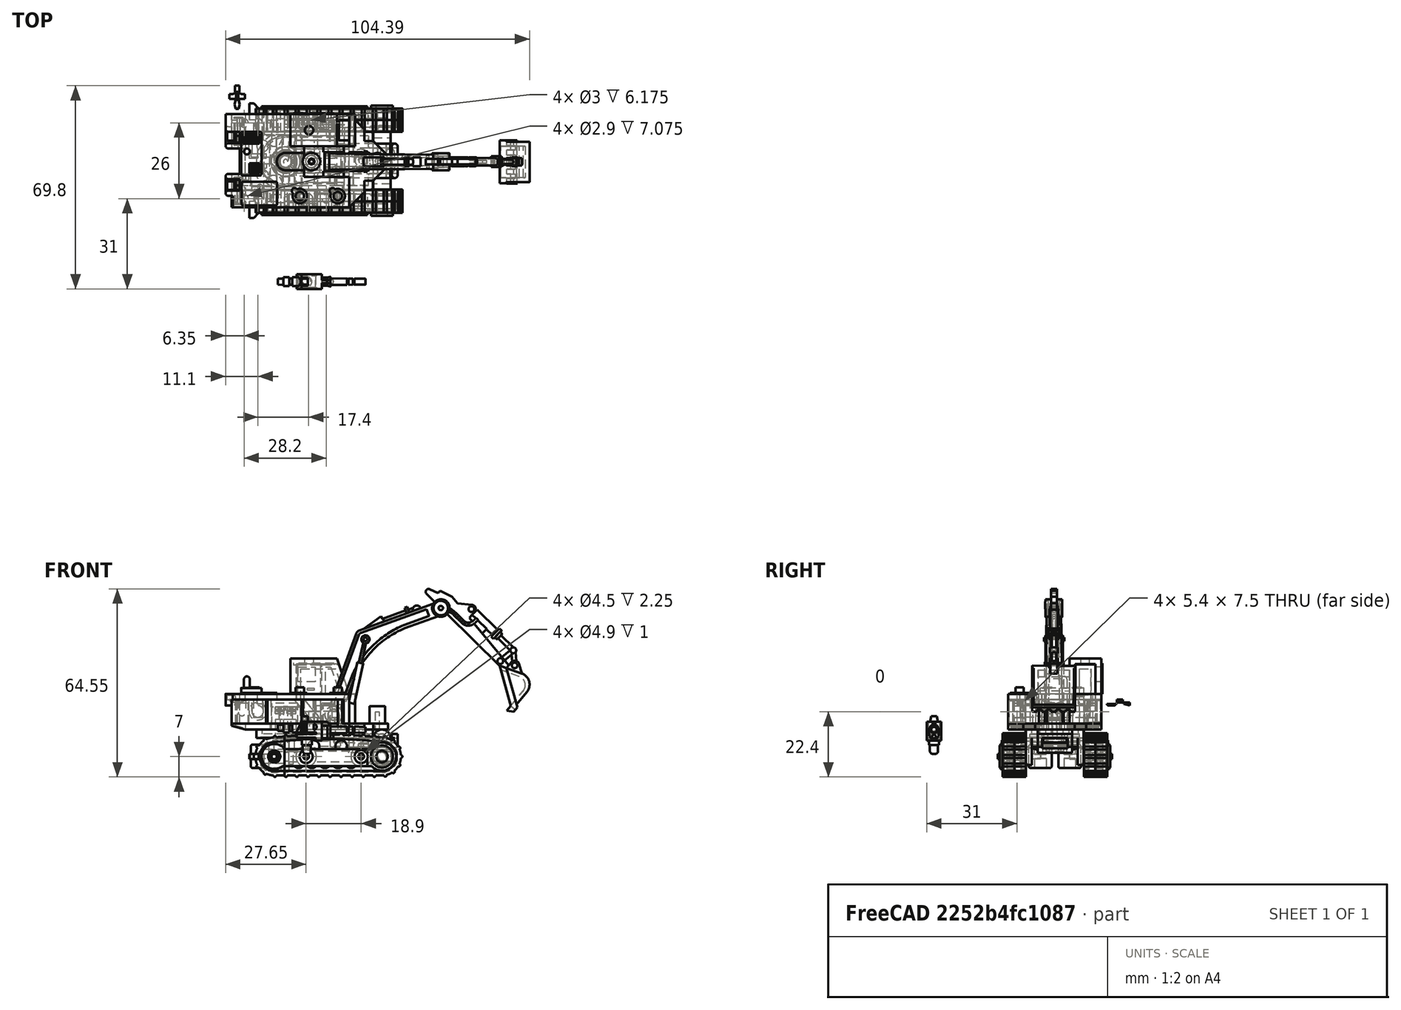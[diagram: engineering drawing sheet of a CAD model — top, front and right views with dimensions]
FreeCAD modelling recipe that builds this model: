
FCSTD DOCUMENT  (FreeCAD 1.0R39109 (Git))
Label: Scavanger
License: All rights reserved
LicenseURL: https://en.wikipedia.org/wiki/All_rights_reserved
objects: Sketcher::SketchObject×284, PartDesign::Pad×196, PartDesign::Pocket×128, PartDesign::Body×18, PartDesign::Fillet×15, PartDesign::SubShapeBinder×11, PartDesign::Chamfer×8, App::Link×5, Part::Mirroring×5, App::Part×1, Part::Feature×1
note: 1644 computed .brp shape members not serialized (recipe doc carries the construction recipe); baked Part::Feature solids carry a one-line shape summary decoded from their .brp

FEATURE [Sketcher::SketchObject] Sketch
  ArcFitTolerance = 1e-06
  AttachmentSupport = -> [XY_Plane]
  FullyConstrained = true
  MakeInternals = false
  MapMode = 5
  sketch-geometry (43):
    g0: LineSegment StartX=0 StartY=0 StartZ=0 EndX=44.5 EndY=0 EndZ=0
    g1: LineSegment StartX=44.5 StartY=0 StartZ=0 EndX=44.5 EndY=-11 EndZ=0
    g2: LineSegment StartX=44.5 StartY=-11 StartZ=0 EndX=27 EndY=-11 EndZ=0
    g3: LineSegment StartX=27 StartY=-11 StartZ=0 EndX=27 EndY=-13.25 EndZ=0
    g4: LineSegment StartX=27 StartY=-13.25 StartZ=0 EndX=20.6 EndY=-13.25 EndZ=0
    g5: ArcOfCircle CenterX=20.6 CenterY=-16.25 CenterZ=0 NormalX=0 NormalY=0 NormalZ=1 AngleXU=0 Radius=3 StartAngle=1.5708 EndAngle=4.71239
    g6: LineSegment StartX=20.6 StartY=-19.25 StartZ=0 EndX=27 EndY=-19.25 EndZ=0
    g7: LineSegment StartX=27 StartY=-19.25 StartZ=0 EndX=27 EndY=-21.5 EndZ=0
    g8: LineSegment StartX=27 StartY=-21.5 StartZ=0 EndX=42.5 EndY=-21.5 EndZ=0
    g9: LineSegment StartX=42.5 StartY=-21.5 StartZ=0 EndX=42.5 EndY=-32 EndZ=0
    g10: LineSegment StartX=42.5 StartY=-32 StartZ=0 EndX=2.5 EndY=-32 EndZ=0
    g11: LineSegment StartX=2.5 StartY=-32 StartZ=0 EndX=2.5 EndY=-28 EndZ=0
    g12: LineSegment StartX=2.5 StartY=-28 StartZ=0 EndX=0.875 EndY=-28 EndZ=0
    g13: ArcOfCircle CenterX=0.875 CenterY=-27.125 CenterZ=0 NormalX=0 NormalY=0 NormalZ=1 AngleXU=0 Radius=0.875 StartAngle=1.5708 EndAngle=4.71239
    g14: LineSegment StartX=0.875 StartY=-26.25 StartZ=0 EndX=4.8 EndY=-26.25 EndZ=0
    g15: LineSegment StartX=4.8 StartY=-26.25 StartZ=0 EndX=4.8 EndY=-22.25 EndZ=0
    g16: LineSegment StartX=4.8 StartY=-22.25 StartZ=0 EndX=0.875 EndY=-22.25 EndZ=0
    g17: ArcOfCircle CenterX=0.875 CenterY=-21.375 CenterZ=0 NormalX=0 NormalY=0 NormalZ=1 AngleXU=0 Radius=0.875 StartAngle=1.5708 EndAngle=4.71239
    g18: LineSegment StartX=0.875 StartY=-20.5 StartZ=0 EndX=4.8 EndY=-20.5 EndZ=0
    g19: LineSegment StartX=4.8 StartY=-20.5 StartZ=0 EndX=4.8 EndY=-11.75 EndZ=0
    g20: LineSegment StartX=4.8 StartY=-11.75 StartZ=0 EndX=0.875 EndY=-11.75 EndZ=0
    g21: ArcOfCircle CenterX=0.875 CenterY=-10.875 CenterZ=0 NormalX=0 NormalY=0 NormalZ=1 AngleXU=0 Radius=0.875 StartAngle=1.5708 EndAngle=4.71239
    g22: LineSegment StartX=0.875 StartY=-10 StartZ=0 EndX=4.8 EndY=-10 EndZ=0
    g23: LineSegment StartX=4.8 StartY=-10 StartZ=0 EndX=4.8 EndY=-6 EndZ=0
    g24: LineSegment StartX=4.8 StartY=-6 StartZ=0 EndX=0.875 EndY=-6 EndZ=0
    g25: ArcOfCircle CenterX=0.875 CenterY=-5.125 CenterZ=0 NormalX=0 NormalY=0 NormalZ=1 AngleXU=0 Radius=0.875 StartAngle=3.14159 EndAngle=4.71239
    g26: LineSegment StartX=0 StartY=0 StartZ=0 EndX=0 EndY=-5.125 EndZ=0
    g27: LineSegment [constr] StartX=0.875 StartY=-10 StartZ=0 EndX=0.875 EndY=-10.875 EndZ=0
    g28: LineSegment [constr] StartX=0.875 StartY=-10.875 StartZ=0 EndX=0.875 EndY=-11.75 EndZ=0
    g29: LineSegment [constr] StartX=0.875 StartY=-20.5 StartZ=0 EndX=0.875 EndY=-21.375 EndZ=0
    g30: LineSegment [constr] StartX=0.875 StartY=-21.375 StartZ=0 EndX=0.875 EndY=-22.25 EndZ=0
    g31: LineSegment [constr] StartX=0.875 StartY=-26.25 StartZ=0 EndX=0.875 EndY=-27.125 EndZ=0
    g32: LineSegment [constr] StartX=0.875 StartY=-27.125 StartZ=0 EndX=0.875 EndY=-28 EndZ=0
    g33: LineSegment [constr] StartX=27 StartY=-13.25 StartZ=0 EndX=27 EndY=-19.25 EndZ=0
    g34: LineSegment [constr] StartX=20.6 StartY=-13.25 StartZ=0 EndX=17.6 EndY=-13.25 EndZ=0
    g35: LineSegment [constr] StartX=17.6 StartY=-13.25 StartZ=0 EndX=17.6 EndY=-16.25 EndZ=0
    g36: LineSegment [constr] StartX=20.6 StartY=-13.25 StartZ=0 EndX=20.6 EndY=-19.25 EndZ=0
    g37: LineSegment [constr] StartX=4.8 StartY=-10 StartZ=0 EndX=4.8 EndY=-11.75 EndZ=0
    g38: LineSegment [constr] StartX=4.8 StartY=-20.5 StartZ=0 EndX=4.8 EndY=-22.25 EndZ=0
    g39: LineSegment StartX=42.5 StartY=-2 StartZ=0 EndX=24.3 EndY=-2 EndZ=0
    g40: LineSegment StartX=24.3 StartY=-2 StartZ=0 EndX=24.3 EndY=-9 EndZ=0
    g41: LineSegment StartX=24.3 StartY=-9 StartZ=0 EndX=42.5 EndY=-9 EndZ=0
    g42: LineSegment StartX=42.5 StartY=-9 StartZ=0 EndX=42.5 EndY=-2 EndZ=0
  constraints (123):
    c: Coincident(g0,g-1)
    c: PointOnObject(g0,g-1)
    c: Coincident(g1,g0)
    c: Vertical(g1)
    c: DistanceX(g0,g0) = 44.5
    c: Coincident(g2,g1)
    c: Horizontal(g2)
    c: Coincident(g3,g2)
    c: Vertical(g3)
    c: Coincident(g4,g3)
    c: Horizontal(g4)
    c: Coincident(g5,g4)
    c: Coincident(g6,g5)
    c: Horizontal(g6)
    c: Coincident(g7,g6)
    c: Vertical(g7)
    c: Coincident(g8,g7)
    c: Horizontal(g8)
    c: Coincident(g9,g8)
    c: Vertical(g9)
    c: Coincident(g10,g9)
    c: Horizontal(g10)
    c: Coincident(g11,g10)
    c: Vertical(g11)
    c: Coincident(g12,g11)
    c: Horizontal(g12)
    c: Coincident(g13,g12)
    c: Coincident(g14,g13)
    c: Coincident(g15,g14)
    c: Vertical(g15)
    c: Coincident(g16,g15)
    c: Horizontal(g16)
    c: Coincident(g17,g16)
    c: Coincident(g18,g17)
    c: Horizontal(g18)
    c: Coincident(g19,g18)
    c: Vertical(g19)
    c: Coincident(g20,g19)
    c: Horizontal(g20)
    c: Coincident(g21,g20)
    c: Coincident(g22,g21)
    c: Horizontal(g22)
    c: Coincident(g23,g22)
    c: Vertical(g23)
    c: Coincident(g24,g23)
    c: Horizontal(g24)
    c: Coincident(g25,g24)
    c: PointOnObject(g25,g-2)
    c: Coincident(g26,g0)
    c: Coincident(g26,g25)
    c: DistanceY(g1,g1) = 11
    c: Horizontal(g14)
    c: DistanceX(g10,g10) = 40
    c: Diameter(g5) = 6
    c: Diameter(g17) = 1.75
    c: Diameter(g21) = 1.75
    c: Diameter(g13) = 1.75
    c: Tangent(g17,g-2)
    c: Tangent(g21,g-2)
    c: Diameter(g25) = 1.75
    c: DistanceX(g25,g24) = 0
    c: DistanceY(g25,g25) = 0
    c: Coincident(g27,g21)
    c: Coincident(g27,g21)
    c: Coincident(g28,g21)
    c: Coincident(g28,g20)
    c: Vertical(g27)
    c: Vertical(g28)
    c: Tangent(g13,g-2)
    c: Coincident(g29,g17)
    c: Coincident(g29,g17)
    c: Coincident(g30,g17)
    c: Coincident(g30,g16)
    c: Coincident(g31,g13)
    c: Coincident(g31,g13)
    c: Coincident(g32,g13)
    c: Coincident(g32,g12)
    c: Vertical(g29)
    c: Vertical(g30)
    c: Vertical(g31)
    c: Vertical(g32)
    c: DistanceX(g2,g2) = 17.5
    c: DistanceY(g7,g2) = 10.5
    c: Coincident(g33,g3)
    c: Coincident(g33,g6)
    c: Vertical(g33)
    c: DistanceY(g3,g2) = 2.25
    c: Coincident(g34,g4)
    c: Horizontal(g34)
    c: Tangent(g34,g5)
    c: Coincident(g35,g34)
    c: Tangent(g35,g5) = -1.5708
    c: Vertical(g35)
    c: Coincident(g36,g4)
    c: Coincident(g36,g5)
    c: Vertical(g36)
    c: DistanceX(g35,g1) = 26.9
    c: DistanceX(g8,g8) = 15.5
    c: DistanceY(g9,g9) = 10.5
    c: DistanceY(g11,g11) = 4
    c: Coincident(g37,g22)
    c: Coincident(g37,g19)
    c: Vertical(g37)
    c: Coincident(g38,g18)
    c: Coincident(g38,g15)
    c: Vertical(g38)
    c: DistanceY(g24,g0) = 6
    c: DistanceY(g23,g23) = 4
    c: DistanceY(g15,g15) = 4
    c: DistanceX(g25,g23) = 4.8
    c: DistanceX(g19,g35) = 12.8
    c: Coincident(g39,g40)
    c: Coincident(g40,g41)
    c: Coincident(g41,g42)
    c: Coincident(g42,g39)
    c: Horizontal(g39)
    c: Horizontal(g41)
    c: Vertical(g40)
    c: Vertical(g42)
    c: DistanceX(g39,g0) = 2
    c: DistanceY(g39,g0) = 2
    c: DistanceY(g1,g41) = 2
    c: DistanceX(g39,g39) = 18.2
FEATURE [PartDesign::Pad] Pad
  Direction = (0,0,1)
  Length = 2
  Length2 = 10
  Profile = -> Sketch
  ReferenceAxis = -> Sketch [N_Axis]
  Refine = true
  Suppressed = false
  Type = 0
FEATURE [Sketcher::SketchObject] Sketch001
  ArcFitTolerance = 1e-06
  AttachmentSupport = -> [Pad]
  ExternalGeometry = -> [Pad]
  FullyConstrained = true
  MakeInternals = false
  MapMode = 5
  Placement = pos=(0,0,0) rot=(0,0.707107,0.707107;3.14159rad)
  sketch-geometry (4):
    g0: LineSegment StartX=-42.5 StartY=2 StartZ=0 EndX=-38.2 EndY=14.2 EndZ=0
    g1: LineSegment StartX=-38.2 StartY=14.2 StartZ=0 EndX=-22.3 EndY=14.2 EndZ=0
    g2: LineSegment StartX=-22.3 StartY=14.2 StartZ=0 EndX=-22.3 EndY=2 EndZ=0
    g3: LineSegment StartX=-22.3 StartY=2 StartZ=0 EndX=-42.5 EndY=2 EndZ=0
  constraints (12):
    c: Coincident(g0,g-5)
    c: Coincident(g1,g0)
    c: Horizontal(g1)
    c: DistanceY(g-6,g1) = 12.2
    c: DistanceX(g1,g1) = 15.9
    c: Coincident(g2,g1)
    c: PointOnObject(g2,g-3)
    c: Vertical(g2)
    c: DistanceX(g0,g2) = 20.2
    c: DistanceX(g-6,g2) = 2
    c: Coincident(g3,g2)
    c: Coincident(g3,g0)
FEATURE [PartDesign::Pad] Pad001
  BaseFeature = -> Pad
  Direction = (0,1,-2e-16)
  Length = 2
  Length2 = 10
  Profile = -> Sketch001
  ReferenceAxis = -> Sketch001 [N_Axis]
  Refine = true
  Reversed = true
  Suppressed = false
  Type = 0
FEATURE [Sketcher::SketchObject] Sketch002
  ArcFitTolerance = 1e-06
  AttachmentSupport = -> [Pad001]
  ExternalGeometry = -> [Pad001]
  FullyConstrained = true
  MakeInternals = false
  MapMode = 5
  Placement = pos=(0,-11,0) rot=(1,0,0;1.5708rad)
  sketch-geometry (4):
    g0: LineSegment StartX=22.3 StartY=2 StartZ=0 EndX=42.5 EndY=2 EndZ=0
    g1: LineSegment StartX=42.5 StartY=2 StartZ=0 EndX=38.2 EndY=14.2 EndZ=0
    g2: LineSegment StartX=38.2 StartY=14.2 StartZ=0 EndX=22.3 EndY=14.2 EndZ=0
    g3: LineSegment StartX=22.3 StartY=14.2 StartZ=0 EndX=22.3 EndY=2 EndZ=0
  constraints (8):
    c: Coincident(g0,g-4)
    c: Coincident(g0,g-3)
    c: Coincident(g1,g0)
    c: Coincident(g1,g-5)
    c: Coincident(g2,g1)
    c: Coincident(g2,g-5)
    c: Coincident(g3,g2)
    c: Coincident(g3,g0)
FEATURE [PartDesign::Pad] Pad002
  BaseFeature = -> Pad001
  Direction = (0,-1,2e-16)
  Length = 2
  Length2 = 10
  Profile = -> Sketch002
  ReferenceAxis = -> Sketch002 [N_Axis]
  Refine = true
  Reversed = true
  Suppressed = false
  Type = 0
FEATURE [Sketcher::SketchObject] Sketch003
  ArcFitTolerance = 1e-06
  AttachmentSupport = -> [Pad002]
  ExternalGeometry = -> [Pad002]
  FullyConstrained = true
  MakeInternals = false
  MapMode = 5
  Placement = pos=(0,0,2) rot=(0,0,1;0rad)
  sketch-geometry (4):
    g0: LineSegment StartX=24.3 StartY=-2 StartZ=0 EndX=22.3 EndY=-2 EndZ=0
    g1: LineSegment StartX=22.3 StartY=-2 StartZ=0 EndX=22.3 EndY=-9 EndZ=0
    g2: LineSegment StartX=22.3 StartY=-9 StartZ=0 EndX=24.3 EndY=-9 EndZ=0
    g3: LineSegment StartX=24.3 StartY=-9 StartZ=0 EndX=24.3 EndY=-2 EndZ=0
  constraints (10):
    c: Coincident(g0,g1)
    c: Coincident(g1,g2)
    c: Coincident(g2,g3)
    c: Coincident(g3,g0)
    c: Horizontal(g0)
    c: Horizontal(g2)
    c: Vertical(g1)
    c: Vertical(g3)
    c: Coincident(g0,g-4)
    c: Coincident(g1,g-5)
FEATURE [PartDesign::Pad] Pad003
  BaseFeature = -> Pad002
  Direction = (0,0,1)
  Length = 12.2
  Length2 = 10
  Profile = -> Sketch003
  ReferenceAxis = -> Sketch003 [N_Axis]
  Refine = true
  Suppressed = false
  Type = 0
FEATURE [Sketcher::SketchObject] Sketch004
  ArcFitTolerance = 1e-06
  AttachmentSupport = -> [Pad003]
  ExternalGeometry = -> [Pad003]
  FullyConstrained = true
  MakeInternals = false
  MapMode = 5
  Placement = pos=(0,-2,0) rot=(1,0,0;1.5708rad)
  sketch-geometry (4):
    g0: LineSegment StartX=24.3 StartY=14.2 StartZ=0 EndX=38.2 EndY=14.2 EndZ=0
    g1: LineSegment StartX=38.2 StartY=14.2 StartZ=0 EndX=38.9049 EndY=12.2 EndZ=0
    g2: LineSegment StartX=38.9049 StartY=12.2 StartZ=0 EndX=24.3 EndY=12.2 EndZ=0
    g3: LineSegment StartX=24.3 StartY=12.2 StartZ=0 EndX=24.3 EndY=14.2 EndZ=0
  constraints (10):
    c: Coincident(g0,g-3)
    c: Coincident(g0,g-4)
    c: Coincident(g1,g0)
    c: PointOnObject(g1,g-4)
    c: Coincident(g2,g1)
    c: Horizontal(g2)
    c: Coincident(g3,g2)
    c: Vertical(g3)
    c: Coincident(g3,g0)
    c: DistanceY(g3,g3) = 2
FEATURE [PartDesign::Pad] Pad004
  BaseFeature = -> Pad003
  Direction = (0,-1,2e-16)
  Length = 7
  Length2 = 10
  Profile = -> Sketch004
  ReferenceAxis = -> Sketch004 [N_Axis]
  Refine = true
  Suppressed = false
  Type = 0
FEATURE [Sketcher::SketchObject] Sketch005
  ArcFitTolerance = 1e-06
  AttachmentSupport = -> [Pad004]
  ExternalGeometry = -> [Pad004]
  FullyConstrained = true
  MakeInternals = false
  MapMode = 5
  Placement = pos=(0,0,0) rot=(1,0,0;3.14159rad)
  sketch-geometry (17):
    g0: ArcOfCircle CenterX=0.875 CenterY=27.125 CenterZ=0 NormalX=0 NormalY=0 NormalZ=1 AngleXU=0 Radius=0.875 StartAngle=1.5708 EndAngle=3.14159
    g1: ArcOfCircle CenterX=0.875 CenterY=21.375 CenterZ=0 NormalX=0 NormalY=0 NormalZ=1 AngleXU=0 Radius=0.875 StartAngle=3.14159 EndAngle=4.71239
    g2: LineSegment [constr] StartX=0.875 StartY=21.375 StartZ=0 EndX=-1e-16 EndY=21.375 EndZ=0
    g3: LineSegment [constr] StartX=0.875 StartY=27.125 StartZ=0 EndX=0 EndY=27.125 EndZ=0
    g4: LineSegment StartX=0 StartY=27.125 StartZ=0 EndX=-1e-16 EndY=21.375 EndZ=0
    g5: LineSegment StartX=0.875 StartY=20.5 StartZ=0 EndX=2 EndY=20.5 EndZ=0
    g6: LineSegment StartX=2 StartY=20.5 StartZ=0 EndX=2 EndY=28 EndZ=0
    g7: LineSegment StartX=2 StartY=28 StartZ=0 EndX=0.875 EndY=28 EndZ=0
    g8: ArcOfCircle CenterX=0.875 CenterY=10.875 CenterZ=0 NormalX=0 NormalY=0 NormalZ=1 AngleXU=0 Radius=0.875 StartAngle=1.5708 EndAngle=3.14159
    g9: LineSegment StartX=2 StartY=4.25 StartZ=0 EndX=2 EndY=11.75 EndZ=0
    g10: LineSegment StartX=2 StartY=11.75 StartZ=0 EndX=0.875 EndY=11.75 EndZ=0
    g11: LineSegment [constr] StartX=0.875 StartY=10.875 StartZ=0 EndX=1.5096e-12 EndY=10.875 EndZ=0
    g12: LineSegment StartX=1.5096e-12 StartY=10.875 StartZ=0 EndX=1.5096e-12 EndY=5.125 EndZ=0
    g13: ArcOfCircle CenterX=0.875 CenterY=5.125 CenterZ=0 NormalX=0 NormalY=0 NormalZ=1 AngleXU=0 Radius=0.875 StartAngle=3.14159 EndAngle=4.71239
    g14: LineSegment [constr] StartX=0.875 StartY=5.125 StartZ=0 EndX=1.5096e-12 EndY=5.125 EndZ=0
    g15: LineSegment [constr] StartX=0.875 StartY=5.125 StartZ=0 EndX=0.875 EndY=4.25 EndZ=0
    g16: LineSegment StartX=0.875 StartY=4.25 StartZ=0 EndX=2 EndY=4.25 EndZ=0
  constraints (44):
    c: Tangent(g0,g-3) = -1.5708
    c: PointOnObject(g0,g-3)
    c: Tangent(g1,g-4) = -1.5708
    c: PointOnObject(g1,g-4)
    c: Coincident(g2,g1)
    c: Coincident(g2,g1)
    c: Horizontal(g2)
    c: Coincident(g3,g0)
    c: Coincident(g3,g0)
    c: Horizontal(g3)
    c: Coincident(g4,g0)
    c: Coincident(g4,g1)
    c: Coincident(g5,g1)
    c: Horizontal(g5)
    c: Coincident(g6,g5)
    c: Vertical(g6)
    c: Coincident(g7,g6)
    c: Coincident(g7,g0)
    c: Horizontal(g7)
    c: Tangent(g8,g-5) = -1.5708
    c: PointOnObject(g8,g-5)
    c: Vertical(g9)
    c: Coincident(g10,g9)
    c: Coincident(g10,g8)
    c: Horizontal(g10)
    c: Coincident(g11,g8)
    c: Coincident(g11,g8)
    c: Coincident(g12,g8)
    c: Coincident(g12,g-6)
    c: Vertical(g12)
    c: Coincident(g13,g12)
    c: Coincident(g14,g-6)
    c: Coincident(g14,g12)
    c: Coincident(g15,g14)
    c: Coincident(g15,g13)
    c: Vertical(g15)
    c: Radius(g-6) = 0.875
    c: Radius(g-5) = 0.875
    c: Coincident(g13,g14)
    c: Coincident(g16,g13)
    c: Coincident(g16,g9)
    c: Horizontal(g16)
    c: DistanceX(g0,g6) = 2
    c: DistanceX(g12,g9) = 2
FEATURE [PartDesign::Pad] Pad005
  BaseFeature = -> Pad004
  Direction = (0,0,-1)
  Length = 2
  Length2 = 10
  Profile = -> Sketch005
  ReferenceAxis = -> Sketch005 [N_Axis]
  Refine = true
  Suppressed = false
  Type = 0
FEATURE [Sketcher::SketchObject] Sketch006
  ArcFitTolerance = 1e-06
  AttachmentSupport = -> [Pad005]
  FullyConstrained = true
  MakeInternals = false
  MapMode = 5
  Placement = pos=(0,0,2) rot=(0,0,1;0rad)
  sketch-geometry (12):
    g0: LineSegment StartX=5.3 StartY=-6.5 StartZ=0 EndX=5.3 EndY=-20.5 EndZ=0
    g1: LineSegment StartX=5.8 StartY=-21 StartZ=0 EndX=11.8 EndY=-21 EndZ=0
    g2: LineSegment StartX=12.3 StartY=-20.5 StartZ=0 EndX=12.3 EndY=-6.5 EndZ=0
    g3: LineSegment StartX=11.8 StartY=-6 StartZ=0 EndX=5.8 EndY=-6 EndZ=0
    g4: ArcOfCircle CenterX=5.8 CenterY=-6.5 CenterZ=0 NormalX=0 NormalY=0 NormalZ=1 AngleXU=0 Radius=0.5 StartAngle=1.5708 EndAngle=3.14159
    g5: GeomPoint [constr] X=5.3 Y=-6 Z=0
    g6: ArcOfCircle CenterX=11.8 CenterY=-6.5 CenterZ=0 NormalX=0 NormalY=0 NormalZ=1 AngleXU=0 Radius=0.5 StartAngle=0 EndAngle=1.5708
    g7: GeomPoint [constr] X=12.3 Y=-6 Z=0
    g8: ArcOfCircle CenterX=11.8 CenterY=-20.5 CenterZ=0 NormalX=0 NormalY=0 NormalZ=1 AngleXU=0 Radius=0.5 StartAngle=4.71239 EndAngle=6.28319
    g9: GeomPoint [constr] X=12.3 Y=-21 Z=0
    g10: ArcOfCircle CenterX=5.8 CenterY=-20.5 CenterZ=0 NormalX=0 NormalY=0 NormalZ=1 AngleXU=0 Radius=0.5 StartAngle=3.14159 EndAngle=4.71239
    g11: GeomPoint [constr] X=5.3 Y=-21 Z=0
  constraints (28):
    c: Vertical(g0)
    c: Vertical(g2)
    c: Horizontal(g1)
    c: Horizontal(g3)
    c: PointOnObject(g5,g0)
    c: PointOnObject(g5,g3)
    c: Tangent(g0,g4) = -1.5708
    c: Tangent(g3,g4) = -1.5708
    c: PointOnObject(g7,g2)
    c: PointOnObject(g7,g3)
    c: Tangent(g2,g6) = -1.5708
    c: Tangent(g3,g6) = -1.5708
    c: PointOnObject(g9,g1)
    c: PointOnObject(g9,g2)
    c: Tangent(g1,g8) = -1.5708
    c: Tangent(g2,g8) = -1.5708
    c: PointOnObject(g11,g0)
    c: PointOnObject(g11,g1)
    c: Tangent(g0,g10) = -1.5708
    c: Tangent(g1,g10) = -1.5708
    c: Radius(g4) = 0.5
    c: Radius(g6) = 0.5
    c: Radius(g10) = 0.5
    c: Radius(g8) = 0.5
    c: DistanceY(g1,g3) = 15
    c: DistanceX(g0,g2) = 7
    c: DistanceY(g3,g-1) = 6
    c: DistanceX(g-1,g0) = 5.3
FEATURE [PartDesign::Pad] Pad006
  BaseFeature = -> Pad005
  Direction = (0,0,1)
  Length = 2
  Length2 = 10
  Profile = -> Sketch006
  ReferenceAxis = -> Sketch006 [N_Axis]
  Refine = true
  Suppressed = false
  Type = 0
FEATURE [Sketcher::SketchObject] Sketch007
  ArcFitTolerance = 1e-06
  AttachmentSupport = -> [Pad006]
  ExternalGeometry = -> [Pad006]
  FullyConstrained = true
  MakeInternals = false
  MapMode = 5
  Placement = pos=(0,0,4) rot=(0,0,1;0rad)
  sketch-geometry (4):
    g0: Circle CenterX=7.3 CenterY=-12.8 CenterZ=0 NormalX=0 NormalY=0 NormalZ=1 AngleXU=0 Radius=1
    g1: LineSegment [constr] StartX=7.3 StartY=-12.8 StartZ=0 EndX=7.3 EndY=-13.8 EndZ=0
    g2: LineSegment [constr] StartX=7.3 StartY=-12.8 StartZ=0 EndX=7.3 EndY=-11.8 EndZ=0
    g3: LineSegment [constr] StartX=7.3 StartY=-12.8 StartZ=0 EndX=6.3 EndY=-12.8 EndZ=0
  constraints (12):
    c: Diameter(g0) = 2
    c: Coincident(g1,g0)
    c: PointOnObject(g1,g0)
    c: Vertical(g1)
    c: Coincident(g2,g0)
    c: PointOnObject(g2,g0)
    c: Vertical(g2)
    c: DistanceY(g2,g-1) = 11.8
    c: Coincident(g3,g0)
    c: PointOnObject(g3,g0)
    c: Horizontal(g3)
    c: DistanceX(g-3,g3) = 1
FEATURE [PartDesign::Pad] Pad007
  BaseFeature = -> Pad006
  Direction = (0,0,1)
  Length = 4
  Length2 = 10
  Profile = -> Sketch007
  ReferenceAxis = -> Sketch007 [N_Axis]
  Refine = true
  Suppressed = false
  Type = 0
FEATURE [PartDesign::Fillet] Fillet
  Base = -> Pad007 [Edge171]
  BaseFeature = -> Pad007
  Radius = 1
  Refine = true
  SupportTransform = false
  Suppressed = false
  UseAllEdges = false
FEATURE [Sketcher::SketchObject] Sketch008
  ArcFitTolerance = 1e-06
  AttachmentSupport = -> [Fillet]
  ExternalGeometry = -> [Fillet]
  FullyConstrained = true
  MakeInternals = false
  MapMode = 5
  Placement = pos=(0,0,4) rot=(0,0,1;0rad)
  sketch-geometry (16):
    g0: LineSegment StartX=11.6 StartY=-6.7 StartZ=0 EndX=6 EndY=-6.7 EndZ=0
    g1: LineSegment StartX=6 StartY=-6.7 StartZ=0 EndX=6 EndY=-10.1 EndZ=0
    g2: LineSegment StartX=6 StartY=-10.1 StartZ=0 EndX=11.6 EndY=-10.1 EndZ=0
    g3: LineSegment StartX=11.6 StartY=-10.1 StartZ=0 EndX=11.6 EndY=-6.7 EndZ=0
    g4: LineSegment StartX=11.4 StartY=-6.9 StartZ=0 EndX=6.2 EndY=-6.9 EndZ=0
    g5: LineSegment StartX=6.2 StartY=-6.9 StartZ=0 EndX=6.2 EndY=-9.9 EndZ=0
    g6: LineSegment StartX=6.2 StartY=-9.9 StartZ=0 EndX=11.4 EndY=-9.9 EndZ=0
    g7: LineSegment StartX=11.4 StartY=-9.9 StartZ=0 EndX=11.4 EndY=-6.9 EndZ=0
    g8: LineSegment StartX=11.6 StartY=-16.9 StartZ=0 EndX=8.2 EndY=-16.9 EndZ=0
    g9: LineSegment StartX=8.2 StartY=-16.9 StartZ=0 EndX=8.2 EndY=-20.3 EndZ=0
    g10: LineSegment StartX=8.2 StartY=-20.3 StartZ=0 EndX=11.6 EndY=-20.3 EndZ=0
    g11: LineSegment StartX=11.6 StartY=-20.3 StartZ=0 EndX=11.6 EndY=-16.9 EndZ=0
    g12: LineSegment StartX=11.4 StartY=-17.1 StartZ=0 EndX=8.4 EndY=-17.1 EndZ=0
    g13: LineSegment StartX=8.4 StartY=-17.1 StartZ=0 EndX=8.4 EndY=-20.1 EndZ=0
    g14: LineSegment StartX=8.4 StartY=-20.1 StartZ=0 EndX=11.4 EndY=-20.1 EndZ=0
    g15: LineSegment StartX=11.4 StartY=-20.1 StartZ=0 EndX=11.4 EndY=-17.1 EndZ=0
  constraints (50):
    c: Coincident(g0,g1)
    c: Coincident(g1,g2)
    c: Coincident(g2,g3)
    c: Coincident(g3,g0)
    c: Horizontal(g0)
    c: Horizontal(g2)
    c: Vertical(g1)
    c: Vertical(g3)
    c: Coincident(g4,g5)
    c: Coincident(g5,g6)
    c: Coincident(g6,g7)
    c: Coincident(g7,g4)
    c: Horizontal(g4)
    c: Horizontal(g6)
    c: Vertical(g5)
    c: Vertical(g7)
    c: Coincident(g8,g9)
    c: Coincident(g9,g10)
    c: Coincident(g10,g11)
    c: Coincident(g11,g8)
    c: Horizontal(g8)
    c: Horizontal(g10)
    c: Vertical(g9)
    c: Vertical(g11)
    c: Coincident(g12,g13)
    c: Coincident(g13,g14)
    c: Coincident(g14,g15)
    c: Coincident(g15,g12)
    c: Horizontal(g12)
    c: Horizontal(g14)
    c: Vertical(g13)
    c: Vertical(g15)
    c: DistanceX(g8,g8) = 3.4
    c: DistanceY(g9,g9) = 3.4
    c: DistanceX(g8,g12) = 0.2
    c: DistanceX(g12,g8) = 0.2
    c: DistanceY(g12,g8) = 0.2
    c: DistanceY(g9,g13) = 0.2
    c: DistanceX(g6,g2) = 0.2
    c: DistanceX(g1,g5) = 0.2
    c: DistanceY(g1,g5) = 0.2
    c: DistanceY(g4,g0) = 0.2
    c: DistanceX(g0,g0) = 5.6
    c: DistanceY(g1,g1) = 3.4
    c: DistanceX(g-4,g-3) = 7
    c: DistanceX(g-4,g0) = 0.7
    c: DistanceY(g0,g-5) = 0.7
    c: DistanceY(g-6,g10) = 0.7
    c: DistanceX(g10,g-3) = 0.7
    c: DistanceX(g0,g-3) = 0.7
FEATURE [PartDesign::Pad] Pad008
  BaseFeature = -> Fillet
  Direction = (0,0,1)
  Length = 0.3
  Length2 = 10
  Profile = -> Sketch008
  ReferenceAxis = -> Sketch008 [N_Axis]
  Refine = true
  Suppressed = false
  Type = 0
FEATURE [Sketcher::SketchObject] Sketch009
  ArcFitTolerance = 1e-06
  AttachmentSupport = -> [Pad008]
  ExternalGeometry = -> [Pad008]
  FullyConstrained = true
  MakeInternals = false
  MapMode = 5
  Placement = pos=(0,0,4) rot=(0,0,1;0rad)
  sketch-geometry (197):
    g0: LineSegment [constr] StartX=11.4 StartY=-6.9 StartZ=0 EndX=8.4 EndY=-9.9 EndZ=0
    g1: LineSegment [constr] StartX=10.1 StartY=-6.9 StartZ=0 EndX=7.1 EndY=-9.9 EndZ=0
    g2: LineSegment [constr] StartX=8.8 StartY=-6.9 StartZ=0 EndX=6.2 EndY=-9.5 EndZ=0
    g3: LineSegment [constr] StartX=7.5 StartY=-6.9 StartZ=0 EndX=6.2 EndY=-8.2 EndZ=0
    g4: LineSegment [constr] StartX=11.4 StartY=-8.2 StartZ=0 EndX=9.7 EndY=-9.9 EndZ=0
    g5: LineSegment [constr] StartX=11.4 StartY=-9.5 StartZ=0 EndX=11 EndY=-9.9 EndZ=0
    g6: LineSegment [constr] StartX=6.2 StartY=-6.9 StartZ=0 EndX=9.2 EndY=-9.9 EndZ=0
    g7: LineSegment [constr] StartX=7.5 StartY=-6.9 StartZ=0 EndX=10.5 EndY=-9.9 EndZ=0
    g8: LineSegment [constr] StartX=8.8 StartY=-6.9 StartZ=0 EndX=11.4 EndY=-9.5 EndZ=0
    g9: LineSegment [constr] StartX=10.1 StartY=-6.9 StartZ=0 EndX=11.4 EndY=-8.2 EndZ=0
    g10: LineSegment [constr] StartX=6.2 StartY=-8.2 StartZ=0 EndX=7.9 EndY=-9.9 EndZ=0
    g11: LineSegment [constr] StartX=6.2 StartY=-9.5 StartZ=0 EndX=6.6 EndY=-9.9 EndZ=0
    g12: LineSegment StartX=11.4 StartY=-9.65 StartZ=0 EndX=8.65 EndY=-6.9 EndZ=0
    g13: LineSegment StartX=11.4 StartY=-9.35 StartZ=0 EndX=8.95 EndY=-6.9 EndZ=0
    g14: LineSegment StartX=11.4 StartY=-8.05 StartZ=0 EndX=10.25 EndY=-6.9 EndZ=0
    g15: LineSegment StartX=11.4 StartY=-8.35 StartZ=0 EndX=9.95 EndY=-6.9 EndZ=0
    g16: LineSegment StartX=7.65 StartY=-6.9 StartZ=0 EndX=10.65 EndY=-9.9 EndZ=0
    g17: LineSegment StartX=7.35 StartY=-6.9 StartZ=0 EndX=10.35 EndY=-9.9 EndZ=0
    g18: LineSegment StartX=6.35 StartY=-6.9 StartZ=0 EndX=9.35 EndY=-9.9 EndZ=0
    g19: LineSegment StartX=6.2 StartY=-7.05 StartZ=0 EndX=9.05 EndY=-9.9 EndZ=0
    g20: LineSegment StartX=6.2 StartY=-8.05 StartZ=0 EndX=8.05 EndY=-9.9 EndZ=0
    g21: LineSegment StartX=6.2 StartY=-8.35 StartZ=0 EndX=7.75 EndY=-9.9 EndZ=0
    g22: LineSegment StartX=6.75 StartY=-9.9 StartZ=0 EndX=6.2 EndY=-9.35 EndZ=0
    g23: LineSegment StartX=6.45 StartY=-9.9 StartZ=0 EndX=6.2 EndY=-9.65 EndZ=0
    g24: LineSegment StartX=10.25 StartY=-6.9 StartZ=0 EndX=9.95 EndY=-6.9 EndZ=0
    g25: LineSegment StartX=8.95 StartY=-6.9 StartZ=0 EndX=8.65 EndY=-6.9 EndZ=0
    g26: LineSegment StartX=7.65 StartY=-6.9 StartZ=0 EndX=7.35 EndY=-6.9 EndZ=0
    g27: LineSegment StartX=6.35 StartY=-6.9 StartZ=0 EndX=6.2 EndY=-6.9 EndZ=0
    g28: LineSegment StartX=6.2 StartY=-6.9 StartZ=0 EndX=6.2 EndY=-7.05 EndZ=0
    g29: LineSegment StartX=6.2 StartY=-8.05 StartZ=0 EndX=6.2 EndY=-8.35 EndZ=0
    g30: LineSegment StartX=6.2 StartY=-9.35 StartZ=0 EndX=6.2 EndY=-9.65 EndZ=0
    g31: LineSegment StartX=6.45 StartY=-9.9 StartZ=0 EndX=6.75 EndY=-9.9 EndZ=0
    g32: LineSegment StartX=7.75 StartY=-9.9 StartZ=0 EndX=8.05 EndY=-9.9 EndZ=0
    g33: LineSegment StartX=9.05 StartY=-9.9 StartZ=0 EndX=9.35 EndY=-9.9 EndZ=0
    g34: LineSegment StartX=10.35 StartY=-9.9 StartZ=0 EndX=10.65 EndY=-9.9 EndZ=0
    g35: LineSegment StartX=11.4 StartY=-9.65 StartZ=0 EndX=11.4 EndY=-9.35 EndZ=0
    g36: LineSegment StartX=11.4 StartY=-8.35 StartZ=0 EndX=11.4 EndY=-8.05 EndZ=0
    g37: LineSegment StartX=9.88358 StartY=-8.275 StartZ=0 EndX=9.525 EndY=-8.63358 EndZ=0
    g38: LineSegment StartX=10.025 StartY=-8.41642 StartZ=0 EndX=9.66642 EndY=-8.775 EndZ=0
    g39: LineSegment StartX=10.5336 StartY=-7.625 StartZ=0 EndX=10.175 EndY=-7.98358 EndZ=0
    g40: LineSegment StartX=10.675 StartY=-7.76642 StartZ=0 EndX=10.3164 EndY=-8.125 EndZ=0
    g41: LineSegment StartX=11.1856 StartY=-6.97295 StartZ=0 EndX=10.825 EndY=-7.33358 EndZ=0
    g42: LineSegment StartX=11.327 StartY=-7.11438 StartZ=0 EndX=10.9664 EndY=-7.475 EndZ=0
    g43: LineSegment StartX=9.88358 StartY=-6.975 StartZ=0 EndX=9.525 EndY=-7.33358 EndZ=0
    g44: LineSegment StartX=10.025 StartY=-7.11642 StartZ=0 EndX=9.66642 EndY=-7.475 EndZ=0
    g45: LineSegment StartX=9.23358 StartY=-7.625 StartZ=0 EndX=8.875 EndY=-7.98358 EndZ=0
    g46: LineSegment StartX=9.375 StartY=-7.76642 StartZ=0 EndX=9.01642 EndY=-8.125 EndZ=0
    g47: LineSegment StartX=8.58358 StartY=-8.275 StartZ=0 EndX=8.225 EndY=-8.63358 EndZ=0
    g48: LineSegment StartX=8.725 StartY=-8.41642 StartZ=0 EndX=8.36642 EndY=-8.775 EndZ=0
    g49: LineSegment StartX=9.23358 StartY=-8.925 StartZ=0 EndX=8.875 EndY=-9.28358 EndZ=0
    g50: LineSegment StartX=9.375 StartY=-9.06642 StartZ=0 EndX=9.01642 EndY=-9.425 EndZ=0
    g51: LineSegment StartX=9.88358 StartY=-9.575 StartZ=0 EndX=9.55858 EndY=-9.9 EndZ=0
    g52: LineSegment StartX=10.025 StartY=-9.71642 StartZ=0 EndX=9.84142 EndY=-9.9 EndZ=0
    g53: LineSegment StartX=8.58358 StartY=-9.575 StartZ=0 EndX=8.25858 EndY=-9.9 EndZ=0
    g54: LineSegment StartX=8.725 StartY=-9.71642 StartZ=0 EndX=8.54142 EndY=-9.9 EndZ=0
    g55: LineSegment StartX=7.28358 StartY=-9.575 StartZ=0 EndX=6.95858 EndY=-9.9 EndZ=0
    g56: LineSegment StartX=7.425 StartY=-9.71642 StartZ=0 EndX=7.24142 EndY=-9.9 EndZ=0
    g57: LineSegment StartX=6.63358 StartY=-8.925 StartZ=0 EndX=6.275 EndY=-9.28358 EndZ=0
    g58: LineSegment StartX=6.775 StartY=-9.06642 StartZ=0 EndX=6.41642 EndY=-9.425 EndZ=0
    g59: LineSegment StartX=7.28358 StartY=-8.275 StartZ=0 EndX=6.925 EndY=-8.63358 EndZ=0
    g60: LineSegment StartX=7.425 StartY=-8.41642 StartZ=0 EndX=7.06642 EndY=-8.775 EndZ=0
    g61: LineSegment StartX=7.93358 StartY=-7.625 StartZ=0 EndX=7.575 EndY=-7.98358 EndZ=0
    g62: LineSegment StartX=8.075 StartY=-7.76642 StartZ=0 EndX=7.71642 EndY=-8.125 EndZ=0
    g63: LineSegment StartX=8.58358 StartY=-6.975 StartZ=0 EndX=8.225 EndY=-7.33358 EndZ=0
    g64: LineSegment StartX=8.725 StartY=-7.11642 StartZ=0 EndX=8.36642 EndY=-7.475 EndZ=0
    g65: LineSegment StartX=7.28358 StartY=-6.975 StartZ=0 EndX=6.925 EndY=-7.33358 EndZ=0
    g66: LineSegment StartX=7.425 StartY=-7.11642 StartZ=0 EndX=7.06642 EndY=-7.475 EndZ=0
    g67: LineSegment StartX=6.63358 StartY=-7.625 StartZ=0 EndX=6.275 EndY=-7.98358 EndZ=0
    g68: LineSegment StartX=6.775 StartY=-7.76642 StartZ=0 EndX=6.41642 EndY=-8.125 EndZ=0
    g69: LineSegment StartX=7.93358 StartY=-8.925 StartZ=0 EndX=7.575 EndY=-9.28358 EndZ=0
    g70: LineSegment StartX=8.075 StartY=-9.06642 StartZ=0 EndX=7.71642 EndY=-9.425 EndZ=0
    g71: LineSegment StartX=10.5336 StartY=-8.925 StartZ=0 EndX=10.175 EndY=-9.28358 EndZ=0
    g72: LineSegment StartX=10.675 StartY=-9.06642 StartZ=0 EndX=10.3164 EndY=-9.425 EndZ=0
    g73: LineSegment StartX=11.1836 StartY=-8.275 StartZ=0 EndX=10.825 EndY=-8.63358 EndZ=0
    g74: LineSegment StartX=11.325 StartY=-8.41642 StartZ=0 EndX=10.9664 EndY=-8.775 EndZ=0
    g75: LineSegment StartX=10.9664 StartY=-8.775 StartZ=0 EndX=10.825 EndY=-8.63358 EndZ=0
    g76: LineSegment StartX=11.325 StartY=-8.41642 StartZ=0 EndX=11.1836 EndY=-8.275 EndZ=0
    g77: LineSegment StartX=11.327 StartY=-7.11438 StartZ=0 EndX=11.1856 EndY=-6.97295 EndZ=0
    g78: LineSegment StartX=10.9664 StartY=-7.475 StartZ=0 EndX=10.825 EndY=-7.33358 EndZ=0
    g79: LineSegment StartX=10.675 StartY=-7.76642 StartZ=0 EndX=10.5336 EndY=-7.625 EndZ=0
    g80: LineSegment StartX=10.3164 StartY=-8.125 StartZ=0 EndX=10.175 EndY=-7.98358 EndZ=0
    g81: LineSegment StartX=10.025 StartY=-7.11642 StartZ=0 EndX=9.88358 EndY=-6.975 EndZ=0
    g82: LineSegment StartX=9.66642 StartY=-7.475 StartZ=0 EndX=9.525 EndY=-7.33358 EndZ=0
    g83: LineSegment StartX=9.375 StartY=-7.76642 StartZ=0 EndX=9.23358 EndY=-7.625 EndZ=0
    g84: LineSegment StartX=9.01642 StartY=-8.125 StartZ=0 EndX=8.875 EndY=-7.98358 EndZ=0
    g85: LineSegment StartX=8.36642 StartY=-7.475 StartZ=0 EndX=8.225 EndY=-7.33358 EndZ=0
    g86: LineSegment StartX=8.725 StartY=-7.11642 StartZ=0 EndX=8.58358 EndY=-6.975 EndZ=0
    g87: LineSegment StartX=8.075 StartY=-7.76642 StartZ=0 EndX=7.93358 EndY=-7.625 EndZ=0
    g88: LineSegment StartX=7.425 StartY=-7.11642 StartZ=0 EndX=7.28358 EndY=-6.975 EndZ=0
    g89: LineSegment StartX=7.06642 StartY=-7.475 StartZ=0 EndX=6.925 EndY=-7.33358 EndZ=0
    g90: LineSegment StartX=6.775 StartY=-7.76642 StartZ=0 EndX=6.63358 EndY=-7.625 EndZ=0
    g91: LineSegment StartX=6.41642 StartY=-8.125 StartZ=0 EndX=6.275 EndY=-7.98358 EndZ=0
    g92: LineSegment StartX=7.71642 StartY=-8.125 StartZ=0 EndX=7.575 EndY=-7.98358 EndZ=0
    g93: LineSegment StartX=7.425 StartY=-8.41642 StartZ=0 EndX=7.28358 EndY=-8.275 EndZ=0
    g94: LineSegment StartX=7.06642 StartY=-8.775 StartZ=0 EndX=6.925 EndY=-8.63358 EndZ=0
    g95: LineSegment StartX=6.775 StartY=-9.06642 StartZ=0 EndX=6.63358 EndY=-8.925 EndZ=0
    g96: LineSegment StartX=6.41642 StartY=-9.425 StartZ=0 EndX=6.275 EndY=-9.28358 EndZ=0
    g97: LineSegment StartX=7.425 StartY=-9.71642 StartZ=0 EndX=7.28358 EndY=-9.575 EndZ=0
    g98: LineSegment StartX=8.725 StartY=-9.71642 StartZ=0 EndX=8.58358 EndY=-9.575 EndZ=0
    g99: LineSegment StartX=8.075 StartY=-9.06642 StartZ=0 EndX=7.93358 EndY=-8.925 EndZ=0
    g100: LineSegment StartX=7.71642 StartY=-9.425 StartZ=0 EndX=7.575 EndY=-9.28358 EndZ=0
    g101: LineSegment StartX=9.01642 StartY=-9.425 StartZ=0 EndX=8.875 EndY=-9.28358 EndZ=0
    g102: LineSegment StartX=9.375 StartY=-9.06642 StartZ=0 EndX=9.23358 EndY=-8.925 EndZ=0
    g103: LineSegment StartX=8.725 StartY=-8.41642 StartZ=0 EndX=8.58358 EndY=-8.275 EndZ=0
    g104: LineSegment StartX=8.36642 StartY=-8.775 StartZ=0 EndX=8.225 EndY=-8.63358 EndZ=0
    g105: LineSegment StartX=9.66642 StartY=-8.775 StartZ=0 EndX=9.525 EndY=-8.63358 EndZ=0
    g106: LineSegment StartX=10.025 StartY=-8.41642 StartZ=0 EndX=9.88358 EndY=-8.275 EndZ=0
    g107: LineSegment StartX=10.675 StartY=-9.06642 StartZ=0 EndX=10.5336 EndY=-8.925 EndZ=0
    g108: LineSegment StartX=10.3164 StartY=-9.425 StartZ=0 EndX=10.175 EndY=-9.28358 EndZ=0
    g109: LineSegment StartX=10.025 StartY=-9.71642 StartZ=0 EndX=9.88358 EndY=-9.575 EndZ=0
    g110: LineSegment StartX=9.84142 StartY=-9.9 StartZ=0 EndX=9.55858 EndY=-9.9 EndZ=0
    g111: LineSegment StartX=8.54142 StartY=-9.9 StartZ=0 EndX=8.25858 EndY=-9.9 EndZ=0
    g112: LineSegment StartX=7.24142 StartY=-9.9 StartZ=0 EndX=6.95858 EndY=-9.9 EndZ=0
    g113: LineSegment StartX=11.1414 StartY=-9.9 StartZ=0 EndX=11.325 EndY=-9.71642 EndZ=0
    g114: LineSegment StartX=11.325 StartY=-9.71642 StartZ=0 EndX=11.1836 EndY=-9.575 EndZ=0
    g115: LineSegment StartX=11.1836 StartY=-9.575 StartZ=0 EndX=10.8586 EndY=-9.9 EndZ=0
    g116: LineSegment StartX=10.8586 StartY=-9.9 StartZ=0 EndX=11.1414 EndY=-9.9 EndZ=0
    g117: LineSegment [constr] StartX=11.4 StartY=-17.1 StartZ=0 EndX=8.4 EndY=-20.1 EndZ=0
    g118: LineSegment [constr] StartX=10.1 StartY=-17.1 StartZ=0 EndX=8.4 EndY=-18.8 EndZ=0
    g119: LineSegment [constr] StartX=8.8 StartY=-17.1 StartZ=0 EndX=8.4 EndY=-17.5 EndZ=0
    g120: LineSegment [constr] StartX=11.4 StartY=-18.4 StartZ=0 EndX=9.7 EndY=-20.1 EndZ=0
    g121: LineSegment [constr] StartX=11.4 StartY=-19.7 StartZ=0 EndX=11 EndY=-20.1 EndZ=0
    g122: LineSegment [constr] StartX=10.1 StartY=-17.1 StartZ=0 EndX=11.4 EndY=-18.4 EndZ=0
    g123: LineSegment [constr] StartX=8.8 StartY=-17.1 StartZ=0 EndX=11.4 EndY=-19.7 EndZ=0
    g124: LineSegment [constr] StartX=8.4 StartY=-18 StartZ=0 EndX=10.5 EndY=-20.1 EndZ=0
    g125: LineSegment [constr] StartX=8.4 StartY=-19.3 StartZ=0 EndX=9.2 EndY=-20.1 EndZ=0
    g126: LineSegment [constr] StartX=10.1 StartY=-17.1 StartZ=0 EndX=10.1 EndY=-18.4 EndZ=0
    g127: LineSegment [constr] StartX=8.8 StartY=-17.1 StartZ=0 EndX=8.8 EndY=-18.4 EndZ=0
    g128: LineSegment StartX=8.95 StartY=-17.1 StartZ=0 EndX=11.4 EndY=-19.55 EndZ=0
    g129: LineSegment StartX=11.4 StartY=-19.85 StartZ=0 EndX=8.65 EndY=-17.1 EndZ=0
    g130: LineSegment StartX=8.95 StartY=-17.1 StartZ=0 EndX=8.65 EndY=-17.1 EndZ=0
    g131: LineSegment StartX=11.4 StartY=-19.55 StartZ=0 EndX=11.4 EndY=-19.85 EndZ=0
    g132: LineSegment StartX=9.95 StartY=-17.1 StartZ=0 EndX=11.4 EndY=-18.55 EndZ=0
    g133: LineSegment StartX=11.4 StartY=-18.25 StartZ=0 EndX=10.25 EndY=-17.1 EndZ=0
    g134: LineSegment StartX=10.25 StartY=-17.1 StartZ=0 EndX=9.95 EndY=-17.1 EndZ=0
    g135: LineSegment StartX=11.4 StartY=-18.25 StartZ=0 EndX=11.4 EndY=-18.55 EndZ=0
    g136: LineSegment StartX=8.4 StartY=-17.85 StartZ=0 EndX=10.65 EndY=-20.1 EndZ=0
    g137: LineSegment StartX=10.35 StartY=-20.1 StartZ=0 EndX=8.4 EndY=-18.15 EndZ=0
    g138: LineSegment StartX=8.4 StartY=-18.15 StartZ=0 EndX=8.4 EndY=-17.85 EndZ=0
    g139: LineSegment StartX=10.65 StartY=-20.1 StartZ=0 EndX=10.35 EndY=-20.1 EndZ=0
    g140: LineSegment StartX=8.4 StartY=-19.15 StartZ=0 EndX=9.35 EndY=-20.1 EndZ=0
    g141: LineSegment StartX=8.4 StartY=-19.45 StartZ=0 EndX=9.05 EndY=-20.1 EndZ=0
    g142: LineSegment StartX=9.35 StartY=-20.1 StartZ=0 EndX=9.05 EndY=-20.1 EndZ=0
    g143: LineSegment StartX=8.4 StartY=-19.15 StartZ=0 EndX=8.4 EndY=-19.45 EndZ=0
    g144: LineSegment StartX=9.23358 StartY=-17.825 StartZ=0 EndX=9.375 EndY=-17.9664 EndZ=0
    g145: LineSegment StartX=9.375 StartY=-17.9664 StartZ=0 EndX=9.01642 EndY=-18.325 EndZ=0
    g146: LineSegment StartX=9.01642 StartY=-18.325 StartZ=0 EndX=8.875 EndY=-18.1836 EndZ=0
    g147: LineSegment StartX=8.875 StartY=-18.1836 StartZ=0 EndX=9.23358 EndY=-17.825 EndZ=0
    g148: LineSegment StartX=9.88358 StartY=-17.175 StartZ=0 EndX=10.025 EndY=-17.3164 EndZ=0
    g149: LineSegment StartX=10.025 StartY=-17.3164 StartZ=0 EndX=9.66642 EndY=-17.675 EndZ=0
    g150: LineSegment StartX=9.66642 StartY=-17.675 StartZ=0 EndX=9.525 EndY=-17.5336 EndZ=0
    g151: LineSegment StartX=9.525 StartY=-17.5336 StartZ=0 EndX=9.88358 EndY=-17.175 EndZ=0
    g152: LineSegment StartX=8.58358 StartY=-18.475 StartZ=0 EndX=8.725 EndY=-18.6164 EndZ=0
    g153: LineSegment StartX=8.725 StartY=-18.6164 StartZ=0 EndX=8.4 EndY=-18.9414 EndZ=0
    g154: LineSegment StartX=8.4 StartY=-18.9414 StartZ=0 EndX=8.4 EndY=-18.6586 EndZ=0
    g155: LineSegment StartX=8.58358 StartY=-18.475 StartZ=0 EndX=8.4 EndY=-18.6586 EndZ=0
    g156: LineSegment StartX=11.1856 StartY=-17.173 StartZ=0 EndX=10.825 EndY=-17.5336 EndZ=0
    g157: LineSegment StartX=10.825 StartY=-17.5336 StartZ=0 EndX=10.9664 EndY=-17.675 EndZ=0
    g158: LineSegment StartX=10.9664 StartY=-17.675 StartZ=0 EndX=11.327 EndY=-17.3144 EndZ=0
    g159: LineSegment StartX=11.327 StartY=-17.3144 StartZ=0 EndX=11.1856 EndY=-17.173 EndZ=0
    g160: LineSegment StartX=10.5336 StartY=-17.825 StartZ=0 EndX=10.675 EndY=-17.9664 EndZ=0
    g161: LineSegment StartX=10.675 StartY=-17.9664 StartZ=0 EndX=10.3164 EndY=-18.325 EndZ=0
    g162: LineSegment StartX=10.3164 StartY=-18.325 StartZ=0 EndX=10.175 EndY=-18.1836 EndZ=0
    g163: LineSegment StartX=10.5336 StartY=-17.825 StartZ=0 EndX=10.175 EndY=-18.1836 EndZ=0
    g164: LineSegment StartX=11.1836 StartY=-18.475 StartZ=0 EndX=11.325 EndY=-18.6164 EndZ=0
    g165: LineSegment StartX=11.325 StartY=-18.6164 StartZ=0 EndX=10.9664 EndY=-18.975 EndZ=0
    g166: LineSegment StartX=10.9664 StartY=-18.975 StartZ=0 EndX=10.825 EndY=-18.8336 EndZ=0
    g167: LineSegment StartX=11.1836 StartY=-18.475 StartZ=0 EndX=10.825 EndY=-18.8336 EndZ=0
    g168: LineSegment StartX=9.88358 StartY=-18.475 StartZ=0 EndX=10.025 EndY=-18.6164 EndZ=0
    g169: LineSegment StartX=10.025 StartY=-18.6164 StartZ=0 EndX=9.66642 EndY=-18.975 EndZ=0
    g170: LineSegment StartX=9.66642 StartY=-18.975 StartZ=0 EndX=9.525 EndY=-18.8336 EndZ=0
    g171: LineSegment StartX=9.88358 StartY=-18.475 StartZ=0 EndX=9.525 EndY=-18.8336 EndZ=0
    g172: LineSegment StartX=10.5336 StartY=-19.125 StartZ=0 EndX=10.675 EndY=-19.2664 EndZ=0
    g173: LineSegment StartX=10.675 StartY=-19.2664 StartZ=0 EndX=10.3164 EndY=-19.625 EndZ=0
    g174: LineSegment StartX=10.3164 StartY=-19.625 StartZ=0 EndX=10.175 EndY=-19.4836 EndZ=0
    g175: LineSegment StartX=10.5336 StartY=-19.125 StartZ=0 EndX=10.175 EndY=-19.4836 EndZ=0
    g176: LineSegment StartX=11.325 StartY=-19.9164 StartZ=0 EndX=11.1836 EndY=-19.775 EndZ=0
    g177: LineSegment StartX=11.1836 StartY=-19.775 StartZ=0 EndX=10.8586 EndY=-20.1 EndZ=0
    g178: LineSegment StartX=10.8586 StartY=-20.1 StartZ=0 EndX=11.1414 EndY=-20.1 EndZ=0
    g179: LineSegment StartX=11.325 StartY=-19.9164 StartZ=0 EndX=11.1414 EndY=-20.1 EndZ=0
    g180: LineSegment StartX=9.84142 StartY=-20.1 StartZ=0 EndX=10.025 EndY=-19.9164 EndZ=0
    g181: LineSegment StartX=10.025 StartY=-19.9164 StartZ=0 EndX=9.88358 EndY=-19.775 EndZ=0
    g182: LineSegment StartX=9.88358 StartY=-19.775 StartZ=0 EndX=9.55858 EndY=-20.1 EndZ=0
    g183: LineSegment StartX=9.55858 StartY=-20.1 StartZ=0 EndX=9.84142 EndY=-20.1 EndZ=0
    g184: LineSegment StartX=8.725 StartY=-19.9164 StartZ=0 EndX=8.58358 EndY=-19.775 EndZ=0
    g185: LineSegment StartX=8.58358 StartY=-19.775 StartZ=0 EndX=8.4 EndY=-19.9586 EndZ=0
    g186: LineSegment StartX=8.4 StartY=-19.9586 StartZ=0 EndX=8.4 EndY=-20.1 EndZ=0
    g187: LineSegment StartX=8.4 StartY=-20.1 StartZ=0 EndX=8.54142 EndY=-20.1 EndZ=0
    g188: LineSegment StartX=8.54142 StartY=-20.1 StartZ=0 EndX=8.725 EndY=-19.9164 EndZ=0
    g189: LineSegment StartX=9.375 StartY=-19.2664 StartZ=0 EndX=9.23358 EndY=-19.125 EndZ=0
    g190: LineSegment StartX=9.23358 StartY=-19.125 StartZ=0 EndX=8.875 EndY=-19.4836 EndZ=0
    g191: LineSegment StartX=8.875 StartY=-19.4836 StartZ=0 EndX=9.01642 EndY=-19.625 EndZ=0
    g192: LineSegment StartX=9.01642 StartY=-19.625 StartZ=0 EndX=9.375 EndY=-19.2664 EndZ=0
    g193: LineSegment StartX=8.58358 StartY=-17.175 StartZ=0 EndX=8.4 EndY=-17.3586 EndZ=0
    g194: LineSegment StartX=8.58358 StartY=-17.175 StartZ=0 EndX=8.725 EndY=-17.3164 EndZ=0
    g195: LineSegment StartX=8.725 StartY=-17.3164 StartZ=0 EndX=8.4 EndY=-17.6414 EndZ=0
    g196: LineSegment StartX=8.4 StartY=-17.6414 StartZ=0 EndX=8.4 EndY=-17.3586 EndZ=0
  constraints (603):
    c: DistanceY(g-8,g-8) = 3
    c: DistanceY(g-4,g-4) = 3
    c: DistanceX(g-12,g-11) = 0.7
    c: Coincident(g0,g-4)
    c: PointOnObject(g0,g-5)
    c: Angle(g0,g-4) = 0.785398
    c: PointOnObject(g1,g-5)
    c: PointOnObject(g1,g-13)
    c: Parallel(g1,g0)
    c: PointOnObject(g2,g-6)
    c: PointOnObject(g3,g-6)
    c: PointOnObject(g3,g-13)
    c: PointOnObject(g2,g-13)
    c: Parallel(g1,g2)
    c: Parallel(g0,g3)
    c: PointOnObject(g4,g-4)
    c: PointOnObject(g4,g-5)
    c: PointOnObject(g5,g-4)
    c: PointOnObject(g5,g-5)
    c: Parallel(g0,g4)
    c: Parallel(g4,g5)
    c: DistanceX(g3,g2) = 1.3
    c: DistanceX(g2,g1) = 1.3
    c: DistanceX(g1,g0) = 1.3
    c: DistanceY(g4,g0) = 1.3
    c: DistanceX(g-6,g3) = 1.3
    c: DistanceY(g5,g4) = 1.3
    c: Coincident(g6,g-6)
    c: PointOnObject(g6,g-5)
    c: Angle(g6,g-13) = 0.785398
    c: Coincident(g7,g3)
    c: PointOnObject(g7,g-5)
    c: Coincident(g8,g2)
    c: PointOnObject(g8,g-4)
    c: Coincident(g9,g1)
    c: PointOnObject(g9,g-4)
    c: Coincident(g10,g3)
    c: PointOnObject(g10,g-5)
    c: Coincident(g11,g2)
    c: PointOnObject(g11,g-5)
    c: Parallel(g6,g7)
    c: Parallel(g7,g8)
    c: Parallel(g8,g9)
    c: Parallel(g6,g10)
    c: Parallel(g10,g11)
    c: PointOnObject(g13,g-4)
    c: PointOnObject(g14,g-4)
    c: PointOnObject(g15,g-4)
    c: PointOnObject(g14,g-13)
    c: PointOnObject(g15,g-13)
    c: PointOnObject(g13,g-13)
    c: PointOnObject(g12,g-13)
    c: Parallel(g12,g8)
    c: PointOnObject(g12,g-4)
    c: Parallel(g8,g13)
    c: Parallel(g9,g15)
    c: Parallel(g9,g14)
    c: DistanceY(g5,g13) = 0.15
    c: DistanceY(g12,g5) = 0.15
    c: DistanceY(g15,g4) = 0.15
    c: DistanceY(g4,g14) = 0.15
    c: PointOnObject(g19,g-5)
    c: PointOnObject(g18,g-5)
    c: PointOnObject(g17,g-5)
    c: PointOnObject(g16,g-5)
    c: PointOnObject(g21,g-5)
    c: PointOnObject(g20,g-5)
    c: Parallel(g10,g21)
    c: Parallel(g10,g20)
    c: Parallel(g16,g7)
    c: Parallel(g17,g7)
    c: Parallel(g18,g6)
    c: Parallel(g19,g6)
    c: PointOnObject(g16,g-13)
    c: PointOnObject(g17,g-13)
    c: PointOnObject(g18,g-13)
    c: PointOnObject(g19,g-6)
    c: PointOnObject(g20,g-6)
    c: PointOnObject(g21,g-6)
    c: Parallel(g11,g22)
    c: PointOnObject(g22,g-6)
    c: PointOnObject(g22,g-5)
    c: Parallel(g23,g11)
    c: PointOnObject(g23,g-5)
    c: PointOnObject(g23,g-6)
    c: Coincident(g24,g14)
    c: Coincident(g24,g15)
    c: Coincident(g25,g13)
    c: Coincident(g25,g12)
    c: Coincident(g26,g16)
    c: Coincident(g26,g17)
    c: DistanceX(g3,g16) = 0.15
    c: DistanceX(g17,g3) = 0.15
    c: DistanceX(g6,g18) = 0.15
    c: DistanceY(g19,g6) = 0.15
    c: DistanceY(g3,g20) = 0.15
    c: DistanceY(g21,g3) = 0.15
    c: DistanceY(g2,g22) = 0.15
    c: DistanceY(g23,g2) = 0.15
    c: Coincident(g27,g18)
    c: Coincident(g27,g6)
    c: Coincident(g28,g6)
    c: Coincident(g28,g19)
    c: Coincident(g29,g20)
    c: Coincident(g29,g21)
    c: Coincident(g30,g22)
    c: Coincident(g30,g23)
    c: Coincident(g31,g23)
    c: Coincident(g31,g22)
    c: Coincident(g32,g21)
    c: Coincident(g32,g20)
    c: Coincident(g33,g19)
    c: Coincident(g33,g18)
    c: Coincident(g34,g17)
    c: Coincident(g34,g16)
    c: Coincident(g35,g12)
    c: Coincident(g35,g13)
    c: Coincident(g36,g15)
    c: Coincident(g36,g14)
    c: Coincident(g75,g74)
    c: Coincident(g75,g73)
    c: Coincident(g76,g74)
    c: Coincident(g76,g73)
    c: Coincident(g77,g42)
    c: Coincident(g77,g41)
    c: Coincident(g78,g42)
    c: Coincident(g78,g41)
    c: Coincident(g79,g40)
    c: Coincident(g79,g39)
    c: Coincident(g80,g40)
    c: Coincident(g80,g39)
    c: Coincident(g81,g44)
    c: Coincident(g81,g43)
    c: Coincident(g82,g44)
    c: Coincident(g82,g43)
    c: Coincident(g83,g46)
    c: Coincident(g83,g45)
    c: Coincident(g84,g46)
    c: Coincident(g84,g45)
    c: Coincident(g85,g64)
    c: Coincident(g85,g63)
    c: Coincident(g86,g64)
    c: Coincident(g86,g63)
    c: Coincident(g87,g62)
    c: Coincident(g87,g61)
    c: Coincident(g88,g66)
    c: Coincident(g88,g65)
    c: Coincident(g89,g66)
    c: Coincident(g89,g65)
    c: Coincident(g90,g68)
    c: Coincident(g90,g67)
    c: Coincident(g91,g68)
    c: Coincident(g91,g67)
    c: Coincident(g92,g62)
    c: Coincident(g92,g61)
    c: Coincident(g93,g60)
    c: Coincident(g93,g59)
    c: Coincident(g94,g60)
    c: Coincident(g94,g59)
    c: Coincident(g95,g58)
    c: Coincident(g95,g57)
    c: Coincident(g96,g58)
    c: Coincident(g96,g57)
    c: Coincident(g97,g56)
    c: Coincident(g97,g55)
    c: Coincident(g98,g54)
    c: Coincident(g98,g53)
    c: Coincident(g99,g70)
    c: Coincident(g99,g69)
    c: Coincident(g100,g70)
    c: Coincident(g100,g69)
    c: Coincident(g101,g50)
    c: Coincident(g101,g49)
    c: Coincident(g102,g50)
    c: Coincident(g102,g49)
    c: Coincident(g103,g48)
    c: Coincident(g103,g47)
    c: Coincident(g104,g48)
    c: Coincident(g104,g47)
    c: Coincident(g105,g38)
    c: Coincident(g105,g37)
    c: Coincident(g106,g38)
    c: Coincident(g106,g37)
    c: Coincident(g107,g72)
    c: Coincident(g107,g71)
    c: Coincident(g108,g72)
    c: Coincident(g108,g71)
    c: Coincident(g109,g52)
    c: Coincident(g109,g51)
    c: PointOnObject(g52,g-5)
    c: PointOnObject(g51,g-5)
    c: PointOnObject(g54,g-5)
    c: PointOnObject(g53,g-5)
    c: PointOnObject(g56,g-5)
    c: PointOnObject(g55,g-5)
    c: Coincident(g110,g52)
    c: Coincident(g110,g51)
    c: Coincident(g111,g54)
    c: Coincident(g111,g53)
    c: Coincident(g112,g56)
    c: Coincident(g112,g55)
    c: PointOnObject(g113,g-5)
    c: Coincident(g114,g113)
    c: Coincident(g115,g114)
    c: PointOnObject(g115,g-5)
    c: Coincident(g116,g115)
    c: Coincident(g116,g113)
    c: Parallel(g38,g0)
    c: Parallel(g37,g0)
    c: Parallel(g46,g1)
    c: Parallel(g45,g1)
    c: Parallel(g64,g2)
    c: Parallel(g63,g2)
    c: Parallel(g44,g1)
    c: Parallel(g43,g1)
    c: Parallel(g39,g0)
    c: Parallel(g40,g0)
    c: Parallel(g73,g4)
    c: Parallel(g74,g4)
    c: Parallel(g42,g0)
    c: Parallel(g41,g0)
    c: Parallel(g113,g5)
    c: Parallel(g115,g5)
    c: Parallel(g52,g4)
    c: Parallel(g51,g4)
    c: Parallel(g54,g0)
    c: Parallel(g53,g0)
    c: Parallel(g56,g1)
    c: Parallel(g55,g1)
    c: Parallel(g58,g2)
    c: Parallel(g57,g2)
    c: Parallel(g70,g1)
    c: Parallel(g69,g1)
    c: Parallel(g60,g2)
    c: Parallel(g59,g2)
    c: Parallel(g68,g3)
    c: Parallel(g67,g3)
    c: Parallel(g66,g3)
    c: Parallel(g65,g3)
    c: Parallel(g61,g2)
    c: Parallel(g62,g2)
    c: Parallel(g48,g1)
    c: Parallel(g47,g1)
    c: Parallel(g49,g0)
    c: Parallel(g50,g0)
    c: Parallel(g72,g4)
    c: Parallel(g71,g4)
    c: Parallel(g81,g15)
    c: Parallel(g79,g15)
    c: Parallel(g76,g15)
    c: Parallel(g78,g14)
    c: Parallel(g77,g14)
    c: Parallel(g82,g13)
    c: Parallel(g80,g13)
    c: Parallel(g75,g13)
    c: Parallel(g114,g12)
    c: Parallel(g107,g12)
    c: Parallel(g12,g106)
    c: Parallel(g83,g12)
    c: Parallel(g86,g12)
    c: Parallel(g85,g16)
    c: Parallel(g84,g16)
    c: Parallel(g105,g16)
    c: Parallel(g108,g16)
    c: Parallel(g109,g17)
    c: Parallel(g102,g17)
    c: Parallel(g101,g18)
    c: Parallel(g103,g17)
    c: Parallel(g104,g18)
    c: Parallel(g87,g17)
    c: Parallel(g92,g18)
    c: Parallel(g88,g17)
    c: Parallel(g89,g18)
    c: Parallel(g90,g19)
    c: Parallel(g93,g19)
    c: Parallel(g99,g19)
    c: Parallel(g98,g19)
    c: Parallel(g97,g21)
    c: Parallel(g95,g21)
    c: Parallel(g96,g22)
    c: Distance(g57,g2) = 0.1
    c: Distance(g58,g2) = 0.1
    c: Distance(g57,g21) = 0.1
    c: Distance(g57,g22) = 0.1
    c: Distance(g59,g2) = 0.1
    c: Distance(g60,g2) = 0.1
    c: Parallel(g94,g20)
    c: Distance(g59,g20) = 0.1
    c: Distance(g59,g19) = 0.1
    c: Distance(g69,g1) = 0.1
    c: Distance(g70,g1) = 0.1
    c: Parallel(g100,g20)
    c: Distance(g56,g1) = 0.1
    c: Distance(g55,g1) = 0.1
    c: Distance(g54,g0) = 0.1
    c: Distance(g53,g0) = 0.1
    c: Distance(g50,g0) = 0.1
    c: Distance(g49,g0) = 0.1
    c: Distance(g48,g1) = 0.1
    c: Distance(g47,g1) = 0.1
    c: Distance(g56,g21) = 0.1
    c: Distance(g54,g19) = 0.1
    c: Distance(g70,g19) = 0.1
    c: Distance(g70,g20) = 0.1
    c: Parallel(g91,g20)
    c: Distance(g68,g3) = 0.1
    c: Distance(g67,g3) = 0.1
    c: Distance(g68,g19) = 0.1
    c: Distance(g68,g20) = 0.1
    c: Distance(g52,g4) = 0.1
    c: Distance(g51,g4) = 0.1
    c: Distance(g52,g17) = 0.1
    c: Distance(g50,g17) = 0.1
    c: Distance(g50,g18) = 0.1
    c: Distance(g47,g18) = 0.1
    c: Distance(g48,g17) = 0.1
    c: Distance(g62,g2) = 0.1
    c: Distance(g61,g2) = 0.1
    c: Distance(g62,g17) = 0.1
    c: Distance(g62,g18) = 0.1
    c: Distance(g66,g3) = 0.1
    c: Distance(g65,g3) = 0.1
    c: Distance(g66,g18) = 0.1
    c: Distance(g66,g17) = 0.1
    c: Distance(g64,g2) = 0.1
    c: Distance(g63,g2) = 0.1
    c: Distance(g64,g16) = 0.1
    c: Distance(g64,g12) = 0.1
    c: Distance(g46,g1) = 0.1
    c: Distance(g45,g1) = 0.1
    c: Distance(g46,g12) = 0.1
    c: Distance(g46,g16) = 0.1
    c: Distance(g37,g0) = 0.1
    c: Distance(g38,g0) = 0.1
    c: Distance(g38,g12) = 0.1
    c: Distance(g38,g16) = 0.1
    c: Distance(g72,g4) = 0.1
    c: Distance(g71,g4) = 0.1
    c: Distance(g72,g12) = 0.1
    c: Distance(g72,g16) = 0.1
    c: Distance(g113,g5) = 0.1
    c: Distance(g114,g5) = 0.1
    c: Distance(g113,g12) = 0.1
    c: Distance(g74,g4) = 0.1
    c: Distance(g73,g4) = 0.1
    c: Distance(g74,g13) = 0.1
    c: Distance(g74,g15) = 0.1
    c: Distance(g40,g0) = 0.1
    c: Distance(g39,g0) = 0.1
    c: Distance(g40,g13) = 0.1
    c: Distance(g40,g15) = 0.1
    c: Distance(g44,g1) = 0.1
    c: Distance(g43,g1) = 0.1
    c: Distance(g44,g13) = 0.1
    c: Distance(g44,g15) = 0.1
    c: Distance(g42,g0) = 0.1
    c: Distance(g41,g0) = 0.1
    c: Distance(g42,g14) = 0.1
    c: Distance(g41) = 0.51
    c: Coincident(g117,g-8)
    c: Coincident(g117,g-10)
    c: PointOnObject(g118,g-7)
    c: PointOnObject(g119,g-7)
    c: DistanceX(g118,g117) = 1.3
    c: DistanceX(g119,g118) = 1.3
    c: Angle(g-7,g118) = 0.785398
    c: Angle(g119,g-7) = 2.35619
    c: PointOnObject(g119,g-9)
    c: PointOnObject(g118,g-9)
    c: PointOnObject(g120,g-8)
    c: PointOnObject(g121,g-8)
    c: PointOnObject(g120,g-10)
    c: PointOnObject(g121,g-10)
    c: Angle(g120,g-8) = 0.785398
    c: Angle(g-8,g121) = 2.35619
    c: DistanceY(g120,g117) = 1.3
    c: DistanceY(g121,g120) = 1.3
    c: Coincident(g122,g118)
    c: Coincident(g123,g119)
    c: Angle(g123,g-7) = 0.785398
    c: Angle(g-7,g122) = 2.35619
    c: PointOnObject(g122,g-8)
    c: PointOnObject(g123,g-8)
    c: PointOnObject(g124,g-9)
    c: PointOnObject(g125,g-9)
    c: Angle(g-9,g124) = 0.785398
    c: Angle(g125,g-9) = 2.35619
    c: PointOnObject(g125,g-10)
    c: PointOnObject(g124,g-10)
    c: DistanceY(g125,g124) = 1.3
    c: Coincident(g126,g118)
    c: PointOnObject(g126,g117)
    c: Vertical(g126)
    c: Coincident(g127,g119)
    c: PointOnObject(g127,g118)
    c: Vertical(g127)
    c: PointOnObject(g127,g124)
    c: PointOnObject(g128,g-7)
    c: PointOnObject(g128,g-8)
    c: PointOnObject(g129,g-8)
    c: PointOnObject(g129,g-7)
    c: Coincident(g130,g128)
    c: Coincident(g130,g129)
    c: Coincident(g131,g128)
    c: Coincident(g131,g129)
    c: DistanceY(g121,g128) = 0.15
    c: DistanceY(g129,g121) = 0.15
    c: Parallel(g128,g123)
    c: Parallel(g129,g123)
    c: PointOnObject(g132,g-7)
    c: PointOnObject(g132,g-8)
    c: PointOnObject(g133,g-8)
    c: PointOnObject(g133,g-7)
    c: Coincident(g134,g133)
    c: Coincident(g134,g132)
    c: Coincident(g135,g133)
    c: Coincident(g135,g132)
    c: Parallel(g122,g132)
    c: Parallel(g122,g133)
    c: DistanceY(g120,g133) = 0.15
    c: DistanceY(g132,g120) = 0.15
    c: PointOnObject(g136,g-9)
    c: PointOnObject(g136,g-10)
    c: PointOnObject(g137,g-10)
    c: PointOnObject(g137,g-9)
    c: Coincident(g138,g137)
    c: Coincident(g138,g136)
    c: Coincident(g139,g136)
    c: Coincident(g139,g137)
    c: Parallel(g136,g124)
    c: Parallel(g137,g124)
    c: DistanceY(g124,g136) = 0.15
    c: DistanceY(g137,g124) = 0.15
    c: PointOnObject(g140,g-9)
    c: PointOnObject(g140,g-10)
    c: PointOnObject(g141,g-9)
    c: PointOnObject(g141,g-10)
    c: Coincident(g142,g140)
    c: Coincident(g142,g141)
    c: Coincident(g143,g140)
    c: Coincident(g143,g141)
    c: DistanceX(g125,g140) = 0.15
    c: DistanceX(g141,g125) = 0.15
    c: Parallel(g125,g141)
    c: Parallel(g125,g140)
    c: Coincident(g145,g144)
    c: Coincident(g146,g145)
    c: Coincident(g147,g146)
    c: Coincident(g147,g144)
    c: Coincident(g149,g148)
    c: Coincident(g150,g149)
    c: Coincident(g151,g150)
    c: Coincident(g151,g148)
    c: Coincident(g153,g152)
    c: PointOnObject(g153,g-9)
    c: Coincident(g154,g153)
    c: PointOnObject(g154,g-9)
    c: Coincident(g155,g152)
    c: Coincident(g155,g154)
    c: Coincident(g157,g156)
    c: Coincident(g158,g157)
    c: Coincident(g159,g158)
    c: Coincident(g159,g156)
    c: Coincident(g161,g160)
    c: Coincident(g162,g161)
    c: Coincident(g163,g160)
    c: Coincident(g163,g162)
    c: Coincident(g165,g164)
    c: Coincident(g166,g165)
    c: Coincident(g167,g164)
    c: Coincident(g167,g166)
    c: Coincident(g169,g168)
    c: Coincident(g170,g169)
    c: Coincident(g171,g168)
    c: Coincident(g171,g170)
    c: Coincident(g173,g172)
    c: Coincident(g174,g173)
    c: Coincident(g175,g172)
    c: Coincident(g175,g174)
    c: Coincident(g177,g176)
    c: PointOnObject(g177,g-10)
    c: Coincident(g178,g177)
    c: PointOnObject(g178,g-10)
    c: Coincident(g179,g176)
    c: Coincident(g179,g178)
    c: PointOnObject(g180,g-10)
    c: Coincident(g181,g180)
    c: Coincident(g182,g181)
    c: PointOnObject(g182,g-10)
    c: Coincident(g183,g182)
    c: Coincident(g183,g180)
    c: Coincident(g185,g184)
    c: PointOnObject(g185,g-9)
    c: Coincident(g186,g185)
    c: Coincident(g186,g117)
    c: Coincident(g187,g117)
    c: PointOnObject(g187,g-10)
    c: Coincident(g188,g187)
    c: Coincident(g188,g184)
    c: Coincident(g190,g189)
    c: Coincident(g191,g190)
    c: Coincident(g192,g191)
    c: Coincident(g192,g189)
    c: Parallel(g190,g117)
    c: Parallel(g192,g117)
    c: Parallel(g188,g117)
    c: Parallel(g185,g117)
    c: Parallel(g182,g120)
    c: Parallel(g180,g120)
    c: Parallel(g173,g120)
    c: Parallel(g175,g120)
    c: Parallel(g179,g121)
    c: Parallel(g177,g121)
    c: Parallel(g165,g120)
    c: Parallel(g167,g120)
    c: Parallel(g158,g117)
    c: Parallel(g156,g117)
    c: Parallel(g161,g117)
    c: Parallel(g163,g117)
    c: Parallel(g149,g118)
    c: Parallel(g151,g118)
    c: PointOnObject(g193,g-9)
    c: Coincident(g194,g193)
    c: Coincident(g195,g194)
    c: PointOnObject(g195,g-9)
    c: Coincident(g196,g195)
    c: Coincident(g196,g193)
    c: Parallel(g193,g119)
    c: Parallel(g195,g119)
    c: Perpendicular(g194,g195)
    c: Perpendicular(g147,g144)
    c: Perpendicular(g146,g145)
    c: Perpendicular(g150,g149)
    c: Perpendicular(g149,g148)
    c: Perpendicular(g160,g163)
    c: Perpendicular(g162,g161)
    c: Perpendicular(g157,g158)
    c: Perpendicular(g158,g159)
    c: Perpendicular(g167,g164)
    c: Perpendicular(g166,g165)
    c: Perpendicular(g174,g173)
    c: Perpendicular(g175,g172)
    c: Perpendicular(g176,g179)
    c: Perpendicular(g181,g180)
    c: Perpendicular(g184,g188)
    c: Perpendicular(g191,g192)
    c: Perpendicular(g189,g192)
    c: Perpendicular(g170,g169)
    c: Perpendicular(g171,g168)
    c: Parallel(g171,g117)
    c: Parallel(g169,g117)
    c: Parallel(g155,g118)
    c: Parallel(g153,g118)
    c: Distance(g150,g118) = 0.1
    c: Distance(g149,g118) = 0.1
    c: Distance(g149,g128) = 0.1
    c: Distance(g148,g132) = 0.1
    c: Distance(g160,g117) = 0.1
    c: Distance(g160,g117) = 0.1
    c: Distance(g160,g132) = 0.1
    c: Distance(g161,g128) = 0.1
    c: Distance(g164,g120) = 0.1
    c: Distance(g164,g120) = 0.1
    c: Distance(g164,g132) = 0.1
    c: Distance(g166,g128) = 0.1
    c: Distance(g156,g117) = 0.1
    c: Distance(g158,g117) = 0.1
    c: Distance(g156,g133) = 0.1
    c: Distance(g156) = 0.51
    c: Distance(g194,g119) = 0.1
    c: Distance(g193,g119) = 0.1
    c: Distance(g194,g129) = 0.1
    c: Distance(g144,g118) = 0.1
    c: Distance(g144,g118) = 0.1
    c: Distance(g144,g129) = 0.1
    c: Parallel(g145,g118)
    c: Parallel(g147,g118)
    c: Distance(g146,g136) = 0.1
    c: Distance(g168,g117) = 0.1
    c: Distance(g168,g117) = 0.1
    c: Distance(g168,g129) = 0.1
    c: Distance(g170,g136) = 0.1
    c: Distance(g172,g120) = 0.1
    c: Distance(g172,g120) = 0.1
    c: Distance(g172,g129) = 0.1
    c: Distance(g174,g136) = 0.1
    c: Distance(g176,g121) = 0.1
    c: Distance(g176,g121) = 0.1
    c: Distance(g176,g129) = 0.1
    c: Distance(g152,g118) = 0.1
    c: Distance(g152,g118) = 0.1
    c: Distance(g152,g137) = 0.1
    c: Parallel(g152,g124)
    c: Distance(g189,g117) = 0.1
    c: Distance(g189,g117) = 0.1
    c: Distance(g189,g137) = 0.1
    c: Distance(g191,g140) = 0.1
    c: Distance(g180,g120) = 0.1
    c: Distance(g181,g120) = 0.1
    c: Distance(g181,g137) = 0.1
    c: Distance(g184,g117) = 0.1
    c: Distance(g184,g117) = 0.1
    c: Distance(g184,g141) = 0.1
FEATURE [PartDesign::Pad] Pad009
  BaseFeature = -> Pad008
  Direction = (0,0,1)
  Length = 0.2
  Length2 = 10
  Profile = -> Sketch009
  ReferenceAxis = -> Sketch009 [N_Axis]
  Refine = true
  Suppressed = false
  Type = 0
FEATURE [Sketcher::SketchObject] Sketch010
  ArcFitTolerance = 1e-06
  AttachmentSupport = -> [Pad009]
  ExternalGeometry = -> [Pad009]
  FullyConstrained = true
  MakeInternals = false
  MapMode = 5
  Placement = pos=(0,0,4.2) rot=(0,0,1;0rad)
  sketch-geometry (40):
    g0: LineSegment StartX=6.7 StartY=-6.9 StartZ=0 EndX=6.2 EndY=-7.4 EndZ=0
    g1: LineSegment StartX=6.2 StartY=-7.4 StartZ=0 EndX=6.2 EndY=-7.7 EndZ=0
    g2: LineSegment StartX=6.2 StartY=-7.7 StartZ=0 EndX=7 EndY=-6.9 EndZ=0
    g3: LineSegment StartX=7 StartY=-6.9 StartZ=0 EndX=6.7 EndY=-6.9 EndZ=0
    g4: LineSegment StartX=8 StartY=-6.9 StartZ=0 EndX=8.3 EndY=-6.9 EndZ=0
    g5: LineSegment StartX=8.3 StartY=-6.9 StartZ=0 EndX=6.2 EndY=-9 EndZ=0
    g6: LineSegment StartX=6.2 StartY=-9 StartZ=0 EndX=6.2 EndY=-8.7 EndZ=0
    g7: LineSegment StartX=6.2 StartY=-8.7 StartZ=0 EndX=8 EndY=-6.9 EndZ=0
    g8: LineSegment StartX=9.3 StartY=-6.9 StartZ=0 EndX=9.6 EndY=-6.9 EndZ=0
    g9: LineSegment StartX=9.6 StartY=-6.9 StartZ=0 EndX=6.6 EndY=-9.9 EndZ=0
    g10: LineSegment StartX=6.6 StartY=-9.9 StartZ=0 EndX=6.3 EndY=-9.9 EndZ=0
    g11: LineSegment StartX=6.3 StartY=-9.9 StartZ=0 EndX=9.3 EndY=-6.9 EndZ=0
    g12: LineSegment StartX=10.6 StartY=-6.9 StartZ=0 EndX=10.9 EndY=-6.9 EndZ=0
    g13: LineSegment StartX=10.9 StartY=-6.9 StartZ=0 EndX=7.9 EndY=-9.9 EndZ=0
    g14: LineSegment StartX=7.9 StartY=-9.9 StartZ=0 EndX=7.6 EndY=-9.9 EndZ=0
    g15: LineSegment StartX=7.6 StartY=-9.9 StartZ=0 EndX=10.6 EndY=-6.9 EndZ=0
    g16: LineSegment StartX=11.4 StartY=-7.4 StartZ=0 EndX=11.4 EndY=-7.7 EndZ=0
    g17: LineSegment StartX=11.4 StartY=-7.7 StartZ=0 EndX=9.2 EndY=-9.9 EndZ=0
    g18: LineSegment StartX=9.2 StartY=-9.9 StartZ=0 EndX=8.9 EndY=-9.9 EndZ=0
    g19: LineSegment StartX=8.9 StartY=-9.9 StartZ=0 EndX=11.4 EndY=-7.4 EndZ=0
    g20: LineSegment StartX=11.4 StartY=-8.7 StartZ=0 EndX=11.4 EndY=-9 EndZ=0
    g21: LineSegment StartX=11.4 StartY=-9 StartZ=0 EndX=10.5 EndY=-9.9 EndZ=0
    g22: LineSegment StartX=10.5 StartY=-9.9 StartZ=0 EndX=10.2 EndY=-9.9 EndZ=0
    g23: LineSegment StartX=10.2 StartY=-9.9 StartZ=0 EndX=11.4 EndY=-8.7 EndZ=0
    g24: LineSegment StartX=9.3 StartY=-17.1 StartZ=0 EndX=9.6 EndY=-17.1 EndZ=0
    g25: LineSegment StartX=9.6 StartY=-17.1 StartZ=0 EndX=8.4 EndY=-18.3 EndZ=0
    g26: LineSegment StartX=8.4 StartY=-18.3 StartZ=0 EndX=8.4 EndY=-18 EndZ=0
    g27: LineSegment StartX=8.4 StartY=-18 StartZ=0 EndX=9.3 EndY=-17.1 EndZ=0
    g28: LineSegment StartX=10.6 StartY=-17.1 StartZ=0 EndX=10.9 EndY=-17.1 EndZ=0
    g29: LineSegment StartX=10.9 StartY=-17.1 StartZ=0 EndX=8.4 EndY=-19.6 EndZ=0
    g30: LineSegment StartX=8.4 StartY=-19.6 StartZ=0 EndX=8.4 EndY=-19.3 EndZ=0
    g31: LineSegment StartX=8.4 StartY=-19.3 StartZ=0 EndX=10.6 EndY=-17.1 EndZ=0
    g32: LineSegment StartX=11.4 StartY=-17.6 StartZ=0 EndX=11.4 EndY=-17.9 EndZ=0
    g33: LineSegment StartX=11.4 StartY=-17.6 StartZ=0 EndX=8.9 EndY=-20.1 EndZ=0
    g34: LineSegment StartX=8.9 StartY=-20.1 StartZ=0 EndX=9.2 EndY=-20.1 EndZ=0
    g35: LineSegment StartX=9.2 StartY=-20.1 StartZ=0 EndX=11.4 EndY=-17.9 EndZ=0
    g36: LineSegment StartX=11.4 StartY=-18.9 StartZ=0 EndX=11.4 EndY=-19.2 EndZ=0
    g37: LineSegment StartX=11.4 StartY=-19.2 StartZ=0 EndX=10.5 EndY=-20.1 EndZ=0
    g38: LineSegment StartX=10.5 StartY=-20.1 StartZ=0 EndX=10.2 EndY=-20.1 EndZ=0
    g39: LineSegment StartX=10.2 StartY=-20.1 StartZ=0 EndX=11.4 EndY=-18.9 EndZ=0
  constraints (120):
    c: PointOnObject(g0,g-18)
    c: PointOnObject(g0,g-16)
    c: Coincident(g1,g0)
    c: PointOnObject(g1,g-16)
    c: Coincident(g2,g1)
    c: PointOnObject(g2,g-18)
    c: Coincident(g3,g2)
    c: Coincident(g3,g0)
    c: PointOnObject(g4,g-18)
    c: PointOnObject(g4,g-18)
    c: Coincident(g5,g4)
    c: PointOnObject(g5,g-16)
    c: Coincident(g6,g5)
    c: PointOnObject(g6,g-16)
    c: Coincident(g7,g6)
    c: Coincident(g7,g4)
    c: PointOnObject(g8,g-18)
    c: PointOnObject(g8,g-18)
    c: Coincident(g9,g8)
    c: PointOnObject(g9,g-17)
    c: Coincident(g10,g9)
    c: PointOnObject(g10,g-17)
    c: Coincident(g11,g10)
    c: Coincident(g11,g8)
    c: PointOnObject(g12,g-18)
    c: PointOnObject(g12,g-18)
    c: Coincident(g13,g12)
    c: PointOnObject(g13,g-17)
    c: Coincident(g14,g13)
    c: PointOnObject(g14,g-17)
    c: Coincident(g15,g14)
    c: Coincident(g15,g12)
    c: PointOnObject(g16,g-19)
    c: PointOnObject(g16,g-19)
    c: Coincident(g17,g16)
    c: PointOnObject(g17,g-17)
    c: Coincident(g18,g17)
    c: PointOnObject(g18,g-17)
    c: Coincident(g19,g18)
    c: Coincident(g19,g16)
    c: PointOnObject(g20,g-19)
    c: PointOnObject(g20,g-19)
    c: Coincident(g21,g20)
    c: PointOnObject(g21,g-17)
    c: Coincident(g22,g21)
    c: PointOnObject(g22,g-17)
    c: Coincident(g23,g20)
    c: Coincident(g22,g23)
    c: DistanceX(g0,g2) = 0.3
    c: DistanceX(g4,g4) = 0.3
    c: DistanceX(g8,g8) = 0.3
    c: DistanceX(g12,g12) = 0.3
    c: Parallel(g0,g-22)
    c: Parallel(g2,g-22)
    c: Parallel(g7,g-23)
    c: Parallel(g5,g-23)
    c: Parallel(g11,g-24)
    c: Parallel(g9,g-24)
    c: Parallel(g15,g-20)
    c: Parallel(g13,g-20)
    c: Parallel(g17,g-21)
    c: Parallel(g19,g-21)
    c: Parallel(g23,g-21)
    c: Parallel(g21,g-21)
    c: DistanceY(g20,g20) = 0.3
    c: DistanceY(g16,g16) = 0.3
    c: DistanceX(g-18,g0) = 0.5
    c: DistanceX(g2,g4) = 1
    c: DistanceX(g4,g8) = 1
    c: DistanceX(g8,g12) = 1
    c: DistanceX(g13,g18) = 1
    c: DistanceX(g17,g22) = 1
    c: PointOnObject(g24,g-31)
    c: PointOnObject(g24,g-31)
    c: Coincident(g25,g24)
    c: PointOnObject(g25,g-30)
    c: Coincident(g26,g25)
    c: PointOnObject(g26,g-30)
    c: Coincident(g27,g26)
    c: Coincident(g27,g24)
    c: PointOnObject(g28,g-31)
    c: PointOnObject(g28,g-31)
    c: Coincident(g29,g28)
    c: PointOnObject(g29,g-30)
    c: Coincident(g30,g29)
    c: PointOnObject(g30,g-30)
    c: Coincident(g31,g30)
    c: Coincident(g31,g28)
    c: PointOnObject(g32,g-28)
    c: PointOnObject(g32,g-28)
    c: Coincident(g33,g32)
    c: PointOnObject(g33,g-29)
    c: Coincident(g34,g33)
    c: PointOnObject(g34,g-29)
    c: Coincident(g35,g34)
    c: Coincident(g35,g32)
    c: PointOnObject(g36,g-28)
    c: PointOnObject(g36,g-28)
    c: Coincident(g37,g36)
    c: PointOnObject(g37,g-29)
    c: Coincident(g38,g37)
    c: PointOnObject(g38,g-29)
    c: Coincident(g39,g38)
    c: Coincident(g39,g36)
    c: DistanceX(g24,g24) = 0.3
    c: Parallel(g27,g25)
    c: Parallel(g31,g29)
    c: Parallel(g33,g35)
    c: Parallel(g39,g37)
    c: DistanceY(g36,g36) = 0.3
    c: DistanceY(g32,g32) = 0.3
    c: DistanceX(g28,g28) = 0.3
    c: DistanceX(g24,g28) = 1
    c: DistanceY(g36,g32) = 1
    c: Parallel(g29,g33)
    c: Parallel(g35,g39)
    c: Parallel(g31,g25)
    c: Parallel(g29,g-32)
    c: DistanceX(g-31,g24) = 0.9
    c: DistanceX(g37,g-29) = 0.9
FEATURE [PartDesign::Pocket] Pocket
  BaseFeature = -> Pad009
  Direction = (0,0,-1)
  Length = 0.2
  Length2 = 5
  Profile = -> Sketch010
  ReferenceAxis = -> Sketch010 [N_Axis]
  Refine = true
  Suppressed = false
  Type = 0
FEATURE [Sketcher::SketchObject] Sketch011
  ArcFitTolerance = 1e-06
  AttachmentSupport = -> [Pocket]
  ExternalGeometry = -> [Pocket]
  FullyConstrained = true
  MakeInternals = false
  MapMode = 5
  Placement = pos=(0,0,2) rot=(0,0,1;0rad)
  sketch-geometry (12):
    g0: LineSegment StartX=5.5 StartY=-23.7 StartZ=0 EndX=5.5 EndY=-30.8 EndZ=0
    g1: LineSegment StartX=6 StartY=-31.3 StartZ=0 EndX=17.2 EndY=-31.3 EndZ=0
    g2: LineSegment StartX=17.7 StartY=-30.8 StartZ=0 EndX=17.7 EndY=-23.7 EndZ=0
    g3: LineSegment StartX=17.2 StartY=-23.2 StartZ=0 EndX=6 EndY=-23.2 EndZ=0
    g4: ArcOfCircle CenterX=17.2 CenterY=-30.8 CenterZ=0 NormalX=0 NormalY=0 NormalZ=1 AngleXU=0 Radius=0.5 StartAngle=4.71239 EndAngle=6.28319
    g5: GeomPoint [constr] X=17.7 Y=-31.3 Z=0
    g6: ArcOfCircle CenterX=17.2 CenterY=-23.7 CenterZ=0 NormalX=0 NormalY=0 NormalZ=1 AngleXU=0 Radius=0.5 StartAngle=-1.8e-15 EndAngle=1.5708
    g7: GeomPoint [constr] X=17.7 Y=-23.2 Z=0
    g8: ArcOfCircle CenterX=6 CenterY=-23.7 CenterZ=0 NormalX=0 NormalY=0 NormalZ=1 AngleXU=0 Radius=0.5 StartAngle=1.5708 EndAngle=3.14159
    g9: GeomPoint [constr] X=5.5 Y=-23.2 Z=0
    g10: ArcOfCircle CenterX=6 CenterY=-30.8 CenterZ=0 NormalX=0 NormalY=0 NormalZ=1 AngleXU=0 Radius=0.5 StartAngle=3.14159 EndAngle=4.71239
    g11: GeomPoint [constr] X=5.5 Y=-31.3 Z=0
  constraints (28):
    c: Vertical(g0)
    c: Vertical(g2)
    c: Horizontal(g1)
    c: Horizontal(g3)
    c: PointOnObject(g5,g1)
    c: PointOnObject(g5,g2)
    c: Tangent(g1,g4) = -1.5708
    c: Tangent(g2,g4) = -1.5708
    c: PointOnObject(g7,g2)
    c: PointOnObject(g7,g3)
    c: Tangent(g2,g6) = -1.5708
    c: Tangent(g3,g6) = -1.5708
    c: PointOnObject(g9,g0)
    c: PointOnObject(g9,g3)
    c: Tangent(g0,g8) = -1.5708
    c: Tangent(g3,g8) = -1.5708
    c: PointOnObject(g11,g0)
    c: PointOnObject(g11,g1)
    c: Tangent(g0,g10) = -1.5708
    c: Tangent(g1,g10) = -1.5708
    c: Radius(g8) = 0.5
    c: Radius(g10) = 0.5
    c: Radius(g6) = 0.5
    c: Radius(g4) = 0.5
    c: DistanceX(g0,g2) = 12.2
    c: DistanceY(g1,g3) = 8.1
    c: DistanceY(g-3,g1) = 0.7
    c: DistanceX(g-3,g0) = 3
FEATURE [PartDesign::Pad] Pad010
  BaseFeature = -> Pocket
  Direction = (0,0,1)
  Length = 0.3
  Length2 = 10
  Profile = -> Sketch011
  ReferenceAxis = -> Sketch011 [N_Axis]
  Refine = true
  Suppressed = false
  Type = 0
FEATURE [Sketcher::SketchObject] Sketch012
  ArcFitTolerance = 1e-06
  AttachmentSupport = -> [Pad010]
  ExternalGeometry = -> [Pad010]
  FullyConstrained = true
  MakeInternals = false
  MapMode = 5
  Placement = pos=(0,0,2) rot=(0,0,1;0rad)
  sketch-geometry (8):
    g0: Circle CenterX=25.5 CenterY=-28.1 CenterZ=0 NormalX=0 NormalY=0 NormalZ=1 AngleXU=0 Radius=2.5
    g1: Circle CenterX=38.5 CenterY=-28.1 CenterZ=0 NormalX=0 NormalY=0 NormalZ=1 AngleXU=0 Radius=2.5
    g2: LineSegment [constr] StartX=25.5 StartY=-28.1 StartZ=0 EndX=25.5 EndY=-30.6 EndZ=0
    g3: LineSegment [constr] StartX=38.5 StartY=-28.1 StartZ=0 EndX=38.5 EndY=-30.6 EndZ=0
    g4: LineSegment [constr] StartX=38.5 StartY=-28.1 StartZ=0 EndX=41 EndY=-28.1 EndZ=0
    g5: LineSegment [constr] StartX=25.5 StartY=-28.1 StartZ=0 EndX=28 EndY=-28.1 EndZ=0
    g6: LineSegment [constr] StartX=38.5 StartY=-28.1 StartZ=0 EndX=36 EndY=-28.1 EndZ=0
    g7: LineSegment [constr] StartX=36 StartY=-28.1 StartZ=0 EndX=28 EndY=-28.1 EndZ=0
  constraints (23):
    c: Diameter(g0) = 5
    c: Diameter(g1) = 5
    c: Coincident(g2,g0)
    c: PointOnObject(g2,g0)
    c: Vertical(g2)
    c: Coincident(g3,g1)
    c: PointOnObject(g3,g1)
    c: Vertical(g3)
    c: Coincident(g4,g1)
    c: PointOnObject(g4,g1)
    c: Horizontal(g4)
    c: Coincident(g5,g0)
    c: PointOnObject(g5,g0)
    c: Horizontal(g5)
    c: DistanceX(g4,g-5) = 1.5
    c: Coincident(g6,g1)
    c: PointOnObject(g6,g1)
    c: Horizontal(g6)
    c: Coincident(g7,g6)
    c: Coincident(g7,g5)
    c: Horizontal(g7)
    c: DistanceX(g5,g6) = 8
    c: DistanceY(g-5,g3) = 1.4
FEATURE [PartDesign::Pad] Pad011
  BaseFeature = -> Pad010
  Direction = (0,0,1)
  Length = 0.3
  Length2 = 10
  Profile = -> Sketch012
  ReferenceAxis = -> Sketch012 [N_Axis]
  Refine = true
  Suppressed = false
  Type = 0
FEATURE [Sketcher::SketchObject] Sketch013
  ArcFitTolerance = 1e-06
  AttachmentSupport = -> [Pad011]
  ExternalGeometry = -> [Pad011]
  FullyConstrained = true
  MakeInternals = false
  MapMode = 5
  Placement = pos=(0,0,2) rot=(0,0,1;0rad)
  sketch-geometry (8):
    g0: ArcOfCircle CenterX=23.7322 CenterY=-26.3322 CenterZ=0 NormalX=0 NormalY=0 NormalZ=1 AngleXU=0 Radius=1 StartAngle=0.58404 EndAngle=4.12835
    g1: ArcOfCircle CenterX=36.7322 CenterY=-26.3322 CenterZ=0 NormalX=0 NormalY=0 NormalZ=1 AngleXU=0 Radius=1 StartAngle=0.58404 EndAngle=4.12835
    g2: LineSegment [constr] StartX=25.5 StartY=-28.1 StartZ=0 EndX=23.7322 EndY=-26.3322 EndZ=0
    g3: LineSegment [constr] StartX=38.5 StartY=-28.1 StartZ=0 EndX=36.7322 EndY=-26.3322 EndZ=0
    g4: LineSegment [constr] StartX=25.5 StartY=-28.1 StartZ=0 EndX=28 EndY=-28.1 EndZ=0
    g5: LineSegment [constr] StartX=38.5 StartY=-28.1 StartZ=0 EndX=41 EndY=-28.1 EndZ=0
    g6: ArcOfCircle CenterX=25.5 CenterY=-28.1 CenterZ=0 NormalX=0 NormalY=0 NormalZ=1 AngleXU=0 Radius=2.5 StartAngle=1.95348 EndAngle=2.75891
    g7: ArcOfCircle CenterX=38.5 CenterY=-28.1 CenterZ=0 NormalX=0 NormalY=0 NormalZ=1 AngleXU=0 Radius=2.5 StartAngle=1.95348 EndAngle=2.75891
  constraints (24):
    c: PointOnObject(g0,g-4)
    c: PointOnObject(g1,g-3)
    c: Diameter(g0) = 2
    c: Diameter(g1) = 2
    c: Coincident(g2,g-4)
    c: Coincident(g2,g0)
    c: Coincident(g3,g-3)
    c: Coincident(g3,g1)
    c: Coincident(g4,g2)
    c: PointOnObject(g4,g-4)
    c: Horizontal(g4)
    c: Coincident(g5,g3)
    c: PointOnObject(g5,g-3)
    c: Horizontal(g5)
    c: Coincident(g6,g0)
    c: Coincident(g6,g0)
    c: Coincident(g7,g1)
    c: Coincident(g7,g1)
    c: Coincident(g6,g2)
    c: Coincident(g7,g3)
    c: Angle(g4,g2) = 2.35619
    c: Angle(g5,g3) = 2.35619
    c: PointOnObject(g1,g7)
    c: PointOnObject(g0,g6)
FEATURE [PartDesign::Pad] Pad012
  BaseFeature = -> Pad011
  Direction = (0,0,1)
  Length = 0.3
  Length2 = 10
  Profile = -> Sketch013
  ReferenceAxis = -> Sketch013 [N_Axis]
  Refine = true
  Suppressed = false
  Type = 0
FEATURE [Sketcher::SketchObject] Sketch014
  ArcFitTolerance = 1e-06
  AttachmentSupport = -> [Pad012]
  ExternalGeometry = -> [Pad012]
  FullyConstrained = true
  MakeInternals = false
  MapMode = 5
  Placement = pos=(0,0,2.3) rot=(0,0,1;0rad)
  sketch-geometry (2):
    g0: Circle CenterX=25.5 CenterY=-28.1 CenterZ=0 NormalX=0 NormalY=0 NormalZ=1 AngleXU=0 Radius=1.45
    g1: Circle CenterX=38.5 CenterY=-28.1 CenterZ=0 NormalX=0 NormalY=0 NormalZ=1 AngleXU=0 Radius=1.45
  constraints (4):
    c: Coincident(g0,g-3)
    c: Coincident(g1,g-4)
    c: Diameter(g0) = 2.9
    c: Diameter(g1) = 2.9
FEATURE [PartDesign::Pad] Pad013
  BaseFeature = -> Pad012
  Direction = (0,0,1)
  Length = 2
  Length2 = 10
  Profile = -> Sketch014
  ReferenceAxis = -> Sketch014 [N_Axis]
  Refine = true
  Suppressed = false
  Type = 0
FEATURE [Sketcher::SketchObject] Sketch015
  ArcFitTolerance = 1e-06
  AttachmentSupport = -> [Pad013]
  ExternalGeometry = -> [Pad013]
  FullyConstrained = true
  MakeInternals = false
  MapMode = 5
  Placement = pos=(0,-1e-16,0) rot=(0,0.707107,0.707107;3.14159rad)
  sketch-geometry (9):
    g0: LineSegment StartX=-30.8 StartY=11.2 StartZ=0 EndX=-30.8 EndY=6.2 EndZ=0
    g1: LineSegment StartX=-30.8 StartY=6.2 StartZ=0 EndX=-24.8 EndY=6.2 EndZ=0
    g2: LineSegment StartX=-24.8 StartY=6.2 StartZ=0 EndX=-24.8 EndY=11.2 EndZ=0
    g3: LineSegment StartX=-24.8 StartY=11.2 StartZ=0 EndX=-30.8 EndY=11.2 EndZ=0
    g4: LineSegment StartX=-36.0765 StartY=11.2 StartZ=0 EndX=-39.3191 EndY=2 EndZ=0
    g5: LineSegment StartX=-39.3191 StartY=2 StartZ=0 EndX=-34.3191 EndY=2 EndZ=0
    g6: LineSegment StartX=-34.3191 StartY=2 StartZ=0 EndX=-34.3191 EndY=11.2 EndZ=0
    g7: LineSegment StartX=-34.3191 StartY=11.2 StartZ=0 EndX=-36.0765 EndY=11.2 EndZ=0
    g8: LineSegment [constr] StartX=-37.0327 StartY=8.48709 StartZ=0 EndX=-39.8621 EndY=9.48434 EndZ=0
  constraints (28):
    c: Coincident(g0,g1)
    c: Coincident(g1,g2)
    c: Coincident(g2,g3)
    c: Coincident(g3,g0)
    c: Vertical(g0)
    c: Vertical(g2)
    c: Horizontal(g1)
    c: Horizontal(g3)
    c: Coincident(g5,g4)
    c: Horizontal(g5)
    c: Coincident(g6,g5)
    c: Vertical(g6)
    c: Coincident(g7,g6)
    c: Coincident(g7,g4)
    c: Horizontal(g7)
    c: DistanceY(g-6,g4) = 2
    c: DistanceY(g0,g0) = 5
    c: DistanceX(g3,g3) = 6
    c: DistanceX(g2,g-5) = 2.5
    c: DistanceY(g2,g-5) = 3
    c: DistanceY(g4,g-4) = 3
    c: Parallel(g4,g-4)
    c: DistanceX(g5,g5) = 5
    c: PointOnObject(g8,g4)
    c: PointOnObject(g8,g-4)
    c: Angle(g8,g4) = 1.5708
    c: Distance(g8,g-4) = 5
    c: Distance(g8) = 3
FEATURE [PartDesign::Pocket] Pocket001
  BaseFeature = -> Pad013
  Direction = (0,-1,2e-16)
  Length = 5
  Length2 = 5
  Profile = -> Sketch015
  ReferenceAxis = -> Sketch015 [N_Axis]
  Refine = true
  Suppressed = false
  Type = 0
FEATURE [Sketcher::SketchObject] Sketch016
  ArcFitTolerance = 1e-06
  AttachmentSupport = -> [Pocket001]
  ExternalGeometry = -> [Pocket001]
  FullyConstrained = true
  MakeInternals = false
  MapMode = 5
  Placement = pos=(0,-1e-16,0) rot=(0,0.707107,0.707107;3.14159rad)
  sketch-geometry (16):
    g0: LineSegment StartX=-37.2 StartY=12.5 StartZ=0 EndX=-23.3 EndY=12.5 EndZ=0
    g1: LineSegment StartX=-23.3 StartY=12.5 StartZ=0 EndX=-23.3 EndY=12 EndZ=0
    g2: LineSegment StartX=-23.3 StartY=12 StartZ=0 EndX=-24.3 EndY=12 EndZ=0
    g3: LineSegment StartX=-24.3 StartY=12 StartZ=0 EndX=-24.3 EndY=2 EndZ=0
    g4: LineSegment StartX=-24.3 StartY=2 StartZ=0 EndX=-24.8 EndY=2 EndZ=0
    g5: LineSegment StartX=-24.8 StartY=2 StartZ=0 EndX=-24.8 EndY=12 EndZ=0
    g6: LineSegment StartX=-24.8 StartY=12 StartZ=0 EndX=-32.6 EndY=12 EndZ=0
    g7: LineSegment StartX=-32.6 StartY=12 StartZ=0 EndX=-32.6 EndY=2 EndZ=0
    g8: LineSegment StartX=-32.6 StartY=2 StartZ=0 EndX=-33.1 EndY=2 EndZ=0
    g9: LineSegment StartX=-33.1 StartY=2 StartZ=0 EndX=-33.1 EndY=12 EndZ=0
    g10: LineSegment StartX=-33.1 StartY=12 StartZ=0 EndX=-37.2 EndY=12 EndZ=0
    g11: LineSegment StartX=-37.2 StartY=12.5 StartZ=0 EndX=-37.2 EndY=12 EndZ=0
    g12: LineSegment StartX=-30.35 StartY=3.95 StartZ=0 EndX=-30.35 EndY=3.2 EndZ=0
    g13: LineSegment StartX=-30.35 StartY=3.2 StartZ=0 EndX=-28.15 EndY=3.2 EndZ=0
    g14: LineSegment StartX=-28.15 StartY=3.2 StartZ=0 EndX=-28.15 EndY=3.95 EndZ=0
    g15: LineSegment StartX=-28.15 StartY=3.95 StartZ=0 EndX=-30.35 EndY=3.95 EndZ=0
  constraints (48):
    c: Horizontal(g0)
    c: Coincident(g1,g0)
    c: Vertical(g1)
    c: Coincident(g2,g1)
    c: Horizontal(g2)
    c: Coincident(g3,g2)
    c: Vertical(g3)
    c: Coincident(g4,g3)
    c: Coincident(g5,g4)
    c: Vertical(g5)
    c: Coincident(g6,g5)
    c: Horizontal(g6)
    c: Coincident(g7,g6)
    c: Vertical(g7)
    c: Coincident(g8,g7)
    c: Coincident(g9,g8)
    c: Vertical(g9)
    c: Coincident(g10,g9)
    c: Horizontal(g10)
    c: Coincident(g11,g0)
    c: Coincident(g11,g10)
    c: Vertical(g11)
    c: Coincident(g12,g13)
    c: Coincident(g13,g14)
    c: Coincident(g14,g15)
    c: Coincident(g15,g12)
    c: Vertical(g12)
    c: Vertical(g14)
    c: Horizontal(g13)
    c: Horizontal(g15)
    c: Horizontal(g8)
    c: Horizontal(g4)
    c: DistanceY(g8,g-3) = 0
    c: DistanceX(g8,g8) = 0.5
    c: DistanceX(g4,g4) = 0.5
    c: DistanceY(g11,g11) = 0.5
    c: DistanceY(g1,g1) = 0.5
    c: DistanceY(g5,g0) = 0.5
    c: DistanceX(g0,g-4) = 1
    c: DistanceY(g7,g4) = 0
    c: DistanceX(g-5,g0) = 1
    c: DistanceY(g0,g-5) = 1.7
    c: PointOnObject(g-6,g5)
    c: DistanceX(g7,g4) = 7.8
    c: DistanceX(g15,g15) = 2.2
    c: DistanceY(g14,g14) = 0.75
    c: DistanceX(g7,g12) = 2.25
    c: DistanceY(g12,g-7) = 2.25
FEATURE [PartDesign::Pad] Pad014
  BaseFeature = -> Pocket001
  Direction = (0,1,-2e-16)
  Length = 0.3
  Length2 = 10
  Profile = -> Sketch016
  ReferenceAxis = -> Sketch016 [N_Axis]
  Refine = true
  Suppressed = false
  Type = 0
FEATURE [Sketcher::SketchObject] Sketch017
  ArcFitTolerance = 1e-06
  AttachmentSupport = -> [Pad014]
  ExternalGeometry = -> [Pad014]
  FullyConstrained = true
  MakeInternals = false
  MapMode = 5
  Placement = pos=(0,0,0) rot=(1,0,0;3.14159rad)
  sketch-geometry (14):
    g0: LineSegment StartX=40.75 StartY=0 StartZ=0 EndX=44.5 EndY=0 EndZ=0
    g1: LineSegment StartX=44.5 StartY=0 StartZ=0 EndX=44.5 EndY=11 EndZ=0
    g2: LineSegment StartX=44.5 StartY=11 StartZ=0 EndX=30.5 EndY=11 EndZ=0
    g3: LineSegment StartX=30.5 StartY=11 StartZ=0 EndX=30.5 EndY=9 EndZ=0
    g4: LineSegment StartX=30.5 StartY=9 StartZ=0 EndX=42.5 EndY=9 EndZ=0
    g5: LineSegment StartX=42.5 StartY=9 StartZ=0 EndX=42.5 EndY=2 EndZ=0
    g6: LineSegment StartX=42.5 StartY=2 StartZ=0 EndX=40.75 EndY=2 EndZ=0
    g7: LineSegment StartX=40.75 StartY=2 StartZ=0 EndX=40.75 EndY=0 EndZ=0
    g8: LineSegment StartX=42.5 StartY=32 StartZ=0 EndX=42.5 EndY=21.5 EndZ=0
    g9: LineSegment StartX=42.5 StartY=21.5 StartZ=0 EndX=30.5 EndY=21.5 EndZ=0
    g10: LineSegment StartX=30.5 StartY=21.5 StartZ=0 EndX=30.5 EndY=23.5 EndZ=0
    g11: LineSegment StartX=30.5 StartY=23.5 StartZ=0 EndX=40.5 EndY=23.5 EndZ=0
    g12: LineSegment StartX=40.5 StartY=23.5 StartZ=0 EndX=40.5 EndY=32 EndZ=0
    g13: LineSegment StartX=40.5 StartY=32 StartZ=0 EndX=42.5 EndY=32 EndZ=0
  constraints (36):
    c: PointOnObject(g0,g-9)
    c: Coincident(g0,g-9)
    c: Coincident(g1,g0)
    c: Coincident(g1,g-7)
    c: Coincident(g2,g1)
    c: PointOnObject(g2,g-6)
    c: Coincident(g3,g2)
    c: PointOnObject(g3,g-10)
    c: Vertical(g3)
    c: Coincident(g4,g3)
    c: Coincident(g4,g-10)
    c: Coincident(g5,g4)
    c: Coincident(g5,g-11)
    c: Coincident(g6,g5)
    c: PointOnObject(g6,g-11)
    c: Coincident(g7,g6)
    c: Coincident(g7,g0)
    c: Vertical(g7)
    c: Coincident(g8,g-4)
    c: Coincident(g8,g-5)
    c: Coincident(g9,g8)
    c: PointOnObject(g9,g-5)
    c: Coincident(g10,g9)
    c: Vertical(g10)
    c: Coincident(g11,g10)
    c: Horizontal(g11)
    c: Coincident(g12,g11)
    c: PointOnObject(g12,g-4)
    c: Vertical(g12)
    c: Coincident(g13,g12)
    c: Coincident(g13,g8)
    c: DistanceX(g13,g13) = 2
    c: DistanceY(g10,g10) = 2
    c: DistanceX(g10,g11) = 10
    c: DistanceX(g9,g2) = 0
    c: DistanceX(g6,g6) = 1.75
FEATURE [PartDesign::Pad] Pad015
  BaseFeature = -> Pad014
  Direction = (0,0,-1)
  Length = 8.2
  Length2 = 10
  Profile = -> Sketch017
  ReferenceAxis = -> Sketch017 [N_Axis]
  Refine = true
  Suppressed = false
  Type = 0
FEATURE [Sketcher::SketchObject] Sketch018
  ArcFitTolerance = 1e-06
  AttachmentSupport = -> [Pad015]
  ExternalGeometry = -> [Pad015]
  FullyConstrained = true
  MakeInternals = false
  MapMode = 5
  Placement = pos=(0,0,0) rot=(1,0,0;3.14159rad)
  sketch-geometry (1):
    g0: Circle CenterX=20.6 CenterY=16.25 CenterZ=0 NormalX=0 NormalY=0 NormalZ=1 AngleXU=0 Radius=4.95
  constraints (2):
    c: Coincident(g0,g-3)
    c: Diameter(g0) = 9.9
FEATURE [PartDesign::Pad] Pad016
  BaseFeature = -> Pad015
  Direction = (0,0,-1)
  Length = 2.5
  Length2 = 10
  Profile = -> Sketch018
  ReferenceAxis = -> Sketch018 [N_Axis]
  Refine = true
  Suppressed = false
  Type = 0
FEATURE [Sketcher::SketchObject] Sketch019
  ArcFitTolerance = 1e-06
  AttachmentSupport = -> [Pad016]
  ExternalGeometry = -> [Pad016]
  FullyConstrained = true
  MakeInternals = false
  MapMode = 5
  Placement = pos=(0,-23.5,0) rot=(1,0,0;1.5708rad)
  sketch-geometry (4):
    g0: LineSegment StartX=30.5 StartY=-8.2 StartZ=0 EndX=23.6194 EndY=1.8e-15 EndZ=0
    g1: LineSegment StartX=30.5 StartY=-8.2 StartZ=0 EndX=33.8806 EndY=-8.2 EndZ=0
    g2: LineSegment StartX=33.8806 StartY=-8.2 StartZ=0 EndX=27 EndY=0 EndZ=0
    g3: LineSegment StartX=27 StartY=7e-16 StartZ=0 EndX=23.6194 EndY=2.1e-15 EndZ=0
  constraints (10):
    c: Coincident(g0,g-3)
    c: Angle(g-3,g0) = 0.698132
    c: PointOnObject(g0,g-4)
    c: Coincident(g1,g0)
    c: Horizontal(g1)
    c: Coincident(g2,g1)
    c: Parallel(g0,g2)
    c: Coincident(g3,g2)
    c: Coincident(g3,g0)
    c: Coincident(g2,g-5)
FEATURE [PartDesign::Pad] Pad017
  BaseFeature = -> Pad016
  Direction = (0,-1,2e-16)
  Length = 14.5
  Length2 = 10
  Profile = -> Sketch019
  ReferenceAxis = -> Sketch019 [N_Axis]
  Refine = true
  Reversed = true
  Suppressed = false
  Type = 0
FEATURE [Sketcher::SketchObject] Sketch020
  ArcFitTolerance = 1e-06
  AttachmentSupport = -> [Pad017]
  ExternalGeometry = -> [Pad017]
  FullyConstrained = true
  MakeInternals = false
  MapMode = 5
  Placement = pos=(0,-9,0) rot=(0,0.707107,0.707107;3.14159rad)
  sketch-geometry (3):
    g0: LineSegment StartX=-30.5 StartY=0 StartZ=0 EndX=-30.5 EndY=-4.17114 EndZ=0
    g1: LineSegment StartX=-30.5 StartY=-4.17114 StartZ=0 EndX=-27 EndY=0 EndZ=0
    g2: LineSegment StartX=-27 StartY=0 StartZ=0 EndX=-30.5 EndY=0 EndZ=0
  constraints (6):
    c: Coincident(g0,g-4)
    c: Coincident(g0,g-3)
    c: Coincident(g1,g0)
    c: Coincident(g1,g-4)
    c: Coincident(g2,g1)
    c: Coincident(g2,g0)
FEATURE [PartDesign::Pad] Pad018
  BaseFeature = -> Pad017
  Direction = (0,1,-2e-16)
  Length = 2
  Length2 = 10
  Profile = -> Sketch020
  ReferenceAxis = -> Sketch020 [N_Axis]
  Refine = true
  Reversed = true
  Suppressed = false
  Type = 0
FEATURE [Sketcher::SketchObject] Sketch021
  ArcFitTolerance = 1e-06
  AttachmentSupport = -> [Pad018]
  ExternalGeometry = -> [Pad018]
  FullyConstrained = true
  MakeInternals = false
  MapMode = 5
  Placement = pos=(0,-23.5,0) rot=(1,0,0;1.5708rad)
  sketch-geometry (3):
    g0: LineSegment StartX=30.5 StartY=0 StartZ=0 EndX=27 EndY=0 EndZ=0
    g1: LineSegment StartX=27 StartY=0 StartZ=0 EndX=30.5 EndY=-4.17114 EndZ=0
    g2: LineSegment StartX=30.5 StartY=-4.17114 StartZ=0 EndX=30.5 EndY=0 EndZ=0
  constraints (6):
    c: Coincident(g0,g-3)
    c: Coincident(g0,g-4)
    c: Coincident(g1,g0)
    c: Coincident(g1,g-4)
    c: Coincident(g2,g1)
    c: Coincident(g2,g0)
FEATURE [PartDesign::Pad] Pad019
  BaseFeature = -> Pad018
  Direction = (0,-1,2e-16)
  Length = 2
  Length2 = 10
  Profile = -> Sketch021
  ReferenceAxis = -> Sketch021 [N_Axis]
  Refine = true
  Reversed = true
  Suppressed = false
  Type = 0
FEATURE [Sketcher::SketchObject] Sketch022
  ArcFitTolerance = 1e-06
  AttachmentSupport = -> [Pad019]
  ExternalGeometry = -> [Pad019]
  FullyConstrained = true
  MakeInternals = false
  MapMode = 5
  Placement = pos=(0,0,0) rot=(1,0,0;3.14159rad)
  sketch-geometry (4):
    g0: LineSegment StartX=6.7 StartY=19.45 StartZ=0 EndX=6.7 EndY=7.55 EndZ=0
    g1: LineSegment StartX=6.7 StartY=7.55 StartZ=0 EndX=10.9 EndY=7.55 EndZ=0
    g2: LineSegment StartX=10.9 StartY=7.55 StartZ=0 EndX=10.9 EndY=19.45 EndZ=0
    g3: LineSegment StartX=10.9 StartY=19.45 StartZ=0 EndX=6.7 EndY=19.45 EndZ=0
  constraints (14):
    c: Coincident(g0,g1)
    c: Coincident(g1,g2)
    c: Coincident(g2,g3)
    c: Coincident(g3,g0)
    c: Vertical(g0)
    c: Vertical(g2)
    c: Horizontal(g1)
    c: Horizontal(g3)
    c: DistanceY(g0,g0) = 11.9
    c: DistanceX(g3,g3) = 4.2
    c: DistanceY(g-5,g-3) = 15
    c: DistanceX(g-6,g-4) = 7
    c: DistanceX(g-6,g0) = 1.4
    c: DistanceY(g2,g-3) = 1.55
FEATURE [PartDesign::Pocket] Pocket002
  BaseFeature = -> Pad019
  Direction = (0,0,1)
  Length = 2
  Length2 = 5
  Profile = -> Sketch022
  ReferenceAxis = -> Sketch022 [N_Axis]
  Refine = true
  Suppressed = false
  Type = 0
FEATURE [Sketcher::SketchObject] Sketch023
  ArcFitTolerance = 1e-06
  AttachmentSupport = -> [Pocket002]
  ExternalGeometry = -> [Pocket002]
  FullyConstrained = true
  MakeInternals = false
  MapMode = 5
  Placement = pos=(0,0,0) rot=(1,0,0;3.14159rad)
  sketch-geometry (3):
    g0: Circle CenterX=11.75 CenterY=25.05 CenterZ=0 NormalX=0 NormalY=0 NormalZ=1 AngleXU=0 Radius=0.95
    g1: Circle CenterX=11.75 CenterY=6.95 CenterZ=0 NormalX=0 NormalY=0 NormalZ=1 AngleXU=0 Radius=0.95
    g2: LineSegment [constr] StartX=11.75 StartY=25.05 StartZ=0 EndX=10.8 EndY=25.05 EndZ=0
  constraints (9):
    c: Diameter(g0) = 1.9
    c: Diameter(g1) = 1.9
    c: DistanceY(g0,g-4) = 6.95
    c: DistanceY(g-1,g1) = 6.95
    c: DistanceX(g0,g1) = 0
    c: Coincident(g2,g0)
    c: PointOnObject(g2,g0)
    c: Horizontal(g2)
    c: DistanceX(g-6,g2) = 8.8
FEATURE [PartDesign::Pad] Pad020
  BaseFeature = -> Pocket002
  Direction = (0,0,-1)
  Length = 1.5
  Length2 = 10
  Profile = -> Sketch023
  ReferenceAxis = -> Sketch023 [N_Axis]
  Refine = true
  Suppressed = false
  Type = 0
FEATURE [Sketcher::SketchObject] Sketch024
  ArcFitTolerance = 1e-06
  AttachmentSupport = -> [Pad020]
  ExternalGeometry = -> [Pad020]
  FullyConstrained = true
  MakeInternals = false
  MapMode = 5
  Placement = pos=(0,-21.5,0) rot=(0,0.707107,0.707107;3.14159rad)
  sketch-geometry (4):
    g0: LineSegment StartX=-33.6 StartY=-8.2 StartZ=0 EndX=-33.6 EndY=-1.6 EndZ=0
    g1: LineSegment StartX=-33.6 StartY=-1.6 StartZ=0 EndX=-40.6 EndY=-1.6 EndZ=0
    g2: LineSegment StartX=-40.6 StartY=-1.6 StartZ=0 EndX=-40.6 EndY=-8.2 EndZ=0
    g3: LineSegment StartX=-40.6 StartY=-8.2 StartZ=0 EndX=-33.6 EndY=-8.2 EndZ=0
  constraints (12):
    c: Coincident(g0,g1)
    c: Coincident(g1,g2)
    c: Coincident(g2,g3)
    c: Coincident(g3,g0)
    c: Vertical(g0)
    c: Vertical(g2)
    c: Horizontal(g1)
    c: Horizontal(g3)
    c: PointOnObject(g0,g-3)
    c: DistanceX(g1,g1) = 7
    c: DistanceY(g2,g2) = 6.6
    c: DistanceX(g-4,g2) = 1.9
FEATURE [PartDesign::Pad] Pad021
  BaseFeature = -> Pad020
  Direction = (0,1,-2e-16)
  Length = 2
  Length2 = 10
  Profile = -> Sketch024
  ReferenceAxis = -> Sketch024 [N_Axis]
  Refine = true
  Suppressed = false
  Type = 0
FEATURE [Sketcher::SketchObject] Sketch025
  ArcFitTolerance = 1e-06
  AttachmentSupport = -> [Pad021]
  ExternalGeometry = -> [Pad021]
  FullyConstrained = true
  MakeInternals = false
  MapMode = 5
  Placement = pos=(0,-11,0) rot=(1,0,0;1.5708rad)
  sketch-geometry (4):
    g0: LineSegment StartX=33.6 StartY=-1.6 StartZ=0 EndX=33.6 EndY=-8.2 EndZ=0
    g1: LineSegment StartX=33.6 StartY=-8.2 StartZ=0 EndX=40.6 EndY=-8.2 EndZ=0
    g2: LineSegment StartX=40.6 StartY=-8.2 StartZ=0 EndX=40.6 EndY=-1.6 EndZ=0
    g3: LineSegment StartX=40.6 StartY=-1.6 StartZ=0 EndX=33.6 EndY=-1.6 EndZ=0
  constraints (10):
    c: Coincident(g0,g1)
    c: Coincident(g1,g2)
    c: Coincident(g2,g3)
    c: Coincident(g3,g0)
    c: Vertical(g0)
    c: Vertical(g2)
    c: Horizontal(g1)
    c: Horizontal(g3)
    c: Coincident(g0,g-6)
    c: Coincident(g1,g-3)
FEATURE [PartDesign::Pad] Pad022
  BaseFeature = -> Pad021
  Direction = (0,-1,2e-16)
  Length = 2
  Length2 = 10
  Profile = -> Sketch025
  ReferenceAxis = -> Sketch025 [N_Axis]
  Refine = true
  Suppressed = false
  Type = 0
FEATURE [Sketcher::SketchObject] Sketch026
  ArcFitTolerance = 1e-06
  AttachmentSupport = -> [Pad022]
  ExternalGeometry = -> [Pad022]
  FullyConstrained = true
  MakeInternals = false
  MapMode = 5
  Placement = pos=(0,-13,3.5e-15) rot=(1,0,0;1.5708rad)
  sketch-geometry (5):
    g0: LineSegment StartX=39 StartY=-5.1 StartZ=0 EndX=39 EndY=-8.2 EndZ=0
    g1: LineSegment StartX=39 StartY=-8.2 StartZ=0 EndX=35.2 EndY=-8.2 EndZ=0
    g2: LineSegment StartX=35.2 StartY=-8.2 StartZ=0 EndX=35.2 EndY=-5.1 EndZ=0
    g3: ArcOfCircle CenterX=37.1 CenterY=-5.1 CenterZ=0 NormalX=0 NormalY=0 NormalZ=1 AngleXU=0 Radius=1.9 StartAngle=0 EndAngle=3.14159
    g4: LineSegment [constr] StartX=37.1 StartY=-5.1 StartZ=0 EndX=37.1 EndY=-3.2 EndZ=0
  constraints (17):
    c: Vertical(g0)
    c: Coincident(g1,g0)
    c: Horizontal(g1)
    c: Coincident(g2,g1)
    c: Vertical(g2)
    c: PointOnObject(g0,g-3)
    c: Coincident(g3,g2)
    c: Coincident(g3,g0)
    c: DistanceY(g3,g2) = 0
    c: DistanceY(g0,g3) = 0
    c: Diameter(g3) = 3.8
    c: DistanceX(g-5,g-5) = 7
    c: DistanceX(g-6,g3) = 3.5
    c: Coincident(g4,g3)
    c: PointOnObject(g4,g3)
    c: Vertical(g4)
    c: DistanceY(g0,g4) = 5
FEATURE [PartDesign::Pocket] Pocket003
  BaseFeature = -> Pad022
  Direction = (0,1,-2e-16)
  Length = 2
  Length2 = 5
  Profile = -> Sketch026
  ReferenceAxis = -> Sketch026 [N_Axis]
  Refine = true
  Suppressed = false
  Type = 0
FEATURE [Sketcher::SketchObject] Sketch027
  ArcFitTolerance = 1e-06
  AttachmentSupport = -> [Pocket003]
  ExternalGeometry = -> [Pocket003]
  FullyConstrained = true
  MakeInternals = false
  MapMode = 5
  Placement = pos=(0,-19.5,1.05e-14) rot=(0,0.707107,0.707107;3.14159rad)
  sketch-geometry (4):
    g0: LineSegment StartX=-39 StartY=-5.1 StartZ=0 EndX=-39 EndY=-8.2 EndZ=0
    g1: LineSegment StartX=-39 StartY=-8.2 StartZ=0 EndX=-35.2 EndY=-8.2 EndZ=0
    g2: LineSegment StartX=-35.2 StartY=-8.2 StartZ=0 EndX=-35.2 EndY=-5.1 EndZ=0
    g3: ArcOfCircle CenterX=-37.1 CenterY=-5.09999 CenterZ=0 NormalX=0 NormalY=0 NormalZ=1 AngleXU=0 Radius=1.9 StartAngle=6.28318 EndAngle=9.42478
  constraints (9):
    c: Coincident(g0,g-5)
    c: Coincident(g0,g-5)
    c: Coincident(g1,g0)
    c: Coincident(g1,g-4)
    c: Coincident(g2,g1)
    c: Coincident(g2,g-4)
    c: Coincident(g3,g0)
    c: Coincident(g3,g2)
    c: Tangent(g3,g-3)
FEATURE [PartDesign::Pocket] Pocket004
  BaseFeature = -> Pocket003
  Direction = (0,-1,2e-16)
  Length = 2
  Length2 = 5
  Profile = -> Sketch027
  ReferenceAxis = -> Sketch027 [N_Axis]
  Refine = true
  Suppressed = false
  Type = 0
FEATURE [Sketcher::SketchObject] Sketch028
  ArcFitTolerance = 1e-06
  AttachmentSupport = -> [Pocket004]
  ExternalGeometry = -> [Pocket004]
  FullyConstrained = true
  MakeInternals = false
  MapMode = 5
  Placement = pos=(0,0,-8.2) rot=(1,0,0;3.14159rad)
  sketch-geometry (2):
    g0: Circle CenterX=29.5 CenterY=16.25 CenterZ=0 NormalX=0 NormalY=0 NormalZ=1 AngleXU=0 Radius=1
    g1: LineSegment [constr] StartX=29.5 StartY=16.25 StartZ=0 EndX=30.5 EndY=16.25 EndZ=0
  constraints (6):
    c: Radius(g0) = 1
    c: DistanceY(g-5,g0) = 0
    c: Coincident(g1,g0)
    c: PointOnObject(g1,g0)
    c: Horizontal(g1)
    c: Tangent(g0,g-7)
FEATURE [PartDesign::Pocket] Pocket005
  BaseFeature = -> Pocket004
  Direction = (0,0,1)
  Length = 7
  Length2 = 5
  Profile = -> Sketch028
  ReferenceAxis = -> Sketch028 [N_Axis]
  Refine = true
  Suppressed = false
  Type = 0
FEATURE [Sketcher::SketchObject] Sketch029
  ArcFitTolerance = 1e-06
  AttachmentSupport = -> [Pocket005]
  ExternalGeometry = -> [Pocket005]
  FullyConstrained = true
  MakeInternals = false
  MapMode = 5
  Placement = pos=(0,0,-8.2) rot=(1,0,0;3.14159rad)
  sketch-geometry (1):
    g0: Circle CenterX=29.5 CenterY=16.25 CenterZ=0 NormalX=0 NormalY=0 NormalZ=1 AngleXU=0 Radius=2.1
  constraints (2):
    c: Coincident(g0,g-3)
    c: Diameter(g0) = 4.2
FEATURE [PartDesign::Pocket] Pocket006
  BaseFeature = -> Pocket005
  Direction = (0,0,1)
  Length = 2.1
  Length2 = 5
  Profile = -> Sketch029
  ReferenceAxis = -> Sketch029 [N_Axis]
  Refine = true
  Suppressed = false
  Type = 0
FEATURE [Sketcher::SketchObject] Sketch030
  ArcFitTolerance = 1e-06
  AttachmentSupport = -> [Pocket006]
  ExternalGeometry = -> [Pocket006]
  FullyConstrained = true
  MakeInternals = false
  MapMode = 5
  Placement = pos=(0,0,-6.1) rot=(1,0,0;3.14159rad)
  sketch-geometry (2):
    g0: Circle CenterX=29.5 CenterY=16.25 CenterZ=0 NormalX=0 NormalY=0 NormalZ=1 AngleXU=0 Radius=2.1
    g1: Circle CenterX=29.5 CenterY=16.25 CenterZ=0 NormalX=0 NormalY=0 NormalZ=1 AngleXU=0 Radius=1
  constraints (4):
    c: Coincident(g0,g-3)
    c: Coincident(g1,g0)
    c: Tangent(g1,g-3)
    c: Radius(g0) = 2.1
FEATURE [PartDesign::Pad] Pad023
  BaseFeature = -> Pocket006
  Direction = (0,0,-1)
  Length = 5
  Length2 = 10
  Profile = -> Sketch030
  ReferenceAxis = -> Sketch030 [N_Axis]
  Refine = true
  Reversed = true
  Suppressed = false
  Type = 0
FEATURE [Sketcher::SketchObject] Sketch031
  ArcFitTolerance = 1e-06
  AttachmentSupport = -> [Pad023]
  ExternalGeometry = -> [Pad023]
  FullyConstrained = true
  MakeInternals = false
  MapMode = 5
  Placement = pos=(0,0,-3e-16) rot=(0,0,1;0rad)
  sketch-geometry (1):
    g0: Circle CenterX=29.5 CenterY=-16.25 CenterZ=0 NormalX=0 NormalY=0 NormalZ=1 AngleXU=0 Radius=3
  constraints (2):
    c: Coincident(g0,g-3)
    c: Diameter(g0) = 6
FEATURE [PartDesign::Pocket] Pocket007
  BaseFeature = -> Pad023
  Direction = (0,0,-1)
  Length = 4
  Length2 = 5
  Profile = -> Sketch031
  ReferenceAxis = -> Sketch031 [N_Axis]
  Refine = true
  Suppressed = false
  Type = 0
FEATURE [Sketcher::SketchObject] Sketch032
  ArcFitTolerance = 1e-06
  AttachmentOffset = pos=(0,0,1) rot=(0,0,1;0rad)
  AttachmentSupport = -> [Pocket007]
  ExternalGeometry = -> [Pocket007]
  FullyConstrained = true
  MakeInternals = false
  MapMode = 5
  Placement = pos=(0,0,-7.1) rot=(1,0,0;3.14159rad)
  sketch-geometry (2):
    g0: Circle CenterX=29.5 CenterY=16.25 CenterZ=0 NormalX=0 NormalY=0 NormalZ=1 AngleXU=0 Radius=2.1
    g1: Circle CenterX=29.5 CenterY=16.25 CenterZ=0 NormalX=0 NormalY=0 NormalZ=1 AngleXU=0 Radius=3
  constraints (4):
    c: Coincident(g0,g-3)
    c: Equal(g0,g-3)
    c: Coincident(g1,g0)
    c: Radius(g1) = 3
FEATURE [PartDesign::Pad] Pad024
  BaseFeature = -> Pocket007
  Direction = (0,0,-1)
  Length = 3.1
  Length2 = 10
  Profile = -> Sketch032
  ReferenceAxis = -> Sketch032 [N_Axis]
  Refine = true
  Reversed = true
  Suppressed = false
  Type = 0
FEATURE [Sketcher::SketchObject] Sketch033
  ArcFitTolerance = 1e-06
  AttachmentSupport = -> [Pad024]
  ExternalGeometry = -> [Pad024]
  FullyConstrained = true
  MakeInternals = false
  MapMode = 5
  Placement = pos=(0,0,-7.1) rot=(1,0,0;3.14159rad)
  sketch-geometry (4):
    g0: ArcOfCircle CenterX=29.5 CenterY=16.25 CenterZ=0 NormalX=0 NormalY=0 NormalZ=1 AngleXU=0 Radius=3.5 StartAngle=1.5488 EndAngle=4.73439
    g1: LineSegment StartX=29.577 StartY=19.249 StartZ=0 EndX=29.577 EndY=19.7492 EndZ=0
    g2: LineSegment StartX=29.577 StartY=13.251 StartZ=0 EndX=29.577 EndY=12.7508 EndZ=0
    g3: ArcOfCircle CenterX=29.5 CenterY=16.25 CenterZ=0 NormalX=0 NormalY=0 NormalZ=1 AngleXU=0 Radius=3 StartAngle=1.54513 EndAngle=4.73806
  constraints (11):
    c: Coincident(g0,g-4)
    c: Coincident(g1,g-4)
    c: Coincident(g1,g0)
    c: Coincident(g2,g-5)
    c: Coincident(g2,g0)
    c: Vertical(g1)
    c: Vertical(g2)
    c: Radius(g0) = 3.5
    c: Coincident(g3,g2)
    c: Coincident(g3,g1)
    c: Tangent(g3,g-4)
FEATURE [PartDesign::Pad] Pad025
  BaseFeature = -> Pad024
  Direction = (0,0,-1)
  Length = 4
  Length2 = 10
  Profile = -> Sketch033
  ReferenceAxis = -> Sketch033 [N_Axis]
  Refine = true
  Reversed = true
  Suppressed = false
  Type = 0
FEATURE [PartDesign::Pad] Pad026
  BaseFeature = -> Pad025
  Direction = (0,0,1)
  Length = 1
  Length2 = 10
  Profile = -> Pad025 [Face118]
  Refine = true
  Suppressed = false
  Type = 0
FEATURE [Sketcher::SketchObject] Sketch034
  ArcFitTolerance = 1e-06
  AttachmentSupport = -> [Pad026]
  ExternalGeometry = -> [Pad026]
  FullyConstrained = true
  MakeInternals = false
  MapMode = 5
  Placement = pos=(0,0,-2.5) rot=(1,0,0;3.14159rad)
  sketch-geometry (1):
    g0: Circle CenterX=20.6 CenterY=16.25 CenterZ=0 NormalX=0 NormalY=0 NormalZ=1 AngleXU=0 Radius=2
  constraints (2):
    c: Coincident(g0,g-3)
    c: Diameter(g0) = 4
FEATURE [PartDesign::Pad] Pad027
  BaseFeature = -> Pad026
  Direction = (0,0,-1)
  Length = 7.8
  Length2 = 10
  Profile = -> Sketch034
  ReferenceAxis = -> Sketch034 [N_Axis]
  Refine = true
  Suppressed = false
  Type = 0
FEATURE [Sketcher::SketchObject] Sketch035
  ArcFitTolerance = 1e-06
  AttachmentSupport = -> [Pad027]
  ExternalGeometry = -> [Pad027]
  FullyConstrained = true
  MakeInternals = false
  MapMode = 5
  Placement = pos=(0,0,-10.3) rot=(1,0,0;3.14159rad)
  sketch-geometry (1):
    g0: Circle CenterX=20.6 CenterY=16.25 CenterZ=0 NormalX=0 NormalY=0 NormalZ=1 AngleXU=0 Radius=0.75
  constraints (2):
    c: Coincident(g0,g-3)
    c: Radius(g0) = 0.75
FEATURE [PartDesign::Pocket] Pocket008
  BaseFeature = -> Pad027
  Direction = (0,0,1)
  Length = 8
  Length2 = 5
  Profile = -> Sketch035
  ReferenceAxis = -> Sketch035 [N_Axis]
  Refine = true
  Suppressed = false
  Type = 0
FEATURE [Sketcher::SketchObject] Sketch036
  ArcFitTolerance = 1e-06
  AttachmentSupport = -> [Pocket008]
  ExternalGeometry = -> [Pocket008]
  FullyConstrained = true
  MakeInternals = false
  MapMode = 5
  Placement = pos=(0,0,-2.5) rot=(1,0,0;3.14159rad)
  sketch-geometry (2):
    g0: Circle CenterX=20.6 CenterY=16.25 CenterZ=0 NormalX=0 NormalY=0 NormalZ=1 AngleXU=0 Radius=2
    g1: Circle CenterX=20.6 CenterY=16.25 CenterZ=0 NormalX=0 NormalY=0 NormalZ=1 AngleXU=0 Radius=3.5
  constraints (4):
    c: Coincident(g0,g-4)
    c: Equal(g0,g-4)
    c: Coincident(g1,g0)
    c: Diameter(g1) = 7
FEATURE [PartDesign::Pad] Pad028
  BaseFeature = -> Pocket008
  Direction = (0,0,-1)
  Length = 1.5
  Length2 = 10
  Profile = -> Sketch036
  ReferenceAxis = -> Sketch036 [N_Axis]
  Refine = true
  Suppressed = false
  Type = 0
FEATURE [Sketcher::SketchObject] Sketch037
  ArcFitTolerance = 1e-06
  AttachmentSupport = -> [Pad028]
  ExternalGeometry = -> [Pad028]
  FullyConstrained = true
  MakeInternals = false
  MapMode = 5
  Placement = pos=(0,0,-4) rot=(1,0,0;3.14159rad)
  sketch-geometry (12):
    g0: LineSegment [constr] StartX=20.6 StartY=16.25 StartZ=0 EndX=20.6 EndY=19.75 EndZ=0
    g1: LineSegment [constr] StartX=20.6 StartY=16.25 StartZ=0 EndX=24.1 EndY=16.25 EndZ=0
    g2: LineSegment [constr] StartX=20.6 StartY=16.25 StartZ=0 EndX=20.6 EndY=12.75 EndZ=0
    g3: LineSegment [constr] StartX=20.6 StartY=16.25 StartZ=0 EndX=17.1 EndY=16.25 EndZ=0
    g4: LineSegment [constr] StartX=20.6 StartY=16.25 StartZ=0 EndX=18.1251 EndY=13.7751 EndZ=0
    g5: LineSegment [constr] StartX=20.6 StartY=16.25 StartZ=0 EndX=23.0749 EndY=13.7751 EndZ=0
    g6: LineSegment [constr] StartX=20.6 StartY=16.25 StartZ=0 EndX=23.0749 EndY=18.7249 EndZ=0
    g7: LineSegment [constr] StartX=20.6 StartY=16.25 StartZ=0 EndX=18.1251 EndY=18.7249 EndZ=0
    g8: LineSegment StartX=18.6025 StartY=16.35 StartZ=0 EndX=17.1014 EndY=16.35 EndZ=0
    g9: LineSegment StartX=18.6025 StartY=16.15 StartZ=0 EndX=17.1014 EndY=16.15 EndZ=0
    g10: ArcOfCircle CenterX=20.6 CenterY=16.25 CenterZ=0 NormalX=0 NormalY=0 NormalZ=1 AngleXU=0 Radius=2 StartAngle=3.09157 EndAngle=3.19161
    g11: ArcOfCircle CenterX=20.6 CenterY=16.25 CenterZ=0 NormalX=0 NormalY=0 NormalZ=1 AngleXU=0 Radius=3.5 StartAngle=3.11302 EndAngle=3.17017
  constraints (38):
    c: Coincident(g0,g-4)
    c: Vertical(g0)
    c: Coincident(g1,g0)
    c: PointOnObject(g1,g-3)
    c: Horizontal(g1)
    c: Coincident(g2,g0)
    c: PointOnObject(g2,g-3)
    c: Vertical(g2)
    c: Coincident(g3,g0)
    c: PointOnObject(g3,g-3)
    c: Horizontal(g3)
    c: Coincident(g4,g0)
    c: PointOnObject(g4,g-3)
    c: Coincident(g5,g0)
    c: PointOnObject(g5,g-3)
    c: Coincident(g6,g0)
    c: PointOnObject(g6,g-3)
    c: Coincident(g7,g0)
    c: PointOnObject(g7,g-3)
    c: Angle(g0,g7) = 0.785398
    c: Angle(g6,g0) = 0.785398
    c: Angle(g5,g1) = 0.785398
    c: Angle(g4,g2) = 0.785398
    c: PointOnObject(g0,g-3)
    c: PointOnObject(g8,g-4)
    c: PointOnObject(g8,g-3)
    c: Horizontal(g8)
    c: PointOnObject(g9,g-4)
    c: PointOnObject(g9,g-3)
    c: Horizontal(g9)
    c: DistanceY(g3,g8) = 0.1
    c: DistanceY(g9,g3) = 0.1
    c: Coincident(g10,g8)
    c: Coincident(g10,g9)
    c: Tangent(g-4,g10)
    c: Coincident(g11,g9)
    c: Coincident(g11,g8)
    c: Tangent(g11,g-3)
FEATURE [PartDesign::Pocket] Pocket009
  BaseFeature = -> Pad028
  Direction = (0,0,1)
  Length = 1.5
  Length2 = 5
  Profile = -> Sketch037
  ReferenceAxis = -> Sketch037 [N_Axis]
  Refine = true
  Suppressed = false
  Type = 0
FEATURE [Sketcher::SketchObject] Sketch038
  ArcFitTolerance = 1e-06
  AttachmentSupport = -> [Pocket009]
  ExternalGeometry = -> [Pocket009]
  FullyConstrained = true
  MakeInternals = false
  MapMode = 5
  Placement = pos=(0,0,-4) rot=(1,0,0;3.14159rad)
  sketch-geometry (5):
    g0: LineSegment [constr] StartX=20.6 StartY=16.25 StartZ=0 EndX=24.1 EndY=16.25 EndZ=0
    g1: LineSegment StartX=24.0986 StartY=16.35 StartZ=0 EndX=22.5975 EndY=16.35 EndZ=0
    g2: LineSegment StartX=24.0986 StartY=16.15 StartZ=0 EndX=22.5975 EndY=16.15 EndZ=0
    g3: ArcOfCircle CenterX=20.6 CenterY=16.25 CenterZ=0 NormalX=0 NormalY=0 NormalZ=1 AngleXU=0 Radius=3.5 StartAngle=6.25461 EndAngle=6.31176
    g4: ArcOfCircle CenterX=20.6 CenterY=16.25 CenterZ=0 NormalX=0 NormalY=0 NormalZ=1 AngleXU=0 Radius=2 StartAngle=6.23316 EndAngle=6.33321
  constraints (16):
    c: Coincident(g0,g-4)
    c: Coincident(g0,g-4)
    c: PointOnObject(g1,g-3)
    c: Horizontal(g1)
    c: PointOnObject(g2,g-4)
    c: Horizontal(g2)
    c: DistanceY(g0,g1) = 0.1
    c: DistanceY(g2,g0) = 0.1
    c: Coincident(g3,g1)
    c: Coincident(g3,g2)
    c: PointOnObject(g2,g-6)
    c: PointOnObject(g1,g-5)
    c: PointOnObject(g0,g3)
    c: Coincident(g4,g1)
    c: Coincident(g4,g2)
    c: Tangent(g4,g-5)
FEATURE [PartDesign::Pocket] Pocket010
  BaseFeature = -> Pocket009
  Direction = (0,0,1)
  Length = 1.5
  Length2 = 5
  Profile = -> Sketch038
  ReferenceAxis = -> Sketch038 [N_Axis]
  Refine = true
  Suppressed = false
  Type = 0
FEATURE [Sketcher::SketchObject] Sketch039
  ArcFitTolerance = 1e-06
  AttachmentSupport = -> [Pocket010]
  ExternalGeometry = -> [Pocket010]
  FullyConstrained = true
  MakeInternals = false
  MapMode = 5
  Placement = pos=(0,0,-4) rot=(1,0,0;3.14159rad)
  sketch-geometry (6):
    g0: LineSegment [constr] StartX=20.6 StartY=16.25 StartZ=0 EndX=23.0749 EndY=18.7249 EndZ=0
    g1: LineSegment [constr] StartX=20.6 StartY=16.25 StartZ=0 EndX=24.6 EndY=16.25 EndZ=0
    g2: LineSegment StartX=23.0032 StartY=18.7946 StartZ=0 EndX=21.9417 EndY=17.7331 EndZ=0
    g3: LineSegment StartX=23.1446 StartY=18.6532 StartZ=0 EndX=22.0831 EndY=17.5917 EndZ=0
    g4: ArcOfCircle CenterX=20.6 CenterY=16.25 CenterZ=0 NormalX=0 NormalY=0 NormalZ=1 AngleXU=0 Radius=3.5 StartAngle=0.756826 EndAngle=0.813971
    g5: ArcOfCircle CenterX=20.6 CenterY=16.25 CenterZ=0 NormalX=0 NormalY=0 NormalZ=1 AngleXU=0 Radius=2 StartAngle=0.735382 EndAngle=0.835414
  constraints (20):
    c: Coincident(g0,g-4)
    c: PointOnObject(g0,g-3)
    c: Coincident(g1,g0)
    c: Horizontal(g1)
    c: DistanceX(g1,g1) = 4
    c: Angle(g1,g0) = 0.785398
    c: PointOnObject(g2,g-3)
    c: PointOnObject(g2,g-4)
    c: PointOnObject(g3,g-3)
    c: PointOnObject(g3,g-4)
    c: Parallel(g0,g2)
    c: Parallel(g0,g3)
    c: Distance(g0,g2) = 0.1
    c: Distance(g0,g3) = 0.1
    c: Coincident(g4,g2)
    c: Coincident(g4,g3)
    c: Coincident(g5,g2)
    c: Coincident(g5,g3)
    c: Tangent(g5,g-4)
    c: Tangent(g4,g-3)
FEATURE [PartDesign::Pocket] Pocket011
  BaseFeature = -> Pocket010
  Direction = (0,0,1)
  Length = 1.5
  Length2 = 5
  Profile = -> Sketch039
  ReferenceAxis = -> Sketch039 [N_Axis]
  Refine = true
  Suppressed = false
  Type = 0
FEATURE [Sketcher::SketchObject] Sketch040
  ArcFitTolerance = 1e-06
  AttachmentSupport = -> [Pocket011]
  ExternalGeometry = -> [Pocket011]
  FullyConstrained = true
  MakeInternals = false
  MapMode = 5
  Placement = pos=(0,0,-4) rot=(1,0,0;3.14159rad)
  sketch-geometry (6):
    g0: LineSegment [constr] StartX=20.6 StartY=16.25 StartZ=0 EndX=18.1251 EndY=18.7249 EndZ=0
    g1: LineSegment [constr] StartX=20.6 StartY=16.25 StartZ=0 EndX=16.6 EndY=16.25 EndZ=0
    g2: LineSegment StartX=18.1968 StartY=18.7946 StartZ=0 EndX=19.2583 EndY=17.7331 EndZ=0
    g3: LineSegment StartX=18.0554 StartY=18.6532 StartZ=0 EndX=19.1169 EndY=17.5917 EndZ=0
    g4: ArcOfCircle CenterX=20.6 CenterY=16.25 CenterZ=0 NormalX=0 NormalY=0 NormalZ=1 AngleXU=0 Radius=3.5 StartAngle=2.32762 EndAngle=2.38477
    g5: ArcOfCircle CenterX=20.6 CenterY=16.25 CenterZ=0 NormalX=0 NormalY=0 NormalZ=1 AngleXU=0 Radius=1.99994 StartAngle=2.30618 EndAngle=2.40621
  constraints (20):
    c: Coincident(g0,g-4)
    c: PointOnObject(g0,g-3)
    c: Coincident(g1,g0)
    c: Horizontal(g1)
    c: DistanceX(g1,g1) = 4
    c: Angle(g0,g1) = 0.785398
    c: PointOnObject(g2,g-3)
    c: PointOnObject(g2,g-4)
    c: PointOnObject(g3,g-3)
    c: PointOnObject(g3,g-4)
    c: Distance(g0,g3) = 0.1
    c: Distance(g0,g2) = 0.1
    c: Parallel(g0,g3)
    c: Parallel(g0,g2)
    c: Coincident(g4,g3)
    c: Coincident(g4,g2)
    c: Coincident(g5,g3)
    c: Coincident(g5,g2)
    c: Tangent(g4,g-3)
    c: Tangent(g5,g-4)
FEATURE [PartDesign::Pocket] Pocket012
  BaseFeature = -> Pocket011
  Direction = (0,0,1)
  Length = 1.5
  Length2 = 5
  Profile = -> Sketch040
  ReferenceAxis = -> Sketch040 [N_Axis]
  Refine = true
  Suppressed = false
  Type = 0
FEATURE [Sketcher::SketchObject] Sketch041
  ArcFitTolerance = 1e-06
  AttachmentSupport = -> [Pocket012]
  ExternalGeometry = -> [Pocket012]
  FullyConstrained = true
  MakeInternals = false
  MapMode = 5
  Placement = pos=(0,0,-4) rot=(1,0,0;3.14159rad)
  sketch-geometry (5):
    g0: LineSegment [constr] StartX=20.6 StartY=16.25 StartZ=0 EndX=20.6 EndY=19.75 EndZ=0
    g1: LineSegment StartX=20.5 StartY=19.7486 StartZ=0 EndX=20.5 EndY=18.2475 EndZ=0
    g2: LineSegment StartX=20.7 StartY=19.7486 StartZ=0 EndX=20.7 EndY=18.2475 EndZ=0
    g3: ArcOfCircle CenterX=20.6 CenterY=16.25 CenterZ=0 NormalX=0 NormalY=0 NormalZ=1 AngleXU=0 Radius=1.99997 StartAngle=1.52077 EndAngle=1.62082
    g4: ArcOfCircle CenterX=20.6 CenterY=16.25 CenterZ=0 NormalX=0 NormalY=0 NormalZ=1 AngleXU=0 Radius=3.5 StartAngle=1.54222 EndAngle=1.59937
  constraints (17):
    c: Coincident(g0,g-4)
    c: PointOnObject(g0,g-3)
    c: Vertical(g0)
    c: PointOnObject(g1,g-3)
    c: PointOnObject(g1,g-4)
    c: PointOnObject(g2,g-3)
    c: PointOnObject(g2,g-4)
    c: DistanceX(g1,g0) = 0.1
    c: DistanceX(g0,g2) = 0.1
    c: Vertical(g1)
    c: Vertical(g2)
    c: Coincident(g3,g1)
    c: Coincident(g3,g2)
    c: Coincident(g4,g1)
    c: Coincident(g4,g2)
    c: Tangent(g4,g-3)
    c: Tangent(g3,g-4)
FEATURE [PartDesign::Pocket] Pocket013
  BaseFeature = -> Pocket012
  Direction = (0,0,1)
  Length = 1.5
  Length2 = 5
  Profile = -> Sketch041
  ReferenceAxis = -> Sketch041 [N_Axis]
  Refine = true
  Suppressed = false
  Type = 0
FEATURE [Sketcher::SketchObject] Sketch042
  ArcFitTolerance = 1e-06
  AttachmentSupport = -> [Pocket013]
  ExternalGeometry = -> [Pocket013]
  FullyConstrained = true
  MakeInternals = false
  MapMode = 5
  Placement = pos=(0,0,-10.3) rot=(1,0,0;3.14159rad)
  sketch-geometry (2):
    g0: Circle CenterX=20.6 CenterY=16.25 CenterZ=0 NormalX=0 NormalY=0 NormalZ=1 AngleXU=0 Radius=2
    g1: Circle CenterX=20.6 CenterY=16.25 CenterZ=0 NormalX=0 NormalY=0 NormalZ=1 AngleXU=0 Radius=1.95
  constraints (5):
    c: Coincident(g0,g-3)
    c: Equal(g0,g-3)
    c: Coincident(g1,g0)
    c: Radius(g0) = 2
    c: Radius(g1) = 1.95
FEATURE [PartDesign::Pocket] Pocket014
  BaseFeature = -> Pocket013
  Direction = (0,0,1)
  Length = 7.8
  Length2 = 5
  Profile = -> Sketch042
  ReferenceAxis = -> Sketch042 [N_Axis]
  Refine = true
  Suppressed = false
  Type = 0
FEATURE [PartDesign::Chamfer] Chamfer
  Angle = 45
  Base = -> Pocket014 [Edge1389,Edge1393,Edge1381,Edge1385,Edge1397,Edge1401,Edge1372,Edge1409,Edge1407,Edge1368]
  BaseFeature = -> Pocket014
  ChamferType = 0
  FlipDirection = false
  Refine = true
  Size = 0.6
  Size2 = 1
  SupportTransform = false
  Suppressed = false
  UseAllEdges = false
FEATURE [Sketcher::SketchObject] Sketch043
  ArcFitTolerance = 1e-06
  AttachmentSupport = -> [Chamfer]
  ExternalGeometry = -> [Chamfer]
  FullyConstrained = true
  MakeInternals = false
  MapMode = 5
  Placement = pos=(0,0,-4) rot=(1,0,0;3.14159rad)
  sketch-geometry (15):
    g0: LineSegment [constr] StartX=20.6 StartY=16.25 StartZ=0 EndX=20.6 EndY=12.75 EndZ=0
    g1: LineSegment [constr] StartX=20.6 StartY=16.25 StartZ=0 EndX=18.1251 EndY=13.7751 EndZ=0
    g2: LineSegment [constr] StartX=20.6 StartY=16.25 StartZ=0 EndX=23.0749 EndY=13.7751 EndZ=0
    g3: LineSegment StartX=20.7 StartY=14.2525 StartZ=0 EndX=20.7 EndY=12.7514 EndZ=0
    g4: LineSegment StartX=20.5 StartY=14.2525 StartZ=0 EndX=20.5 EndY=12.7514 EndZ=0
    g5: LineSegment StartX=19.2583 StartY=14.7669 StartZ=0 EndX=18.1968 EndY=13.7054 EndZ=0
    g6: LineSegment StartX=19.1169 StartY=14.9083 StartZ=0 EndX=18.0554 EndY=13.8468 EndZ=0
    g7: LineSegment StartX=21.9417 StartY=14.7669 StartZ=0 EndX=23.0032 EndY=13.7054 EndZ=0
    g8: LineSegment StartX=22.0831 StartY=14.9083 StartZ=0 EndX=23.1446 EndY=13.8468 EndZ=0
    g9: ArcOfCircle CenterX=20.6 CenterY=16.25 CenterZ=0 NormalX=0 NormalY=0 NormalZ=1 AngleXU=0 Radius=2 StartAngle=3.87698 EndAngle=3.97701
    g10: ArcOfCircle CenterX=20.6 CenterY=16.25 CenterZ=0 NormalX=0 NormalY=0 NormalZ=1 AngleXU=0 Radius=3.5 StartAngle=3.89842 EndAngle=3.95556
    g11: ArcOfCircle CenterX=20.6 CenterY=16.25 CenterZ=0 NormalX=0 NormalY=0 NormalZ=1 AngleXU=0 Radius=2 StartAngle=4.66237 EndAngle=4.76241
    g12: ArcOfCircle CenterX=20.6 CenterY=16.25 CenterZ=0 NormalX=0 NormalY=0 NormalZ=1 AngleXU=0 Radius=3.5 StartAngle=4.68381 EndAngle=4.74096
    g13: ArcOfCircle CenterX=20.6 CenterY=16.25 CenterZ=0 NormalX=0 NormalY=0 NormalZ=1 AngleXU=0 Radius=1.99996 StartAngle=5.44777 EndAngle=5.5478
    g14: ArcOfCircle CenterX=20.6 CenterY=16.25 CenterZ=0 NormalX=0 NormalY=0 NormalZ=1 AngleXU=0 Radius=3.5 StartAngle=5.46921 EndAngle=5.52636
  constraints (51):
    c: Coincident(g0,g-4)
    c: PointOnObject(g0,g-4)
    c: Vertical(g0)
    c: Coincident(g1,g0)
    c: PointOnObject(g1,g-4)
    c: Coincident(g2,g0)
    c: PointOnObject(g2,g-4)
    c: Angle(g1,g0) = 0.785398
    c: Angle(g0,g2) = 0.785398
    c: PointOnObject(g3,g-3)
    c: PointOnObject(g3,g-4)
    c: PointOnObject(g4,g-3)
    c: PointOnObject(g4,g-4)
    c: PointOnObject(g5,g-3)
    c: PointOnObject(g5,g-4)
    c: PointOnObject(g6,g-3)
    c: PointOnObject(g6,g-4)
    c: PointOnObject(g7,g-3)
    c: PointOnObject(g7,g-4)
    c: PointOnObject(g8,g-3)
    c: PointOnObject(g8,g-4)
    c: Vertical(g4)
    c: Vertical(g3)
    c: Parallel(g2,g7)
    c: Parallel(g2,g8)
    c: Parallel(g5,g1)
    c: Parallel(g1,g6)
    c: DistanceX(g4,g0) = 0.1
    c: DistanceX(g0,g3) = 0.1
    c: Distance(g2,g7) = 0.1
    c: Distance(g2,g8) = 0.1
    c: Distance(g5,g1) = 0.1
    c: Distance(g6,g1) = 0.1
    c: Coincident(g9,g5)
    c: Coincident(g9,g6)
    c: Coincident(g10,g5)
    c: Coincident(g10,g6)
    c: Tangent(g10,g-4)
    c: Tangent(g9,g-3)
    c: Coincident(g11,g4)
    c: Coincident(g11,g3)
    c: Coincident(g12,g4)
    c: Coincident(g12,g3)
    c: Tangent(g12,g-4)
    c: Tangent(g11,g-3)
    c: Coincident(g13,g7)
    c: Coincident(g13,g8)
    c: Coincident(g14,g7)
    c: Coincident(g14,g8)
    c: Tangent(g14,g-4)
    c: Tangent(g13,g-3)
FEATURE [PartDesign::Pocket] Pocket015
  BaseFeature = -> Chamfer
  Direction = (0,0,1)
  Length = 1.5
  Length2 = 5
  Profile = -> Sketch043
  ReferenceAxis = -> Sketch043 [N_Axis]
  Refine = true
  Suppressed = false
  Type = 0
FEATURE [PartDesign::Chamfer] Chamfer001
  Angle = 45
  Base = -> Pocket015 [Edge1407,Edge1415,Edge1412,Edge1451,Edge1448,Edge1461]
  BaseFeature = -> Pocket015
  ChamferType = 0
  FlipDirection = false
  Refine = true
  Size = 0.6
  Size2 = 1
  SupportTransform = false
  Suppressed = false
  UseAllEdges = false
FEATURE [Sketcher::SketchObject] Sketch044
  ArcFitTolerance = 1e-06
  AttachmentSupport = -> [Chamfer001]
  ExternalGeometry = -> [Chamfer001]
  FullyConstrained = true
  MakeInternals = false
  MapMode = 5
  Placement = pos=(0,0,14.2) rot=(0,0,1;0rad)
  sketch-geometry (2):
    g0: Circle CenterX=28.65 CenterY=-5.5 CenterZ=0 NormalX=0 NormalY=0 NormalZ=1 AngleXU=0 Radius=1.45
    g1: LineSegment [constr] StartX=28.65 StartY=-5.5 StartZ=0 EndX=27.2 EndY=-5.5 EndZ=0
  constraints (7):
    c: Radius(g0) = 1.45
    c: DistanceY(g-3,g-3) = 11
    c: DistanceY(g-3,g0) = 5.5
    c: Coincident(g1,g0)
    c: PointOnObject(g1,g0)
    c: Horizontal(g1)
    c: DistanceX(g-3,g1) = 4.9
FEATURE [PartDesign::Pocket] Pocket016
  BaseFeature = -> Chamfer001
  Direction = (0,0,-1)
  Length = 5
  Length2 = 5
  Profile = -> Sketch044
  ReferenceAxis = -> Sketch044 [N_Axis]
  Refine = true
  Suppressed = false
  Type = 0
FEATURE [PartDesign::SubShapeBinder] Binder
  BindCopyOnChange = 0
  BindMode = 2
  ClaimChildren = false
  Context = -> Body001 [Binder.]
  Fuse = false
  MakeFace = true
  OffsetFill = false
  OffsetIntersection = false
  OffsetJoinType = 0
  OffsetOpenResult = false
  PartialLoad = false
  Refine = true
  Relative = true
  _Version = 2
FEATURE [Sketcher::SketchObject] Sketch045
  ArcFitTolerance = 1e-06
  AttachmentSupport = -> [Binder]
  ExternalGeometry = -> [Binder]
  FullyConstrained = true
  MakeInternals = false
  MapMode = 5
  Placement = pos=(0,0,0) rot=(1,0,0;3.14159rad)
  sketch-geometry (8):
    g0: LineSegment StartX=3.5 StartY=24.5 StartZ=0 EndX=40 EndY=24.5 EndZ=0
    g1: LineSegment StartX=40 StartY=24.5 StartZ=0 EndX=40 EndY=32 EndZ=0
    g2: LineSegment StartX=40 StartY=32 StartZ=0 EndX=38.5 EndY=32 EndZ=0
    g3: LineSegment StartX=38.5 StartY=32 StartZ=0 EndX=38.5 EndY=26 EndZ=0
    g4: LineSegment StartX=2 StartY=26 StartZ=0 EndX=38.5 EndY=26 EndZ=0
    g5: LineSegment StartX=2 StartY=26 StartZ=0 EndX=2 EndY=20.5 EndZ=0
    g6: LineSegment StartX=2 StartY=20.5 StartZ=0 EndX=3.5 EndY=20.5 EndZ=0
    g7: LineSegment StartX=3.5 StartY=20.5 StartZ=0 EndX=3.5 EndY=24.5 EndZ=0
  constraints (23):
    c: Horizontal(g0)
    c: Coincident(g1,g0)
    c: Vertical(g1)
    c: Coincident(g2,g1)
    c: Horizontal(g2)
    c: Coincident(g3,g2)
    c: Vertical(g3)
    c: Horizontal(g4)
    c: Coincident(g4,g3)
    c: Coincident(g5,g4)
    c: Vertical(g5)
    c: Coincident(g6,g5)
    c: Horizontal(g6)
    c: Coincident(g7,g6)
    c: Coincident(g0,g7)
    c: Vertical(g7)
    c: DistanceY(g4,g-20) = 6
    c: DistanceY(g0,g3) = 1.5
    c: DistanceX(g2,g1) = 1.5
    c: PointOnObject(g2,g-3)
    c: DistanceX(g6,g6) = 1.5
    c: Coincident(g5,g-22)
    c: DistanceX(g4,g4) = 36.5
FEATURE [PartDesign::Pad] Pad029
  Direction = (0,0,-1)
  Length = 8.2
  Length2 = 10
  Profile = -> Sketch045
  ReferenceAxis = -> Sketch045 [N_Axis]
  Refine = true
  Suppressed = false
  Type = 0
FEATURE [Sketcher::SketchObject] Sketch046
  ArcFitTolerance = 1e-06
  AttachmentSupport = -> [Pad029]
  ExternalGeometry = -> [Pad029]
  FullyConstrained = true
  MakeInternals = false
  MapMode = 5
  Placement = pos=(0,-26,0) rot=(1,0,0;1.5708rad)
  sketch-geometry (6):
    g0: LineSegment StartX=9 StartY=0 StartZ=0 EndX=9 EndY=-4 EndZ=0
    g1: LineSegment StartX=13 StartY=0 StartZ=0 EndX=13 EndY=-4 EndZ=0
    g2: ArcOfCircle CenterX=11 CenterY=-4 CenterZ=0 NormalX=0 NormalY=0 NormalZ=1 AngleXU=0 Radius=2 StartAngle=3.14159 EndAngle=6.28319
    g3: LineSegment StartX=9 StartY=0 StartZ=0 EndX=13 EndY=0 EndZ=0
    g4: LineSegment [constr] StartX=9 StartY=-4 StartZ=0 EndX=13 EndY=-4 EndZ=0
    g5: LineSegment [constr] StartX=11 StartY=-4 StartZ=0 EndX=11 EndY=-6 EndZ=0
  constraints (18):
    c: PointOnObject(g0,g-3)
    c: Vertical(g0)
    c: PointOnObject(g1,g-3)
    c: Vertical(g1)
    c: Coincident(g2,g0)
    c: Coincident(g2,g1)
    c: Coincident(g3,g0)
    c: Coincident(g3,g1)
    c: Coincident(g4,g0)
    c: Coincident(g4,g1)
    c: Horizontal(g4)
    c: PointOnObject(g2,g4)
    c: Diameter(g2) = 4
    c: DistanceX(g-5,g0) = 7
    c: Coincident(g5,g2)
    c: PointOnObject(g5,g2)
    c: Vertical(g5)
    c: DistanceY(g5,g0) = 6
FEATURE [PartDesign::Pocket] Pocket017
  BaseFeature = -> Pad029
  Direction = (0,1,-2e-16)
  Length = 5
  Length2 = 5
  Profile = -> Sketch046
  ReferenceAxis = -> Sketch046 [N_Axis]
  Refine = true
  Suppressed = false
  Type = 0
FEATURE [Sketcher::SketchObject] Sketch047
  ArcFitTolerance = 1e-06
  AttachmentSupport = -> [Pocket017]
  ExternalGeometry = -> [Pocket017]
  FullyConstrained = true
  MakeInternals = false
  MapMode = 5
  Placement = pos=(0,0,-8.2) rot=(1,0,0;3.14159rad)
  sketch-geometry (24):
    g0: LineSegment StartX=38.5 StartY=32 StartZ=0 EndX=38.5 EndY=26 EndZ=0
    g1: LineSegment StartX=38.5 StartY=26 StartZ=0 EndX=26.5 EndY=26 EndZ=0
    g2: LineSegment StartX=26.5 StartY=26 StartZ=0 EndX=20.5 EndY=32 EndZ=0
    g3: LineSegment StartX=20.5 StartY=32 StartZ=0 EndX=2 EndY=32 EndZ=0
    g4: LineSegment StartX=2 StartY=32 StartZ=0 EndX=2 EndY=20.5 EndZ=0
    g5: LineSegment StartX=2 StartY=20.5 StartZ=0 EndX=6.8 EndY=20.5 EndZ=0
    g6: LineSegment StartX=6.8 StartY=20.5 StartZ=0 EndX=6.8 EndY=11.75 EndZ=0
    g7: LineSegment StartX=6.8 StartY=11.75 StartZ=0 EndX=2 EndY=11.75 EndZ=0
    g8: LineSegment StartX=2 StartY=11.75 StartZ=0 EndX=2 EndY=0 EndZ=0
    g9: LineSegment StartX=2 StartY=0 StartZ=0 EndX=20.5 EndY=0 EndZ=0
    g10: LineSegment StartX=20.5 StartY=0 StartZ=0 EndX=26.5 EndY=6 EndZ=0
    g11: LineSegment StartX=26.5 StartY=6 StartZ=0 EndX=38.5 EndY=6 EndZ=0
    g12: LineSegment StartX=38.5 StartY=6 StartZ=0 EndX=38.5 EndY=0 EndZ=0
    g13: LineSegment StartX=38.5 StartY=0 StartZ=0 EndX=42.5 EndY=0 EndZ=0
    g14: LineSegment StartX=42.5 StartY=0 StartZ=0 EndX=47.7 EndY=5.2 EndZ=0
    g15: LineSegment StartX=47.7 StartY=5.2 StartZ=0 EndX=47.7 EndY=9.2 EndZ=0
    g16: LineSegment StartX=47.7 StartY=9.2 StartZ=0 EndX=50.7 EndY=9.2 EndZ=0
    g17: LineSegment StartX=50.7 StartY=9.2 StartZ=0 EndX=55.8 EndY=14.3 EndZ=0
    g18: LineSegment StartX=55.8 StartY=14.3 StartZ=0 EndX=55.8 EndY=17.7 EndZ=0
    g19: LineSegment StartX=55.8 StartY=17.7 StartZ=0 EndX=50.7 EndY=22.8 EndZ=0
    g20: LineSegment StartX=50.7 StartY=22.8 StartZ=0 EndX=47.7 EndY=22.8 EndZ=0
    g21: LineSegment StartX=47.7 StartY=22.8 StartZ=0 EndX=47.7 EndY=26.8 EndZ=0
    g22: LineSegment StartX=42.5 StartY=32 StartZ=0 EndX=47.7 EndY=26.8 EndZ=0
    g23: LineSegment StartX=38.5 StartY=32 StartZ=0 EndX=42.5 EndY=32 EndZ=0
  constraints (71):
    c: Coincident(g0,g-3)
    c: Coincident(g0,g-4)
    c: Coincident(g1,g0)
    c: PointOnObject(g1,g-4)
    c: Coincident(g2,g1)
    c: Coincident(g3,g2)
    c: Horizontal(g3)
    c: Coincident(g4,g3)
    c: Coincident(g4,g-6)
    c: Vertical(g4)
    c: Coincident(g5,g4)
    c: Horizontal(g5)
    c: Coincident(g6,g5)
    c: Vertical(g6)
    c: Coincident(g7,g6)
    c: Horizontal(g7)
    c: Coincident(g8,g7)
    c: PointOnObject(g8,g-1)
    c: Vertical(g8)
    c: Coincident(g9,g8)
    c: PointOnObject(g9,g-1)
    c: Coincident(g10,g9)
    c: Coincident(g11,g10)
    c: Horizontal(g11)
    c: Coincident(g12,g11)
    c: PointOnObject(g12,g-1)
    c: Vertical(g12)
    c: Coincident(g13,g12)
    c: PointOnObject(g13,g-1)
    c: Coincident(g14,g13)
    c: Coincident(g15,g14)
    c: Vertical(g15)
    c: Coincident(g16,g15)
    c: Horizontal(g16)
    c: Coincident(g17,g16)
    c: Coincident(g18,g17)
    c: Vertical(g18)
    c: Coincident(g19,g18)
    c: Coincident(g20,g19)
    c: Horizontal(g20)
    c: Coincident(g21,g20)
    c: Vertical(g21)
    c: Coincident(g22,g21)
    c: DistanceY(g8,g8) = 11.75
    c: DistanceY(g4,g4) = 11.5
    c: DistanceX(g4,g5) = 4.8
    c: Angle(g10,g9) = 2.35619
    c: Angle(g3,g2) = 2.35619
    c: DistanceX(g1,g1) = 12
    c: DistanceX(g11,g11) = 12
    c: DistanceY(g0,g0) = 6
    c: DistanceY(g12,g12) = 6
    c: Coincident(g23,g0)
    c: Coincident(g23,g22)
    c: Horizontal(g23)
    c: DistanceX(g23,g23) = 4
    c: DistanceX(g13,g13) = 4
    c: DistanceX(g3,g3) = 18.5
    c: DistanceX(g9,g9) = 18.5
    c: DistanceX(g7,g7) = 4.8
    c: DistanceX(g3,g18) = 53.8
    c: DistanceY(g15,g15) = 4
    c: DistanceY(g21,g21) = 4
    c: DistanceX(g20,g20) = 3
    c: DistanceX(g16,g16) = 3
    c: DistanceX(g22,g21) = 5.2
    c: DistanceX(g13,g14) = 5.2
    c: Angle(g14,g13) = 2.35619
    c: Angle(g23,g22) = 2.35619
    c: Angle(g20,g19) = 2.35619
    c: Angle(g17,g16) = 2.35619
FEATURE [PartDesign::Pad] Pad030
  BaseFeature = -> Pocket017
  Direction = (0,0,-1)
  Length = 2
  Length2 = 10
  Profile = -> Sketch047
  ReferenceAxis = -> Sketch047 [N_Axis]
  Refine = true
  Suppressed = false
  Type = 0
FEATURE [PartDesign::Fillet] Fillet001
  Base = -> Pad030 [Edge77,Edge79]
  BaseFeature = -> Pad030
  Radius = 4
  Refine = true
  SupportTransform = false
  Suppressed = false
  UseAllEdges = false
FEATURE [Sketcher::SketchObject] Sketch048
  ArcFitTolerance = 1e-06
  AttachmentSupport = -> [Fillet001]
  ExternalGeometry = -> [Fillet001]
  FullyConstrained = true
  MakeInternals = false
  MapMode = 5
  Placement = pos=(0,0,-8.2) rot=(0,0,1;0rad)
  sketch-geometry (8):
    g0: LineSegment StartX=2 StartY=-11.75 StartZ=0 EndX=2 EndY=-6 EndZ=0
    g1: LineSegment StartX=2 StartY=-6 StartZ=0 EndX=38.5 EndY=-6 EndZ=0
    g2: LineSegment StartX=38.5 StartY=-6 StartZ=0 EndX=38.5 EndY=0 EndZ=0
    g3: LineSegment StartX=38.5 StartY=0 StartZ=0 EndX=40 EndY=0 EndZ=0
    g4: LineSegment StartX=40 StartY=0 StartZ=0 EndX=40 EndY=-7.5 EndZ=0
    g5: LineSegment StartX=40 StartY=-7.5 StartZ=0 EndX=3.5 EndY=-7.5 EndZ=0
    g6: LineSegment StartX=3.5 StartY=-7.5 StartZ=0 EndX=3.5 EndY=-11.75 EndZ=0
    g7: LineSegment StartX=3.5 StartY=-11.75 StartZ=0 EndX=2 EndY=-11.75 EndZ=0
  constraints (28):
    c: DistanceX(g-7,g-7) = 1.5
    c: DistanceX(g-3,g-3) = 1.5
    c: DistanceX(g-4,g-4) = 27
    c: DistanceX(g-9,g-9) = 4
    c: DistanceX(g-8,g-8) = 5.5
    c: DistanceY(g-10,g-10) = 6
    c: DistanceY(g-11,g-11) = 6
    c: Coincident(g0,g-13)
    c: PointOnObject(g0,g-12)
    c: Coincident(g1,g0)
    c: Coincident(g1,g-16)
    c: Horizontal(g1)
    c: Coincident(g2,g1)
    c: Coincident(g2,g-10)
    c: Coincident(g3,g2)
    c: PointOnObject(g3,g-1)
    c: Coincident(g4,g3)
    c: Vertical(g4)
    c: Coincident(g5,g4)
    c: Horizontal(g5)
    c: Coincident(g6,g5)
    c: PointOnObject(g6,g-13)
    c: Vertical(g6)
    c: Coincident(g7,g6)
    c: Coincident(g7,g0)
    c: DistanceX(g7,g7) = 1.5
    c: DistanceX(g3,g3) = 1.5
    c: DistanceY(g4,g1) = 1.5
FEATURE [PartDesign::Pad] Pad031
  BaseFeature = -> Fillet001
  Direction = (0,0,1)
  Length = 8.2
  Length2 = 10
  Profile = -> Sketch048
  ReferenceAxis = -> Sketch048 [N_Axis]
  Refine = true
  Suppressed = false
  Type = 0
FEATURE [Sketcher::SketchObject] Sketch049
  ArcFitTolerance = 1e-06
  AttachmentSupport = -> [Pad031]
  ExternalGeometry = -> [Pad031]
  FullyConstrained = true
  MakeInternals = false
  MapMode = 5
  Placement = pos=(0,-6,0) rot=(0,0.707107,0.707107;3.14159rad)
  sketch-geometry (4):
    g0: LineSegment StartX=-13 StartY=0 StartZ=0 EndX=-9 EndY=0 EndZ=0
    g1: LineSegment StartX=-9 StartY=0 StartZ=0 EndX=-9 EndY=-4 EndZ=0
    g2: LineSegment StartX=-13 StartY=0 StartZ=0 EndX=-13 EndY=-4 EndZ=0
    g3: ArcOfCircle CenterX=-11 CenterY=-4.00001 CenterZ=0 NormalX=0 NormalY=0 NormalZ=1 AngleXU=0 Radius=2 StartAngle=3.14159 EndAngle=6.28319
  constraints (9):
    c: Coincident(g0,g-3)
    c: Coincident(g0,g-4)
    c: Coincident(g1,g0)
    c: Coincident(g1,g-5)
    c: Coincident(g2,g0)
    c: Coincident(g2,g-5)
    c: Coincident(g3,g2)
    c: Coincident(g3,g1)
    c: Tangent(g3,g-5)
FEATURE [PartDesign::Pocket] Pocket018
  BaseFeature = -> Pad031
  Direction = (0,-1,2e-16)
  Length = 5
  Length2 = 5
  Profile = -> Sketch049
  ReferenceAxis = -> Sketch049 [N_Axis]
  Refine = true
  Suppressed = false
  Type = 0
FEATURE [Sketcher::SketchObject] Sketch050
  ArcFitTolerance = 1e-06
  AttachmentSupport = -> [Pocket018]
  ExternalGeometry = -> [Pocket018]
  FullyConstrained = true
  MakeInternals = false
  MapMode = 5
  sketch-geometry (8):
    g0: LineSegment StartX=2 StartY=-6.05 StartZ=0 EndX=2 EndY=-9.05 EndZ=0
    g1: LineSegment StartX=2 StartY=-9.05 StartZ=0 EndX=3.5 EndY=-9.05 EndZ=0
    g2: LineSegment StartX=3.5 StartY=-9.05 StartZ=0 EndX=3.5 EndY=-6.05 EndZ=0
    g3: LineSegment StartX=3.5 StartY=-6.05 StartZ=0 EndX=2 EndY=-6.05 EndZ=0
    g4: LineSegment StartX=3.5 StartY=-26 StartZ=0 EndX=3.5 EndY=-23 EndZ=0
    g5: LineSegment StartX=3.5 StartY=-23 StartZ=0 EndX=2 EndY=-23 EndZ=0
    g6: LineSegment StartX=2 StartY=-23 StartZ=0 EndX=2 EndY=-26 EndZ=0
    g7: LineSegment StartX=2 StartY=-26 StartZ=0 EndX=3.5 EndY=-26 EndZ=0
  constraints (23):
    c: Coincident(g0,g1)
    c: Coincident(g1,g2)
    c: Coincident(g2,g3)
    c: Coincident(g3,g0)
    c: Vertical(g0)
    c: Vertical(g2)
    c: Horizontal(g1)
    c: Horizontal(g3)
    c: PointOnObject(g0,g-6)
    c: PointOnObject(g1,g-7)
    c: Coincident(g4,g5)
    c: Coincident(g5,g6)
    c: Coincident(g6,g7)
    c: Vertical(g4)
    c: Vertical(g6)
    c: Horizontal(g5)
    c: Horizontal(g7)
    c: Distance(g4) = 3
    c: Distance(g0) = 3
    c: DistanceY(g0,g-6) = 0.05
    c: Coincident(g4,g7)
    c: DistanceX(g6,g4) = 1.5
    c: Coincident(g6,g-4)
FEATURE [PartDesign::Pad] Pad032
  BaseFeature = -> Pocket018
  Direction = (0,0,1)
  Length = 0.1
  Length2 = 10
  Profile = -> Sketch050
  ReferenceAxis = -> Sketch050 [N_Axis]
  Refine = true
  Suppressed = false
  Type = 0
FEATURE [Sketcher::SketchObject] Sketch051
  ArcFitTolerance = 1e-06
  AttachmentSupport = -> [Pad032]
  ExternalGeometry = -> [Pad032]
  FullyConstrained = true
  MakeInternals = false
  MapMode = 5
  Placement = pos=(0,0,0.1) rot=(0,0,1;0rad)
  sketch-geometry (8):
    g0: LineSegment StartX=3.5 StartY=-23 StartZ=0 EndX=0.5 EndY=-23 EndZ=0
    g1: LineSegment StartX=0.5 StartY=-23 StartZ=0 EndX=0.5 EndY=-26 EndZ=0
    g2: LineSegment StartX=0.5 StartY=-26 StartZ=0 EndX=3.5 EndY=-26 EndZ=0
    g3: LineSegment StartX=3.5 StartY=-26 StartZ=0 EndX=3.5 EndY=-23 EndZ=0
    g4: LineSegment StartX=3.5 StartY=-6.05 StartZ=0 EndX=0.5 EndY=-6.05 EndZ=0
    g5: LineSegment StartX=0.5 StartY=-6.05 StartZ=0 EndX=0.5 EndY=-9.05 EndZ=0
    g6: LineSegment StartX=0.5 StartY=-9.05 StartZ=0 EndX=3.5 EndY=-9.05 EndZ=0
    g7: LineSegment StartX=3.5 StartY=-9.05 StartZ=0 EndX=3.5 EndY=-6.05 EndZ=0
  constraints (20):
    c: Coincident(g0,g1)
    c: Coincident(g1,g2)
    c: Coincident(g2,g3)
    c: Coincident(g3,g0)
    c: Horizontal(g0)
    c: Horizontal(g2)
    c: Vertical(g1)
    c: Coincident(g0,g-10)
    c: Coincident(g4,g5)
    c: Coincident(g5,g6)
    c: Coincident(g6,g7)
    c: Coincident(g7,g4)
    c: Horizontal(g4)
    c: Horizontal(g6)
    c: Vertical(g5)
    c: Coincident(g4,g-4)
    c: Coincident(g6,g-6)
    c: Coincident(g2,g-8)
    c: DistanceX(g2,g2) = 3
    c: DistanceX(g6,g6) = 3
FEATURE [PartDesign::Pad] Pad033
  BaseFeature = -> Pad032
  Direction = (0,0,1)
  Length = 1.5
  Length2 = 10
  Profile = -> Sketch051
  ReferenceAxis = -> Sketch051 [N_Axis]
  Refine = true
  Suppressed = false
  Type = 0
FEATURE [Sketcher::SketchObject] Sketch052
  ArcFitTolerance = 1e-06
  AttachmentSupport = -> [Pad033]
  ExternalGeometry = -> [Pad033]
  FullyConstrained = true
  MakeInternals = false
  MapMode = 5
  Placement = pos=(0,0,-8.2) rot=(0,0,1;0rad)
  sketch-geometry (8):
    g0: LineSegment StartX=3.5 StartY=-20.5 StartZ=0 EndX=3.5 EndY=-22.5 EndZ=0
    g1: LineSegment StartX=3.5 StartY=-22.5 StartZ=0 EndX=8 EndY=-22.5 EndZ=0
    g2: LineSegment StartX=8 StartY=-22.5 StartZ=0 EndX=8 EndY=-20.5 EndZ=0
    g3: LineSegment StartX=8 StartY=-20.5 StartZ=0 EndX=3.5 EndY=-20.5 EndZ=0
    g4: LineSegment StartX=3.5 StartY=-11.75 StartZ=0 EndX=8 EndY=-11.75 EndZ=0
    g5: LineSegment StartX=8 StartY=-11.75 StartZ=0 EndX=8 EndY=-9.75 EndZ=0
    g6: LineSegment StartX=8 StartY=-9.75 StartZ=0 EndX=3.5 EndY=-9.75 EndZ=0
    g7: LineSegment StartX=3.5 StartY=-9.75 StartZ=0 EndX=3.5 EndY=-11.75 EndZ=0
  constraints (22):
    c: Coincident(g0,g1)
    c: Coincident(g1,g2)
    c: Coincident(g2,g3)
    c: Coincident(g3,g0)
    c: Vertical(g0)
    c: Vertical(g2)
    c: Horizontal(g1)
    c: Horizontal(g3)
    c: Coincident(g0,g-8)
    c: Coincident(g4,g5)
    c: Coincident(g5,g6)
    c: Coincident(g6,g7)
    c: Coincident(g7,g4)
    c: Horizontal(g4)
    c: Horizontal(g6)
    c: Vertical(g5)
    c: Vertical(g7)
    c: Coincident(g4,g-4)
    c: DistanceX(g-7,g4) = 6
    c: DistanceX(g-8,g2) = 6
    c: DistanceY(g5,g5) = 2
    c: DistanceY(g2,g2) = 2
FEATURE [PartDesign::Pad] Pad034
  BaseFeature = -> Pad033
  Direction = (0,0,1)
  Length = 8.2
  Length2 = 10
  Profile = -> Sketch052
  ReferenceAxis = -> Sketch052 [N_Axis]
  Refine = true
  Suppressed = false
  Type = 0
FEATURE [Sketcher::SketchObject] Sketch053
  ArcFitTolerance = 1e-06
  AttachmentSupport = -> [Pad034]
  ExternalGeometry = -> [Pad034]
  FullyConstrained = true
  MakeInternals = false
  MapMode = 5
  Placement = pos=(0,-11.75,0) rot=(1,0,0;1.5708rad)
  sketch-geometry (6):
    g0: LineSegment StartX=4.3 StartY=0 StartZ=0 EndX=4.3 EndY=-4.2 EndZ=0
    g1: LineSegment StartX=6.9 StartY=0 StartZ=0 EndX=6.9 EndY=-4.2 EndZ=0
    g2: ArcOfCircle CenterX=5.6 CenterY=-4.2 CenterZ=0 NormalX=0 NormalY=0 NormalZ=1 AngleXU=0 Radius=1.3 StartAngle=3.14159 EndAngle=6.28319
    g3: LineSegment [constr] StartX=4.3 StartY=-4.2 StartZ=0 EndX=6.9 EndY=-4.2 EndZ=0
    g4: LineSegment [constr] StartX=5.6 StartY=-4.2 StartZ=0 EndX=5.6 EndY=-5.5 EndZ=0
    g5: LineSegment StartX=6.9 StartY=0 StartZ=0 EndX=4.3 EndY=0 EndZ=0
  constraints (18):
    c: PointOnObject(g0,g-3)
    c: Vertical(g0)
    c: PointOnObject(g1,g-3)
    c: Vertical(g1)
    c: Coincident(g2,g0)
    c: Coincident(g2,g1)
    c: Coincident(g3,g0)
    c: Coincident(g3,g1)
    c: Horizontal(g3)
    c: PointOnObject(g2,g3)
    c: DistanceX(g0,g1) = 2.6
    c: DistanceX(g1,g-4) = 1.1
    c: Coincident(g4,g2)
    c: PointOnObject(g4,g2)
    c: Vertical(g4)
    c: DistanceY(g4,g0) = 5.5
    c: Coincident(g5,g1)
    c: Coincident(g5,g0)
FEATURE [PartDesign::Pocket] Pocket019
  BaseFeature = -> Pad034
  Direction = (0,1,-2e-16)
  Length = 2
  Length2 = 5
  Profile = -> Sketch053
  ReferenceAxis = -> Sketch053 [N_Axis]
  Refine = true
  Suppressed = false
  Type = 0
FEATURE [Sketcher::SketchObject] Sketch054
  ArcFitTolerance = 1e-06
  AttachmentSupport = -> [Pocket019]
  ExternalGeometry = -> [Pocket019]
  FullyConstrained = true
  MakeInternals = false
  MapMode = 5
  Placement = pos=(0,-20.5,0) rot=(0,0.707107,0.707107;3.14159rad)
  sketch-geometry (4):
    g0: LineSegment StartX=-6.9 StartY=0 StartZ=0 EndX=-4.3 EndY=0 EndZ=0
    g1: LineSegment StartX=-4.3 StartY=0 StartZ=0 EndX=-4.3 EndY=-4.2 EndZ=0
    g2: LineSegment StartX=-6.9 StartY=0 StartZ=0 EndX=-6.9 EndY=-4.2 EndZ=0
    g3: ArcOfCircle CenterX=-5.6 CenterY=-4.20001 CenterZ=0 NormalX=0 NormalY=0 NormalZ=1 AngleXU=0 Radius=1.3 StartAngle=3.14159 EndAngle=6.28319
  constraints (9):
    c: Coincident(g0,g-3)
    c: Coincident(g0,g-5)
    c: Coincident(g1,g0)
    c: Coincident(g1,g-5)
    c: Coincident(g2,g0)
    c: Coincident(g2,g-4)
    c: Coincident(g3,g2)
    c: Coincident(g3,g1)
    c: Tangent(g3,g-4)
FEATURE [PartDesign::Pocket] Pocket020
  BaseFeature = -> Pocket019
  Direction = (0,-1,2e-16)
  Length = 2
  Length2 = 5
  Profile = -> Sketch054
  ReferenceAxis = -> Sketch054 [N_Axis]
  Refine = true
  Suppressed = false
  Type = 0
FEATURE [Sketcher::SketchObject] Sketch055
  ArcFitTolerance = 1e-06
  AttachmentSupport = -> [Pocket020]
  ExternalGeometry = -> [Pocket020]
  FullyConstrained = true
  MakeInternals = false
  MapMode = 5
  Placement = pos=(0,0,0) rot=(0,0.707107,0.707107;3.14159rad)
  sketch-geometry (3):
    g0: LineSegment StartX=-2 StartY=-10.2 StartZ=0 EndX=-2 EndY=-8.9 EndZ=0
    g1: LineSegment StartX=-2 StartY=-10.2 StartZ=0 EndX=-6.8 EndY=-10.2 EndZ=0
    g2: LineSegment StartX=-2 StartY=-8.9 StartZ=0 EndX=-6.8 EndY=-10.2 EndZ=0
  constraints (7):
    c: Coincident(g0,g-4)
    c: PointOnObject(g0,g-3)
    c: DistanceY(g0,g0) = 1.3
    c: Coincident(g1,g0)
    c: Coincident(g2,g0)
    c: Coincident(g2,g1)
    c: Coincident(g-5,g1)
FEATURE [PartDesign::Pocket] Pocket021
  BaseFeature = -> Pocket020
  Direction = (0,-1,2e-16)
  Length = 32
  Length2 = 5
  Profile = -> Sketch055
  ReferenceAxis = -> Sketch055 [N_Axis]
  Refine = true
  Suppressed = false
  Type = 0
FEATURE [Sketcher::SketchObject] Sketch056
  ArcFitTolerance = 1e-06
  AttachmentSupport = -> [Pocket021]
  ExternalGeometry = -> [Pocket021]
  FullyConstrained = true
  MakeInternals = false
  MapMode = 5
  Placement = pos=(-2.10902,-1.7e-15,-7.78714) rot=(0.991268,0,-0.131859;3.14159rad)
  sketch-geometry (8):
    g0: LineSegment StartX=5.25705 StartY=31 StartZ=0 EndX=5.25705 EndY=21.5 EndZ=0
    g1: LineSegment StartX=5.25705 StartY=21.5 StartZ=0 EndX=8.22998 EndY=21.5 EndZ=0
    g2: LineSegment StartX=8.22998 StartY=21.5 StartZ=0 EndX=8.22998 EndY=31 EndZ=0
    g3: LineSegment StartX=8.22998 StartY=31 StartZ=0 EndX=5.25705 EndY=31 EndZ=0
    g4: LineSegment StartX=5.25705 StartY=10.75 StartZ=0 EndX=5.25705 EndY=1 EndZ=0
    g5: LineSegment StartX=5.25705 StartY=1 StartZ=0 EndX=8.22998 EndY=1 EndZ=0
    g6: LineSegment StartX=8.22998 StartY=1 StartZ=0 EndX=8.22998 EndY=10.75 EndZ=0
    g7: LineSegment StartX=8.22998 StartY=10.75 StartZ=0 EndX=5.25705 EndY=10.75 EndZ=0
  constraints (24):
    c: Coincident(g0,g1)
    c: Coincident(g1,g2)
    c: Coincident(g2,g3)
    c: Coincident(g3,g0)
    c: Vertical(g0)
    c: Vertical(g2)
    c: Horizontal(g1)
    c: Horizontal(g3)
    c: Coincident(g4,g5)
    c: Coincident(g5,g6)
    c: Coincident(g6,g7)
    c: Coincident(g7,g4)
    c: Vertical(g4)
    c: Vertical(g6)
    c: Horizontal(g5)
    c: Horizontal(g7)
    c: DistanceY(g0,g-6) = 1
    c: DistanceY(g-5,g0) = 1
    c: DistanceY(g4,g-3) = 1
    c: DistanceY(g-4,g4) = 1
    c: DistanceX(g-4,g4) = 1
    c: DistanceX(g5,g-4) = 1
    c: DistanceX(g-5,g0) = 1
    c: DistanceX(g1,g-5) = 1
FEATURE [PartDesign::Pocket] Pocket022
  BaseFeature = -> Pocket021
  Direction = (0.261415,0,0.965226)
  Length = 0.3
  Length2 = 5
  Profile = -> Sketch056
  ReferenceAxis = -> Sketch056 [N_Axis]
  Refine = true
  Suppressed = false
  Type = 0
FEATURE [Sketcher::SketchObject] Sketch057
  ArcFitTolerance = 1e-06
  AttachmentSupport = -> [Pocket022]
  ExternalGeometry = -> [Pocket022]
  FullyConstrained = true
  MakeInternals = false
  MapMode = 5
  Placement = pos=(-2.03059,0,-7.49757) rot=(0.991268,0,-0.131859;3.14159rad)
  sketch-geometry (32):
    g0: LineSegment StartX=5.55705 StartY=10.45 StartZ=0 EndX=5.55705 EndY=1.3 EndZ=0
    g1: LineSegment StartX=5.55705 StartY=1.3 StartZ=0 EndX=6.15705 EndY=1.3 EndZ=0
    g2: LineSegment StartX=6.15705 StartY=1.3 StartZ=0 EndX=6.15705 EndY=10.45 EndZ=0
    g3: LineSegment StartX=6.15705 StartY=10.45 StartZ=0 EndX=5.55705 EndY=10.45 EndZ=0
    g4: LineSegment StartX=6.45705 StartY=10.45 StartZ=0 EndX=6.45705 EndY=1.3 EndZ=0
    g5: LineSegment StartX=6.45705 StartY=1.3 StartZ=0 EndX=7.05705 EndY=1.3 EndZ=0
    g6: LineSegment StartX=7.05705 StartY=1.3 StartZ=0 EndX=7.05705 EndY=10.45 EndZ=0
    g7: LineSegment StartX=7.05705 StartY=10.45 StartZ=0 EndX=6.45705 EndY=10.45 EndZ=0
    g8: LineSegment StartX=7.35705 StartY=10.45 StartZ=0 EndX=7.35705 EndY=1.3 EndZ=0
    g9: LineSegment StartX=7.35705 StartY=1.3 StartZ=0 EndX=7.92998 EndY=1.3 EndZ=0
    g10: LineSegment StartX=7.92998 StartY=1.3 StartZ=0 EndX=7.92998 EndY=10.45 EndZ=0
    g11: LineSegment StartX=7.92998 StartY=10.45 StartZ=0 EndX=7.35705 EndY=10.45 EndZ=0
    g12: LineSegment [constr] StartX=6.15705 StartY=10.45 StartZ=0 EndX=6.45705 EndY=10.45 EndZ=0
    g13: LineSegment [constr] StartX=7.05705 StartY=10.45 StartZ=0 EndX=7.35705 EndY=10.45 EndZ=0
    g14: LineSegment [constr] StartX=6.15705 StartY=1.3 StartZ=0 EndX=6.45705 EndY=1.3 EndZ=0
    g15: LineSegment [constr] StartX=7.05705 StartY=1.3 StartZ=0 EndX=7.35705 EndY=1.3 EndZ=0
    g16: LineSegment StartX=5.55705 StartY=30.7 StartZ=0 EndX=5.55705 EndY=21.8 EndZ=0
    g17: LineSegment StartX=5.55705 StartY=21.8 StartZ=0 EndX=6.15705 EndY=21.8 EndZ=0
    g18: LineSegment StartX=6.15705 StartY=21.8 StartZ=0 EndX=6.15705 EndY=30.7 EndZ=0
    g19: LineSegment StartX=6.15705 StartY=30.7 StartZ=0 EndX=5.55705 EndY=30.7 EndZ=0
    g20: LineSegment StartX=6.45705 StartY=30.7 StartZ=0 EndX=6.45705 EndY=21.8 EndZ=0
    g21: LineSegment StartX=6.45705 StartY=21.8 StartZ=0 EndX=7.05705 EndY=21.8 EndZ=0
    g22: LineSegment StartX=7.05705 StartY=21.8 StartZ=0 EndX=7.05705 EndY=30.7 EndZ=0
    g23: LineSegment StartX=7.05705 StartY=30.7 StartZ=0 EndX=6.45705 EndY=30.7 EndZ=0
    g24: LineSegment StartX=7.35705 StartY=30.7 StartZ=0 EndX=7.35705 EndY=21.8 EndZ=0
    g25: LineSegment StartX=7.35705 StartY=21.8 StartZ=0 EndX=7.92998 EndY=21.8 EndZ=0
    g26: LineSegment StartX=7.92998 StartY=21.8 StartZ=0 EndX=7.92998 EndY=30.7 EndZ=0
    g27: LineSegment StartX=7.92998 StartY=30.7 StartZ=0 EndX=7.35705 EndY=30.7 EndZ=0
    g28: LineSegment [constr] StartX=6.45705 StartY=30.7 StartZ=0 EndX=6.15705 EndY=30.7 EndZ=0
    g29: LineSegment [constr] StartX=7.35705 StartY=30.7 StartZ=0 EndX=7.05705 EndY=30.7 EndZ=0
    g30: LineSegment [constr] StartX=6.45705 StartY=21.8 StartZ=0 EndX=6.15705 EndY=21.8 EndZ=0
    g31: LineSegment [constr] StartX=7.35705 StartY=21.8 StartZ=0 EndX=7.05705 EndY=21.8 EndZ=0
  constraints (90):
    c: Coincident(g0,g1)
    c: Coincident(g1,g2)
    c: Coincident(g2,g3)
    c: Coincident(g3,g0)
    c: Vertical(g0)
    c: Vertical(g2)
    c: Horizontal(g1)
    c: Horizontal(g3)
    c: Coincident(g4,g5)
    c: Coincident(g5,g6)
    c: Coincident(g6,g7)
    c: Coincident(g7,g4)
    c: Vertical(g4)
    c: Vertical(g6)
    c: Horizontal(g5)
    c: Horizontal(g7)
    c: Coincident(g8,g9)
    c: Coincident(g9,g10)
    c: Coincident(g10,g11)
    c: Coincident(g11,g8)
    c: Vertical(g8)
    c: Vertical(g10)
    c: Horizontal(g9)
    c: Horizontal(g11)
    c: DistanceX(g-3,g-3) = 2.97293
    c: DistanceX(g-3,g0) = 0.3
    c: DistanceX(g10,g-3) = 0.3
    c: DistanceX(g6,g8) = 0.3
    c: DistanceX(g2,g4) = 0.3
    c: DistanceX(g3,g3) = 0.6
    c: DistanceX(g7,g7) = 0.6
    c: DistanceX(g11,g11) = 0.572927
    c: DistanceY(g0,g-3) = 0.3
    c: Coincident(g12,g2)
    c: Coincident(g12,g4)
    c: Coincident(g13,g6)
    c: Coincident(g13,g8)
    c: Horizontal(g12)
    c: Horizontal(g13)
    c: Coincident(g14,g1)
    c: Coincident(g14,g4)
    c: Coincident(g15,g5)
    c: Coincident(g15,g8)
    c: Horizontal(g14)
    c: Horizontal(g15)
    c: DistanceY(g-4,g0) = 0.3
    c: Coincident(g16,g17)
    c: Coincident(g17,g18)
    c: Coincident(g18,g19)
    c: Coincident(g19,g16)
    c: Vertical(g16)
    c: Vertical(g18)
    c: Horizontal(g17)
    c: Horizontal(g19)
    c: Coincident(g20,g21)
    c: Coincident(g21,g22)
    c: Coincident(g22,g23)
    c: Coincident(g23,g20)
    c: Vertical(g20)
    c: Vertical(g22)
    c: Horizontal(g21)
    c: Horizontal(g23)
    c: Coincident(g24,g25)
    c: Coincident(g25,g26)
    c: Coincident(g26,g27)
    c: Coincident(g27,g24)
    c: Vertical(g24)
    c: Vertical(g26)
    c: Horizontal(g25)
    c: Horizontal(g27)
    c: Coincident(g28,g20)
    c: Coincident(g28,g18)
    c: Coincident(g29,g24)
    c: Coincident(g29,g22)
    c: Horizontal(g28)
    c: Horizontal(g29)
    c: Coincident(g30,g20)
    c: Coincident(g30,g17)
    c: Horizontal(g30)
    c: Coincident(g31,g24)
    c: Coincident(g31,g21)
    c: Horizontal(g31)
    c: DistanceX(g-5,g16) = 0.3
    c: DistanceX(g30,g30) = 0.3
    c: DistanceX(g31,g31) = 0.3
    c: DistanceX(g17,g17) = 0.6
    c: DistanceX(g21,g21) = 0.6
    c: DistanceY(g-5,g16) = 0.3
    c: DistanceY(g16,g-6) = 0.3
    c: DistanceX(g26,g-6) = 0.3
FEATURE [PartDesign::Pad] Pad035
  BaseFeature = -> Pocket022
  Direction = (-0.261415,0,-0.965226)
  Length = 0.3
  Length2 = 10
  Profile = -> Sketch057
  ReferenceAxis = -> Sketch057 [N_Axis]
  Refine = true
  Suppressed = false
  Type = 0
FEATURE [Sketcher::SketchObject] Sketch058
  ArcFitTolerance = 1e-06
  AttachmentSupport = -> [Pad035]
  ExternalGeometry = -> [Pad035]
  FullyConstrained = true
  MakeInternals = false
  MapMode = 5
  Placement = pos=(0,0,-8.2) rot=(0,0,1;0rad)
  sketch-geometry (1):
    g0: Circle CenterX=20.6 CenterY=-16.25 CenterZ=0 NormalX=0 NormalY=0 NormalZ=1 AngleXU=0 Radius=5.25
  constraints (4):
    c: Diameter(g0) = 10.5
    c: DistanceY(g-3,g-3) = 8.75
    c: DistanceY(g0,g-3) = 4.5
    c: DistanceX(g-3,g0) = 13.8
FEATURE [PartDesign::Pocket] Pocket023
  BaseFeature = -> Pad035
  Direction = (0,0,-1)
  Length = 5
  Length2 = 5
  Profile = -> Sketch058
  ReferenceAxis = -> Sketch058 [N_Axis]
  Refine = true
  Suppressed = false
  Type = 0
FEATURE [Sketcher::SketchObject] Sketch059
  ArcFitTolerance = 1e-06
  AttachmentSupport = -> [Pocket023]
  ExternalGeometry = -> [Pocket023]
  FullyConstrained = true
  MakeInternals = false
  MapMode = 5
  Placement = pos=(0,0,-10.2) rot=(1,0,0;3.14159rad)
  sketch-geometry (2):
    g0: Circle CenterX=29.5 CenterY=16.25 CenterZ=0 NormalX=0 NormalY=0 NormalZ=1 AngleXU=0 Radius=0.75
    g1: LineSegment [constr] StartX=20.6 StartY=16.25 StartZ=0 EndX=29.5 EndY=16.25 EndZ=0
  constraints (5):
    c: Radius(g0) = 0.75
    c: Coincident(g1,g-3)
    c: Coincident(g1,g0)
    c: Horizontal(g1)
    c: DistanceX(g1,g1) = 8.9
FEATURE [PartDesign::Pocket] Pocket024
  BaseFeature = -> Pocket023
  Direction = (0,0,1)
  Length = 5
  Length2 = 5
  Profile = -> Sketch059
  ReferenceAxis = -> Sketch059 [N_Axis]
  Refine = true
  Suppressed = false
  Type = 0
FEATURE [Sketcher::SketchObject] Sketch060
  ArcFitTolerance = 1e-06
  AttachmentSupport = -> [Pocket024]
  ExternalGeometry = -> [Pocket024]
  FullyConstrained = true
  MakeInternals = false
  MapMode = 5
  Placement = pos=(0,0,-8.2) rot=(0,0,1;0rad)
  sketch-geometry (2):
    g0: Circle CenterX=29.5 CenterY=-16.25 CenterZ=0 NormalX=0 NormalY=0 NormalZ=1 AngleXU=0 Radius=0.75
    g1: Circle CenterX=29.5 CenterY=-16.25 CenterZ=0 NormalX=0 NormalY=0 NormalZ=1 AngleXU=0 Radius=2
  constraints (4):
    c: Coincident(g0,g-3)
    c: Equal(g0,g-3)
    c: Coincident(g1,g0)
    c: Diameter(g1) = 4
FEATURE [PartDesign::Pad] Pad036
  BaseFeature = -> Pocket024
  Direction = (0,0,1)
  Length = 2
  Length2 = 10
  Profile = -> Sketch060
  ReferenceAxis = -> Sketch060 [N_Axis]
  Refine = true
  Suppressed = false
  Type = 0
FEATURE [Sketcher::SketchObject] Sketch061
  ArcFitTolerance = 1e-06
  AttachmentSupport = -> [Pad036]
  ExternalGeometry = -> [Pad036]
  FullyConstrained = true
  MakeInternals = false
  MapMode = 5
  Placement = pos=(0,0,-10.2) rot=(1,0,0;3.14159rad)
  sketch-geometry (9):
    g0: LineSegment StartX=34 StartY=18.85 StartZ=0 EndX=41 EndY=18.85 EndZ=0
    g1: LineSegment StartX=41 StartY=18.85 StartZ=0 EndX=41 EndY=13.65 EndZ=0
    g2: LineSegment StartX=41 StartY=13.65 StartZ=0 EndX=34 EndY=13.65 EndZ=0
    g3: LineSegment StartX=34 StartY=13.65 StartZ=0 EndX=34 EndY=14.35 EndZ=0
    g4: LineSegment StartX=34 StartY=14.35 StartZ=0 EndX=39.7 EndY=14.35 EndZ=0
    g5: LineSegment StartX=39.7 StartY=14.35 StartZ=0 EndX=39.7 EndY=18.15 EndZ=0
    g6: LineSegment StartX=39.7 StartY=18.15 StartZ=0 EndX=34 EndY=18.15 EndZ=0
    g7: LineSegment StartX=34 StartY=18.85 StartZ=0 EndX=34 EndY=18.15 EndZ=0
    g8: LineSegment [constr] StartX=34 StartY=18.15 StartZ=0 EndX=34 EndY=14.35 EndZ=0
  constraints (27):
    c: Horizontal(g0)
    c: Coincident(g1,g0)
    c: Vertical(g1)
    c: Coincident(g2,g1)
    c: Horizontal(g2)
    c: Coincident(g3,g2)
    c: Coincident(g4,g3)
    c: Horizontal(g4)
    c: Coincident(g5,g4)
    c: Vertical(g5)
    c: Coincident(g6,g5)
    c: Horizontal(g6)
    c: Coincident(g7,g0)
    c: Coincident(g7,g6)
    c: Vertical(g7)
    c: Vertical(g3)
    c: Coincident(g8,g6)
    c: Coincident(g8,g3)
    c: Vertical(g8)
    c: DistanceY(g8,g8) = 3.8
    c: DistanceY(g7,g7) = 0.7
    c: DistanceY(g3,g3) = 0.7
    c: DistanceX(g5,g0) = 1.3
    c: DistanceX(g0,g0) = 7
    c: DistanceY(g5,g5) = 3.8
    c: DistanceY(g-3,g5) = 1.9
    c: DistanceX(g-3,g6) = 4.5
FEATURE [PartDesign::Pocket] Pocket025
  BaseFeature = -> Pad036
  Direction = (0,0,1)
  Length = 5
  Length2 = 5
  Profile = -> Sketch061
  ReferenceAxis = -> Sketch061 [N_Axis]
  Refine = true
  Suppressed = false
  Type = 0
FEATURE [Sketcher::SketchObject] Sketch062
  ArcFitTolerance = 1e-06
  AttachmentSupport = -> [Pocket025]
  ExternalGeometry = -> [Pocket025]
  FullyConstrained = true
  MakeInternals = false
  MapMode = 5
  Placement = pos=(0,0,-8.2) rot=(0,0,1;0rad)
  sketch-geometry (2):
    g0: Circle CenterX=52.1 CenterY=-16 CenterZ=0 NormalX=0 NormalY=0 NormalZ=1 AngleXU=0 Radius=2.7
    g1: LineSegment [constr] StartX=52.1 StartY=-16 StartZ=0 EndX=54.8 EndY=-16 EndZ=0
  constraints (9):
    c: DistanceY(g-4,g-3) = 0.0862915
    c: DistanceY(g-4,g-3) = 5.74315
    c: DistanceY(g-7,g-6) = 13.6
    c: DistanceY(g0,g-6) = 6.8
    c: Radius(g0) = 2.7
    c: Coincident(g1,g0)
    c: PointOnObject(g1,g0)
    c: Horizontal(g1)
    c: DistanceX(g1,g-3) = 1
FEATURE [PartDesign::Pad] Pad037
  BaseFeature = -> Pocket025
  Direction = (0,0,1)
  Length = 6
  Length2 = 10
  Profile = -> Sketch062
  ReferenceAxis = -> Sketch062 [N_Axis]
  Refine = true
  Suppressed = false
  Type = 0
FEATURE [PartDesign::Fillet] Fillet002
  Base = -> Pad037 [Edge151]
  BaseFeature = -> Pad037
  Radius = 0.3
  Refine = true
  SupportTransform = false
  Suppressed = false
  UseAllEdges = false
FEATURE [Sketcher::SketchObject] Sketch063
  ArcFitTolerance = 1e-06
  AttachmentSupport = -> [Fillet002]
  ExternalGeometry = -> [Fillet002]
  FullyConstrained = true
  MakeInternals = false
  MapMode = 5
  Placement = pos=(0,0,-10.2) rot=(1,0,0;3.14159rad)
  sketch-geometry (1):
    g0: Circle CenterX=52.1 CenterY=16 CenterZ=0 NormalX=0 NormalY=0 NormalZ=1 AngleXU=0 Radius=0.75
  constraints (2):
    c: Coincident(g0,g-3)
    c: Radius(g0) = 0.75
FEATURE [PartDesign::Pocket] Pocket026
  BaseFeature = -> Fillet002
  Direction = (0,0,1)
  Length = 6
  Length2 = 5
  Profile = -> Sketch063
  ReferenceAxis = -> Sketch063 [N_Axis]
  Refine = true
  Suppressed = false
  Type = 0
FEATURE [Sketcher::SketchObject] Sketch064
  ArcFitTolerance = 1e-06
  AttachmentSupport = -> [Pocket026]
  ExternalGeometry = -> [Pocket026]
  FullyConstrained = true
  MakeInternals = false
  MapMode = 5
  Placement = pos=(0,-26,0) rot=(1,0,0;1.5708rad)
  sketch-geometry (3):
    g0: LineSegment StartX=3.5 StartY=1.6 StartZ=0 EndX=3 EndY=1.6 EndZ=0
    g1: LineSegment StartX=3.5 StartY=1.6 StartZ=0 EndX=3.5 EndY=1.1 EndZ=0
    g2: LineSegment StartX=3.5 StartY=1.1 StartZ=0 EndX=3 EndY=1.6 EndZ=0
  constraints (8):
    c: Coincident(g0,g-4)
    c: PointOnObject(g0,g-3)
    c: Coincident(g1,g0)
    c: PointOnObject(g1,g-4)
    c: Coincident(g2,g1)
    c: Coincident(g2,g0)
    c: DistanceX(g0,g0) = 0.5
    c: DistanceY(g1,g1) = 0.5
FEATURE [PartDesign::Pocket] Pocket027
  BaseFeature = -> Pocket026
  Direction = (0,1,-2e-16)
  Length = 20
  Length2 = 5
  Profile = -> Sketch064
  ReferenceAxis = -> Sketch064 [N_Axis]
  Refine = true
  Suppressed = false
  Type = 0
FEATURE [PartDesign::Body] Body001  label="Front_Torso"
  AllowCompound = false
  Group = -> [Binder,Sketch045,Pad029,Sketch046,Pocket017,Sketch047,Pad030,Fillet001,Sketch048,Pad031,Sketch049,Pocket018,Sketch050,Pad032,Sketch051,Pad033,Sketch052,Pad034,Sketch053,Pocket019,Sketch054,Pocket020,Sketch055,Pocket021,Sketch056,Pocket022,Sketch057,Pad035,Sketch058,Pocket023,Sketch059,Pocket024,Sketch060,Pad036,Sketch061,Pocket025,Sketch062,Pad037,Fillet002,Sketch063,Pocket026,Sketch064,Pocket027]
  Origin = -> Origin001
  Tip = -> Pocket027
FEATURE [Sketcher::SketchObject] Sketch065
  ArcFitTolerance = 1e-06
  AttachmentSupport = -> [XY_Plane002]
  FullyConstrained = true
  MakeInternals = false
  MapMode = 5
  sketch-geometry (12):
    g0: LineSegment [constr] StartX=-4e-16 StartY=0 StartZ=0 EndX=50.4 EndY=-4e-16 EndZ=0
    g1: LineSegment StartX=-4e-16 StartY=0 StartZ=0 EndX=25.1943 EndY=11.751 EndZ=0
    g2: LineSegment StartX=50.4 StartY=-4e-16 StartZ=0 EndX=25.1943 EndY=11.751 EndZ=0
    g3: LineSegment StartX=1.9444 StartY=-4.16885 StartZ=0 EndX=12.9214 EndY=0.950952 EndZ=0
    g4: ArcOfCircle CenterX=25.1943 CenterY=-29.2294 CenterZ=0 NormalX=0 NormalY=0 NormalZ=1 AngleXU=0 Radius=32.5803 StartAngle=1.18457 EndAngle=1.95703
    g5: LineSegment StartX=37.4673 StartY=0.950952 StartZ=0 EndX=48.4563 EndY=-4.16918 EndZ=0
    g6: LineSegment [constr] StartX=50.4 StartY=-4e-16 StartZ=0 EndX=48.4563 EndY=-4.16918 EndZ=0
    g7: LineSegment [constr] StartX=-4e-16 StartY=0 StartZ=0 EndX=1.9444 EndY=-4.16885 EndZ=0
    g8: LineSegment [constr] StartX=25.1943 StartY=-29.2294 StartZ=0 EndX=25.1943 EndY=3.35095 EndZ=0
    g9: LineSegment [constr] StartX=25.1943 StartY=3.35095 StartZ=0 EndX=25.1943 EndY=11.751 EndZ=0
    g10: ArcOfCircle CenterX=51.1739 CenterY=-2.89846 CenterZ=0 NormalX=0 NormalY=0 NormalZ=1 AngleXU=0 Radius=3 StartAngle=3.57898 EndAngle=8.1149
    g11: ArcOfCircle CenterX=-0.773401 CenterY=-2.89859 CenterZ=0 NormalX=0 NormalY=0 NormalZ=1 AngleXU=0 Radius=3 StartAngle=1.31005 EndAngle=5.84597
  constraints (35):
    c: Coincident(g0,g-1)
    c: PointOnObject(g0,g-1)
    c: Coincident(g1,g0)
    c: Coincident(g2,g0)
    c: Coincident(g2,g1)
    c: Angle(g1,g2) = 2.26893
    c: DistanceX(g0,g0) = 50.4
    c: Distance(g1) = 27.8
    c: Distance(g2) = 27.8102
    c: Coincident(g4,g3)
    c: Coincident(g5,g4)
    c: Coincident(g6,g0)
    c: Coincident(g6,g5)
    c: Distance(g6) = 4.6
    c: Coincident(g7,g0)
    c: Coincident(g7,g3)
    c: Distance(g7) = 4.6
    c: Coincident(g8,g4)
    c: PointOnObject(g8,g4)
    c: Vertical(g8)
    c: Coincident(g9,g8)
    c: Coincident(g9,g1)
    c: Vertical(g9)
    c: DistanceY(g9,g9) = 8.4
    c: Angle(g7,g1) = 1.5708
    c: Angle(g3,g7) = 1.5708
    c: DistanceY(g4,g3) = 0
    c: Angle(g2,g6) = 1.5708
    c: DistanceY(g3,g8) = 2.4
    c: Coincident(g10,g0)
    c: Coincident(g10,g5)
    c: Diameter(g10) = 6
    c: Coincident(g11,g0)
    c: Coincident(g11,g3)
    c: Diameter(g11) = 6
FEATURE [PartDesign::Pad] Pad038
  Direction = (0,0,1)
  Length = 5.6
  Length2 = 10
  Profile = -> Sketch065
  ReferenceAxis = -> Sketch065 [N_Axis]
  Refine = true
  Suppressed = false
  Type = 0
FEATURE [PartDesign::Fillet] Fillet003
  Base = -> Pad038 [Edge2]
  BaseFeature = -> Pad038
  Radius = 2
  Refine = true
  SupportTransform = false
  Suppressed = false
  UseAllEdges = false
FEATURE [Sketcher::SketchObject] Sketch066
  ArcFitTolerance = 1e-06
  AttachmentSupport = -> [Fillet003]
  ExternalGeometry = -> [Fillet003]
  FullyConstrained = true
  MakeInternals = false
  MapMode = 5
  Placement = pos=(0,0,0) rot=(1,0,0;3.14159rad)
  sketch-geometry (1):
    g0: Circle CenterX=51.1739 CenterY=2.89846 CenterZ=0 NormalX=0 NormalY=0 NormalZ=1 AngleXU=0 Radius=3
  constraints (2):
    c: Coincident(g0,g-3)
    c: Equal(g0,g-3)
FEATURE [PartDesign::Pad] Pad039
  BaseFeature = -> Fillet003
  Direction = (0,0,-1)
  Length = 0.25
  Length2 = 10
  Profile = -> Sketch066
  ReferenceAxis = -> Sketch066 [N_Axis]
  Refine = true
  Suppressed = false
  Type = 0
FEATURE [Sketcher::SketchObject] Sketch067
  ArcFitTolerance = 1e-06
  AttachmentSupport = -> [Pad039]
  ExternalGeometry = -> [Pad039]
  FullyConstrained = true
  MakeInternals = false
  MapMode = 5
  Placement = pos=(0,0,5.6) rot=(0,0,1;0rad)
  sketch-geometry (1):
    g0: Circle CenterX=51.1739 CenterY=-2.89846 CenterZ=0 NormalX=0 NormalY=0 NormalZ=1 AngleXU=0 Radius=3
  constraints (2):
    c: Coincident(g0,g-4)
    c: Equal(g0,g-4)
FEATURE [PartDesign::Pad] Pad040
  BaseFeature = -> Pad039
  Direction = (0,0,1)
  Length = 0.25
  Length2 = 10
  Profile = -> Sketch067
  ReferenceAxis = -> Sketch067 [N_Axis]
  Refine = true
  Suppressed = false
  Type = 0
FEATURE [Sketcher::SketchObject] Sketch068
  ArcFitTolerance = 1e-06
  AttachmentSupport = -> [Pad040]
  ExternalGeometry = -> [Pad040]
  FullyConstrained = true
  MakeInternals = false
  MapMode = 5
  Placement = pos=(0,0,5.6) rot=(0,0,1;0rad)
  sketch-geometry (1):
    g0: Circle CenterX=-0.773401 CenterY=-2.89859 CenterZ=0 NormalX=0 NormalY=0 NormalZ=1 AngleXU=0 Radius=3
  constraints (2):
    c: Coincident(g0,g-3)
    c: Equal(g0,g-3)
FEATURE [PartDesign::Pad] Pad041
  BaseFeature = -> Pad040
  Direction = (0,0,1)
  Length = 0.1
  Length2 = 10
  Profile = -> Sketch068
  ReferenceAxis = -> Sketch068 [N_Axis]
  Refine = true
  Suppressed = false
  Type = 0
FEATURE [Sketcher::SketchObject] Sketch069
  ArcFitTolerance = 1e-06
  AttachmentSupport = -> [Pad041]
  ExternalGeometry = -> [Pad041]
  FullyConstrained = true
  MakeInternals = false
  MapMode = 5
  Placement = pos=(0,0,0) rot=(1,0,0;3.14159rad)
  sketch-geometry (1):
    g0: Circle CenterX=-0.773401 CenterY=2.89859 CenterZ=0 NormalX=0 NormalY=0 NormalZ=1 AngleXU=0 Radius=3
  constraints (2):
    c: Coincident(g0,g-3)
    c: Equal(g0,g-3)
FEATURE [PartDesign::Pad] Pad042
  BaseFeature = -> Pad041
  Direction = (0,0,-1)
  Length = 0.1
  Length2 = 10
  Profile = -> Sketch069
  ReferenceAxis = -> Sketch069 [N_Axis]
  Refine = true
  Suppressed = false
  Type = 0
FEATURE [Sketcher::SketchObject] Sketch070
  ArcFitTolerance = 1e-06
  AttachmentSupport = -> [Pad042]
  ExternalGeometry = -> [Pad042]
  FullyConstrained = false
  MakeInternals = false
  MapMode = 5
  Placement = pos=(0,0,0) rot=(1,0,0;3.14159rad)
  sketch-geometry (4):
    g0: LineSegment StartX=24.0163 StartY=-5.17817 StartZ=0 EndX=24.0163 EndY=-6.67308 EndZ=0
    g1: LineSegment StartX=24.0163 StartY=-6.67308 StartZ=0 EndX=26.3302 EndY=-6.67308 EndZ=0
    g2: LineSegment StartX=26.3302 StartY=-6.67308 StartZ=0 EndX=26.3302 EndY=-5.17817 EndZ=0
    g3: LineSegment StartX=26.3302 StartY=-5.17817 StartZ=0 EndX=24.0163 EndY=-5.17817 EndZ=0
  constraints (8):
    c: Coincident(g0,g1)
    c: Coincident(g1,g2)
    c: Coincident(g2,g3)
    c: Coincident(g3,g0)
    c: Vertical(g0)
    c: Vertical(g2)
    c: Horizontal(g1)
    c: Horizontal(g3)
FEATURE [PartDesign::Pad] Pad043
  BaseFeature = -> Pad042
  Direction = (0,0,-1)
  Length = 1
  Length2 = 10
  Profile = -> Sketch070
  ReferenceAxis = -> Sketch070 [N_Axis]
  Refine = true
  Suppressed = false
  Type = 0
FEATURE [Sketcher::SketchObject] Sketch071
  ArcFitTolerance = 1e-06
  AttachmentOffset = pos=(0,0,-8) rot=(0,0,1;0rad)
  AttachmentSupport = -> [Pad043]
  ExternalGeometry = -> [Pad043]
  FullyConstrained = true
  MakeInternals = false
  MapMode = 5
  Placement = pos=(0,13.1782,-1.8e-15) rot=(1,0,0;1.5708rad)
  sketch-geometry (10):
    g0: LineSegment StartX=50.4 StartY=1e-16 StartZ=0 EndX=50.4 EndY=-2 EndZ=0
    g1: LineSegment StartX=50.4 StartY=-2 StartZ=0 EndX=0 EndY=-2 EndZ=0
    g2: LineSegment StartX=0 StartY=-2 StartZ=0 EndX=0 EndY=0 EndZ=0
    g3: LineSegment StartX=0 StartY=0 StartZ=0 EndX=-4e-16 EndY=0.4 EndZ=0
    g4: LineSegment StartX=-4e-16 StartY=0.4 StartZ=0 EndX=50.4 EndY=1e-16 EndZ=0
    g5: LineSegment StartX=0 StartY=5.6 StartZ=0 EndX=-4e-16 EndY=5.2 EndZ=0
    g6: LineSegment StartX=-4e-16 StartY=5.2 StartZ=0 EndX=50.4 EndY=5.6 EndZ=0
    g7: LineSegment StartX=50.4 StartY=5.6 StartZ=0 EndX=50.4 EndY=7.6 EndZ=0
    g8: LineSegment StartX=50.4 StartY=7.6 StartZ=0 EndX=0 EndY=7.6 EndZ=0
    g9: LineSegment StartX=0 StartY=5.6 StartZ=0 EndX=0 EndY=7.6 EndZ=0
  constraints (26):
    c: Coincident(g0,g-5)
    c: Vertical(g0)
    c: Coincident(g1,g0)
    c: Horizontal(g1)
    c: Coincident(g2,g1)
    c: Coincident(g2,g-1)
    c: Vertical(g2)
    c: Coincident(g3,g2)
    c: PointOnObject(g3,g-3)
    c: Coincident(g4,g3)
    c: Coincident(g4,g0)
    c: DistanceY(g3,g3) = 0.4
    c: DistanceY(g2,g2) = 2
    c: PointOnObject(g5,g-3)
    c: Coincident(g6,g5)
    c: DistanceY(g5,g5) = 0.4
    c: Coincident(g7,g6)
    c: Vertical(g7)
    c: Coincident(g8,g7)
    c: PointOnObject(g8,g-2)
    c: Horizontal(g8)
    c: Coincident(g9,g5)
    c: Coincident(g9,g8)
    c: DistanceY(g9,g9) = 2
    c: Coincident(g5,g-8)
    c: Coincident(g6,g-6)
FEATURE [PartDesign::Pocket] Pocket028
  BaseFeature = -> Pad043
  Direction = (0,1,-2e-16)
  Length = 22
  Length2 = 5
  Profile = -> Sketch071
  ReferenceAxis = -> Sketch071 [N_Axis]
  Refine = true
  Reversed = true
  Suppressed = false
  Type = 0
FEATURE [Sketcher::SketchObject] Sketch072
  ArcFitTolerance = 1e-06
  AttachmentSupport = -> [Pocket028]
  ExternalGeometry = -> [Pocket028]
  FullyConstrained = true
  MakeInternals = false
  MapMode = 5
  Placement = pos=(0,0,5.85) rot=(0,0,1;0rad)
  sketch-geometry (1):
    g0: Circle CenterX=51.1739 CenterY=-2.89846 CenterZ=0 NormalX=0 NormalY=0 NormalZ=1 AngleXU=0 Radius=3
  constraints (2):
    c: Coincident(g0,g-3)
    c: Equal(g0,g-3)
FEATURE [PartDesign::Pad] Pad044
  BaseFeature = -> Pocket028
  Direction = (0,0,1)
  Length = 6.1
  Length2 = 10
  Profile = -> Sketch072
  ReferenceAxis = -> Sketch072 [N_Axis]
  Refine = true
  Reversed = true
  Suppressed = false
  Type = 0
FEATURE [Sketcher::SketchObject] Sketch073
  ArcFitTolerance = 1e-06
  AttachmentSupport = -> [Pad044]
  ExternalGeometry = -> [Pad044]
  FullyConstrained = true
  MakeInternals = false
  MapMode = 5
  Placement = pos=(0,0,5.7) rot=(0,0,1;0rad)
  sketch-geometry (1):
    g0: Circle CenterX=-0.773401 CenterY=-2.89859 CenterZ=0 NormalX=0 NormalY=0 NormalZ=1 AngleXU=0 Radius=3
  constraints (2):
    c: Coincident(g0,g-3)
    c: Equal(g0,g-3)
FEATURE [PartDesign::Pad] Pad045
  BaseFeature = -> Pad044
  Direction = (0,0,1)
  Length = 5.8
  Length2 = 10
  Profile = -> Sketch073
  ReferenceAxis = -> Sketch073 [N_Axis]
  Refine = true
  Reversed = true
  Suppressed = false
  Type = 0
FEATURE [PartDesign::Pad] Pad046
  BaseFeature = -> Pad045
  Direction = (0,0,-1)
  Length = 0.25
  Length2 = 10
  Profile = -> Pad045 [Face1]
  Refine = true
  Suppressed = false
  Type = 0
FEATURE [PartDesign::Pad] Pad047
  BaseFeature = -> Pad046
  Direction = (0,0,1)
  Length = 0.25
  Length2 = 10
  Profile = -> Pad046 [Face1]
  Refine = true
  Suppressed = false
  Type = 0
FEATURE [Sketcher::SketchObject] Sketch074
  ArcFitTolerance = 1e-06
  AttachmentSupport = -> [Pad047]
  ExternalGeometry = -> [Pad047]
  FullyConstrained = true
  MakeInternals = false
  MapMode = 5
  Placement = pos=(0,0,6.1) rot=(0,0,1;0rad)
  sketch-geometry (1):
    g0: Circle CenterX=51.1739 CenterY=-2.89846 CenterZ=0 NormalX=0 NormalY=0 NormalZ=1 AngleXU=0 Radius=1.9
  constraints (2):
    c: Coincident(g0,g-3)
    c: Radius(g0) = 1.9
FEATURE [PartDesign::Pad] Pad048
  BaseFeature = -> Pad047
  Direction = (0,0,1)
  Length = 2
  Length2 = 10
  Profile = -> Sketch074
  ReferenceAxis = -> Sketch074 [N_Axis]
  Refine = true
  Suppressed = false
  Type = 0
FEATURE [Sketcher::SketchObject] Sketch075
  ArcFitTolerance = 1e-06
  AttachmentSupport = -> [Pad048]
  ExternalGeometry = -> [Pad048]
  FullyConstrained = true
  MakeInternals = false
  MapMode = 5
  Placement = pos=(0,0,-0.5) rot=(1,0,0;3.14159rad)
  sketch-geometry (1):
    g0: Circle CenterX=51.1739 CenterY=2.89846 CenterZ=0 NormalX=0 NormalY=0 NormalZ=1 AngleXU=0 Radius=1.9
  constraints (2):
    c: Coincident(g0,g-3)
    c: Radius(g0) = 1.9
FEATURE [PartDesign::Pad] Pad049
  BaseFeature = -> Pad048
  Direction = (0,0,-1)
  Length = 2
  Length2 = 10
  Profile = -> Sketch075
  ReferenceAxis = -> Sketch075 [N_Axis]
  Refine = true
  Suppressed = false
  Type = 0
FEATURE [Sketcher::SketchObject] Sketch076
  ArcFitTolerance = 1e-06
  AttachmentSupport = -> [Pad049]
  ExternalGeometry = -> [Pad049]
  FullyConstrained = true
  MakeInternals = false
  MapMode = 5
  Placement = pos=(0,0,5.7) rot=(0,0,1;0rad)
  sketch-geometry (1):
    g0: Circle CenterX=-0.773401 CenterY=-2.89859 CenterZ=0 NormalX=0 NormalY=0 NormalZ=1 AngleXU=0 Radius=0.75
  constraints (2):
    c: Radius(g0) = 0.75
    c: Coincident(g0,g-3)
FEATURE [PartDesign::Pocket] Pocket029
  BaseFeature = -> Pad049
  Direction = (0,0,-1)
  Length = 6
  Length2 = 5
  Profile = -> Sketch076
  ReferenceAxis = -> Sketch076 [N_Axis]
  Refine = true
  Suppressed = false
  Type = 0
FEATURE [Sketcher::SketchObject] Sketch077
  ArcFitTolerance = 1e-06
  AttachmentSupport = -> [Pocket029]
  ExternalGeometry = -> [Pocket029]
  FullyConstrained = true
  MakeInternals = false
  MapMode = 5
  Placement = pos=(0.0031744,1e-16,0.399975) rot=(0.999992,0,-0.003968;3.14159rad)
  sketch-geometry (14):
    g0: LineSegment StartX=2.22247 StartY=2.82018 StartZ=0 EndX=12.4102 EndY=-1.93134 EndZ=0
    g1: ArcOfCircle CenterX=25.192 CenterY=29.2294 CenterZ=0 NormalX=0 NormalY=0 NormalZ=1 AngleXU=0 Radius=33.6803 StartAngle=4.32313 EndAngle=5.05713
    g2: LineSegment StartX=36.5742 StartY=-2.46935 StartZ=0 EndX=48.1725 EndY=2.93448 EndZ=0
    g3: ArcOfCircle CenterX=51.1722 CenterY=2.89849 CenterZ=0 NormalX=0 NormalY=0 NormalZ=1 AngleXU=0 Radius=3 StartAngle=3.12959 EndAngle=4.02604
    g4: LineSegment StartX=49.2711 StartY=0.577787 StartZ=0 EndX=25.6148 EndY=-10.4505 EndZ=0
    g5: ArcOfCircle CenterX=25.1922 CenterY=-9.5442 CenterZ=0 NormalX=0 NormalY=0 NormalZ=1 AngleXU=0 Radius=1.00001 StartAngle=4.27602 EndAngle=5.14876
    g6: LineSegment StartX=24.7695 StartY=-10.4505 StartZ=0 EndX=1.12424 EndY=0.577594 EndZ=0
    g7: LineSegment [constr] StartX=3.75384 StartY=3.32348 StartZ=0 EndX=3.28744 EndY=2.32348 EndZ=0
    g8: ArcOfCircle CenterX=-0.776505 CenterY=2.89862 CenterZ=0 NormalX=0 NormalY=0 NormalZ=1 AngleXU=0 Radius=3 StartAngle=5.39856 EndAngle=6.25703
    g9: LineSegment [constr] StartX=2.23467 StartY=0.0596903 StartZ=0 EndX=1.81199 EndY=-0.846586 EndZ=0
    g10: LineSegment [constr] StartX=47.0641 StartY=2.41808 StartZ=0 EndX=46.6418 EndY=3.32453 EndZ=0
    g11: LineSegment [constr] StartX=48.1632 StartY=0.0612903 StartZ=0 EndX=48.5857 EndY=-0.845059 EndZ=0
    g12: LineSegment [constr] StartX=25.192 StartY=29.2294 StartZ=0 EndX=25.192 EndY=-3.35095 EndZ=0
    g13: LineSegment [constr] StartX=25.192 StartY=-3.35095 StartZ=0 EndX=25.192 EndY=-4.45095 EndZ=0
  constraints (47):
    c: PointOnObject(g0,g-10)
    c: Coincident(g1,g0)
    c: Coincident(g2,g1)
    c: PointOnObject(g2,g-3)
    c: Coincident(g3,g2)
    c: Coincident(g4,g3)
    c: Coincident(g5,g4)
    c: Coincident(g6,g5)
    c: PointOnObject(g6,g-10)
    c: Tangent(g3,g-3) = -1.5708
    c: Coincident(g1,g-6)
    c: PointOnObject(g7,g-9)
    c: PointOnObject(g7,g0)
    c: Perpendicular(g7,g-9)
    c: DistanceY(g7,g7) = 1
    c: Coincident(g8,g6)
    c: Coincident(g8,g0)
    c: PointOnObject(g9,g6)
    c: PointOnObject(g9,g-8)
    c: Perpendicular(g-8,g9)
    c: Parallel(g0,g-9)
    c: Parallel(g6,g-8)
    c: Parallel(g2,g-4)
    c: Parallel(g4,g-5)
    c: Distance(g-1,g9) = 2
    c: Distance(g7,g-9) = 2
    c: Distance(g9) = 1
    c: Coincident(g5,g-7)
    c: Radius(g8) = 3
    c: PointOnObject(g10,g2)
    c: PointOnObject(g10,g-4)
    c: Perpendicular(g-4,g10)
    c: Distance(g-4,g10) = 2
    c: Distance(g10) = 1
    c: PointOnObject(g11,g4)
    c: PointOnObject(g11,g-5)
    c: Perpendicular(g4,g11)
    c: Distance(g11,g-5) = 2
    c: Distance(g11) = 1
    c: DistanceY(g4,g5) = 0
    c: Coincident(g12,g1)
    c: PointOnObject(g12,g-6)
    c: Vertical(g12)
    c: Coincident(g13,g12)
    c: PointOnObject(g13,g1)
    c: Vertical(g13)
    c: DistanceY(g13,g13) = 1.1
FEATURE [PartDesign::Pocket] Pocket030
  BaseFeature = -> Pocket029
  Direction = (0.00793626,0,0.999969)
  Length = 1
  Length2 = 5
  Profile = -> Sketch077
  ReferenceAxis = -> Sketch077 [N_Axis]
  Refine = true
  Suppressed = false
  Type = 0
FEATURE [Sketcher::SketchObject] Sketch078
  ArcFitTolerance = 1e-06
  AttachmentSupport = -> [Pocket030]
  ExternalGeometry = -> [Pocket030]
  FullyConstrained = true
  MakeInternals = false
  MapMode = 5
  Placement = pos=(-0.0412672,1.1e-15,5.19967) rot=(0,-1,0;0.007936rad)
  sketch-geometry (16):
    g0: LineSegment StartX=24.7884 StartY=10.4386 StartZ=0 EndX=1.16868 EndY=-0.577594 EndZ=0
    g1: ArcOfCircle CenterX=-0.732063 CenterY=-2.89862 CenterZ=0 NormalX=0 NormalY=0 NormalZ=1 AngleXU=0 Radius=3 StartAngle=6.27142 EndAngle=7.16781
    g2: LineSegment StartX=2.26773 StartY=-2.93391 StartZ=0 EndX=13.015 EndY=2.0786 EndZ=0
    g3: ArcOfCircle CenterX=25.2362 CenterY=-29.649 CenterZ=0 NormalX=0 NormalY=0 NormalZ=1 AngleXU=0 Radius=34 StartAngle=1.20312 EndAngle=1.93847
    g4: ArcOfCircle CenterX=25.2366 CenterY=9.54034 CenterZ=0 NormalX=0 NormalY=0 NormalZ=1 AngleXU=0 Radius=1.00385 StartAngle=1.16095 EndAngle=2.0336
    g5: LineSegment StartX=25.6366 StartY=10.4611 StartZ=0 EndX=49.3155 EndY=-0.577787 EndZ=0
    g6: LineSegment StartX=37.4573 StartY=2.0786 StartZ=0 EndX=48.2169 EndY=-2.93448 EndZ=0
    g7: ArcOfCircle CenterX=51.2167 CenterY=-2.89849 CenterZ=0 NormalX=0 NormalY=0 NormalZ=1 AngleXU=0 Radius=3 StartAngle=2.25714 EndAngle=3.15359
    g8: LineSegment [constr] StartX=2.27651 StartY=-0.0609062 StartZ=0 EndX=1.85382 EndY=0.84537 EndZ=0
    g9: LineSegment [constr] StartX=3.3756 StartY=-2.4172 StartZ=0 EndX=3.79829 EndY=-3.32348 EndZ=0
    g10: LineSegment [constr] StartX=48.2076 StartY=-0.0612903 StartZ=0 EndX=48.6302 EndY=0.845059 EndZ=0
    g11: LineSegment [constr] StartX=47.1086 StartY=-2.41808 StartZ=0 EndX=46.6862 EndY=-3.32453 EndZ=0
    g12: LineSegment [constr] StartX=25.2366 StartY=9.54034 StartZ=0 EndX=25.2366 EndY=10.5442 EndZ=0
    g13: LineSegment [constr] StartX=25.2366 StartY=10.5442 StartZ=0 EndX=25.2366 EndY=11.5442 EndZ=0
    g14: LineSegment [constr] StartX=25.2364 StartY=-29.2294 StartZ=0 EndX=25.2364 EndY=3.35095 EndZ=0
    g15: LineSegment [constr] StartX=25.2364 StartY=3.35095 StartZ=0 EndX=25.2364 EndY=4.35095 EndZ=0
  constraints (56):
    c: Coincident(g1,g0)
    c: Coincident(g2,g1)
    c: Coincident(g3,g2)
    c: Coincident(g4,g0)
    c: Coincident(g5,g4)
    c: PointOnObject(g5,g-8)
    c: Coincident(g6,g3)
    c: PointOnObject(g6,g-8)
    c: Coincident(g7,g6)
    c: Coincident(g7,g5)
    c: PointOnObject(g0,g-10)
    c: PointOnObject(g1,g-10)
    c: PointOnObject(g8,g0)
    c: PointOnObject(g8,g-4)
    c: PointOnObject(g9,g2)
    c: PointOnObject(g9,g-11)
    c: Perpendicular(g0,g8)
    c: Perpendicular(g-11,g9)
    c: Parallel(g2,g-11)
    c: Parallel(g0,g-4)
    c: Distance(g9,g-11) = 2
    c: Distance(g8,g-4) = 2
    c: Distance(g8) = 1
    c: Distance(g9) = 1
    c: Radius(g1) = 3
    c: PointOnObject(g10,g5)
    c: PointOnObject(g10,g-3)
    c: PointOnObject(g11,g6)
    c: PointOnObject(g11,g-7)
    c: Parallel(g5,g-3)
    c: Parallel(g6,g-7)
    c: Perpendicular(g-7,g11)
    c: Perpendicular(g-3,g10)
    c: Distance(g-3,g10) = 2
    c: Distance(g11,g-7) = 2
    c: Distance(g11) = 1
    c: Distance(g10) = 1
    c: Radius(g7) = 3
    c: Coincident(g12,g4)
    c: PointOnObject(g12,g4)
    c: Vertical(g12)
    c: Coincident(g13,g12)
    c: PointOnObject(g13,g-6)
    c: Vertical(g13)
    c: DistanceY(g13,g13) = 1
    c: DistanceX(g-6,g4) = 0
    c: DistanceX(g12,g4) = 0.4
    c: Coincident(g14,g-5)
    c: PointOnObject(g14,g-5)
    c: Vertical(g14)
    c: Coincident(g15,g14)
    c: PointOnObject(g15,g3)
    c: Vertical(g15)
    c: DistanceY(g15,g15) = 1
    c: Radius(g3) = 34
    c: DistanceY(g2,g3) = 0
FEATURE [PartDesign::Pocket] Pocket031
  BaseFeature = -> Pocket030
  Direction = (0.00793626,0,-0.999969)
  Length = 1
  Length2 = 5
  Profile = -> Sketch078
  ReferenceAxis = -> Sketch078 [N_Axis]
  Refine = true
  Suppressed = false
  Type = 0
FEATURE [Sketcher::SketchObject] Sketch079
  ArcFitTolerance = 1e-06
  AttachmentSupport = -> [Pocket031]
  ExternalGeometry = -> [Pocket031]
  FullyConstrained = true
  MakeInternals = false
  MapMode = 5
  Placement = pos=(0,0,-0.1) rot=(1,0,0;3.14159rad)
  sketch-geometry (2):
    g0: Circle CenterX=-0.773401 CenterY=2.89859 CenterZ=0 NormalX=0 NormalY=0 NormalZ=1 AngleXU=0 Radius=0.75
    g1: Circle CenterX=-0.773401 CenterY=2.89859 CenterZ=0 NormalX=0 NormalY=0 NormalZ=1 AngleXU=0 Radius=2.5
  constraints (4):
    c: Coincident(g0,g-3)
    c: Equal(g0,g-3)
    c: Coincident(g1,g0)
    c: Radius(g1) = 2.5
FEATURE [PartDesign::Pocket] Pocket032
  BaseFeature = -> Pocket031
  Direction = (0,0,1)
  Length = 1
  Length2 = 5
  Profile = -> Sketch079
  ReferenceAxis = -> Sketch079 [N_Axis]
  Refine = true
  Suppressed = false
  Type = 0
FEATURE [Sketcher::SketchObject] Sketch080
  ArcFitTolerance = 1e-06
  AttachmentSupport = -> [Pocket032]
  ExternalGeometry = -> [Pocket032]
  FullyConstrained = true
  MakeInternals = false
  MapMode = 5
  Placement = pos=(0,0,5.7) rot=(0,0,1;0rad)
  sketch-geometry (2):
    g0: Circle CenterX=-0.773401 CenterY=-2.89859 CenterZ=0 NormalX=0 NormalY=0 NormalZ=1 AngleXU=0 Radius=0.75
    g1: Circle CenterX=-0.773401 CenterY=-2.89859 CenterZ=0 NormalX=0 NormalY=0 NormalZ=1 AngleXU=0 Radius=2.5
  constraints (4):
    c: Coincident(g0,g-3)
    c: Equal(g0,g-3)
    c: Coincident(g1,g0)
    c: Radius(g1) = 2.5
FEATURE [PartDesign::Pocket] Pocket033
  BaseFeature = -> Pocket032
  Direction = (0,0,-1)
  Length = 1
  Length2 = 5
  Profile = -> Sketch080
  ReferenceAxis = -> Sketch080 [N_Axis]
  Refine = true
  Suppressed = false
  Type = 0
FEATURE [Sketcher::SketchObject] Sketch081
  ArcFitTolerance = 1e-06
  AttachmentOffset = pos=(0,0,-1.9) rot=(0,0,1;0rad)
  AttachmentSupport = -> [Pocket033]
  ExternalGeometry = -> [Pocket033]
  FullyConstrained = true
  MakeInternals = false
  MapMode = 5
  Placement = pos=(0,0,3.8) rot=(0,0,1;0rad)
  sketch-geometry (1):
    g0: Circle CenterX=-0.773401 CenterY=-2.89859 CenterZ=0 NormalX=0 NormalY=0 NormalZ=1 AngleXU=0 Radius=3
  constraints (2):
    c: Coincident(g0,g-3)
    c: Equal(g0,g-3)
FEATURE [PartDesign::Pocket] Pocket034
  BaseFeature = -> Pocket033
  Direction = (0,0,-1)
  Length = 2
  Length2 = 5
  Profile = -> Sketch081
  ReferenceAxis = -> Sketch081 [N_Axis]
  Refine = true
  Suppressed = false
  Type = 0
FEATURE [Sketcher::SketchObject] Sketch082
  ArcFitTolerance = 1e-06
  AttachmentSupport = -> [Pocket034]
  ExternalGeometry = -> [Pocket034]
  FullyConstrained = true
  MakeInternals = false
  MapMode = 5
  Placement = pos=(-0.033331,0,4.1997) rot=(0,-1,0;0.007936rad)
  sketch-geometry (4):
    g0: LineSegment StartX=1.16868 StartY=-0.577594 StartZ=0 EndX=2.98123 EndY=0.267777 EndZ=0
    g1: LineSegment StartX=2.26773 StartY=-2.93391 StartZ=0 EndX=4.08023 EndY=-2.08857 EndZ=0
    g2: LineSegment StartX=2.98123 StartY=0.267777 StartZ=0 EndX=4.08023 EndY=-2.08857 EndZ=0
    g3: ArcOfCircle CenterX=-0.732063 CenterY=-2.89862 CenterZ=0 NormalX=0 NormalY=0 NormalZ=1 AngleXU=0 Radius=3 StartAngle=6.27142 EndAngle=7.16781
  constraints (11):
    c: Coincident(g0,g-3)
    c: PointOnObject(g0,g-3)
    c: Coincident(g1,g-5)
    c: PointOnObject(g1,g-5)
    c: Coincident(g2,g0)
    c: Coincident(g2,g1)
    c: Coincident(g3,g-3)
    c: Coincident(g3,g1)
    c: Radius(g3) = 3
    c: Perpendicular(g2,g0)
    c: Distance(g0) = 2
FEATURE [PartDesign::Pad] Pad050
  BaseFeature = -> Pocket034
  Direction = (-0.00793626,0,0.999969)
  Length = 1
  Length2 = 10
  Profile = -> Sketch082
  ReferenceAxis = -> Sketch082 [N_Axis]
  Refine = true
  Suppressed = false
  Type = 0
FEATURE [Sketcher::SketchObject] Sketch083
  ArcFitTolerance = 1e-06
  AttachmentSupport = -> [Pad050]
  ExternalGeometry = -> [Pad050]
  FullyConstrained = true
  MakeInternals = false
  MapMode = 5
  Placement = pos=(0.0111107,0,1.39994) rot=(0.999992,0,-0.003968;3.14159rad)
  sketch-geometry (4):
    g0: LineSegment StartX=2.22247 StartY=2.82018 StartZ=0 EndX=4.03502 EndY=1.97481 EndZ=0
    g1: LineSegment StartX=1.12424 StartY=0.577594 StartZ=0 EndX=2.97974 EndY=-0.287809 EndZ=0
    g2: LineSegment StartX=2.97974 StartY=-0.287809 StartZ=0 EndX=4.03502 EndY=1.97481 EndZ=0
    g3: ArcOfCircle CenterX=-0.776505 CenterY=2.89862 CenterZ=0 NormalX=0 NormalY=0 NormalZ=1 AngleXU=0 Radius=3 StartAngle=5.39856 EndAngle=6.25703
  constraints (11):
    c: Coincident(g0,g-4)
    c: PointOnObject(g0,g-3)
    c: Coincident(g1,g-5)
    c: PointOnObject(g1,g-5)
    c: Coincident(g2,g1)
    c: Coincident(g2,g0)
    c: Coincident(g3,g0)
    c: Coincident(g3,g-5)
    c: Radius(g3) = 3
    c: Perpendicular(g2,g0)
    c: Distance(g0) = 2
FEATURE [PartDesign::Pad] Pad051
  BaseFeature = -> Pad050
  Direction = (-0.00793626,0,-0.999969)
  Length = 1
  Length2 = 10
  Profile = -> Sketch083
  ReferenceAxis = -> Sketch083 [N_Axis]
  Refine = true
  Suppressed = false
  Type = 0
FEATURE [Sketcher::SketchObject] Sketch084
  ArcFitTolerance = 1e-06
  AttachmentOffset = pos=(0,0,-1) rot=(0,0,1;0rad)
  AttachmentSupport = -> [Pad051]
  ExternalGeometry = -> [Pad051]
  FullyConstrained = true
  MakeInternals = false
  MapMode = 5
  Placement = pos=(0,0,5.1) rot=(0,0,1;0rad)
  sketch-geometry (1):
    g0: Circle CenterX=25.1945 CenterY=7.74034 CenterZ=0 NormalX=0 NormalY=0 NormalZ=1 AngleXU=0 Radius=1.4
  constraints (3):
    c: Diameter(g0) = 2.8
    c: DistanceX(g0,g-3) = 0
    c: DistanceY(g0,g-3) = 1.8
FEATURE [PartDesign::Pad] Pad052
  BaseFeature = -> Pad051
  Direction = (0,0,1)
  Length = 4.5
  Length2 = 10
  Profile = -> Sketch084
  ReferenceAxis = -> Sketch084 [N_Axis]
  Refine = true
  Reversed = true
  Suppressed = false
  Type = 0
FEATURE [Sketcher::SketchObject] Sketch085
  ArcFitTolerance = 1e-06
  AttachmentSupport = -> [Pad052]
  ExternalGeometry = -> [Pad052]
  FullyConstrained = true
  MakeInternals = false
  MapMode = 5
  Placement = pos=(0,0,5.1) rot=(0,0,1;0rad)
  sketch-geometry (7):
    g0: LineSegment [constr] StartX=25.1945 StartY=7.74034 StartZ=0 EndX=26.3687 EndY=6.97795 EndZ=0
    g1: LineSegment [constr] StartX=26.3687 StartY=6.97795 StartZ=0 EndX=43.9818 EndY=-4.45796 EndZ=0
    g2: LineSegment StartX=25.1945 StartY=7.74034 StartZ=0 EndX=24.9223 EndY=7.32098 EndZ=0
    g3: LineSegment StartX=24.9223 StartY=7.32098 StartZ=0 EndX=32.2159 EndY=2.58533 EndZ=0
    g4: LineSegment StartX=32.2159 StartY=2.58533 StartZ=0 EndX=32.7605 EndY=3.42405 EndZ=0
    g5: LineSegment StartX=32.7605 StartY=3.42405 StartZ=0 EndX=25.4668 EndY=8.1597 EndZ=0
    g6: LineSegment StartX=25.4668 StartY=8.1597 StartZ=0 EndX=25.1945 EndY=7.74034 EndZ=0
  constraints (20):
    c: Coincident(g0,g-3)
    c: PointOnObject(g0,g-3)
    c: Angle(g0,g-4) = 0.139626
    c: Coincident(g1,g0)
    c: Angle(g0,g1) = 3.14159
    c: Distance(g1) = 21
    c: Coincident(g2,g0)
    c: Coincident(g3,g2)
    c: Coincident(g4,g3)
    c: Coincident(g5,g4)
    c: Coincident(g6,g5)
    c: Coincident(g6,g0)
    c: Parallel(g1,g5)
    c: Parallel(g1,g3)
    c: Distance(g6) = 0.5
    c: Distance(g2) = 0.5
    c: Perpendicular(g2,g0)
    c: Perpendicular(g6,g0)
    c: Perpendicular(g4,g3)
    c: PointOnObject(g3,g-5)
FEATURE [PartDesign::Pad] Pad053
  BaseFeature = -> Pad052
  Direction = (0,0,1)
  Length = 4.5
  Length2 = 10
  Profile = -> Sketch085
  ReferenceAxis = -> Sketch085 [N_Axis]
  Refine = true
  Reversed = true
  Suppressed = false
  Type = 0
FEATURE [PartDesign::Pad] Pad054
  BaseFeature = -> Pad053
  Direction = (0,0,1)
  Length = 0.5
  Length2 = 10
  Profile = -> Pad053 [Face52]
  Refine = true
  Suppressed = false
  Type = 0
FEATURE [PartDesign::Pad] Pad055
  BaseFeature = -> Pad054
  Direction = (0,0,-1)
  Length = 0.5
  Length2 = 10
  Profile = -> Pad054 [Face38]
  Refine = true
  Suppressed = false
  Type = 0
FEATURE [Sketcher::SketchObject] Sketch086
  ArcFitTolerance = 1e-06
  AttachmentSupport = -> [Pad055]
  ExternalGeometry = -> [Pad055]
  FullyConstrained = true
  MakeInternals = false
  MapMode = 5
  Placement = pos=(0,0,0.1) rot=(1,0,0;3.14159rad)
  sketch-geometry (9):
    g0: Circle [constr] CenterX=25.1945 CenterY=-7.74034 CenterZ=0 NormalX=0 NormalY=0 NormalZ=1 AngleXU=0 Radius=1.4
    g1: LineSegment [constr] StartX=25.1945 StartY=-7.74034 StartZ=0 EndX=26.3687 EndY=-6.97795 EndZ=0
    g2: LineSegment [constr] StartX=26.3687 StartY=-6.97795 StartZ=0 EndX=43.9818 EndY=4.45796 EndZ=0
    g3: LineSegment StartX=32.6403 StartY=-4.09821 StartZ=0 EndX=44.5264 EndY=3.61924 EndZ=0
    g4: LineSegment StartX=44.5264 StartY=3.61924 StartZ=0 EndX=43.9818 EndY=4.45796 EndZ=0
    g5: LineSegment StartX=43.9818 StartY=4.45796 StartZ=0 EndX=43.4372 EndY=5.29667 EndZ=0
    g6: LineSegment StartX=43.4372 StartY=5.29667 StartZ=0 EndX=31.5512 EndY=-2.42078 EndZ=0
    g7: LineSegment StartX=32.6403 StartY=-4.09821 StartZ=0 EndX=32.0957 EndY=-3.2595 EndZ=0
    g8: LineSegment StartX=32.0957 StartY=-3.2595 StartZ=0 EndX=31.5512 EndY=-2.42078 EndZ=0
  constraints (25):
    c: Coincident(g0,g-3)
    c: PointOnObject(g-3,g0)
    c: Coincident(g1,g0)
    c: PointOnObject(g1,g0)
    c: Parallel(g-4,g1)
    c: Coincident(g2,g1)
    c: Distance(g2) = 21
    c: Parallel(g2,g-4)
    c: Coincident(g4,g3)
    c: Coincident(g4,g2)
    c: Coincident(g5,g2)
    c: Coincident(g6,g5)
    c: Parallel(g2,g3)
    c: Parallel(g2,g6)
    c: Coincident(g7,g3)
    c: PointOnObject(g7,g2)
    c: Coincident(g8,g7)
    c: Coincident(g8,g6)
    c: PointOnObject(g-5,g7)
    c: Distance(g7) = 1
    c: Distance(g8) = 1
    c: Perpendicular(g7,g2)
    c: Perpendicular(g8,g2)
    c: Perpendicular(g4,g2)
    c: Perpendicular(g5,g2)
FEATURE [PartDesign::Pad] Pad056
  BaseFeature = -> Pad055
  Direction = (0,0,-1)
  Length = 6
  Length2 = 10
  Profile = -> Sketch086
  ReferenceAxis = -> Sketch086 [N_Axis]
  Refine = true
  Reversed = true
  Suppressed = false
  Type = 0
FEATURE [PartDesign::Pad] Pad057
  BaseFeature = -> Pad056
  Direction = (0,0,-1)
  Length = 0.5
  Length2 = 10
  Profile = -> Pad056 [Face44]
  Refine = true
  Suppressed = false
  Type = 0
FEATURE [Sketcher::SketchObject] Sketch087
  ArcFitTolerance = 1e-06
  AttachmentSupport = -> [Pad057]
  ExternalGeometry = -> [Pad057]
  FullyConstrained = true
  MakeInternals = false
  MapMode = 5
  Placement = pos=(0,0,0.1) rot=(1,0,0;3.14159rad)
  sketch-geometry (4):
    g0: LineSegment StartX=29.837 StartY=-4.12989 StartZ=0 EndX=31.8234 EndY=-2.84014 EndZ=0
    g1: LineSegment StartX=31.8234 StartY=-2.84014 StartZ=0 EndX=32.3676 EndY=-3.67816 EndZ=0
    g2: ArcOfCircle CenterX=25.2338 CenterY=28.9708 CenterZ=0 NormalX=0 NormalY=0 NormalZ=1 AngleXU=0 Radius=33.4193 StartAngle=4.85057 EndAngle=4.92751
    g3: GeomPoint [constr] X=29.8371 Y=-4.12989 Z=0
  constraints (10):
    c: Coincident(g0,g-3)
    c: PointOnObject(g0,g-5)
    c: Angle(g0,g-3) = 3.14159
    c: Coincident(g1,g0)
    c: Coincident(g1,g-5)
    c: Coincident(g2,g1)
    c: PointOnObject(g3,g-6)
    c: PointOnObject(g3,g2)
    c: Tangent(g-6,g2,g3) = -1.5708
    c: Coincident(g2,g0)
FEATURE [PartDesign::Pad] Pad058
  BaseFeature = -> Pad057
  Direction = (0,0,-1)
  Length = 5.5
  Length2 = 10
  Profile = -> Sketch087
  ReferenceAxis = -> Sketch087 [N_Axis]
  Refine = true
  Reversed = true
  Suppressed = false
  Type = 0
FEATURE [PartDesign::Fillet] Fillet004
  Base = -> Pad058 [Edge3,Edge1,Edge6,Edge19]
  BaseFeature = -> Pad058
  Radius = 0.49
  Refine = true
  SupportTransform = false
  Suppressed = false
  UseAllEdges = false
FEATURE [PartDesign::Pad] Pad059
  BaseFeature = -> Fillet004
  Direction = (0,0,1)
  Length = 0.25
  Length2 = 10
  Profile = -> Fillet004 [Face13]
  Refine = true
  Suppressed = false
  Type = 0
FEATURE [Sketcher::SketchObject] Sketch088
  ArcFitTolerance = 1e-06
  AttachmentSupport = -> [Pad059]
  ExternalGeometry = -> [Pad059]
  FullyConstrained = true
  MakeInternals = false
  MapMode = 5
  Placement = pos=(0,0,0.1) rot=(1,0,0;3.14159rad)
  sketch-geometry (4):
    g0: ArcOfCircle CenterX=25.1945 CenterY=-7.74034 CenterZ=0 NormalX=0 NormalY=0 NormalZ=1 AngleXU=0 Radius=1.4 StartAngle=0.94108 EndAngle=6.49385
    g1: LineSegment StartX=26.019 StartY=-6.60887 StartZ=0 EndX=31.8234 EndY=-2.84014 EndZ=0
    g2: LineSegment StartX=31.8234 StartY=-2.84014 StartZ=0 EndX=32.368 EndY=-3.67886 EndZ=0
    g3: LineSegment StartX=32.368 StartY=-3.67886 StartZ=0 EndX=26.5636 EndY=-7.44759 EndZ=0
  constraints (8):
    c: Coincident(g0,g-5)
    c: Tangent(g0,g-7) = -1.5708
    c: Coincident(g1,g0)
    c: Coincident(g1,g-6)
    c: Coincident(g2,g1)
    c: Coincident(g2,g-5)
    c: Coincident(g3,g-5)
    c: Coincident(g3,g0)
FEATURE [PartDesign::Pad] Pad060
  BaseFeature = -> Pad059
  Direction = (0,0,-1)
  Length = 0.25
  Length2 = 10
  Profile = -> Sketch088
  ReferenceAxis = -> Sketch088 [N_Axis]
  Refine = true
  Suppressed = false
  Type = 0
FEATURE [PartDesign::Fillet] Fillet005
  Base = -> Pad060 [Edge105,Edge109,Edge68,Edge67]
  BaseFeature = -> Pad060
  Radius = 0.25
  Refine = true
  SupportTransform = false
  Suppressed = false
  UseAllEdges = false
FEATURE [Sketcher::SketchObject] Sketch089
  ArcFitTolerance = 1e-06
  AttachmentSupport = -> [Fillet005]
  ExternalGeometry = -> [Fillet005]
  FullyConstrained = true
  MakeInternals = false
  MapMode = 5
  Placement = pos=(0,0,5.85) rot=(0,0,1;0rad)
  sketch-geometry (1):
    g0: Circle CenterX=25.1945 CenterY=7.74034 CenterZ=0 NormalX=0 NormalY=0 NormalZ=1 AngleXU=0 Radius=0.65
  constraints (2):
    c: Coincident(g0,g-3)
    c: Diameter(g0) = 1.3
FEATURE [PartDesign::Pad] Pad061
  BaseFeature = -> Fillet005
  Direction = (0,0,1)
  Length = 0.5
  Length2 = 10
  Profile = -> Sketch089
  ReferenceAxis = -> Sketch089 [N_Axis]
  Refine = true
  Suppressed = false
  Type = 0
FEATURE [Sketcher::SketchObject] Sketch090
  ArcFitTolerance = 1e-06
  AttachmentSupport = -> [Pad061]
  ExternalGeometry = -> [Pad061]
  FullyConstrained = true
  MakeInternals = false
  MapMode = 5
  Placement = pos=(0,0,-0.15) rot=(1,0,0;3.14159rad)
  sketch-geometry (1):
    g0: Circle CenterX=25.1945 CenterY=-7.74034 CenterZ=0 NormalX=0 NormalY=0 NormalZ=1 AngleXU=0 Radius=0.65
  constraints (2):
    c: Coincident(g0,g-3)
    c: Diameter(g0) = 1.3
FEATURE [PartDesign::Pad] Pad062
  BaseFeature = -> Pad061
  Direction = (0,0,-1)
  Length = 0.5
  Length2 = 10
  Profile = -> Sketch090
  ReferenceAxis = -> Sketch090 [N_Axis]
  Refine = true
  Suppressed = false
  Type = 0
FEATURE [Sketcher::SketchObject] Sketch091
  ArcFitTolerance = 1e-06
  AttachmentOffset = pos=(0,0,-2.05) rot=(0,0,1;0rad)
  AttachmentSupport = -> [Pad062]
  ExternalGeometry = -> [Pad062]
  FullyConstrained = true
  MakeInternals = false
  MapMode = 5
  Placement = pos=(0,0,4.3) rot=(0,0,1;0rad)
  sketch-geometry (2):
    g0: LineSegment StartX=4.16885 StartY=1.9444 StartZ=0 EndX=6.70641 EndY=3.12795 EndZ=0
    g1: ArcOfCircle CenterX=5.43763 CenterY=2.53618 CenterZ=0 NormalX=0 NormalY=0 NormalZ=1 AngleXU=0 Radius=1.4 StartAngle=0.436418 EndAngle=3.57801
  constraints (7):
    c: PointOnObject(g0,g-3)
    c: PointOnObject(g0,g-3)
    c: Coincident(g1,g0)
    c: Coincident(g1,g0)
    c: PointOnObject(g1,g0)
    c: Diameter(g1) = 2.8
    c: Distance(g-1,g0) = 4.6
FEATURE [PartDesign::Pad] Pad063
  BaseFeature = -> Pad062
  Direction = (0,0,1)
  Length = 3
  Length2 = 10
  Profile = -> Sketch091
  ReferenceAxis = -> Sketch091 [N_Axis]
  Refine = true
  Reversed = true
  Suppressed = false
  Type = 0
FEATURE [Sketcher::SketchObject] Sketch092
  ArcFitTolerance = 1e-06
  AttachmentOffset = pos=(0,0,-0.5) rot=(0,0,1;0rad)
  AttachmentSupport = -> [Pad063]
  ExternalGeometry = -> [Pad063]
  FullyConstrained = true
  MakeInternals = false
  MapMode = 5
  Placement = pos=(0,0,3.8) rot=(0,0,1;0rad)
  sketch-geometry (4):
    g0: LineSegment StartX=6.70641 StartY=3.12795 StartZ=0 EndX=23.0193 EndY=10.7365 EndZ=0
    g1: LineSegment StartX=23.0193 StartY=10.7365 StartZ=0 EndX=22.5966 EndY=11.6428 EndZ=0
    g2: LineSegment StartX=22.5966 StartY=11.6428 StartZ=0 EndX=5.67242 EndY=3.74911 EndZ=0
    g3: LineSegment StartX=6.70641 StartY=3.12795 StartZ=0 EndX=5.67242 EndY=3.74911 EndZ=0
  constraints (11):
    c: Coincident(g0,g-3)
    c: PointOnObject(g0,g-4)
    c: Distance(g0) = 18
    c: Coincident(g1,g0)
    c: Coincident(g2,g1)
    c: Coincident(g3,g0)
    c: Coincident(g3,g2)
    c: Parallel(g0,g2)
    c: Distance(g1) = 1
    c: Perpendicular(g0,g1)
    c: Angle(g3,g2) = 0.977384
FEATURE [PartDesign::Pad] Pad064
  BaseFeature = -> Pad063
  Direction = (0,0,1)
  Length = 2
  Length2 = 10
  Profile = -> Sketch092
  ReferenceAxis = -> Sketch092 [N_Axis]
  Refine = true
  Reversed = true
  Suppressed = false
  Type = 0
FEATURE [Sketcher::SketchObject] Sketch093
  ArcFitTolerance = 1e-06
  AttachmentSupport = -> [Pad064]
  ExternalGeometry = -> [Pad064]
  FullyConstrained = true
  MakeInternals = false
  MapMode = 5
  Placement = pos=(-0.422696,0.906271,0) rot=(-0.154901,0.698572,0.698572;3.44895rad)
  sketch-geometry (8):
    g0: LineSegment StartX=-9.7798 StartY=4.3 StartZ=0 EndX=-9.7798 EndY=1.3 EndZ=0
    g1: LineSegment StartX=-9.7798 StartY=1.3 StartZ=0 EndX=-8.7798 EndY=1.3 EndZ=0
    g2: LineSegment StartX=-8.7798 StartY=1.3 StartZ=0 EndX=-8.7798 EndY=4.3 EndZ=0
    g3: LineSegment StartX=-8.7798 StartY=4.3 StartZ=0 EndX=-9.7798 EndY=4.3 EndZ=0
    g4: LineSegment StartX=-25.4 StartY=4.3 StartZ=0 EndX=-25.4 EndY=1.3 EndZ=0
    g5: LineSegment StartX=-25.4 StartY=1.3 StartZ=0 EndX=-18.4 EndY=1.3 EndZ=0
    g6: LineSegment StartX=-18.4 StartY=1.3 StartZ=0 EndX=-18.4 EndY=4.3 EndZ=0
    g7: LineSegment StartX=-18.4 StartY=4.3 StartZ=0 EndX=-25.4 EndY=4.3 EndZ=0
  constraints (25):
    c: Coincident(g0,g1)
    c: Coincident(g1,g2)
    c: Coincident(g2,g3)
    c: Coincident(g3,g0)
    c: Vertical(g0)
    c: Vertical(g2)
    c: Horizontal(g1)
    c: Horizontal(g3)
    c: DistanceY(g0,g0) = 3
    c: DistanceY(g-3,g2) = 0.5
    c: DistanceX(g3,g3) = 1
    c: DistanceX(g2,g-3) = 1.8
    c: Coincident(g4,g5)
    c: Coincident(g5,g6)
    c: Coincident(g6,g7)
    c: Coincident(g7,g4)
    c: Vertical(g4)
    c: Vertical(g6)
    c: Horizontal(g5)
    c: Horizontal(g7)
    c: DistanceY(g4,g4) = 3
    c: DistanceY(g-3,g4) = 0.5
    c: PointOnObject(g-3,g4)
    c: DistanceX(g7,g7) = 7
    c: DistanceX(g5,g0) = 8.6202
FEATURE [PartDesign::Pad] Pad065
  BaseFeature = -> Pad064
  Direction = (-0.422696,0.906271,0)
  Length = 2
  Length2 = 10
  Profile = -> Sketch093
  ReferenceAxis = -> Sketch093 [N_Axis]
  Refine = true
  Reversed = true
  Suppressed = false
  Type = 0
FEATURE [PartDesign::Pad] Pad066
  BaseFeature = -> Pad065
  Direction = (-0.422696,0.906271,0)
  Length = 1
  Length2 = 10
  Profile = -> Sketch093
  ReferenceAxis = -> Sketch093 [N_Axis]
  Refine = true
  Suppressed = false
  Type = 0
FEATURE [PartDesign::Fillet] Fillet006
  Base = -> Pad066 [Edge249,Edge257,Edge255,Edge252]
  BaseFeature = -> Pad066
  Radius = 0.99
  Refine = true
  SupportTransform = false
  Suppressed = false
  UseAllEdges = false
FEATURE [Sketcher::SketchObject] Sketch094
  ArcFitTolerance = 1e-06
  AttachmentSupport = -> [Fillet006]
  ExternalGeometry = -> [Fillet006]
  FullyConstrained = true
  MakeInternals = false
  MapMode = 5
  Placement = pos=(0,0,4.3) rot=(0,0,1;0rad)
  sketch-geometry (3):
    g0: LineSegment StartX=15.83 StartY=9.59015 StartZ=0 EndX=23.0193 EndY=10.7365 EndZ=0
    g1: LineSegment StartX=23.0193 StartY=10.7365 StartZ=0 EndX=22.1739 EndY=12.549 EndZ=0
    g2: LineSegment StartX=22.1739 StartY=12.549 StartZ=0 EndX=15.83 EndY=9.59015 EndZ=0
  constraints (6):
    c: Coincident(g0,g-4)
    c: Coincident(g0,g-5)
    c: Coincident(g1,g0)
    c: Coincident(g1,g-4)
    c: Coincident(g2,g1)
    c: Coincident(g2,g0)
FEATURE [PartDesign::Pocket] Pocket035
  BaseFeature = -> Fillet006
  Direction = (0,0,-1)
  Length = 5
  Length2 = 5
  Profile = -> Sketch094
  ReferenceAxis = -> Sketch094 [N_Axis]
  Refine = true
  Suppressed = false
  Type = 0
FEATURE [Sketcher::SketchObject] Sketch095
  ArcFitTolerance = 1e-06
  AttachmentSupport = -> [Pocket035]
  ExternalGeometry = -> [Pocket035]
  FullyConstrained = true
  MakeInternals = false
  MapMode = 5
  Placement = pos=(0,0,4.3) rot=(0,0,1;0rad)
  sketch-geometry (3):
    g0: LineSegment StartX=15.83 StartY=9.59015 StartZ=0 EndX=16.218 EndY=7.57532 EndZ=0
    g1: LineSegment StartX=16.218 StartY=7.57532 StartZ=0 EndX=16.6712 EndY=7.78667 EndZ=0
    g2: LineSegment StartX=16.6712 StartY=7.78667 StartZ=0 EndX=15.83 EndY=9.59015 EndZ=0
  constraints (7):
    c: Coincident(g0,g-3)
    c: PointOnObject(g0,g-4)
    c: Coincident(g1,g0)
    c: Coincident(g1,g-4)
    c: Coincident(g2,g1)
    c: Coincident(g2,g0)
    c: Distance(g1) = 0.5
FEATURE [PartDesign::Pad] Pad067
  BaseFeature = -> Pocket035
  Direction = (0,0,1)
  Length = 3
  Length2 = 10
  Profile = -> Sketch095
  ReferenceAxis = -> Sketch095 [N_Axis]
  Refine = true
  Reversed = true
  Suppressed = false
  Type = 0
FEATURE [PartDesign::SubShapeBinder] Binder001
  BindCopyOnChange = 0
  BindMode = 0
  ClaimChildren = false
  Context = -> Body003 [Binder001.]
  Fuse = false
  MakeFace = true
  OffsetFill = false
  OffsetIntersection = false
  OffsetJoinType = 0
  OffsetOpenResult = false
  PartialLoad = false
  Refine = true
  Relative = true
  Support = -> [Body[Pocket016.Face64]]
  _Version = 2
FEATURE [Sketcher::SketchObject] Sketch096
  ArcFitTolerance = 1e-06
  AttachmentSupport = -> [Binder001]
  ExternalGeometry = -> [Binder001]
  FullyConstrained = true
  MakeInternals = false
  MapMode = 5
  Placement = pos=(0,-9,0) rot=(0,0.707107,0.707107;3.14159rad)
  sketch-geometry (6):
    g0: LineSegment StartX=-38.8695 StartY=12.15 StartZ=0 EndX=-42.45 EndY=1.99145 EndZ=0
    g1: LineSegment StartX=-42.45 StartY=1.99145 StartZ=0 EndX=-42.45 EndY=0.05 EndZ=0
    g2: LineSegment StartX=-42.45 StartY=0.05 StartZ=0 EndX=-24.35 EndY=0.05 EndZ=0
    g3: LineSegment StartX=-24.35 StartY=0.05 StartZ=0 EndX=-24.35 EndY=12.15 EndZ=0
    g4: LineSegment StartX=-24.35 StartY=12.15 StartZ=0 EndX=-38.8695 EndY=12.15 EndZ=0
    g5: LineSegment [constr] StartX=-42.1204 StartY=2.92651 StartZ=0 EndX=-42.1676 EndY=2.94313 EndZ=0
  constraints (19):
    c: Coincident(g1,g0)
    c: Vertical(g1)
    c: Coincident(g2,g1)
    c: Horizontal(g2)
    c: Coincident(g3,g2)
    c: Vertical(g3)
    c: Coincident(g4,g3)
    c: Coincident(g4,g0)
    c: Horizontal(g4)
    c: Parallel(g-3,g0)
    c: DistanceY(g-5,g2) = 0.05
    c: DistanceX(g2,g-5) = 0.05
    c: DistanceY(g3,g-5) = 0.05
    c: DistanceX(g-6,g1) = 0.05
    c: PointOnObject(g5,g0)
    c: PointOnObject(g5,g-3)
    c: Perpendicular(g5,g-3)
    c: Distance(g5,g-6) = 1
    c: Distance(g5) = 0.05
FEATURE [PartDesign::Pad] Pad068
  Direction = (0,1,-2e-16)
  Length = 1.5
  Length2 = 10
  Profile = -> Sketch096
  ReferenceAxis = -> Sketch096 [N_Axis]
  Refine = true
  Suppressed = false
  Type = 0
FEATURE [Sketcher::SketchObject] Sketch097
  ArcFitTolerance = 1e-06
  AttachmentSupport = -> [Pad068]
  ExternalGeometry = -> [Pad068]
  FullyConstrained = true
  MakeInternals = false
  MapMode = 5
  Placement = pos=(0,-7.5,2.3e-15) rot=(0,0.707107,0.707107;3.14159rad)
  sketch-geometry (11):
    g0: LineSegment StartX=-38.8695 StartY=12.15 StartZ=0 EndX=-42.45 EndY=1.99145 EndZ=0
    g1: LineSegment StartX=-42.45 StartY=1.99145 StartZ=0 EndX=-42.45 EndY=0.05 EndZ=0
    g2: LineSegment StartX=-42.45 StartY=0.05 StartZ=0 EndX=-40.95 EndY=0.05 EndZ=0
    g3: LineSegment StartX=-40.95 StartY=0.05 StartZ=0 EndX=-40.95 EndY=1.73484 EndZ=0
    g4: LineSegment StartX=-40.95 StartY=1.73484 StartZ=0 EndX=-37.8078 EndY=10.65 EndZ=0
    g5: LineSegment StartX=-38.8695 StartY=12.15 StartZ=0 EndX=-24.35 EndY=12.15 EndZ=0
    g6: LineSegment StartX=-24.35 StartY=12.15 StartZ=0 EndX=-24.35 EndY=0.05 EndZ=0
    g7: LineSegment StartX=-24.35 StartY=0.05 StartZ=0 EndX=-25.85 EndY=0.05 EndZ=0
    g8: LineSegment StartX=-25.85 StartY=0.05 StartZ=0 EndX=-25.85 EndY=10.65 EndZ=0
    g9: LineSegment StartX=-25.85 StartY=10.65 StartZ=0 EndX=-37.8078 EndY=10.65 EndZ=0
    g10: LineSegment [constr] StartX=-40.1992 StartY=8.37747 StartZ=0 EndX=-38.7845 EndY=7.87884 EndZ=0
  constraints (29):
    c: Coincident(g0,g-5)
    c: Coincident(g0,g-4)
    c: Coincident(g1,g0)
    c: Coincident(g1,g-7)
    c: Coincident(g2,g1)
    c: PointOnObject(g2,g-7)
    c: DistanceX(g2,g2) = 1.5
    c: Coincident(g3,g2)
    c: Vertical(g3)
    c: Coincident(g4,g3)
    c: Coincident(g5,g0)
    c: Coincident(g5,g-6)
    c: Coincident(g6,g5)
    c: Coincident(g6,g-7)
    c: Coincident(g7,g6)
    c: PointOnObject(g7,g-7)
    c: Coincident(g8,g7)
    c: Vertical(g8)
    c: Coincident(g9,g8)
    c: Coincident(g9,g4)
    c: Horizontal(g9)
    c: Parallel(g0,g4)
    c: DistanceY(g4,g0) = 1.5
    c: DistanceX(g8,g5) = 1.5
    c: PointOnObject(g10,g0)
    c: PointOnObject(g10,g4)
    c: Perpendicular(g10,g0)
    c: Distance(g0,g10) = 4
    c: Distance(g10) = 1.5
FEATURE [PartDesign::Pad] Pad069
  BaseFeature = -> Pad068
  Direction = (0,1,-2e-16)
  Length = 5.4
  Length2 = 10
  Profile = -> Sketch097
  ReferenceAxis = -> Sketch097 [N_Axis]
  Refine = true
  Suppressed = false
  Type = 0
FEATURE [Sketcher::SketchObject] Sketch098
  ArcFitTolerance = 1e-06
  AttachmentSupport = -> [Pad069]
  ExternalGeometry = -> [Pad069]
  FullyConstrained = true
  MakeInternals = false
  MapMode = 5
  Placement = pos=(0,-2.1,5e-16) rot=(0,0.707107,0.707107;3.14159rad)
  sketch-geometry (5):
    g0: LineSegment StartX=-40.95 StartY=0.05 StartZ=0 EndX=-25.85 EndY=0.05 EndZ=0
    g1: LineSegment StartX=-25.85 StartY=0.05 StartZ=0 EndX=-25.85 EndY=10.65 EndZ=0
    g2: LineSegment StartX=-25.85 StartY=10.65 StartZ=0 EndX=-37.8078 EndY=10.65 EndZ=0
    g3: LineSegment StartX=-37.8078 StartY=10.65 StartZ=0 EndX=-40.95 EndY=1.73484 EndZ=0
    g4: LineSegment StartX=-40.95 StartY=1.73484 StartZ=0 EndX=-40.95 EndY=0.05 EndZ=0
  constraints (10):
    c: Coincident(g0,g-3)
    c: Coincident(g0,g-6)
    c: Coincident(g1,g0)
    c: Coincident(g1,g-6)
    c: Coincident(g2,g1)
    c: Coincident(g2,g-5)
    c: Coincident(g3,g2)
    c: Coincident(g3,g-4)
    c: Coincident(g4,g3)
    c: Coincident(g4,g0)
FEATURE [PartDesign::Pad] Pad070
  BaseFeature = -> Pad069
  Direction = (0,1,-2e-16)
  Length = 1.5
  Length2 = 10
  Profile = -> Sketch098
  ReferenceAxis = -> Sketch098 [N_Axis]
  Refine = true
  Reversed = true
  Suppressed = false
  Type = 0
FEATURE [PartDesign::Body] Body003  label="Cab"
  AllowCompound = false
  Group = -> [Binder001,Sketch096,Pad068,Sketch097,Pad069,Sketch098,Pad070]
  Origin = -> Origin003
  Tip = -> Pad070
FEATURE [Sketcher::SketchObject] Sketch099
  ArcFitTolerance = 1e-06
  AttachmentSupport = -> [XY_Plane004]
  FullyConstrained = true
  MakeInternals = false
  MapMode = 5
  sketch-geometry (5):
    g0: LineSegment StartX=4.60348 StartY=-9.77661 StartZ=0 EndX=0 EndY=-13 EndZ=0
    g1: LineSegment StartX=0 StartY=0 StartZ=0 EndX=0 EndY=-13 EndZ=0
    g2: LineSegment StartX=0 StartY=0 StartZ=0 EndX=4.60348 EndY=-3.22339 EndZ=0
    g3: ArcOfCircle CenterX=2.30917 CenterY=-6.5 CenterZ=0 NormalX=0 NormalY=0 NormalZ=1 AngleXU=0 Radius=4 StartAngle=5.32325 EndAngle=7.24312
    g4: GeomPoint [constr] X=9.28296 Y=-6.5 Z=0
  constraints (12):
    c: PointOnObject(g0,g-2)
    c: Coincident(g1,g0)
    c: DistanceY(g1,g1) = 13
    c: Coincident(g2,g1)
    c: PointOnObject(g4,g0)
    c: PointOnObject(g4,g2)
    c: Tangent(g0,g3) = 1.5708
    c: Tangent(g2,g3) = 1.5708
    c: Angle(g2,g0) = 1.22173
    c: Coincident(g1,g-1)
    c: Diameter(g3) = 8
    c: DistanceY(g3,g1) = 6.5
FEATURE [PartDesign::Pad] Pad071
  Direction = (0,0,1)
  Length = 13.8
  Length2 = 10
  Profile = -> Sketch099
  ReferenceAxis = -> Sketch099 [N_Axis]
  Refine = true
  Suppressed = false
  Type = 0
FEATURE [Sketcher::SketchObject] Sketch100
  ArcFitTolerance = 1e-06
  AttachmentSupport = -> [Pad071]
  ExternalGeometry = -> [Pad071]
  FullyConstrained = true
  MakeInternals = false
  MapMode = 5
  Placement = pos=(0,0,13.8) rot=(0,0,1;0rad)
  sketch-geometry (6):
    g0: LineSegment StartX=0 StartY=-11.5 StartZ=0 EndX=3.50917 EndY=-9.04285 EndZ=0
    g1: LineSegment StartX=0 StartY=-1.5 StartZ=0 EndX=3.50917 EndY=-3.95715 EndZ=0
    g2: ArcOfCircle CenterX=1.67222 CenterY=-6.5 CenterZ=0 NormalX=0 NormalY=0 NormalZ=1 AngleXU=0 Radius=3.13695 StartAngle=5.33799 EndAngle=7.22838
    g3: LineSegment StartX=0 StartY=-1.5 StartZ=0 EndX=0 EndY=-11.5 EndZ=0
    g4: LineSegment [constr] StartX=1.67222 StartY=-6.5 StartZ=0 EndX=4.80917 EndY=-6.5 EndZ=0
    g5: LineSegment [constr] StartX=4.80917 StartY=-6.5 StartZ=0 EndX=6.30917 EndY=-6.5 EndZ=0
  constraints (19):
    c: PointOnObject(g0,g-2)
    c: PointOnObject(g1,g-2)
    c: Coincident(g2,g1)
    c: Coincident(g2,g0)
    c: Coincident(g3,g1)
    c: Coincident(g3,g0)
    c: DistanceY(g-5,g0) = 1.5
    c: DistanceY(g1,g-1) = 1.5
    c: Parallel(g1,g-3)
    c: Parallel(g0,g-5)
    c: DistanceX(g1,g0) = 0
    c: Coincident(g4,g2)
    c: PointOnObject(g4,g2)
    c: Horizontal(g4)
    c: Coincident(g5,g4)
    c: PointOnObject(g5,g-4)
    c: Horizontal(g5)
    c: DistanceX(g5,g5) = 1.5
    c: DistanceX(g0,g4) = 1.3
FEATURE [PartDesign::Pocket] Pocket036
  BaseFeature = -> Pad071
  Direction = (0,0,-1)
  Length = 12.3
  Length2 = 5
  Profile = -> Sketch100
  ReferenceAxis = -> Sketch100 [N_Axis]
  Refine = true
  Suppressed = false
  Type = 0
FEATURE [Sketcher::SketchObject] Sketch101
  ArcFitTolerance = 1e-06
  AttachmentSupport = -> [Pocket036]
  ExternalGeometry = -> [Pocket036]
  FullyConstrained = true
  MakeInternals = false
  MapMode = 5
  Placement = pos=(0,0,13.8) rot=(0,0,1;0rad)
  sketch-geometry (4):
    g0: LineSegment StartX=0 StartY=-1.5 StartZ=0 EndX=0 EndY=-11.5 EndZ=0
    g1: LineSegment StartX=0 StartY=-11.5 StartZ=0 EndX=3.50917 EndY=-9.04285 EndZ=0
    g2: LineSegment StartX=0 StartY=-1.5 StartZ=0 EndX=3.50917 EndY=-3.95715 EndZ=0
    g3: ArcOfCircle CenterX=1.67222 CenterY=-6.5 CenterZ=0 NormalX=0 NormalY=0 NormalZ=1 AngleXU=0 Radius=3.13695 StartAngle=5.33799 EndAngle=7.22838
  constraints (9):
    c: Coincident(g0,g-3)
    c: Coincident(g0,g-5)
    c: Coincident(g1,g0)
    c: Coincident(g1,g-5)
    c: Coincident(g2,g0)
    c: Coincident(g2,g-4)
    c: Coincident(g3,g2)
    c: Coincident(g3,g1)
    c: Tangent(g3,g-4)
FEATURE [PartDesign::Pad] Pad072
  BaseFeature = -> Pocket036
  Direction = (0,0,1)
  Length = 1.5
  Length2 = 10
  Profile = -> Sketch101
  ReferenceAxis = -> Sketch101 [N_Axis]
  Refine = true
  Reversed = true
  Suppressed = false
  Type = 0
FEATURE [Sketcher::SketchObject] Sketch102
  ArcFitTolerance = 1e-06
  AttachmentSupport = -> [Pad072]
  ExternalGeometry = -> [Pad072]
  FullyConstrained = true
  MakeInternals = false
  MapMode = 5
  Placement = pos=(0,0,13.8) rot=(0,0,1;0rad)
  sketch-geometry (9):
    g0: LineSegment StartX=0 StartY=0 StartZ=0 EndX=-2 EndY=1.40042 EndZ=0
    g1: LineSegment StartX=-2 StartY=1.40042 StartZ=0 EndX=-2 EndY=-12.9004 EndZ=0
    g2: LineSegment StartX=-2 StartY=-12.9004 StartZ=0 EndX=-3.72022 EndY=-14.1049 EndZ=0
    g3: LineSegment StartX=-3.72022 StartY=-14.1049 StartZ=0 EndX=-1.57708 EndY=-15.1043 EndZ=0
    g4: LineSegment StartX=-1.57708 StartY=-15.1043 StartZ=0 EndX=0 EndY=-14 EndZ=0
    g5: LineSegment StartX=0 StartY=-14 StartZ=0 EndX=0 EndY=0 EndZ=0
    g6: LineSegment [constr] StartX=0 StartY=-6.59958 StartZ=0 EndX=-2 EndY=-6.59958 EndZ=0
    g7: LineSegment [constr] StartX=-2.49149 StartY=-13.2446 StartZ=0 EndX=-1.31688 EndY=-14.9221 EndZ=0
    g8: LineSegment [constr] StartX=-2 StartY=-12.9004 StartZ=0 EndX=0 EndY=-11.5 EndZ=0
  constraints (27):
    c: Coincident(g0,g-1)
    c: Coincident(g1,g0)
    c: Vertical(g1)
    c: Coincident(g2,g1)
    c: Coincident(g3,g2)
    c: Coincident(g4,g3)
    c: PointOnObject(g4,g-2)
    c: Coincident(g5,g4)
    c: Coincident(g5,g0)
    c: PointOnObject(g6,g1)
    c: Horizontal(g6)
    c: DistanceX(g6,g6) = 2
    c: DistanceY(g6,g0) = 8
    c: Angle(g0,g-3) = 3.14159
    c: Parallel(g-5,g4)
    c: Parallel(g2,g4)
    c: Angle(g3,g2) = 1.0472
    c: PointOnObject(g7,g2)
    c: PointOnObject(g7,g4)
    c: Perpendicular(g7,g2)
    c: Distance(g7,g2) = 1.5
    c: PointOnObject(g6,g5)
    c: DistanceY(g4,g-5) = 1
    c: Distance(g2) = 2.1
    c: Coincident(g8,g1)
    c: Coincident(g8,g-6)
    c: Angle(g2,g8) = 3.14159
FEATURE [PartDesign::Pad] Pad073
  BaseFeature = -> Pad072
  Direction = (0,0,1)
  Length = 1.5
  Length2 = 10
  Profile = -> Sketch102
  ReferenceAxis = -> Sketch102 [N_Axis]
  Refine = true
  Reversed = true
  Suppressed = false
  Type = 0
FEATURE [PartDesign::Pad] Pad074
  BaseFeature = -> Pad073
  Direction = (0,0,1)
  Length = 0.5
  Length2 = 10
  Profile = -> Sketch102
  ReferenceAxis = -> Sketch102 [N_Axis]
  Refine = true
  Suppressed = false
  Type = 0
FEATURE [Sketcher::SketchObject] Sketch103
  ArcFitTolerance = 1e-06
  AttachmentSupport = -> [Pad074]
  ExternalGeometry = -> [Pad074]
  FullyConstrained = true
  MakeInternals = false
  MapMode = 5
  Placement = pos=(3.4e-15,0,12.3) rot=(1,0,0;3.14159rad)
  sketch-geometry (10):
    g0: LineSegment StartX=-3.4e-15 StartY=1.5 StartZ=0 EndX=0 EndY=0 EndZ=0
    g1: LineSegment StartX=0 StartY=0 StartZ=0 EndX=-2 EndY=-1.40042 EndZ=0
    g2: LineSegment StartX=-3.4e-15 StartY=1.5 StartZ=0 EndX=-2 EndY=0.0995849 EndZ=0
    g3: LineSegment StartX=-2 StartY=0.0995849 StartZ=0 EndX=-2 EndY=-1.40042 EndZ=0
    g4: LineSegment StartX=-1.57708 StartY=15.1043 StartZ=0 EndX=-3.72022 EndY=14.1049 EndZ=0
    g5: LineSegment StartX=-3.72022 StartY=14.1049 StartZ=0 EndX=-2 EndY=12.9004 EndZ=0
    g6: LineSegment StartX=-1.57708 StartY=15.1043 StartZ=0 EndX=0 EndY=14 EndZ=0
    g7: LineSegment StartX=0 StartY=14 StartZ=0 EndX=0 EndY=13 EndZ=0
    g8: LineSegment StartX=0 StartY=11.5 StartZ=0 EndX=-2 EndY=12.9004 EndZ=0
    g9: LineSegment StartX=0 StartY=13 StartZ=0 EndX=0 EndY=11.5 EndZ=0
  constraints (21):
    c: Coincident(g0,g-4)
    c: Coincident(g0,g-1)
    c: Coincident(g1,g0)
    c: Coincident(g1,g-10)
    c: Coincident(g2,g0)
    c: PointOnObject(g2,g-10)
    c: Coincident(g3,g2)
    c: Coincident(g3,g1)
    c: Parallel(g1,g2)
    c: Coincident(g4,g-8)
    c: Coincident(g4,g-9)
    c: Coincident(g5,g4)
    c: Coincident(g5,g-10)
    c: Coincident(g6,g4)
    c: Coincident(g6,g-7)
    c: Coincident(g7,g6)
    c: Coincident(g7,g-6)
    c: Coincident(g8,g-3)
    c: Coincident(g8,g5)
    c: Coincident(g9,g7)
    c: Coincident(g9,g-3)
FEATURE [PartDesign::Pad] Pad075
  BaseFeature = -> Pad074
  Direction = (0,0,-1)
  Length = 10.8
  Length2 = 10
  Profile = -> Sketch103
  ReferenceAxis = -> Sketch103 [N_Axis]
  Refine = true
  Suppressed = false
  Type = 0
FEATURE [Sketcher::SketchObject] Sketch104
  ArcFitTolerance = 1e-06
  AttachmentSupport = -> [Pad075]
  ExternalGeometry = -> [Pad075]
  FullyConstrained = true
  MakeInternals = false
  MapMode = 5
  Placement = pos=(0,0,1.5) rot=(1,0,0;3.14159rad)
  sketch-geometry (6):
    g0: LineSegment StartX=0 StartY=14 StartZ=0 EndX=0 EndY=0 EndZ=0
    g1: LineSegment StartX=0 StartY=0 StartZ=0 EndX=-2 EndY=-1.40042 EndZ=0
    g2: LineSegment StartX=-2 StartY=-1.40042 StartZ=0 EndX=-2 EndY=12.9004 EndZ=0
    g3: LineSegment StartX=-2 StartY=12.9004 StartZ=0 EndX=-3.72022 EndY=14.1049 EndZ=0
    g4: LineSegment StartX=-3.72022 StartY=14.1049 StartZ=0 EndX=-1.57708 EndY=15.1043 EndZ=0
    g5: LineSegment StartX=-1.57708 StartY=15.1043 StartZ=0 EndX=0 EndY=14 EndZ=0
  constraints (12):
    c: Coincident(g0,g-7)
    c: Coincident(g0,g-1)
    c: Coincident(g1,g0)
    c: Coincident(g1,g-4)
    c: Coincident(g2,g1)
    c: Coincident(g2,g-3)
    c: Coincident(g3,g2)
    c: Coincident(g3,g-9)
    c: Coincident(g4,g3)
    c: Coincident(g4,g-8)
    c: Coincident(g5,g4)
    c: Coincident(g5,g0)
FEATURE [PartDesign::Pad] Pad076
  BaseFeature = -> Pad075
  Direction = (0,0,-1)
  Length = 2
  Length2 = 10
  Profile = -> Sketch104
  ReferenceAxis = -> Sketch104 [N_Axis]
  Refine = true
  Suppressed = false
  Type = 0
FEATURE [Sketcher::SketchObject] Sketch105
  ArcFitTolerance = 1e-06
  AttachmentSupport = -> [Pad076]
  ExternalGeometry = -> [Pad076]
  FullyConstrained = true
  MakeInternals = false
  MapMode = 5
  Placement = pos=(5.40323,-7.71662,-2.01e-14) rot=(-0.217607,0.690162,0.690162;3.57013rad)
  sketch-geometry (17):
    g0: LineSegment [constr] StartX=9.03768 StartY=12.3 StartZ=0 EndX=9.03768 EndY=1.5 EndZ=0
    g1: LineSegment StartX=11.1377 StartY=12.6 StartZ=0 EndX=9.03768 EndY=12.6 EndZ=0
    g2: LineSegment StartX=9.03768 StartY=12.6 StartZ=0 EndX=9.03768 EndY=11.025 EndZ=0
    g3: LineSegment StartX=9.03768 StartY=11.025 StartZ=0 EndX=11.1377 EndY=11.025 EndZ=0
    g4: LineSegment StartX=11.1377 StartY=11.025 StartZ=0 EndX=11.1377 EndY=12.6 EndZ=0
    g5: LineSegment StartX=11.1377 StartY=9.325 StartZ=0 EndX=9.03768 EndY=9.325 EndZ=0
    g6: LineSegment StartX=9.03768 StartY=9.325 StartZ=0 EndX=9.03768 EndY=7.75 EndZ=0
    g7: LineSegment StartX=9.03768 StartY=7.75 StartZ=0 EndX=11.1377 EndY=7.75 EndZ=0
    g8: LineSegment StartX=11.1377 StartY=7.75 StartZ=0 EndX=11.1377 EndY=9.325 EndZ=0
    g9: LineSegment StartX=11.1377 StartY=6.05 StartZ=0 EndX=9.03768 EndY=6.05 EndZ=0
    g10: LineSegment StartX=9.03768 StartY=6.05 StartZ=0 EndX=9.03768 EndY=4.475 EndZ=0
    g11: LineSegment StartX=9.03768 StartY=4.475 StartZ=0 EndX=11.1377 EndY=4.475 EndZ=0
    g12: LineSegment StartX=11.1377 StartY=4.475 StartZ=0 EndX=11.1377 EndY=6.05 EndZ=0
    g13: LineSegment StartX=11.1377 StartY=2.775 StartZ=0 EndX=9.03768 EndY=2.775 EndZ=0
    g14: LineSegment StartX=9.03768 StartY=2.775 StartZ=0 EndX=9.03768 EndY=1.2 EndZ=0
    g15: LineSegment StartX=9.03768 StartY=1.2 StartZ=0 EndX=11.1377 EndY=1.2 EndZ=0
    g16: LineSegment StartX=11.1377 StartY=1.2 StartZ=0 EndX=11.1377 EndY=2.775 EndZ=0
  constraints (51):
    c: Coincident(g0,g-4)
    c: Coincident(g0,g-5)
    c: Coincident(g1,g2)
    c: Coincident(g2,g3)
    c: Coincident(g3,g4)
    c: Coincident(g4,g1)
    c: Horizontal(g1)
    c: Horizontal(g3)
    c: Vertical(g2)
    c: Vertical(g4)
    c: PointOnObject(g1,g-3)
    c: PointOnObject(g2,g0)
    c: Coincident(g5,g6)
    c: Coincident(g6,g7)
    c: Coincident(g7,g8)
    c: Coincident(g8,g5)
    c: Horizontal(g5)
    c: Horizontal(g7)
    c: Vertical(g6)
    c: Vertical(g8)
    c: PointOnObject(g5,g-3)
    c: Coincident(g9,g10)
    c: Coincident(g10,g11)
    c: Coincident(g11,g12)
    c: Coincident(g12,g9)
    c: Horizontal(g9)
    c: Horizontal(g11)
    c: Vertical(g10)
    c: Vertical(g12)
    c: PointOnObject(g9,g-3)
    c: PointOnObject(g10,g0)
    c: Coincident(g13,g14)
    c: Coincident(g14,g15)
    c: Coincident(g15,g16)
    c: Coincident(g16,g13)
    c: Horizontal(g13)
    c: Horizontal(g15)
    c: Vertical(g14)
    c: Vertical(g16)
    c: PointOnObject(g13,g-3)
    c: PointOnObject(g14,g0)
    c: DistanceY(g1,g-3) = 1.7
    c: DistanceY(g5,g3) = 1.7
    c: DistanceY(g9,g7) = 1.7
    c: DistanceY(g13,g11) = 1.7
    c: DistanceY(g-3,g15) = 1.7
    c: DistanceY(g-3,g-3) = 14.8
    c: DistanceY(g4,g4) = 1.575
    c: DistanceY(g8,g8) = 1.575
    c: DistanceY(g12,g12) = 1.575
    c: PointOnObject(g6,g0)
FEATURE [PartDesign::Pocket] Pocket037
  BaseFeature = -> Pad076
  Direction = (0.573576,-0.819152,-2.2e-15)
  Length = 5
  Length2 = 5
  Profile = -> Sketch105
  ReferenceAxis = -> Sketch105 [N_Axis]
  Refine = true
  Suppressed = false
  Type = 0
FEATURE [Sketcher::SketchObject] Sketch106
  ArcFitTolerance = 1e-06
  AttachmentOffset = pos=(0,0,-5.65) rot=(0,0,1;0rad)
  AttachmentSupport = -> [Pocket037]
  ExternalGeometry = -> [Pocket037]
  FullyConstrained = true
  MakeInternals = false
  MapMode = 5
  Placement = pos=(3.2e-15,0,8.15) rot=(0,0,1;0rad)
  sketch-geometry (4):
    g0: LineSegment StartX=0 StartY=0 StartZ=0 EndX=4.58725 EndY=-3.21203 EndZ=0
    g1: LineSegment StartX=4.58725 StartY=-3.21203 StartZ=0 EndX=4.58725 EndY=0.287972 EndZ=0
    g2: LineSegment StartX=0 StartY=0 StartZ=0 EndX=2.04788 EndY=1.43394 EndZ=0
    g3: ArcOfCircle CenterX=2.99379 CenterY=0.143492 CenterZ=0 NormalX=0 NormalY=0 NormalZ=1 AngleXU=0 Radius=1.6 StartAngle=0.090423 EndAngle=2.20333
  constraints (12):
    c: Coincident(g0,g-1)
    c: PointOnObject(g0,g-3)
    c: Coincident(g1,g0)
    c: Vertical(g1)
    c: Coincident(g2,g0)
    c: Coincident(g3,g2)
    c: Coincident(g3,g1)
    c: Distance(g0) = 5.6
    c: Parallel(g2,g-4)
    c: DistanceY(g1,g1) = 3.5
    c: Distance(g2) = 2.5
    c: Radius(g3) = 1.6
FEATURE [PartDesign::Pad] Pad077
  BaseFeature = -> Pocket037
  Direction = (0,0,1)
  Length = 2.5
  Length2 = 10
  Profile = -> Sketch106
  ReferenceAxis = -> Sketch106 [N_Axis]
  Refine = true
  Reversed = true
  Suppressed = false
  Type = 0
FEATURE [Sketcher::SketchObject] Sketch107
  ArcFitTolerance = 1e-06
  AttachmentOffset = pos=(0,0,-0.25) rot=(0,0,1;0rad)
  AttachmentSupport = -> [Pad077]
  ExternalGeometry = -> [Pad077]
  FullyConstrained = true
  MakeInternals = false
  MapMode = 5
  Placement = pos=(0,0,7.9) rot=(0,0,1;0rad)
  sketch-geometry (7):
    g0: LineSegment StartX=-2 StartY=1.40042 StartZ=0 EndX=-14.65 EndY=23.3109 EndZ=0
    g1: LineSegment StartX=1.02951 StartY=0.720867 StartZ=0 EndX=-10.2333 EndY=25.8609 EndZ=0
    g2: LineSegment StartX=1.02951 StartY=0.720867 StartZ=0 EndX=0 EndY=3e-16 EndZ=0
    g3: LineSegment StartX=0 StartY=3e-16 StartZ=0 EndX=-2 EndY=1.40042 EndZ=0
    g4: LineSegment [constr] StartX=-2 StartY=1.40042 StartZ=0 EndX=0.165064 EndY=2.65042 EndZ=0
    g5: LineSegment [constr] StartX=-14.65 StartY=23.3109 StartZ=0 EndX=-10.2333 EndY=25.8609 EndZ=0
    g6: LineSegment StartX=-14.65 StartY=23.3109 StartZ=0 EndX=-10.2333 EndY=25.8609 EndZ=0
  constraints (18):
    c: Coincident(g0,g-3)
    c: PointOnObject(g1,g-4)
    c: Coincident(g2,g1)
    c: Coincident(g2,g-1)
    c: Coincident(g3,g2)
    c: Coincident(g3,g0)
    c: Distance(g0) = 25.3
    c: Coincident(g4,g0)
    c: PointOnObject(g4,g1)
    c: Perpendicular(g0,g4)
    c: Distance(g4) = 2.5
    c: Coincident(g5,g0)
    c: Perpendicular(g0,g5)
    c: Distance(g5) = 5.1
    c: Coincident(g1,g5)
    c: Coincident(g6,g0)
    c: Coincident(g6,g1)
    c: Angle(g0,g-5) = 2.61799
FEATURE [PartDesign::Pad] Pad078
  BaseFeature = -> Pad077
  Direction = (0,0,1)
  Length = 2
  Length2 = 10
  Profile = -> Sketch107
  ReferenceAxis = -> Sketch107 [N_Axis]
  Refine = true
  Reversed = true
  Suppressed = false
  Type = 0
FEATURE [Sketcher::SketchObject] Sketch108
  ArcFitTolerance = 1e-06
  AttachmentSupport = -> [Pad078]
  ExternalGeometry = -> [Pad078]
  FullyConstrained = false
  MakeInternals = false
  MapMode = 5
  Placement = pos=(0,0,7.9) rot=(0,0,1;0rad)
  sketch-geometry (14):
    g0: ArcOfCircle CenterX=-16.15 CenterY=25.9089 CenterZ=0 NormalX=0 NormalY=0 NormalZ=1 AngleXU=0 Radius=3 StartAngle=2.0944 EndAngle=5.23599
    g1: LineSegment [constr] StartX=-17.65 StartY=28.507 StartZ=0 EndX=-16.15 EndY=25.9089 EndZ=0
    g2: LineSegment [constr] StartX=-16.15 StartY=25.9089 StartZ=0 EndX=-14.65 EndY=23.3109 EndZ=0
    g3: LineSegment StartX=-17.65 StartY=28.507 StartZ=0 EndX=-19.6 EndY=31.8845 EndZ=0
    g4: ArcOfCircle CenterX=-18.734 CenterY=32.3845 CenterZ=0 NormalX=0 NormalY=0 NormalZ=1 AngleXU=0 Radius=1 StartAngle=0.872665 EndAngle=3.66519
    g5: LineSegment StartX=-18.0912 StartY=33.1506 StartZ=0 EndX=-15.7164 EndY=31.1579 EndZ=0
    g6: LineSegment StartX=-15.7164 StartY=31.1579 StartZ=0 EndX=-14.8504 EndY=31.6579 EndZ=0
    g7: LineSegment StartX=-14.8504 StartY=31.6579 StartZ=0 EndX=-11.4663 EndY=28.6131 EndZ=0
    g8: LineSegment StartX=-11.4663 StartY=28.6131 StartZ=0 EndX=-10.2333 EndY=25.8609 EndZ=0
    g9: LineSegment [constr] StartX=-19.6 StartY=31.8845 StartZ=0 EndX=-18.734 EndY=32.3845 EndZ=0
    g10: LineSegment [constr] StartX=-11.4663 StartY=28.6131 StartZ=0 EndX=-16.15 EndY=25.9089 EndZ=0
    g11: LineSegment [constr] StartX=-18.734 StartY=32.3845 StartZ=0 EndX=-18.0912 EndY=33.1506 EndZ=0
    g12: LineSegment [constr] StartX=-15.7164 StartY=31.1579 StartZ=0 EndX=-18.3145 EndY=29.6579 EndZ=0
    g13: LineSegment StartX=-10.2333 StartY=25.8609 StartZ=0 EndX=-14.65 EndY=23.3109 EndZ=0
  constraints (36):
    c: Coincident(g0,g-3)
    c: Radius(g0) = 3
    c: Coincident(g1,g0)
    c: Coincident(g1,g0)
    c: Coincident(g2,g0)
    c: Coincident(g2,g0)
    c: Angle(g1,g2) = 3.14159
    c: Angle(g-4,g2) = 3.14159
    c: Coincident(g3,g0)
    c: Angle(g3,g1) = 3.14159
    c: Coincident(g4,g3)
    c: Coincident(g5,g4)
    c: Coincident(g6,g5)
    c: Coincident(g7,g6)
    c: Coincident(g8,g7)
    c: Coincident(g8,g-5)
    c: Angle(g-5,g8) = 3.14159
    c: Radius(g4) = 1
    c: Distance(g0,g3) = 3.9
    c: Coincident(g9,g3)
    c: Coincident(g9,g4)
    c: Perpendicular(g3,g9)
    c: Coincident(g10,g7)
    c: Coincident(g10,g0)
    c: Perpendicular(g10,g2)
    c: Distance(g5) = 3.1
    c: Coincident(g11,g4)
    c: Coincident(g11,g4)
    c: Angle(g11,g9) = 2.79253
    c: Coincident(g12,g5)
    c: PointOnObject(g12,g3)
    c: Perpendicular(g3,g12)
    c: Distance(g12) = 3
    c: Angle(g12,g6) = 3.14159
    c: Coincident(g13,g0)
    c: Coincident(g13,g8)
FEATURE [PartDesign::Pad] Pad079
  BaseFeature = -> Pad078
  Direction = (0,0,1)
  Length = 2
  Length2 = 10
  Profile = -> Sketch108
  ReferenceAxis = -> Sketch108 [N_Axis]
  Refine = true
  Reversed = true
  Suppressed = false
  Type = 0
FEATURE [Sketcher::SketchObject] Sketch109
  ArcFitTolerance = 1e-06
  AttachmentSupport = -> [Pad079]
  ExternalGeometry = -> [Pad079]
  FullyConstrained = true
  MakeInternals = false
  MapMode = 5
  Placement = pos=(0,0,7.9) rot=(0,0,1;0rad)
  sketch-geometry (1):
    g0: Circle CenterX=-16.15 CenterY=25.9089 CenterZ=0 NormalX=0 NormalY=0 NormalZ=1 AngleXU=0 Radius=0.75
  constraints (2):
    c: Coincident(g0,g-3)
    c: Radius(g0) = 0.75
FEATURE [PartDesign::Pocket] Pocket038
  BaseFeature = -> Pad079
  Direction = (0,0,-1)
  Length = 5
  Length2 = 5
  Profile = -> Sketch109
  ReferenceAxis = -> Sketch109 [N_Axis]
  Refine = true
  Suppressed = false
  Type = 0
FEATURE [Sketcher::SketchObject] Sketch110
  ArcFitTolerance = 1e-06
  AttachmentSupport = -> [Pocket038]
  ExternalGeometry = -> [Pocket038]
  FullyConstrained = true
  MakeInternals = false
  MapMode = 5
  Placement = pos=(0,0,8.15) rot=(0,0,1;0rad)
  sketch-geometry (1):
    g0: Circle CenterX=2.99379 CenterY=0.143492 CenterZ=0 NormalX=0 NormalY=0 NormalZ=1 AngleXU=0 Radius=0.95
  constraints (2):
    c: Coincident(g0,g-3)
    c: Diameter(g0) = 1.9
FEATURE [PartDesign::Pad] Pad080
  BaseFeature = -> Pocket038
  Direction = (0,0,1)
  Length = 0.3
  Length2 = 10
  Profile = -> Sketch110
  ReferenceAxis = -> Sketch110 [N_Axis]
  Refine = true
  Suppressed = false
  Type = 0
FEATURE [Sketcher::SketchObject] Sketch111
  ArcFitTolerance = 1e-06
  AttachmentSupport = -> [Pad080]
  ExternalGeometry = -> [Pad080]
  FullyConstrained = true
  MakeInternals = false
  MapMode = 5
  Placement = pos=(0,0,5.65) rot=(1,0,0;3.14159rad)
  sketch-geometry (1):
    g0: Circle CenterX=2.99379 CenterY=-0.143492 CenterZ=0 NormalX=0 NormalY=0 NormalZ=1 AngleXU=0 Radius=0.95
  constraints (2):
    c: Coincident(g0,g-3)
    c: Diameter(g0) = 1.9
FEATURE [PartDesign::Pad] Pad081
  BaseFeature = -> Pad080
  Direction = (0,0,-1)
  Length = 0.3
  Length2 = 10
  Profile = -> Sketch111
  ReferenceAxis = -> Sketch111 [N_Axis]
  Refine = true
  Suppressed = false
  Type = 0
FEATURE [Sketcher::SketchObject] Sketch112
  ArcFitTolerance = 1e-06
  AttachmentSupport = -> [Pad081]
  ExternalGeometry = -> [Pad081]
  FullyConstrained = true
  MakeInternals = false
  MapMode = 5
  Placement = pos=(0,0,7.9) rot=(0,0,1;0rad)
  sketch-geometry (7):
    g0: LineSegment [constr] StartX=-14.65 StartY=23.3109 StartZ=0 EndX=-10.2333 EndY=25.8609 EndZ=0
    g1: LineSegment StartX=-10.2333 StartY=25.8609 StartZ=0 EndX=-7.65753 EndY=20.1115 EndZ=0
    g2: LineSegment StartX=-7.65753 StartY=20.1115 StartZ=0 EndX=-5.39731 EndY=21.4164 EndZ=0
    g3: LineSegment StartX=-10.2333 StartY=25.8609 StartZ=0 EndX=-5.61764 EndY=24.1188 EndZ=0
    g4: ArcOfCircle CenterX=-6.14731 CenterY=22.7154 CenterZ=0 NormalX=0 NormalY=0 NormalZ=1 AngleXU=0 Radius=1.5 StartAngle=5.23599 EndAngle=7.49309
    g5: GeomPoint [constr] X=-2.65399 Y=23.0003 Z=0
    g6: LineSegment [constr] StartX=-5.61764 StartY=24.1188 StartZ=0 EndX=-8.81175 EndY=22.6878 EndZ=0
  constraints (18):
    c: Coincident(g0,g-4)
    c: PointOnObject(g0,g-5)
    c: Perpendicular(g-3,g0)
    c: Coincident(g1,g0)
    c: PointOnObject(g1,g-5)
    c: Coincident(g2,g1)
    c: Coincident(g3,g0)
    c: PointOnObject(g5,g2)
    c: PointOnObject(g5,g3)
    c: Tangent(g2,g4) = -1.5708
    c: Tangent(g3,g4) = 1.5708
    c: Distance(g1) = 6.3
    c: Coincident(g6,g3)
    c: PointOnObject(g6,g1)
    c: Perpendicular(g1,g6)
    c: Distance(g6) = 3.5
    c: Radius(g4) = 1.5
    c: Perpendicular(g-3,g2)
FEATURE [PartDesign::Pad] Pad082
  BaseFeature = -> Pad081
  Direction = (0,0,1)
  Length = 2
  Length2 = 10
  Profile = -> Sketch112
  ReferenceAxis = -> Sketch112 [N_Axis]
  Refine = true
  Reversed = true
  Suppressed = false
  Type = 0
FEATURE [Sketcher::SketchObject] Sketch113
  ArcFitTolerance = 1e-06
  AttachmentSupport = -> [Pad082]
  ExternalGeometry = -> [Pad082]
  FullyConstrained = true
  MakeInternals = false
  MapMode = 5
  Placement = pos=(0,0,7.9) rot=(0,0,1;0rad)
  sketch-geometry (1):
    g0: Circle CenterX=-6.14731 CenterY=22.7154 CenterZ=0 NormalX=0 NormalY=0 NormalZ=1 AngleXU=0 Radius=1
  constraints (2):
    c: Coincident(g0,g-3)
    c: Radius(g0) = 1
FEATURE [PartDesign::Pad] Pad083
  BaseFeature = -> Pad082
  Direction = (0,0,1)
  Length = 0.3
  Length2 = 10
  Profile = -> Sketch113
  ReferenceAxis = -> Sketch113 [N_Axis]
  Refine = true
  Suppressed = false
  Type = 0
FEATURE [Sketcher::SketchObject] Sketch114
  ArcFitTolerance = 1e-06
  AttachmentSupport = -> [Pad083]
  ExternalGeometry = -> [Pad083]
  FullyConstrained = true
  MakeInternals = false
  MapMode = 5
  Placement = pos=(0,0,5.9) rot=(1,0,0;3.14159rad)
  sketch-geometry (1):
    g0: Circle CenterX=-6.14731 CenterY=-22.7154 CenterZ=0 NormalX=0 NormalY=0 NormalZ=1 AngleXU=0 Radius=1
  constraints (2):
    c: Coincident(g0,g-3)
    c: Radius(g0) = 1
FEATURE [PartDesign::Pad] Pad084
  BaseFeature = -> Pad083
  Direction = (0,0,-1)
  Length = 0.3
  Length2 = 10
  Profile = -> Sketch114
  ReferenceAxis = -> Sketch114 [N_Axis]
  Refine = true
  Suppressed = false
  Type = 0
FEATURE [Sketcher::SketchObject] Sketch115
  ArcFitTolerance = 1e-06
  AttachmentSupport = -> [Pad084]
  ExternalGeometry = -> [Pad084]
  FullyConstrained = true
  MakeInternals = false
  MapMode = 5
  Placement = pos=(0,0,7.9) rot=(0,0,1;0rad)
  sketch-geometry (6):
    g0: LineSegment [constr] StartX=-5.39731 StartY=21.4164 StartZ=0 EndX=3.62894 EndY=5.78247 EndZ=0
    g1: LineSegment [constr] StartX=3.62894 StartY=5.78247 StartZ=0 EndX=2.99379 EndY=0.143492 EndZ=0
    g2: Circle CenterX=-1.36442 CenterY=2.89955 CenterZ=0 NormalX=0 NormalY=0 NormalZ=1 AngleXU=0 Radius=1
    g3: LineSegment [constr] StartX=-1.36442 StartY=2.89955 StartZ=0 EndX=-2.49025 EndY=2.24955 EndZ=0
    g4: LineSegment [constr] StartX=-1.36442 StartY=2.89955 StartZ=0 EndX=-0.237924 EndY=3.54994 EndZ=0
    g5: LineSegment [constr] StartX=-0.237924 StartY=3.54994 StartZ=0 EndX=3.62894 EndY=5.78247 EndZ=0
  constraints (17):
    c: Coincident(g0,g-3)
    c: Perpendicular(g-4,g0)
    c: Coincident(g1,g0)
    c: Coincident(g1,g-6)
    c: Radius(g2) = 1
    c: Coincident(g3,g2)
    c: PointOnObject(g3,g-8)
    c: Coincident(g4,g2)
    c: PointOnObject(g4,g-7)
    c: Angle(g4,g3) = 3.14159
    c: Perpendicular(g-8,g3)
    c: Distance(g4,g-7) = 3.1
    c: Distance(g3,g4) = 2.60076
    c: Distance(g3,g2) = 1.3
    c: Coincident(g5,g4)
    c: Coincident(g5,g0)
    c: Perpendicular(g5,g0)
FEATURE [PartDesign::Pad] Pad085
  BaseFeature = -> Pad084
  Direction = (0,0,1)
  Length = 0.3
  Length2 = 10
  Profile = -> Sketch115
  ReferenceAxis = -> Sketch115 [N_Axis]
  Refine = true
  Suppressed = false
  Type = 0
FEATURE [Sketcher::SketchObject] Sketch116
  ArcFitTolerance = 1e-06
  AttachmentSupport = -> [Pad085]
  ExternalGeometry = -> [Pad085]
  FullyConstrained = true
  MakeInternals = false
  MapMode = 5
  Placement = pos=(0,0,5.9) rot=(1,0,0;3.14159rad)
  sketch-geometry (1):
    g0: Circle CenterX=-1.36442 CenterY=-2.89955 CenterZ=0 NormalX=0 NormalY=0 NormalZ=1 AngleXU=0 Radius=1
  constraints (2):
    c: Coincident(g0,g-3)
    c: Equal(g0,g-3)
FEATURE [PartDesign::Pad] Pad086
  BaseFeature = -> Pad085
  Direction = (0,0,-1)
  Length = 0.3
  Length2 = 10
  Profile = -> Sketch116
  ReferenceAxis = -> Sketch116 [N_Axis]
  Refine = true
  Suppressed = false
  Type = 0
FEATURE [Sketcher::SketchObject] Sketch117
  ArcFitTolerance = 1e-06
  AttachmentSupport = -> [Pad086]
  ExternalGeometry = -> [Pad086]
  FullyConstrained = true
  MakeInternals = false
  MapMode = 5
  Placement = pos=(-10.6229,18.3994,0) rot=(0.935113,0.250563,0.250563;1.63783rad)
  sketch-geometry (1):
    g0: Circle CenterX=6.03399 CenterY=6.9 CenterZ=0 NormalX=0 NormalY=0 NormalZ=1 AngleXU=0 Radius=1.3
  constraints (2):
    c: Symmetric(g-3,g-3,g0)
    c: Diameter(g0) = 2.6
FEATURE [PartDesign::Pad] Pad087
  BaseFeature = -> Pad086
  Direction = (0.5,-0.866025,2e-16)
  Length = 10
  Length2 = 10
  Profile = -> Sketch117
  ReferenceAxis = -> Sketch117 [N_Axis]
  Refine = true
  Suppressed = false
  Type = 0
FEATURE [Sketcher::SketchObject] Sketch118
  ArcFitTolerance = 1e-06
  AttachmentSupport = -> [Pad087]
  ExternalGeometry = -> [Pad087]
  FullyConstrained = true
  MakeInternals = false
  MapMode = 5
  Placement = pos=(-5.6229,9.73915,2.2e-15) rot=(0.935113,0.250563,0.250563;1.63783rad)
  sketch-geometry (4):
    g0: LineSegment StartX=4.03399 StartY=8.75 StartZ=0 EndX=4.03399 EndY=5.05 EndZ=0
    g1: LineSegment StartX=4.03399 StartY=5.05 StartZ=0 EndX=8.03399 EndY=5.05 EndZ=0
    g2: LineSegment StartX=8.03399 StartY=5.05 StartZ=0 EndX=8.03399 EndY=8.75 EndZ=0
    g3: LineSegment StartX=8.03399 StartY=8.75 StartZ=0 EndX=4.03399 EndY=8.75 EndZ=0
  constraints (12):
    c: Coincident(g0,g1)
    c: Coincident(g1,g2)
    c: Coincident(g2,g3)
    c: Coincident(g3,g0)
    c: Vertical(g0)
    c: Vertical(g2)
    c: Horizontal(g1)
    c: Horizontal(g3)
    c: DistanceX(g3,g3) = 4
    c: DistanceY(g2,g2) = 3.7
    c: DistanceY(g-3,g2) = 1.85
    c: DistanceX(g0,g-3) = 2
FEATURE [PartDesign::Pad] Pad088
  BaseFeature = -> Pad087
  Direction = (0.5,-0.866025,0)
  Length = 1
  Length2 = 10
  Profile = -> Sketch118
  ReferenceAxis = -> Sketch118 [N_Axis]
  Refine = true
  Suppressed = false
  Type = 0
FEATURE [Sketcher::SketchObject] Sketch119
  ArcFitTolerance = 1e-06
  AttachmentSupport = -> [Pad088]
  ExternalGeometry = -> [Pad088]
  FullyConstrained = true
  MakeInternals = false
  MapMode = 5
  Placement = pos=(-5.1229,8.87312,2.5e-15) rot=(0.935113,0.250563,0.250563;1.63783rad)
  sketch-geometry (1):
    g0: Circle CenterX=6.03399 CenterY=6.9 CenterZ=0 NormalX=0 NormalY=0 NormalZ=1 AngleXU=0 Radius=1.3
  constraints (2):
    c: Coincident(g0,g-3)
    c: Equal(g0,g-3)
FEATURE [PartDesign::Pad] Pad089
  BaseFeature = -> Pad088
  Direction = (0.5,-0.866025,2e-16)
  Length = 1
  Length2 = 10
  Profile = -> Sketch119
  ReferenceAxis = -> Sketch119 [N_Axis]
  Refine = true
  Suppressed = false
  Type = 0
FEATURE [Sketcher::SketchObject] Sketch120
  ArcFitTolerance = 1e-06
  AttachmentSupport = -> [Pad089]
  ExternalGeometry = -> [Pad089]
  FullyConstrained = true
  MakeInternals = false
  MapMode = 5
  Placement = pos=(1.12638,0.504623,0) rot=(0.416434,0.642878,0.642878;2.35241rad)
  sketch-geometry (1):
    g0: Circle CenterX=3.20398 CenterY=6.9 CenterZ=0 NormalX=0 NormalY=0 NormalZ=1 AngleXU=0 Radius=0.75
  constraints (5):
    c: Diameter(g0) = 1.5
    c: DistanceX(g-3,g-3) = 2
    c: DistanceY(g-4,g-3) = 2.6
    c: DistanceY(g0,g-3) = 1.3
    c: DistanceX(g-3,g0) = 1
FEATURE [PartDesign::Pad] Pad090
  BaseFeature = -> Pad089
  Direction = (0.912602,0.408848,2e-16)
  Length = 4
  Length2 = 10
  Profile = -> Sketch120
  ReferenceAxis = -> Sketch120 [N_Axis]
  Refine = true
  Suppressed = false
  Type = 0
FEATURE [Sketcher::SketchObject] Sketch121
  ArcFitTolerance = 1e-06
  AttachmentSupport = -> [Pad090]
  ExternalGeometry = -> [Pad090]
  FullyConstrained = true
  MakeInternals = false
  MapMode = 5
  Placement = pos=(0,0,8.2) rot=(0,0,1;0rad)
  sketch-geometry (3):
    g0: LineSegment [constr] StartX=0.602691 StartY=11.0241 StartZ=0 EndX=3.92521 EndY=5.26932 EndZ=0
    g1: LineSegment [constr] StartX=3.46685 StartY=5.06397 StartZ=0 EndX=3.92521 EndY=5.26932 EndZ=0
    g2: Circle CenterX=3.92521 CenterY=5.26932 CenterZ=0 NormalX=0 NormalY=0 NormalZ=1 AngleXU=0 Radius=1
  constraints (7):
    c: Symmetric(g-3,g-3,g0)
    c: Perpendicular(g0,g-3)
    c: Symmetric(g-4,g-4,g1)
    c: Coincident(g1,g0)
    c: Perpendicular(g-4,g1)
    c: Coincident(g2,g0)
    c: Radius(g2) = 1
FEATURE [PartDesign::Pad] Pad091
  BaseFeature = -> Pad090
  Direction = (0,0,1)
  Length = 2.6
  Length2 = 10
  Profile = -> Sketch121
  ReferenceAxis = -> Sketch121 [N_Axis]
  Refine = true
  Reversed = true
  Suppressed = false
  Type = 0
FEATURE [Sketcher::SketchObject] Sketch122
  ArcFitTolerance = 1e-06
  AttachmentSupport = -> [Pad091]
  ExternalGeometry = -> [Pad091]
  FullyConstrained = true
  MakeInternals = false
  MapMode = 5
  Placement = pos=(-4.6229,8.0071,-4.5e-15) rot=(0.935113,0.250563,0.250563;1.63783rad)
  sketch-geometry (1):
    g0: Circle CenterX=6.03399 CenterY=6.9 CenterZ=0 NormalX=0 NormalY=0 NormalZ=1 AngleXU=0 Radius=0.75
  constraints (2):
    c: Coincident(g0,g-3)
    c: Diameter(g0) = 1.5
FEATURE [PartDesign::Pad] Pad092
  BaseFeature = -> Pad091
  Direction = (0.5,-0.866025,0)
  Length = 7
  Length2 = 10
  Profile = -> Sketch122
  ReferenceAxis = -> Sketch122 [N_Axis]
  Refine = true
  Suppressed = false
  Type = 0
FEATURE [Sketcher::SketchObject] Sketch123
  ArcFitTolerance = 1e-06
  AttachmentOffset = pos=(0,0,-1.25) rot=(0,0,1;0rad)
  AttachmentSupport = -> [Pad092]
  ExternalGeometry = -> [Pad092]
  FullyConstrained = true
  MakeInternals = false
  MapMode = 5
  Placement = pos=(0,0,6.6) rot=(1,0,0;3.14159rad)
  sketch-geometry (5):
    g0: LineSegment [constr] StartX=2.99379 StartY=-0.143492 StartZ=0 EndX=3.92521 EndY=-5.26932 EndZ=0
    g1: LineSegment StartX=3.75746 StartY=-1.54948 StartZ=0 EndX=3.84685 EndY=-2.04143 EndZ=0
    g2: LineSegment StartX=3.84685 StartY=-2.04143 StartZ=0 EndX=2.86296 EndY=-2.22021 EndZ=0
    g3: LineSegment StartX=2.86296 StartY=-2.22021 StartZ=0 EndX=2.77357 EndY=-1.72827 EndZ=0
    g4: ArcOfCircle CenterX=2.99379 CenterY=-0.143507 CenterZ=0 NormalX=0 NormalY=0 NormalZ=1 AngleXU=0 Radius=1.59999 StartAngle=4.57431 EndAngle=5.20997
  constraints (15):
    c: Coincident(g0,g-3)
    c: Coincident(g0,g-4)
    c: PointOnObject(g1,g-5)
    c: Coincident(g2,g1)
    c: Coincident(g3,g2)
    c: PointOnObject(g3,g-5)
    c: Parallel(g1,g0)
    c: Parallel(g3,g0)
    c: Perpendicular(g2,g1)
    c: Coincident(g4,g3)
    c: Coincident(g4,g1)
    c: Distance(g2,g0) = 0.5
    c: Distance(g1,g0) = 0.5
    c: Distance(g3) = 0.5
    c: Tangent(g4,g-5)
FEATURE [PartDesign::Pad] Pad093
  BaseFeature = -> Pad092
  Direction = (0,0,-1)
  Length = 0.5
  Length2 = 10
  Profile = -> Sketch123
  ReferenceAxis = -> Sketch123 [N_Axis]
  Refine = true
  Reversed = true
  Suppressed = false
  Type = 0
FEATURE [Sketcher::SketchObject] Sketch124
  ArcFitTolerance = 1e-06
  AttachmentSupport = -> [Pad093]
  ExternalGeometry = -> [Pad093]
  FullyConstrained = true
  MakeInternals = false
  MapMode = 5
  Placement = pos=(0.482054,2.65285,0) rot=(0.063594,0.705675,0.705675;3.01457rad)
  sketch-geometry (1):
    g0: Circle CenterX=-2.9199 CenterY=6.85 CenterZ=0 NormalX=0 NormalY=0 NormalZ=1 AngleXU=0 Radius=0.75
  constraints (5):
    c: Diameter(g0) = 1.5
    c: Distance(g-3) = 1
    c: Distance(g-4) = 0.5
    c: DistanceX(g-4,g0) = 0.5
    c: DistanceY(g0,g-4) = 0.25
FEATURE [PartDesign::Pad] Pad094
  BaseFeature = -> Pad093
  Direction = (0.178784,0.983888,0)
  Length = 3
  Length2 = 10
  Profile = -> Sketch124
  ReferenceAxis = -> Sketch124 [N_Axis]
  Refine = true
  Suppressed = false
  Type = 0
FEATURE [PartDesign::Pad] Pad095
  BaseFeature = -> Pad094
  Direction = (0.178784,0.983888,0)
  Length = 2
  Length2 = 10
  Profile = -> Sketch124
  ReferenceAxis = -> Sketch124 [N_Axis]
  Refine = true
  Reversed = true
  Suppressed = false
  Type = 0
FEATURE [Sketcher::SketchObject] Sketch125
  ArcFitTolerance = 1e-06
  AttachmentOffset = pos=(0,0,-0.5) rot=(0,0,1;0rad)
  AttachmentSupport = -> [Pad095]
  ExternalGeometry = -> [Pad095]
  FullyConstrained = true
  MakeInternals = false
  MapMode = 5
  Placement = pos=(0,0,6.4) rot=(1,0,0;3.14159rad)
  sketch-geometry (4):
    g0: LineSegment StartX=-7.65753 StartY=-20.1115 StartZ=0 EndX=-4.79559 EndY=-13.7232 EndZ=0
    g1: LineSegment StartX=-4.79559 StartY=-13.7232 StartZ=0 EndX=-2.63502 EndY=-14.9707 EndZ=0
    g2: LineSegment StartX=-2.63502 StartY=-14.9707 StartZ=0 EndX=-6.11668 EndY=-21.0011 EndZ=0
    g3: LineSegment StartX=-6.11668 StartY=-21.0011 StartZ=0 EndX=-7.65753 EndY=-20.1115 EndZ=0
  constraints (10):
    c: Coincident(g0,g-4)
    c: PointOnObject(g0,g-4)
    c: Coincident(g1,g0)
    c: Coincident(g2,g1)
    c: Coincident(g2,g-3)
    c: Coincident(g3,g2)
    c: Coincident(g3,g0)
    c: Perpendicular(g3,g2)
    c: Distance(g0) = 7
    c: Parallel(g3,g1)
FEATURE [PartDesign::Pad] Pad096
  BaseFeature = -> Pad095
  Direction = (0,0,-1)
  Length = 1
  Length2 = 10
  Profile = -> Sketch125
  ReferenceAxis = -> Sketch125 [N_Axis]
  Refine = true
  Reversed = true
  Suppressed = false
  Type = 0
FEATURE [Sketcher::SketchObject] Sketch126
  ArcFitTolerance = 1e-06
  AttachmentSupport = -> [Pad096]
  ExternalGeometry = -> [Pad096]
  FullyConstrained = true
  MakeInternals = false
  MapMode = 5
  Placement = pos=(0,0,7.9) rot=(0,0,1;0rad)
  sketch-geometry (28):
    g0: LineSegment StartX=-5.56154 StartY=19.3009 StartZ=0 EndX=-6.42757 EndY=18.8009 EndZ=0
    g1: LineSegment StartX=-6.92294 StartY=18.6105 StartZ=0 EndX=-7.49696 EndY=18.4881 EndZ=0
    g2: LineSegment StartX=-9.64622 StartY=19.4441 StartZ=0 EndX=-11.6962 EndY=22.9948 EndZ=0
    g3: Circle [constr] CenterX=-16.15 CenterY=25.9089 CenterZ=0 NormalX=0 NormalY=0 NormalZ=1 AngleXU=0 Radius=3
    g4: LineSegment StartX=-12.617 StartY=24.1998 StartZ=0 EndX=-13.3213 EndY=24.9098 EndZ=0
    g5: ArcOfCircle CenterX=-7.91417 CenterY=20.4441 CenterZ=0 NormalX=0 NormalY=0 NormalZ=1 AngleXU=0 Radius=2 StartAngle=3.66519 EndAngle=4.92254
    g6: GeomPoint [constr] X=-8.91914 Y=18.1847 Z=0
    g7: ArcOfCircle CenterX=-7.27757 CenterY=20.2731 CenterZ=0 NormalX=0 NormalY=0 NormalZ=1 AngleXU=0 Radius=1.7 StartAngle=4.92254 EndAngle=5.23599
    g8: GeomPoint [constr] X=-6.66021 Y=18.6665 Z=0
    g9: ArcOfCircle CenterX=-16.8058 CenterY=20.0448 CenterZ=0 NormalX=0 NormalY=0 NormalZ=1 AngleXU=0 Radius=5.9 StartAngle=0.523599 EndAngle=0.78136
    g10: GeomPoint [constr] X=-12.0785 Y=23.657 Z=0
    g11: LineSegment [constr] StartX=-11.6962 StartY=22.9948 StartZ=0 EndX=-13.7747 EndY=21.7948 EndZ=0
    g12: LineSegment StartX=-5.56154 StartY=19.3009 StartZ=0 EndX=-5.06154 EndY=18.4348 EndZ=0
    g13: LineSegment StartX=-5.06154 StartY=18.4348 StartZ=0 EndX=-5.92757 EndY=17.9348 EndZ=0
    g14: LineSegment StartX=-6.71433 StartY=17.6325 StartZ=0 EndX=-7.28835 EndY=17.5101 EndZ=0
    g15: LineSegment StartX=-10.5122 StartY=18.9441 StartZ=0 EndX=-12.5622 EndY=22.4948 EndZ=0
    g16: LineSegment StartX=-13.327 StartY=23.4956 StartZ=0 EndX=-13.8319 EndY=24.0046 EndZ=0
    g17: ArcOfCircle CenterX=-16.15 CenterY=25.9089 CenterZ=0 NormalX=0 NormalY=0 NormalZ=1 AngleXU=0 Radius=2.99998 StartAngle=5.59546 EndAngle=5.94365
    g18: ArcOfCircle CenterX=-16.8058 CenterY=20.0448 CenterZ=0 NormalX=0 NormalY=0 NormalZ=1 AngleXU=0 Radius=4.9 StartAngle=0.523599 EndAngle=0.78136
    g19: GeomPoint [constr] X=-12.8798 Y=23.0447 Z=0
    g20: LineSegment [constr] StartX=-12.8695 StartY=24.4543 StartZ=0 EndX=-13.5795 EndY=23.7501 EndZ=0
    g21: LineSegment [constr] StartX=-11.1962 StartY=22.1287 StartZ=0 EndX=-12.0622 EndY=21.6287 EndZ=0
    g22: ArcOfCircle CenterX=-7.91417 CenterY=20.4441 CenterZ=0 NormalX=0 NormalY=0 NormalZ=1 AngleXU=0 Radius=3 StartAngle=3.66519 EndAngle=4.92254
    g23: GeomPoint [constr] X=-9.42162 Y=17.055 Z=0
    g24: ArcOfCircle CenterX=-7.27757 CenterY=20.2731 CenterZ=0 NormalX=0 NormalY=0 NormalZ=1 AngleXU=0 Radius=2.7 StartAngle=4.92254 EndAngle=5.23599
    g25: GeomPoint [constr] X=-6.29706 Y=17.7215 Z=0
    g26: LineSegment [constr] StartX=-7.28835 StartY=17.5101 StartZ=0 EndX=-7.49696 EndY=18.4881 EndZ=0
    g27: LineSegment [constr] StartX=-5.92757 StartY=17.9348 StartZ=0 EndX=-6.42757 EndY=18.8009 EndZ=0
  constraints (69):
    c: PointOnObject(g0,g-3)
    c: Coincident(g3,g-6)
    c: PointOnObject(g4,g3)
    c: PointOnObject(g6,g1)
    c: PointOnObject(g6,g2)
    c: Tangent(g1,g5) = 1.5708
    c: Tangent(g2,g5) = 1.5708
    c: PointOnObject(g8,g0)
    c: PointOnObject(g8,g1)
    c: Tangent(g0,g7) = 1.5708
    c: Tangent(g1,g7) = 1.5708
    c: PointOnObject(g10,g2)
    c: PointOnObject(g10,g4)
    c: Tangent(g2,g9) = -1.5708
    c: Tangent(g4,g9) = -1.5708
    c: Distance(g-3,g0) = 1.75
    c: Parallel(g2,g-5)
    c: PointOnObject(g11,g-5)
    c: Perpendicular(g11,g2)
    c: Distance(g11) = 2.4
    c: Distance(g11,g9) = 3.5
    c: Coincident(g12,g0)
    c: PointOnObject(g12,g-3)
    c: Coincident(g13,g12)
    c: PointOnObject(g16,g3)
    c: Coincident(g17,g16)
    c: Coincident(g17,g4)
    c: PointOnObject(g19,g15)
    c: PointOnObject(g19,g16)
    c: Tangent(g15,g18) = -1.5708
    c: Tangent(g16,g18) = -1.5708
    c: Parallel(g2,g15)
    c: Parallel(g4,g16)
    c: PointOnObject(g-6,g3)
    c: PointOnObject(g20,g4)
    c: Symmetric(g16,g16,g20)
    c: Perpendicular(g16,g20)
    c: Distance(g20) = 1
    c: PointOnObject(g21,g2)
    c: PointOnObject(g21,g15)
    c: Perpendicular(g21,g2)
    c: Distance(g21,g15) = 1
    c: PointOnObject(g23,g14)
    c: PointOnObject(g23,g15)
    c: Tangent(g14,g22) = 1.5708
    c: Tangent(g15,g22) = 1.5708
    c: PointOnObject(g25,g13)
    c: PointOnObject(g25,g14)
    c: Tangent(g13,g24) = 1.5708
    c: Tangent(g14,g24) = 1.5708
    c: Coincident(g22,g5)
    c: Parallel(g13,g0)
    c: Parallel(g14,g1)
    c: Coincident(g24,g7)
    c: Coincident(g18,g9)
    c: Coincident(g26,g14)
    c: Coincident(g26,g1)
    c: Coincident(g27,g13)
    c: Perpendicular(g27,g13)
    c: Distance(g27) = 1
    c: Perpendicular(g13,g-3)
    c: Radius(g7) = 1.7
    c: Radius(g5) = 2
    c: Coincident(g11,g2)
    c: Distance(g4,g21) = 3.5
    c: Distance(g4,g4) = 1
    c: Distance(g21,g2) = 3.1
    c: Distance(g0,g27) = 1
    c: Tangent(g17,g3)
FEATURE [PartDesign::Pad] Pad097
  BaseFeature = -> Pad096
  Direction = (0,0,1)
  Length = 0.5
  Length2 = 10
  Profile = -> Sketch126
  ReferenceAxis = -> Sketch126 [N_Axis]
  Refine = true
  Suppressed = false
  Type = 0
FEATURE [PartDesign::Pad] Pad098
  BaseFeature = -> Pad097
  Direction = (0,0,1)
  Length = 2.5
  Length2 = 10
  Profile = -> Sketch126
  ReferenceAxis = -> Sketch126 [N_Axis]
  Refine = true
  Reversed = true
  Suppressed = false
  Type = 0
FEATURE [Sketcher::SketchObject] Sketch127
  ArcFitTolerance = 1e-06
  AttachmentSupport = -> [Pad098]
  ExternalGeometry = -> [Pad098]
  FullyConstrained = true
  MakeInternals = false
  MapMode = 5
  Placement = pos=(-9.7479,16.8839,0) rot=(-0.186157,0.694747,0.694747;3.50969rad)
  sketch-geometry (3):
    g0: LineSegment StartX=-4.83399 StartY=8.4 StartZ=0 EndX=-4.33399 EndY=8.4 EndZ=0
    g1: LineSegment StartX=-4.33399 StartY=8.4 StartZ=0 EndX=-4.83399 EndY=7.9 EndZ=0
    g2: LineSegment StartX=-4.83399 StartY=7.9 StartZ=0 EndX=-4.83399 EndY=8.4 EndZ=0
  constraints (8):
    c: Coincident(g0,g-4)
    c: PointOnObject(g0,g-3)
    c: Coincident(g1,g0)
    c: PointOnObject(g1,g-4)
    c: Coincident(g2,g1)
    c: Coincident(g2,g0)
    c: DistanceX(g0,g0) = 0.5
    c: DistanceY(g2,g2) = 0.5
FEATURE [PartDesign::Pocket] Pocket039
  BaseFeature = -> Pad098
  Direction = (0.5,-0.866025,0)
  Length = 1
  Length2 = 5
  Profile = -> Sketch127
  ReferenceAxis = -> Sketch127 [N_Axis]
  Refine = true
  Suppressed = false
  Type = 0
FEATURE [Sketcher::SketchObject] Sketch128
  ArcFitTolerance = 1e-06
  AttachmentSupport = -> [Pocket039]
  ExternalGeometry = -> [Pocket039]
  FullyConstrained = true
  MakeInternals = false
  MapMode = 5
  Placement = pos=(-9.7479,16.8839,0) rot=(-0.186157,0.694747,0.694747;3.50969rad)
  sketch-geometry (3):
    g0: LineSegment StartX=-4.83399 StartY=7.9 StartZ=0 EndX=-5.33399 EndY=7.4 EndZ=0
    g1: LineSegment StartX=-4.83399 StartY=7.4 StartZ=0 EndX=-5.33399 EndY=7.4 EndZ=0
    g2: LineSegment StartX=-4.83399 StartY=7.9 StartZ=0 EndX=-4.83399 EndY=7.4 EndZ=0
  constraints (7):
    c: Coincident(g0,g-4)
    c: Coincident(g1,g-4)
    c: Horizontal(g1)
    c: Coincident(g0,g1)
    c: Angle(g0,g-3) = 3.14159
    c: Coincident(g2,g0)
    c: Coincident(g2,g1)
FEATURE [PartDesign::Pad] Pad099
  BaseFeature = -> Pocket039
  Direction = (-0.5,0.866025,0)
  Length = 1
  Length2 = 10
  Profile = -> Sketch128
  ReferenceAxis = -> Sketch128 [N_Axis]
  Refine = true
  Reversed = true
  Suppressed = false
  Type = 0
FEATURE [Sketcher::SketchObject] Sketch129
  ArcFitTolerance = 1e-06
  AttachmentSupport = -> [Pad099]
  ExternalGeometry = -> [Pad099]
  FullyConstrained = true
  MakeInternals = false
  MapMode = 5
  Placement = pos=(-9.2479,16.0178,0) rot=(0.935113,0.250563,0.250563;1.63783rad)
  sketch-geometry (3):
    g0: LineSegment StartX=4.83399 StartY=5.4 StartZ=0 EndX=4.83399 EndY=5.9 EndZ=0
    g1: LineSegment StartX=4.83399 StartY=5.9 StartZ=0 EndX=4.33399 EndY=5.4 EndZ=0
    g2: LineSegment StartX=4.33399 StartY=5.4 StartZ=0 EndX=4.83399 EndY=5.4 EndZ=0
  constraints (8):
    c: Coincident(g0,g-4)
    c: PointOnObject(g0,g-3)
    c: Coincident(g1,g0)
    c: PointOnObject(g1,g-4)
    c: Coincident(g2,g1)
    c: Coincident(g2,g0)
    c: DistanceY(g0,g0) = 0.5
    c: DistanceX(g2,g2) = 0.5
FEATURE [PartDesign::Pocket] Pocket040
  BaseFeature = -> Pad099
  Direction = (-0.5,0.866025,0)
  Length = 1
  Length2 = 5
  Profile = -> Sketch129
  ReferenceAxis = -> Sketch129 [N_Axis]
  Refine = true
  Suppressed = false
  Type = 0
FEATURE [Sketcher::SketchObject] Sketch130
  ArcFitTolerance = 1e-06
  AttachmentSupport = -> [Pocket040]
  ExternalGeometry = -> [Pocket040]
  FullyConstrained = true
  MakeInternals = false
  MapMode = 5
  Placement = pos=(-9.2479,16.0178,0) rot=(0.935113,0.250563,0.250563;1.63783rad)
  sketch-geometry (3):
    g0: LineSegment StartX=4.83399 StartY=6.4 StartZ=0 EndX=5.33399 EndY=6.4 EndZ=0
    g1: LineSegment StartX=5.33399 StartY=6.4 StartZ=0 EndX=4.83399 EndY=5.9 EndZ=0
    g2: LineSegment StartX=4.83399 StartY=6.4 StartZ=0 EndX=4.83399 EndY=5.9 EndZ=0
  constraints (7):
    c: Coincident(g0,g-4)
    c: Horizontal(g0)
    c: Coincident(g1,g0)
    c: Coincident(g1,g-4)
    c: Coincident(g2,g0)
    c: Coincident(g2,g1)
    c: Angle(g-5,g1) = 3.14159
FEATURE [PartDesign::Pad] Pad100
  BaseFeature = -> Pocket040
  Direction = (0.5,-0.866025,0)
  Length = 1
  Length2 = 10
  Profile = -> Sketch130
  ReferenceAxis = -> Sketch130 [N_Axis]
  Refine = true
  Reversed = true
  Suppressed = false
  Type = 0
FEATURE [PartDesign::Fillet] Fillet007
  Base = -> Pad100 [Edge285,Edge268]
  BaseFeature = -> Pad100
  Radius = 1
  Refine = true
  SupportTransform = false
  Suppressed = false
  UseAllEdges = false
FEATURE [Sketcher::SketchObject] Sketch131
  ArcFitTolerance = 1e-06
  AttachmentSupport = -> [Fillet007]
  ExternalGeometry = -> [Fillet007]
  FullyConstrained = true
  MakeInternals = false
  MapMode = 5
  Placement = pos=(0,0,8.4) rot=(0,0,1;0rad)
  sketch-geometry (32):
    g0: LineSegment StartX=-8.26707 StartY=18.4754 StartZ=0 EndX=-8.44352 EndY=17.4911 EndZ=0
    g1: LineSegment StartX=-8.46192 StartY=18.5205 StartZ=0 EndX=-8.7358 EndY=17.5588 EndZ=0
    g2: LineSegment StartX=-9.21128 StartY=18.9217 StartZ=0 EndX=-9.85984 EndY=18.1606 EndZ=0
    g3: LineSegment StartX=-9.35684 StartY=19.0589 StartZ=0 EndX=-10.0782 EndY=18.3663 EndZ=0
    g4: LineSegment StartX=-9.8311 StartY=19.7643 StartZ=0 EndX=-10.6971 EndY=19.2643 EndZ=0
    g5: LineSegment StartX=-9.9311 StartY=19.9375 StartZ=0 EndX=-10.7971 EndY=19.4375 EndZ=0
    g6: LineSegment StartX=-10.3561 StartY=20.6736 StartZ=0 EndX=-11.2221 EndY=20.1736 EndZ=0
    g7: LineSegment StartX=-10.4561 StartY=20.8468 StartZ=0 EndX=-11.3221 EndY=20.3468 EndZ=0
    g8: LineSegment StartX=-10.8811 StartY=21.5829 StartZ=0 EndX=-11.7471 EndY=21.0829 EndZ=0
    g9: LineSegment StartX=-10.9811 StartY=21.7561 StartZ=0 EndX=-11.8471 EndY=21.2561 EndZ=0
    g10: LineSegment StartX=-11.4061 StartY=22.4923 StartZ=0 EndX=-12.2721 EndY=21.9923 EndZ=0
    g11: LineSegment StartX=-11.5061 StartY=22.6655 StartZ=0 EndX=-12.3721 EndY=22.1655 EndZ=0
    g12: LineSegment StartX=-11.9472 StartY=23.392 StartZ=0 EndX=-12.7707 EndY=22.8247 EndZ=0
    g13: LineSegment StartX=-12.0634 StartY=23.5548 StartZ=0 EndX=-12.8672 EndY=22.9599 EndZ=0
    g14: LineSegment StartX=-12.617 StartY=24.1998 StartZ=0 EndX=-13.327 EndY=23.4956 EndZ=0
    g15: LineSegment StartX=-12.7579 StartY=24.3418 StartZ=0 EndX=-13.4678 EndY=23.6376 EndZ=0
    g16: LineSegment StartX=-12.617 StartY=24.1998 StartZ=0 EndX=-12.7579 EndY=24.3418 EndZ=0
    g17: LineSegment StartX=-13.327 StartY=23.4956 StartZ=0 EndX=-13.4678 EndY=23.6376 EndZ=0
    g18: ArcOfCircle CenterX=-16.8058 CenterY=20.0448 CenterZ=0 NormalX=0 NormalY=0 NormalZ=1 AngleXU=0 Radius=5.9 StartAngle=0.603268 EndAngle=0.637168
    g19: ArcOfCircle CenterX=-16.8058 CenterY=20.0448 CenterZ=0 NormalX=0 NormalY=0 NormalZ=1 AngleXU=0 Radius=4.9 StartAngle=0.603268 EndAngle=0.637168
    g20: LineSegment StartX=-11.4061 StartY=22.4923 StartZ=0 EndX=-11.5061 EndY=22.6655 EndZ=0
    g21: LineSegment StartX=-12.2721 StartY=21.9923 StartZ=0 EndX=-12.3721 EndY=22.1655 EndZ=0
    g22: LineSegment StartX=-10.8811 StartY=21.5829 StartZ=0 EndX=-10.9811 EndY=21.7561 EndZ=0
    g23: LineSegment StartX=-11.7471 StartY=21.0829 StartZ=0 EndX=-11.8471 EndY=21.2561 EndZ=0
    g24: LineSegment StartX=-10.3561 StartY=20.6736 StartZ=0 EndX=-10.4561 EndY=20.8468 EndZ=0
    g25: LineSegment StartX=-11.2221 StartY=20.1736 StartZ=0 EndX=-11.3221 EndY=20.3468 EndZ=0
    g26: LineSegment StartX=-9.8311 StartY=19.7643 StartZ=0 EndX=-9.9311 EndY=19.9375 EndZ=0
    g27: LineSegment StartX=-10.6971 StartY=19.2643 StartZ=0 EndX=-10.7971 EndY=19.4375 EndZ=0
    g28: ArcOfCircle CenterX=-7.91417 CenterY=20.4441 CenterZ=0 NormalX=0 NormalY=0 NormalZ=1 AngleXU=0 Radius=2 StartAngle=3.90666 EndAngle=4.0067
    g29: ArcOfCircle CenterX=-7.91417 CenterY=20.4441 CenterZ=0 NormalX=0 NormalY=0 NormalZ=1 AngleXU=0 Radius=3 StartAngle=3.90666 EndAngle=4.0067
    g30: ArcOfCircle CenterX=-7.91418 CenterY=20.444 CenterZ=0 NormalX=0 NormalY=0 NormalZ=1 AngleXU=0 Radius=1.99998 StartAngle=4.43497 EndAngle=4.53501
    g31: ArcOfCircle CenterX=-7.91417 CenterY=20.4441 CenterZ=0 NormalX=0 NormalY=0 NormalZ=1 AngleXU=0 Radius=3 StartAngle=4.43497 EndAngle=4.53501
  constraints (101):
    c: PointOnObject(g0,g-3)
    c: PointOnObject(g0,g-4)
    c: PointOnObject(g1,g-3)
    c: PointOnObject(g1,g-4)
    c: PointOnObject(g2,g-3)
    c: PointOnObject(g2,g-4)
    c: PointOnObject(g4,g-5)
    c: PointOnObject(g4,g-6)
    c: PointOnObject(g5,g-5)
    c: PointOnObject(g5,g-6)
    c: PointOnObject(g6,g-5)
    c: PointOnObject(g6,g-6)
    c: PointOnObject(g7,g-5)
    c: PointOnObject(g7,g-6)
    c: PointOnObject(g8,g-5)
    c: PointOnObject(g8,g-6)
    c: PointOnObject(g9,g-5)
    c: PointOnObject(g9,g-6)
    c: PointOnObject(g12,g-7)
    c: PointOnObject(g12,g-8)
    c: PointOnObject(g13,g-7)
    c: PointOnObject(g13,g-8)
    c: PointOnObject(g14,g-7)
    c: PointOnObject(g15,g-10)
    c: PointOnObject(g15,g-9)
    c: Perpendicular(g15,g-10)
    c: Perpendicular(g-7,g12)
    c: Perpendicular(g-7,g13)
    c: Perpendicular(g-7,g14)
    c: Perpendicular(g11,g-5)
    c: Perpendicular(g10,g-5)
    c: Perpendicular(g-3,g0)
    c: Perpendicular(g-3,g1)
    c: Perpendicular(g-3,g2)
    c: Perpendicular(g-3,g3)
    c: Perpendicular(g-5,g4)
    c: Perpendicular(g-5,g5)
    c: Perpendicular(g-5,g6)
    c: Perpendicular(g-5,g7)
    c: Perpendicular(g-5,g8)
    c: Perpendicular(g-5,g9)
    c: PointOnObject(g10,g-6)
    c: PointOnObject(g10,g-5)
    c: PointOnObject(g3,g-3)
    c: PointOnObject(g3,g-4)
    c: Distance(g15,g14) = 0.2
    c: Distance(g13,g12) = 0.2
    c: Distance(g11,g10) = 0.2
    c: Coincident(g14,g-9)
    c: Coincident(g16,g14)
    c: Coincident(g16,g15)
    c: Coincident(g17,g14)
    c: Coincident(g17,g15)
    c: Distance(g9,g8) = 0.2
    c: Distance(g7,g6) = 0.2
    c: Distance(g5,g4) = 0.2
    c: Distance(g0,g1) = 0.2
    c: Distance(g2,g3) = 0.2
    c: Coincident(g18,g13)
    c: Coincident(g18,g12)
    c: Tangent(g18,g-7)
    c: Coincident(g19,g13)
    c: Coincident(g19,g12)
    c: Tangent(g19,g-8)
    c: Coincident(g20,g10)
    c: Coincident(g20,g11)
    c: Coincident(g21,g10)
    c: Coincident(g21,g11)
    c: PointOnObject(g11,g-6)
    c: Distance(g12,g11) = 0.85
    c: Distance(g9,g10) = 0.85
    c: Distance(g7,g8) = 0.85
    c: Distance(g5,g6) = 0.85
    c: Distance(g3,g4) = 0.85
    c: Distance(g1,g2) = 0.85
    c: Distance(g14,g13) = 0.85
    c: Coincident(g22,g8)
    c: Coincident(g22,g9)
    c: Coincident(g23,g8)
    c: Coincident(g23,g9)
    c: Coincident(g24,g6)
    c: Coincident(g24,g7)
    c: Coincident(g25,g6)
    c: Coincident(g25,g7)
    c: Coincident(g26,g4)
    c: Coincident(g26,g5)
    c: Coincident(g27,g4)
    c: Coincident(g27,g5)
    c: Coincident(g28,g2)
    c: Coincident(g28,g3)
    c: Tangent(g28,g-3)
    c: Coincident(g29,g2)
    c: Coincident(g29,g3)
    c: Tangent(g29,g-4)
    c: Coincident(g30,g0)
    c: Coincident(g30,g1)
    c: Tangent(g30,g-3)
    c: Coincident(g31,g0)
    c: Coincident(g31,g1)
    c: Tangent(g31,g-4)
    c: PointOnObject(g11,g-5)
FEATURE [PartDesign::Pocket] Pocket041
  BaseFeature = -> Fillet007
  Direction = (0,0,-1)
  Length = 0.4
  Length2 = 5
  Profile = -> Sketch131
  ReferenceAxis = -> Sketch131 [N_Axis]
  Refine = true
  Suppressed = false
  Type = 0
FEATURE [PartDesign::Fillet] Fillet008
  Base = -> Pocket041 [Edge288,Edge293,Edge297,Edge299,Vertex183,Edge258,Edge281,Edge277,Edge283,Edge262,Edge266,Edge270,Edge274,Edge255,Edge251,Edge212,Vertex147,Edge208,Edge206,Edge187,Edge209,Edge210,Edge122,Edge117,Edge116,Edge123,Edge321,Edge325,Edge315,Edge311,Edge307,Edge303,Edge389,Edge392,Edge393,Edge396,Edge397,Edge400,Edge401,Edge387,+9 more]
  BaseFeature = -> Pocket041
  Radius = 0.25
  Refine = true
  SupportTransform = false
  Suppressed = false
  UseAllEdges = false
FEATURE [Sketcher::SketchObject] Sketch132
  ArcFitTolerance = 1e-06
  AttachmentSupport = -> [Fillet008]
  ExternalGeometry = -> [Fillet008]
  FullyConstrained = true
  MakeInternals = false
  MapMode = 5
  Placement = pos=(0,0,5.4) rot=(1,0,0;3.14159rad)
  sketch-geometry (32):
    g0: LineSegment StartX=-13.4678 StartY=-23.6376 StartZ=0 EndX=-12.7579 EndY=-24.3418 EndZ=0
    g1: LineSegment StartX=-13.327 StartY=-23.4956 StartZ=0 EndX=-12.617 EndY=-24.1998 EndZ=0
    g2: LineSegment StartX=-12.8672 StartY=-22.9599 StartZ=0 EndX=-12.0634 EndY=-23.5548 EndZ=0
    g3: LineSegment StartX=-11.9472 StartY=-23.392 StartZ=0 EndX=-12.7707 EndY=-22.8247 EndZ=0
    g4: LineSegment StartX=-12.3721 StartY=-22.1655 StartZ=0 EndX=-11.5061 EndY=-22.6655 EndZ=0
    g5: LineSegment StartX=-11.4061 StartY=-22.4923 StartZ=0 EndX=-12.2721 EndY=-21.9923 EndZ=0
    g6: LineSegment StartX=-11.8471 StartY=-21.2561 StartZ=0 EndX=-10.9811 EndY=-21.7561 EndZ=0
    g7: LineSegment StartX=-10.8811 StartY=-21.5829 StartZ=0 EndX=-11.7471 EndY=-21.0829 EndZ=0
    g8: LineSegment StartX=-11.3221 StartY=-20.3468 StartZ=0 EndX=-10.4561 EndY=-20.8468 EndZ=0
    g9: LineSegment StartX=-10.3561 StartY=-20.6736 StartZ=0 EndX=-11.2221 EndY=-20.1736 EndZ=0
    g10: LineSegment StartX=-10.7971 StartY=-19.4375 StartZ=0 EndX=-9.9311 EndY=-19.9375 EndZ=0
    g11: LineSegment StartX=-9.8311 StartY=-19.7643 StartZ=0 EndX=-10.6971 EndY=-19.2643 EndZ=0
    g12: LineSegment StartX=-10.0782 StartY=-18.3663 StartZ=0 EndX=-9.35684 EndY=-19.0589 EndZ=0
    g13: LineSegment StartX=-9.21128 StartY=-18.9217 StartZ=0 EndX=-9.85984 EndY=-18.1606 EndZ=0
    g14: LineSegment StartX=-8.7358 StartY=-17.5588 StartZ=0 EndX=-8.46192 EndY=-18.5205 EndZ=0
    g15: LineSegment StartX=-8.26707 StartY=-18.4754 StartZ=0 EndX=-8.44352 EndY=-17.4911 EndZ=0
    g16: ArcOfCircle CenterX=-7.91416 CenterY=-20.4441 CenterZ=0 NormalX=0 NormalY=0 NormalZ=1 AngleXU=0 Radius=3.00003 StartAngle=1.74818 EndAngle=1.84822
    g17: ArcOfCircle CenterX=-7.91418 CenterY=-20.444 CenterZ=0 NormalX=0 NormalY=0 NormalZ=1 AngleXU=0 Radius=1.99998 StartAngle=1.74817 EndAngle=1.84822
    g18: ArcOfCircle CenterX=-7.91417 CenterY=-20.4441 CenterZ=0 NormalX=0 NormalY=0 NormalZ=1 AngleXU=0 Radius=2 StartAngle=2.27648 EndAngle=2.37652
    g19: ArcOfCircle CenterX=-7.91417 CenterY=-20.4441 CenterZ=0 NormalX=0 NormalY=0 NormalZ=1 AngleXU=0 Radius=3 StartAngle=2.27648 EndAngle=2.37652
    g20: LineSegment StartX=-10.6971 StartY=-19.2643 StartZ=0 EndX=-10.7971 EndY=-19.4375 EndZ=0
    g21: LineSegment StartX=-9.8311 StartY=-19.7643 StartZ=0 EndX=-9.9311 EndY=-19.9375 EndZ=0
    g22: LineSegment StartX=-10.3561 StartY=-20.6736 StartZ=0 EndX=-10.4561 EndY=-20.8468 EndZ=0
    g23: LineSegment StartX=-11.2221 StartY=-20.1736 StartZ=0 EndX=-11.3221 EndY=-20.3468 EndZ=0
    g24: LineSegment StartX=-10.8811 StartY=-21.5829 StartZ=0 EndX=-10.9811 EndY=-21.7561 EndZ=0
    g25: LineSegment StartX=-11.7471 StartY=-21.0829 StartZ=0 EndX=-11.8471 EndY=-21.2561 EndZ=0
    g26: LineSegment StartX=-11.4061 StartY=-22.4923 StartZ=0 EndX=-11.5061 EndY=-22.6655 EndZ=0
    g27: LineSegment StartX=-12.2721 StartY=-21.9923 StartZ=0 EndX=-12.3721 EndY=-22.1655 EndZ=0
    g28: LineSegment StartX=-13.327 StartY=-23.4956 StartZ=0 EndX=-13.4678 EndY=-23.6376 EndZ=0
    g29: LineSegment StartX=-12.617 StartY=-24.1998 StartZ=0 EndX=-12.7579 EndY=-24.3418 EndZ=0
    g30: ArcOfCircle CenterX=-16.8058 CenterY=-20.0448 CenterZ=0 NormalX=0 NormalY=0 NormalZ=1 AngleXU=0 Radius=5.9 StartAngle=5.64602 EndAngle=5.67992
    g31: ArcOfCircle CenterX=-16.8058 CenterY=-20.0448 CenterZ=0 NormalX=0 NormalY=0 NormalZ=1 AngleXU=0 Radius=4.9 StartAngle=5.64602 EndAngle=5.67992
  constraints (70):
    c: Coincident(g0,g-26)
    c: Coincident(g0,g-25)
    c: Coincident(g1,g-27)
    c: Coincident(g1,g-27)
    c: Coincident(g2,g-34)
    c: Coincident(g2,g-34)
    c: Coincident(g3,g-29)
    c: Coincident(g3,g-30)
    c: Coincident(g4,g-6)
    c: Coincident(g4,g-6)
    c: Coincident(g5,g-5)
    c: Coincident(g5,g-4)
    c: Coincident(g6,g-8)
    c: Coincident(g6,g-9)
    c: Coincident(g7,g-10)
    c: Coincident(g7,g-10)
    c: Coincident(g8,g-33)
    c: Coincident(g8,g-33)
    c: Coincident(g9,g-12)
    c: Coincident(g9,g-13)
    c: Coincident(g10,g-32)
    c: Coincident(g10,g-32)
    c: Coincident(g11,g-15)
    c: Coincident(g11,g-16)
    c: Coincident(g12,g-31)
    c: Coincident(g12,g-31)
    c: Coincident(g13,g-18)
    c: Coincident(g13,g-19)
    c: Coincident(g14,g-23)
    c: Coincident(g14,g-23)
    c: Coincident(g15,g-21)
    c: Coincident(g15,g-22)
    c: Coincident(g16,g15)
    c: Coincident(g16,g14)
    c: Tangent(g16,g-22)
    c: Coincident(g17,g14)
    c: Coincident(g17,g15)
    c: Tangent(g17,g-20)
    c: Coincident(g18,g13)
    c: Coincident(g18,g12)
    c: Tangent(g18,g-17)
    c: Coincident(g19,g13)
    c: Coincident(g19,g12)
    c: Tangent(g19,g-19)
    c: Coincident(g20,g11)
    c: Coincident(g20,g10)
    c: Coincident(g21,g11)
    c: Coincident(g21,g10)
    c: Coincident(g22,g9)
    c: Coincident(g22,g8)
    c: Coincident(g23,g9)
    c: Coincident(g23,g8)
    c: Coincident(g24,g7)
    c: Coincident(g24,g6)
    c: Coincident(g25,g7)
    c: Coincident(g25,g6)
    c: Coincident(g26,g5)
    c: Coincident(g26,g4)
    c: Coincident(g27,g5)
    c: Coincident(g27,g4)
    c: Coincident(g28,g1)
    c: Coincident(g28,g0)
    c: Coincident(g29,g1)
    c: Coincident(g29,g0)
    c: Coincident(g30,g3)
    c: Coincident(g30,g2)
    c: Tangent(g30,g-28)
    c: Coincident(g31,g3)
    c: Coincident(g31,g2)
    c: Tangent(g31,g-30)
FEATURE [PartDesign::Pocket] Pocket042
  BaseFeature = -> Fillet008
  Direction = (0,0,1)
  Length = 0.4
  Length2 = 5
  Profile = -> Sketch132
  ReferenceAxis = -> Sketch132 [N_Axis]
  Refine = true
  Suppressed = false
  Type = 0
FEATURE [PartDesign::Fillet] Fillet009
  Base = -> Pocket042 [Edge328,Edge322,Edge326,Edge303,Edge307,Edge311,Edge315,Edge319,Edge300,Edge296,Edge162,Edge161,Edge159,Edge56,Edge57,Edge59,Edge63,Edge69,Edge70,Edge166,Edge165,Edge164,Edge365,Edge369,Edge360,Edge356,Edge352,Edge348,Edge344,Edge342,Edge338,Edge333,Edge538,Edge533,Edge535,Edge517,Edge518,Edge521,Edge522,Edge525,+9 more]
  BaseFeature = -> Pocket042
  Radius = 0.25
  Refine = true
  SupportTransform = false
  Suppressed = false
  UseAllEdges = false
FEATURE [PartDesign::Body] Body004  label="Upper_Scoop"
  AllowCompound = false
  Group = -> [Sketch099,Pad071,Sketch100,Pocket036,Sketch101,Pad072,Sketch102,Pad073,Pad074,Sketch103,Pad075,Sketch104,Pad076,Sketch105,Pocket037,Sketch106,Pad077,Sketch107,Pad078,Sketch108,Pad079,Sketch109,Pocket038,Sketch110,Pad080,Sketch111,Pad081,Sketch112,Pad082,Sketch113,Pad083,Sketch114,Pad084,Sketch115,Pad085,Sketch116,Pad086,Sketch117,Pad087,Sketch118,Pad088,Sketch119,Pad089,Sketch120,Pad090,Sketch121,+28 more]
  Origin = -> Origin004
  Placement = pos=(96.4151,-9.45,10.8146) rot=(0.981945,-0.132962,0.134557;1.5851rad)
  Tip = -> Fillet009
FEATURE [PartDesign::Pad] Pad101
  BaseFeature = -> Pocket016
  Direction = (-1,0,0)
  Length = 0.25
  Length2 = 10
  Profile = -> Pocket016 [Face71]
  Refine = true
  Suppressed = false
  Type = 0
FEATURE [PartDesign::Body] Body  label="Rear_Torso"
  AllowCompound = false
  Group = -> [Sketch,Pad,Sketch001,Pad001,Sketch002,Pad002,Sketch003,Pad003,Sketch004,Pad004,Sketch005,Pad005,Sketch006,Pad006,Sketch007,Pad007,Fillet,Sketch008,Pad008,Sketch009,Pad009,Sketch010,Pocket,Sketch011,Pad010,Sketch012,Pad011,Sketch013,Pad012,Sketch014,Pad013,Sketch015,Pocket001,Sketch016,Pad014,Sketch017,Pad015,Sketch018,Pad016,Sketch019,Pad017,Sketch020,Pad018,Sketch021,Pad019,Sketch022,Pocket002,+48 more]
  Origin = -> Origin
  Tip = -> Pad101
FEATURE [PartDesign::SubShapeBinder] Binder002
  BindCopyOnChange = 0
  BindMode = 2
  ClaimChildren = false
  Context = -> Body005 [Binder002.]
  Fuse = false
  MakeFace = true
  OffsetFill = false
  OffsetIntersection = false
  OffsetJoinType = 0
  OffsetOpenResult = false
  PartialLoad = false
  Refine = true
  Relative = true
  _Version = 2
FEATURE [Sketcher::SketchObject] Sketch133
  ArcFitTolerance = 1e-06
  AttachmentSupport = -> [Binder002]
  ExternalGeometry = -> [Binder002]
  FullyConstrained = true
  MakeInternals = false
  MapMode = 5
  Placement = pos=(0,0,-10.2) rot=(1,0,0;3.14159rad)
  sketch-geometry (4):
    g0: LineSegment StartX=50.6 StartY=6 StartZ=0 EndX=20.6 EndY=6 EndZ=0
    g1: LineSegment StartX=50.6 StartY=26 StartZ=0 EndX=20.6 EndY=26 EndZ=0
    g2: ArcOfCircle CenterX=20.6 CenterY=16 CenterZ=0 NormalX=0 NormalY=0 NormalZ=1 AngleXU=0 Radius=10 StartAngle=1.57079 EndAngle=4.71239
    g3: LineSegment StartX=50.6 StartY=26 StartZ=0 EndX=50.6 EndY=6 EndZ=0
  constraints (14):
    c: Horizontal(g0)
    c: Horizontal(g1)
    c: Coincident(g2,g0)
    c: Coincident(g2,g1)
    c: DistanceX(g1,g0) = 0
    c: PointOnObject(g-19,g1)
    c: PointOnObject(g-13,g0)
    c: DistanceY(g-13,g-19) = 20
    c: Diameter(g2) = 20
    c: DistanceX(g0,g0) = 30
    c: DistanceX(g1,g1) = 30
    c: Coincident(g3,g1)
    c: Coincident(g3,g0)
    c: DistanceX(g-3,g2) = 0
FEATURE [PartDesign::Pad] Pad102
  Direction = (0,0,-1)
  Length = 3
  Length2 = 10
  Profile = -> Sketch133
  ReferenceAxis = -> Sketch133 [N_Axis]
  Refine = true
  Suppressed = false
  Type = 0
FEATURE [Sketcher::SketchObject] Sketch134
  ArcFitTolerance = 1e-06
  AttachmentSupport = -> [Pad102]
  ExternalGeometry = -> [Pad102]
  FullyConstrained = true
  MakeInternals = false
  MapMode = 5
  Placement = pos=(0,0,-13.2) rot=(1,0,0;3.14159rad)
  sketch-geometry (3):
    g0: Circle CenterX=20.6 CenterY=16.25 CenterZ=0 NormalX=0 NormalY=0 NormalZ=1 AngleXU=0 Radius=3.5
    g1: LineSegment [constr] StartX=20.6 StartY=26 StartZ=0 EndX=20.6 EndY=16.25 EndZ=0
    g2: LineSegment [constr] StartX=20.6 StartY=16.25 StartZ=0 EndX=20.6 EndY=6 EndZ=0
  constraints (8):
    c: Diameter(g0) = 7
    c: Coincident(g1,g-3)
    c: Coincident(g1,g0)
    c: Coincident(g2,g0)
    c: Coincident(g2,g-4)
    c: Vertical(g1)
    c: DistanceY(g0,g1) = 9.75
    c: DistanceY(g2,g1) = 20
FEATURE [PartDesign::Pocket] Pocket043
  BaseFeature = -> Pad102
  Direction = (0,0,1)
  Length = 5
  Length2 = 5
  Profile = -> Sketch134
  ReferenceAxis = -> Sketch134 [N_Axis]
  Refine = true
  Suppressed = false
  Type = 0
FEATURE [Sketcher::SketchObject] Sketch135
  ArcFitTolerance = 1e-06
  AttachmentSupport = -> [Pocket043]
  ExternalGeometry = -> [Pocket043]
  FullyConstrained = true
  MakeInternals = false
  MapMode = 5
  Placement = pos=(0,0,-10.2) rot=(0,0,1;0rad)
  sketch-geometry (2):
    g0: Circle CenterX=20.6 CenterY=-16.25 CenterZ=0 NormalX=0 NormalY=0 NormalZ=1 AngleXU=0 Radius=5
    g1: Circle CenterX=20.6 CenterY=-16.25 CenterZ=0 NormalX=0 NormalY=0 NormalZ=1 AngleXU=0 Radius=3.49999
  constraints (4):
    c: Coincident(g0,g-3)
    c: Diameter(g0) = 10
    c: Coincident(g1,g0)
    c: Tangent(g1,g-3)
FEATURE [PartDesign::Pad] Pad103
  BaseFeature = -> Pocket043
  Direction = (0,0,1)
  Length = 7.65
  Length2 = 10
  Profile = -> Sketch135
  ReferenceAxis = -> Sketch135 [N_Axis]
  Refine = true
  Suppressed = false
  Type = 0
FEATURE [Sketcher::SketchObject] Sketch136
  ArcFitTolerance = 1e-06
  AttachmentSupport = -> [Pad103]
  ExternalGeometry = -> [Pad103]
  FullyConstrained = true
  MakeInternals = false
  MapMode = 5
  Placement = pos=(0,0,-13.2) rot=(1,0,0;3.14159rad)
  sketch-geometry (1):
    g0: Circle CenterX=20.6 CenterY=16.25 CenterZ=0 NormalX=0 NormalY=0 NormalZ=1 AngleXU=0 Radius=3.55
  constraints (3):
    c: Coincident(g0,g-3)
    c: Radius(g-3) = 3.5
    c: Radius(g0) = 3.55
FEATURE [PartDesign::Pocket] Pocket044
  BaseFeature = -> Pad103
  Direction = (0,0,1)
  Length = 12
  Length2 = 5
  Profile = -> Sketch136
  ReferenceAxis = -> Sketch136 [N_Axis]
  Refine = true
  Suppressed = false
  Type = 0
FEATURE [Sketcher::SketchObject] Sketch137
  ArcFitTolerance = 1e-06
  AttachmentOffset = pos=(0,0,-6.4) rot=(0,0,1;0rad)
  AttachmentSupport = -> [Pocket044]
  ExternalGeometry = -> [Pocket044]
  FullyConstrained = true
  MakeInternals = false
  MapMode = 5
  Placement = pos=(0,0,-6.8) rot=(1,0,0;3.14159rad)
  sketch-geometry (2):
    g0: Circle CenterX=20.6 CenterY=16.25 CenterZ=0 NormalX=0 NormalY=0 NormalZ=1 AngleXU=0 Radius=3.55
    g1: Circle CenterX=20.6 CenterY=16.25 CenterZ=0 NormalX=0 NormalY=0 NormalZ=1 AngleXU=0 Radius=2.3
  constraints (4):
    c: Coincident(g0,g-3)
    c: Equal(g0,g-3)
    c: Coincident(g1,g0)
    c: Diameter(g1) = 4.6
FEATURE [PartDesign::Pad] Pad104
  BaseFeature = -> Pocket044
  Direction = (0,0,-1)
  Length = 2
  Length2 = 10
  Profile = -> Sketch137
  ReferenceAxis = -> Sketch137 [N_Axis]
  Refine = true
  Reversed = true
  Suppressed = false
  Type = 0
FEATURE [Sketcher::SketchObject] Sketch138
  ArcFitTolerance = 1e-06
  AttachmentSupport = -> [Pad104]
  ExternalGeometry = -> [Pad104]
  FullyConstrained = true
  MakeInternals = false
  MapMode = 5
  Placement = pos=(0,0,-4.8) rot=(0,0,1;0rad)
  sketch-geometry (16):
    g0: LineSegment StartX=20.1 StartY=-12.7354 StartZ=0 EndX=20.1 EndY=-14.005 EndZ=0
    g1: LineSegment StartX=21.1 StartY=-12.7354 StartZ=0 EndX=21.1 EndY=-14.005 EndZ=0
    g2: LineSegment StartX=22.845 StartY=-15.75 StartZ=0 EndX=24.1147 EndY=-15.75 EndZ=0
    g3: LineSegment StartX=22.845 StartY=-16.75 StartZ=0 EndX=24.1147 EndY=-16.75 EndZ=0
    g4: LineSegment StartX=18.355 StartY=-15.75 StartZ=0 EndX=17.0854 EndY=-15.75 EndZ=0
    g5: LineSegment StartX=18.355 StartY=-16.75 StartZ=0 EndX=17.0854 EndY=-16.75 EndZ=0
    g6: LineSegment StartX=20.1 StartY=-18.495 StartZ=0 EndX=20.1 EndY=-19.7646 EndZ=0
    g7: LineSegment StartX=21.1 StartY=-18.495 StartZ=0 EndX=21.1 EndY=-19.7646 EndZ=0
    g8: ArcOfCircle CenterX=20.6 CenterY=-16.25 CenterZ=0 NormalX=0 NormalY=0 NormalZ=1 AngleXU=0 Radius=3.55 StartAngle=3.00028 EndAngle=3.28291
    g9: ArcOfCircle CenterX=20.6 CenterY=-16.25 CenterZ=0 NormalX=0 NormalY=0 NormalZ=1 AngleXU=0 Radius=2.3 StartAngle=2.92245 EndAngle=3.36073
    g10: ArcOfCircle CenterX=20.6 CenterY=-16.25 CenterZ=0 NormalX=0 NormalY=0 NormalZ=1 AngleXU=0 Radius=3.55 StartAngle=1.42948 EndAngle=1.71211
    g11: ArcOfCircle CenterX=20.6 CenterY=-16.25 CenterZ=0 NormalX=0 NormalY=0 NormalZ=1 AngleXU=0 Radius=2.3 StartAngle=1.35166 EndAngle=1.78994
    g12: ArcOfCircle CenterX=20.6 CenterY=-16.25 CenterZ=0 NormalX=0 NormalY=0 NormalZ=1 AngleXU=0 Radius=2.3 StartAngle=6.06404 EndAngle=6.50233
    g13: ArcOfCircle CenterX=20.6 CenterY=-16.25 CenterZ=0 NormalX=0 NormalY=0 NormalZ=1 AngleXU=0 Radius=3.55 StartAngle=6.14187 EndAngle=6.4245
    g14: ArcOfCircle CenterX=20.6 CenterY=-16.25 CenterZ=0 NormalX=0 NormalY=0 NormalZ=1 AngleXU=0 Radius=2.3 StartAngle=4.49325 EndAngle=4.93153
    g15: ArcOfCircle CenterX=20.6 CenterY=-16.25 CenterZ=0 NormalX=0 NormalY=0 NormalZ=1 AngleXU=0 Radius=3.55 StartAngle=4.57107 EndAngle=4.8537
  constraints (56):
    c: PointOnObject(g0,g-4)
    c: PointOnObject(g0,g-3)
    c: Vertical(g0)
    c: PointOnObject(g1,g-4)
    c: PointOnObject(g1,g-3)
    c: Vertical(g1)
    c: PointOnObject(g2,g-3)
    c: PointOnObject(g2,g-4)
    c: Horizontal(g2)
    c: PointOnObject(g3,g-3)
    c: PointOnObject(g3,g-4)
    c: Horizontal(g3)
    c: PointOnObject(g4,g-3)
    c: PointOnObject(g4,g-4)
    c: Horizontal(g4)
    c: PointOnObject(g5,g-3)
    c: PointOnObject(g5,g-4)
    c: Horizontal(g5)
    c: PointOnObject(g6,g-3)
    c: PointOnObject(g6,g-4)
    c: Vertical(g6)
    c: PointOnObject(g7,g-3)
    c: PointOnObject(g7,g-4)
    c: Vertical(g7)
    c: DistanceY(g-4,g4) = 0.5
    c: DistanceY(g5,g-4) = 0.5
    c: DistanceY(g-4,g2) = 0.5
    c: DistanceY(g3,g-4) = 0.5
    c: DistanceX(g0,g-4) = 0.5
    c: DistanceX(g6,g-4) = 0.5
    c: DistanceX(g-4,g7) = 0.5
    c: DistanceX(g-4,g1) = 0.5
    c: Coincident(g8,g4)
    c: Coincident(g8,g5)
    c: Tangent(g8,g-4)
    c: Coincident(g9,g5)
    c: Coincident(g9,g4)
    c: Tangent(g9,g-3)
    c: Coincident(g10,g0)
    c: Coincident(g10,g1)
    c: Tangent(g10,g-4)
    c: Coincident(g11,g0)
    c: Coincident(g11,g1)
    c: Tangent(g11,g-3)
    c: Coincident(g12,g2)
    c: Coincident(g12,g3)
    c: Tangent(g12,g-3)
    c: Coincident(g13,g2)
    c: Coincident(g13,g3)
    c: Tangent(g13,g-4)
    c: Coincident(g14,g6)
    c: Coincident(g14,g7)
    c: Tangent(g14,g-3)
    c: Coincident(g15,g6)
    c: Coincident(g15,g7)
    c: Tangent(g15,g-4)
FEATURE [PartDesign::Pad] Pad105
  BaseFeature = -> Pad104
  Direction = (0,0,1)
  Length = 1.4
  Length2 = 10
  Profile = -> Sketch138
  ReferenceAxis = -> Sketch138 [N_Axis]
  Refine = true
  Suppressed = false
  Type = 0
FEATURE [PartDesign::Chamfer] Chamfer002
  Angle = 45
  Base = -> Pad105 [Edge59,Edge61,Edge67,Edge70,Edge43,Edge45,Edge51,Edge52]
  BaseFeature = -> Pad105
  ChamferType = 0
  FlipDirection = false
  Refine = true
  Size = 0.4
  Size2 = 1
  SupportTransform = false
  Suppressed = false
  UseAllEdges = false
FEATURE [Sketcher::SketchObject] Sketch139
  ArcFitTolerance = 1e-06
  AttachmentSupport = -> [Chamfer002]
  ExternalGeometry = -> [Chamfer002]
  FullyConstrained = true
  MakeInternals = false
  MapMode = 5
  Placement = pos=(0,0,-3.4) rot=(0,0,1;0rad)
  sketch-geometry (1):
    g0: Circle CenterX=20.6 CenterY=-16.25 CenterZ=0 NormalX=0 NormalY=0 NormalZ=1 AngleXU=0 Radius=3.55
  constraints (2):
    c: Coincident(g0,g-3)
    c: Equal(g0,g-3)
FEATURE [PartDesign::Pocket] Pocket045
  BaseFeature = -> Chamfer002
  Direction = (0,0,-1)
  Length = 0.1
  Length2 = 5
  Profile = -> Sketch139
  ReferenceAxis = -> Sketch139 [N_Axis]
  Refine = true
  Suppressed = false
  Type = 0
FEATURE [Sketcher::SketchObject] Sketch140
  ArcFitTolerance = 1e-06
  AttachmentSupport = -> [Pocket045]
  ExternalGeometry = -> [Pocket045]
  FullyConstrained = true
  MakeInternals = false
  MapMode = 5
  Placement = pos=(0,0,-13.2) rot=(1,0,0;3.14159rad)
  sketch-geometry (4):
    g0: LineSegment StartX=50.6 StartY=21.9 StartZ=0 EndX=50.6 EndY=10.1 EndZ=0
    g1: LineSegment StartX=50.6 StartY=10.1 StartZ=0 EndX=56.6 EndY=10.1 EndZ=0
    g2: LineSegment StartX=56.6 StartY=10.1 StartZ=0 EndX=56.6 EndY=21.9 EndZ=0
    g3: LineSegment StartX=56.6 StartY=21.9 StartZ=0 EndX=50.6 EndY=21.9 EndZ=0
  constraints (13):
    c: Coincident(g0,g1)
    c: Coincident(g1,g2)
    c: Coincident(g2,g3)
    c: Coincident(g3,g0)
    c: Vertical(g0)
    c: Vertical(g2)
    c: Horizontal(g1)
    c: Horizontal(g3)
    c: PointOnObject(g0,g-3)
    c: DistanceY(g2,g2) = 11.8
    c: DistanceY(g-3,g-3) = 20
    c: DistanceY(g0,g-3) = 4.1
    c: DistanceX(g3,g3) = 6
FEATURE [PartDesign::Pad] Pad106
  BaseFeature = -> Pocket045
  Direction = (0,0,-1)
  Length = 3
  Length2 = 10
  Profile = -> Sketch140
  ReferenceAxis = -> Sketch140 [N_Axis]
  Refine = true
  Reversed = true
  Suppressed = false
  Type = 0
FEATURE [Sketcher::SketchObject] Sketch141
  ArcFitTolerance = 1e-06
  AttachmentSupport = -> [Pad106]
  ExternalGeometry = -> [Pad106]
  FullyConstrained = true
  MakeInternals = false
  MapMode = 5
  Placement = pos=(0,0,-13.2) rot=(1,0,0;3.14159rad)
  sketch-geometry (4):
    g0: LineSegment StartX=55.2 StartY=20 StartZ=0 EndX=55.2 EndY=12 EndZ=0
    g1: LineSegment StartX=55.2 StartY=12 StartZ=0 EndX=58 EndY=12 EndZ=0
    g2: LineSegment StartX=58 StartY=12 StartZ=0 EndX=58 EndY=20 EndZ=0
    g3: LineSegment StartX=58 StartY=20 StartZ=0 EndX=55.2 EndY=20 EndZ=0
  constraints (13):
    c: Coincident(g0,g1)
    c: Coincident(g1,g2)
    c: Coincident(g2,g3)
    c: Coincident(g3,g0)
    c: Vertical(g0)
    c: Vertical(g2)
    c: Horizontal(g1)
    c: Horizontal(g3)
    c: DistanceY(g2,g2) = 8
    c: DistanceY(g-5,g-5) = 11.8
    c: DistanceY(g2,g-5) = 1.9
    c: DistanceX(g3,g3) = 2.8
    c: DistanceX(g-5,g2) = 1.4
FEATURE [PartDesign::Pad] Pad107
  BaseFeature = -> Pad106
  Direction = (0,0,-1)
  Length = 1.5
  Length2 = 10
  Profile = -> Sketch141
  ReferenceAxis = -> Sketch141 [N_Axis]
  Refine = true
  Suppressed = false
  Type = 0
FEATURE [Sketcher::SketchObject] Sketch142
  ArcFitTolerance = 1e-06
  AttachmentSupport = -> [Pad107]
  ExternalGeometry = -> [Pad107]
  FullyConstrained = true
  MakeInternals = false
  MapMode = 5
  Placement = pos=(0,-21.9,0) rot=(1,0,0;1.5708rad)
  sketch-geometry (2):
    g0: ArcOfCircle CenterX=53.7 CenterY=-13.2 CenterZ=0 NormalX=0 NormalY=0 NormalZ=1 AngleXU=0 Radius=1.5 StartAngle=-1.8e-15 EndAngle=3.14159
    g1: LineSegment StartX=52.2 StartY=-13.2 StartZ=0 EndX=55.2 EndY=-13.2 EndZ=0
  constraints (6):
    c: Coincident(g0,g-4)
    c: PointOnObject(g0,g-3)
    c: PointOnObject(g0,g-3)
    c: Diameter(g0) = 3
    c: Coincident(g1,g0)
    c: Coincident(g1,g0)
FEATURE [PartDesign::Pocket] Pocket046
  BaseFeature = -> Pad107
  Direction = (0,1,-2e-16)
  Length = 12
  Length2 = 5
  Profile = -> Sketch142
  ReferenceAxis = -> Sketch142 [N_Axis]
  Refine = true
  Suppressed = false
  Type = 0
FEATURE [Sketcher::SketchObject] Sketch143
  ArcFitTolerance = 1e-06
  AttachmentSupport = -> [Pocket046]
  ExternalGeometry = -> [Pocket046]
  FullyConstrained = true
  MakeInternals = false
  MapMode = 5
  Placement = pos=(0,-21.9,0) rot=(1,0,0;1.5708rad)
  sketch-geometry (3):
    g0: ArcOfCircle CenterX=53.7 CenterY=-13.1017 CenterZ=0 NormalX=0 NormalY=0 NormalZ=1 AngleXU=0 Radius=2.90167 StartAngle=6.24929 EndAngle=7.85398
    g1: LineSegment StartX=53.7 StartY=-10.2 StartZ=0 EndX=56.6 EndY=-10.2 EndZ=0
    g2: LineSegment StartX=56.6 StartY=-10.2 StartZ=0 EndX=56.6 EndY=-13.2 EndZ=0
  constraints (7):
    c: Coincident(g0,g-4)
    c: PointOnObject(g0,g-5)
    c: DistanceX(g-3,g0) = 0
    c: Tangent(g1,g0) = 1.5708
    c: Coincident(g1,g-5)
    c: Coincident(g2,g0)
    c: Coincident(g2,g1)
FEATURE [PartDesign::Pocket] Pocket047
  BaseFeature = -> Pocket046
  Direction = (0,1,-2e-16)
  Length = 12
  Length2 = 5
  Profile = -> Sketch143
  ReferenceAxis = -> Sketch143 [N_Axis]
  Refine = true
  Suppressed = false
  Type = 0
FEATURE [PartDesign::Fillet] Fillet010
  Base = -> Pocket047 [Edge53,Edge50,Edge47,Edge48,Edge4,Edge26]
  BaseFeature = -> Pocket047
  Radius = 1
  Refine = true
  SupportTransform = false
  Suppressed = false
  UseAllEdges = false
FEATURE [Sketcher::SketchObject] Sketch144
  ArcFitTolerance = 1e-06
  AttachmentSupport = -> [Fillet010]
  ExternalGeometry = -> [Fillet010]
  FullyConstrained = true
  MakeInternals = false
  MapMode = 5
  Placement = pos=(0,0,-10.2) rot=(0,0,1;0rad)
  sketch-geometry (20):
    g0: LineSegment StartX=37.6 StartY=-11.25 StartZ=0 EndX=37.6 EndY=-8 EndZ=0
    g1: LineSegment StartX=37.6 StartY=-8 StartZ=0 EndX=20.6 EndY=-8 EndZ=0
    g2: LineSegment StartX=37.6 StartY=-21.25 StartZ=0 EndX=37.6 EndY=-24 EndZ=0
    g3: LineSegment StartX=37.6 StartY=-24 StartZ=0 EndX=20.6 EndY=-24 EndZ=0
    g4: LineSegment StartX=37.6 StartY=-21.25 StartZ=0 EndX=20.6 EndY=-21.25 EndZ=0
    g5: LineSegment StartX=37.6 StartY=-11.25 StartZ=0 EndX=20.6 EndY=-11.25 EndZ=0
    g6: LineSegment [constr] StartX=20.6 StartY=-26 StartZ=0 EndX=20.6 EndY=-24 EndZ=0
    g7: LineSegment [constr] StartX=20.6 StartY=-8 StartZ=0 EndX=20.6 EndY=-6 EndZ=0
    g8: ArcOfCircle CenterX=20.6 CenterY=-16 CenterZ=0 NormalX=0 NormalY=0 NormalZ=1 AngleXU=0 Radius=8 StartAngle=1.5708 EndAngle=4.71239
    g9: ArcOfCircle CenterX=20.6 CenterY=-16.25 CenterZ=0 NormalX=0 NormalY=0 NormalZ=1 AngleXU=0 Radius=5 StartAngle=1.5708 EndAngle=4.71239
    g10: LineSegment StartX=24.6 StartY=-13.25 StartZ=0 EndX=37.6 EndY=-13.25 EndZ=0
    g11: LineSegment StartX=37.6 StartY=-13.25 StartZ=0 EndX=37.6 EndY=-15.25 EndZ=0
    g12: LineSegment StartX=37.6 StartY=-15.25 StartZ=0 EndX=25.499 EndY=-15.25 EndZ=0
    g13: LineSegment StartX=25.499 StartY=-17.25 StartZ=0 EndX=37.6 EndY=-17.25 EndZ=0
    g14: LineSegment StartX=37.6 StartY=-17.25 StartZ=0 EndX=37.6 EndY=-19.25 EndZ=0
    g15: LineSegment StartX=37.6 StartY=-19.25 StartZ=0 EndX=24.6 EndY=-19.25 EndZ=0
    g16: ArcOfCircle CenterX=20.6 CenterY=-16.25 CenterZ=0 NormalX=0 NormalY=0 NormalZ=1 AngleXU=0 Radius=5 StartAngle=5.63968 EndAngle=6.08183
    g17: ArcOfCircle CenterX=20.6001 CenterY=-16.25 CenterZ=0 NormalX=0 NormalY=0 NormalZ=1 AngleXU=0 Radius=4.99998 StartAngle=0.201357 EndAngle=0.643502
    g18: LineSegment [constr] StartX=37.6 StartY=-11.25 StartZ=0 EndX=37.6 EndY=-13.25 EndZ=0
    g19: LineSegment [constr] StartX=37.6 StartY=-15.25 StartZ=0 EndX=37.6 EndY=-17.25 EndZ=0
  constraints (61):
    c: Vertical(g0)
    c: Coincident(g1,g0)
    c: Horizontal(g1)
    c: Vertical(g2)
    c: Coincident(g3,g2)
    c: Horizontal(g3)
    c: Coincident(g4,g2)
    c: Horizontal(g4)
    c: Coincident(g5,g0)
    c: Horizontal(g5)
    c: DistanceY(g1,g-4) = 2
    c: DistanceY(g-4,g3) = 2
    c: Coincident(g6,g-4)
    c: Coincident(g6,g3)
    c: Vertical(g6)
    c: Coincident(g7,g1)
    c: Coincident(g7,g-4)
    c: Vertical(g7)
    c: Coincident(g8,g3)
    c: Coincident(g8,g1)
    c: DistanceX(g8,g1) = 0
    c: Coincident(g9,g4)
    c: Coincident(g5,g9)
    c: DistanceX(g4,g3) = 0
    c: DistanceX(g5,g1) = 0
    c: Radius(g9) = 5
    c: DistanceX(g0,g-5) = 13
    c: DistanceX(g2,g-6) = 13
    c: DistanceX(g9,g8) = 0
    c: DistanceY(g0,g0) = 3.25
    c: PointOnObject(g10,g-7)
    c: Horizontal(g10)
    c: Coincident(g11,g10)
    c: Vertical(g11)
    c: Coincident(g12,g11)
    c: PointOnObject(g12,g-7)
    c: Horizontal(g12)
    c: PointOnObject(g13,g-7)
    c: Horizontal(g13)
    c: Coincident(g14,g13)
    c: Vertical(g14)
    c: Coincident(g15,g14)
    c: PointOnObject(g15,g-7)
    c: Horizontal(g15)
    c: Coincident(g16,g15)
    c: Coincident(g16,g13)
    c: Tangent(g16,g-7)
    c: Coincident(g17,g12)
    c: Coincident(g17,g10)
    c: Tangent(g17,g-7)
    c: DistanceY(g11,g11) = 2
    c: DistanceY(g14,g14) = 2
    c: Coincident(g18,g0)
    c: Coincident(g18,g10)
    c: Coincident(g19,g11)
    c: Coincident(g19,g13)
    c: Vertical(g18)
    c: Vertical(g19)
    c: DistanceY(g13,g11) = 2
    c: DistanceY(g10,g0) = 2
    c: DistanceY(g2,g14) = 2
FEATURE [PartDesign::Pocket] Pocket048
  BaseFeature = -> Fillet010
  Direction = (0,0,-1)
  Length = 1.5
  Length2 = 5
  Profile = -> Sketch144
  ReferenceAxis = -> Sketch144 [N_Axis]
  Refine = true
  Suppressed = false
  Type = 0
FEATURE [Sketcher::SketchObject] Sketch145
  ArcFitTolerance = 1e-06
  AttachmentSupport = -> [Pocket048]
  ExternalGeometry = -> [Pocket048]
  FullyConstrained = true
  MakeInternals = false
  MapMode = 5
  Placement = pos=(0,0,-13.2) rot=(1,0,0;3.14159rad)
  sketch-geometry (2):
    g0: Circle CenterX=46.45 CenterY=16 CenterZ=0 NormalX=0 NormalY=0 NormalZ=1 AngleXU=0 Radius=2.35
    g1: LineSegment [constr] StartX=46.45 StartY=16 StartZ=0 EndX=48.8 EndY=16 EndZ=0
  constraints (7):
    c: Diameter(g0) = 4.7
    c: DistanceY(g-4,g-3) = 20
    c: DistanceY(g0,g-3) = 10
    c: Coincident(g1,g0)
    c: PointOnObject(g1,g0)
    c: Horizontal(g1)
    c: DistanceX(g1,g-5) = 9.2
FEATURE [PartDesign::Pad] Pad108
  BaseFeature = -> Pocket048
  Direction = (0,0,-1)
  Length = 2
  Length2 = 10
  Profile = -> Sketch145
  ReferenceAxis = -> Sketch145 [N_Axis]
  Refine = true
  Suppressed = false
  Type = 0
FEATURE [Sketcher::SketchObject] Sketch146
  ArcFitTolerance = 1e-06
  AttachmentSupport = -> [Pad108]
  ExternalGeometry = -> [Pad108]
  FullyConstrained = true
  MakeInternals = false
  MapMode = 5
  Placement = pos=(0,0,-15.2) rot=(1,0,0;3.14159rad)
  sketch-geometry (1):
    g0: Circle CenterX=46.45 CenterY=16 CenterZ=0 NormalX=0 NormalY=0 NormalZ=1 AngleXU=0 Radius=0.75
  constraints (2):
    c: Coincident(g0,g-3)
    c: Radius(g0) = 0.75
FEATURE [PartDesign::Pocket] Pocket049
  BaseFeature = -> Pad108
  Direction = (0,0,1)
  Length = 5
  Length2 = 5
  Profile = -> Sketch146
  ReferenceAxis = -> Sketch146 [N_Axis]
  Refine = true
  Suppressed = false
  Type = 0
FEATURE [Sketcher::SketchObject] Sketch147
  ArcFitTolerance = 1e-06
  AttachmentSupport = -> [Pocket049]
  ExternalGeometry = -> [Pocket049]
  FullyConstrained = true
  MakeInternals = false
  MapMode = 5
  Placement = pos=(0,-26,0) rot=(1,0,0;1.5708rad)
  sketch-geometry (2):
    g0: ArcOfCircle CenterX=39.55 CenterY=-13.2 CenterZ=0 NormalX=0 NormalY=0 NormalZ=1 AngleXU=0 Radius=1.25 StartAngle=7e-16 EndAngle=3.14159
    g1: LineSegment StartX=40.8 StartY=-13.2 StartZ=0 EndX=38.3 EndY=-13.2 EndZ=0
  constraints (7):
    c: PointOnObject(g0,g-3)
    c: PointOnObject(g0,g-3)
    c: Diameter(g0) = 2.5
    c: DistanceX(g0,g-4) = 9.8
    c: PointOnObject(g0,g-3)
    c: Coincident(g1,g0)
    c: Coincident(g1,g0)
FEATURE [PartDesign::Pocket] Pocket050
  BaseFeature = -> Pocket049
  Direction = (0,1,-2e-16)
  Length = 18.5
  Length2 = 5
  Profile = -> Sketch147
  ReferenceAxis = -> Sketch147 [N_Axis]
  Refine = true
  Suppressed = false
  Type = 0
FEATURE [Sketcher::SketchObject] Sketch148
  ArcFitTolerance = 1e-06
  AttachmentSupport = -> [Pocket050]
  ExternalGeometry = -> [Pocket050]
  FullyConstrained = true
  MakeInternals = false
  MapMode = 5
  Placement = pos=(0,-26,0) rot=(1,0,0;1.5708rad)
  sketch-geometry (2):
    g0: ArcOfCircle CenterX=39.55 CenterY=-13.2 CenterZ=0 NormalX=0 NormalY=0 NormalZ=1 AngleXU=0 Radius=1.25 StartAngle=-1.8e-15 EndAngle=3.14159
    g1: LineSegment StartX=38.3 StartY=-13.2 StartZ=0 EndX=40.8 EndY=-13.2 EndZ=0
  constraints (4):
    c: Tangent(g0,g-3) = -1.5708
    c: Coincident(g0,g-3)
    c: Coincident(g1,g0)
    c: Coincident(g1,g0)
FEATURE [PartDesign::Pad] Pad109
  BaseFeature = -> Pocket050
  Direction = (0,-1,2e-16)
  Length = 1.5
  Length2 = 10
  Profile = -> Sketch148
  ReferenceAxis = -> Sketch148 [N_Axis]
  Refine = true
  Reversed = true
  Suppressed = false
  Type = 0
FEATURE [Sketcher::SketchObject] Sketch149
  ArcFitTolerance = 1e-06
  AttachmentSupport = -> [Pad109]
  ExternalGeometry = -> [Pad109]
  FullyConstrained = true
  MakeInternals = false
  MapMode = 5
  Placement = pos=(0,0,-13.2) rot=(1,0,0;3.14159rad)
  sketch-geometry (13):
    g0: LineSegment StartX=52.2 StartY=18.4 StartZ=0 EndX=52.2 EndY=13.6 EndZ=0
    g1: LineSegment StartX=49.1 StartY=11.6 StartZ=0 EndX=49.1 EndY=7.5 EndZ=0
    g2: LineSegment StartX=49.1 StartY=7.5 StartZ=0 EndX=42.3 EndY=7.5 EndZ=0
    g3: LineSegment StartX=42.3 StartY=7.5 StartZ=0 EndX=42.3 EndY=24.5 EndZ=0
    g4: LineSegment StartX=42.3 StartY=24.5 StartZ=0 EndX=49.1 EndY=24.5 EndZ=0
    g5: LineSegment StartX=49.1 StartY=24.5 StartZ=0 EndX=49.1 EndY=20.4 EndZ=0
    g6: Circle CenterX=46.45 CenterY=16 CenterZ=0 NormalX=0 NormalY=0 NormalZ=1 AngleXU=0 Radius=2.35
    g7: LineSegment StartX=52.2 StartY=18.4 StartZ=0 EndX=50.7 EndY=18.4 EndZ=0
    g8: LineSegment StartX=50.7 StartY=18.4 StartZ=0 EndX=50.7 EndY=20.4 EndZ=0
    g9: LineSegment StartX=50.7 StartY=20.4 StartZ=0 EndX=49.1 EndY=20.4 EndZ=0
    g10: LineSegment StartX=52.2 StartY=13.6 StartZ=0 EndX=50.7 EndY=13.6 EndZ=0
    g11: LineSegment StartX=50.7 StartY=13.6 StartZ=0 EndX=50.7 EndY=11.6 EndZ=0
    g12: LineSegment StartX=50.7 StartY=11.6 StartZ=0 EndX=49.1 EndY=11.6 EndZ=0
  constraints (38):
    c: PointOnObject(g0,g-10)
    c: PointOnObject(g0,g-10)
    c: Vertical(g1)
    c: Coincident(g2,g1)
    c: Horizontal(g2)
    c: Coincident(g3,g2)
    c: Vertical(g3)
    c: Coincident(g4,g3)
    c: Horizontal(g4)
    c: Coincident(g5,g4)
    c: Vertical(g5)
    c: Coincident(g6,g-11)
    c: Equal(g6,g-11)
    c: Coincident(g7,g0)
    c: Horizontal(g7)
    c: Coincident(g8,g7)
    c: Vertical(g8)
    c: Coincident(g9,g8)
    c: Coincident(g9,g5)
    c: Horizontal(g9)
    c: Coincident(g10,g0)
    c: Horizontal(g10)
    c: Coincident(g11,g10)
    c: Vertical(g11)
    c: Coincident(g12,g11)
    c: Coincident(g12,g1)
    c: Horizontal(g12)
    c: DistanceX(g10,g10) = 1.5
    c: DistanceX(g7,g7) = 1.5
    c: DistanceX(g-3,g2) = 1.5
    c: DistanceY(g-9,g2) = 1.5
    c: DistanceY(g4,g-4) = 1.5
    c: DistanceX(g4,g-5) = 1.5
    c: DistanceX(g1,g-8) = 1.5
    c: DistanceY(g-8,g11) = 1.5
    c: DistanceY(g8,g-6) = 1.5
    c: DistanceY(g-10,g0) = 3.5
    c: DistanceY(g0,g-10) = 3.5
FEATURE [PartDesign::Pocket] Pocket051
  BaseFeature = -> Pad109
  Direction = (0,0,1)
  Length = 1.5
  Length2 = 5
  Profile = -> Sketch149
  ReferenceAxis = -> Sketch149 [N_Axis]
  Refine = true
  Suppressed = false
  Type = 0
FEATURE [PartDesign::Pocket] Pocket052
  BaseFeature = -> Pocket051
  Direction = (1,3e-15,0)
  Length = 1.5
  Length2 = 5
  Profile = -> Pocket051 [Face84]
  Refine = true
  Suppressed = false
  Type = 0
FEATURE [PartDesign::Fillet] Fillet011
  Base = -> Pocket052 [Edge223,Edge219,Edge206,Edge209]
  BaseFeature = -> Pocket052
  Radius = 0.5
  Refine = true
  SupportTransform = false
  Suppressed = false
  UseAllEdges = false
FEATURE [Sketcher::SketchObject] Sketch150
  ArcFitTolerance = 1e-06
  AttachmentSupport = -> [Fillet011]
  ExternalGeometry = -> [Fillet011]
  FullyConstrained = true
  MakeInternals = false
  MapMode = 5
  Placement = pos=(0,0,-11.7) rot=(1,0,0;3.14159rad)
  sketch-geometry (4):
    g0: LineSegment StartX=52.2 StartY=18.4 StartZ=0 EndX=52.2 EndY=13.6 EndZ=0
    g1: LineSegment StartX=52.2 StartY=13.6 StartZ=0 EndX=55.2 EndY=13.6 EndZ=0
    g2: LineSegment StartX=55.2 StartY=13.6 StartZ=0 EndX=55.2 EndY=18.4 EndZ=0
    g3: LineSegment StartX=55.2 StartY=18.4 StartZ=0 EndX=52.2 EndY=18.4 EndZ=0
  constraints (10):
    c: Coincident(g0,g1)
    c: Coincident(g1,g2)
    c: Coincident(g2,g3)
    c: Coincident(g3,g0)
    c: Vertical(g2)
    c: Horizontal(g1)
    c: Horizontal(g3)
    c: Coincident(g0,g-3)
    c: PointOnObject(g1,g-5)
    c: Coincident(g0,g-4)
FEATURE [PartDesign::Pad] Pad110
  BaseFeature = -> Fillet011
  Direction = (0,0,-1)
  Length = 0.1
  Length2 = 10
  Profile = -> Sketch150
  ReferenceAxis = -> Sketch150 [N_Axis]
  Refine = true
  Suppressed = false
  Type = 0
FEATURE [Sketcher::SketchObject] Sketch151
  ArcFitTolerance = 1e-06
  AttachmentSupport = -> [Pad110]
  ExternalGeometry = -> [Pad110]
  FullyConstrained = true
  MakeInternals = false
  MapMode = 5
  Placement = pos=(0,0,-13.2) rot=(1,0,0;3.14159rad)
  sketch-geometry (8):
    g0: LineSegment StartX=31.6 StartY=26 StartZ=0 EndX=31.6 EndY=20 EndZ=0
    g1: LineSegment StartX=31.6 StartY=20 StartZ=0 EndX=35.6 EndY=20 EndZ=0
    g2: LineSegment StartX=35.6 StartY=20 StartZ=0 EndX=35.6 EndY=26 EndZ=0
    g3: LineSegment StartX=35.6 StartY=26 StartZ=0 EndX=31.6 EndY=26 EndZ=0
    g4: LineSegment StartX=31.6 StartY=6 StartZ=0 EndX=35.6 EndY=6 EndZ=0
    g5: LineSegment StartX=35.6 StartY=6 StartZ=0 EndX=35.6 EndY=12 EndZ=0
    g6: LineSegment StartX=35.6 StartY=12 StartZ=0 EndX=31.6 EndY=12 EndZ=0
    g7: LineSegment StartX=31.6 StartY=12 StartZ=0 EndX=31.6 EndY=6 EndZ=0
  constraints (24):
    c: Coincident(g0,g1)
    c: Coincident(g1,g2)
    c: Coincident(g2,g3)
    c: Coincident(g3,g0)
    c: Vertical(g0)
    c: Vertical(g2)
    c: Horizontal(g1)
    c: Horizontal(g3)
    c: PointOnObject(g0,g-3)
    c: Coincident(g4,g5)
    c: Coincident(g5,g6)
    c: Coincident(g6,g7)
    c: Coincident(g7,g4)
    c: Horizontal(g4)
    c: Horizontal(g6)
    c: Vertical(g5)
    c: Vertical(g7)
    c: PointOnObject(g4,g-4)
    c: DistanceY(g2,g2) = 6
    c: DistanceY(g5,g5) = 6
    c: DistanceX(g1,g1) = 4
    c: DistanceX(g6,g6) = 4
    c: DistanceX(g1,g5) = 0
    c: DistanceX(g0,g-5) = 19
FEATURE [PartDesign::Pad] Pad111
  BaseFeature = -> Pad110
  Direction = (0,0,-1)
  Length = 1
  Length2 = 10
  Profile = -> Sketch151
  ReferenceAxis = -> Sketch151 [N_Axis]
  Refine = true
  Suppressed = false
  Type = 0
FEATURE [PartDesign::Fillet] Fillet012
  Base = -> Pad111 [Edge101,Edge93,Edge100,Edge95,Edge91,Edge90,Edge103,Edge105]
  BaseFeature = -> Pad111
  Radius = 0.5
  Refine = true
  SupportTransform = false
  Suppressed = false
  UseAllEdges = false
FEATURE [Sketcher::SketchObject] Sketch152
  ArcFitTolerance = 1e-06
  AttachmentSupport = -> [Fillet012]
  ExternalGeometry = -> [Fillet012]
  FullyConstrained = true
  MakeInternals = false
  MapMode = 5
  Placement = pos=(0,0,-13.2) rot=(1,0,0;3.14159rad)
  sketch-geometry (9):
    g0: ArcOfCircle CenterX=20.6 CenterY=16 CenterZ=0 NormalX=0 NormalY=0 NormalZ=1 AngleXU=0 Radius=8.8 StartAngle=1.5708 EndAngle=4.71239
    g1: LineSegment StartX=20.6 StartY=24.8 StartZ=0 EndX=26.3 EndY=24.8 EndZ=0
    g2: LineSegment StartX=26.3 StartY=24.8 StartZ=0 EndX=26.3 EndY=7.2 EndZ=0
    g3: LineSegment StartX=26.3 StartY=7.2 StartZ=0 EndX=20.6 EndY=7.2 EndZ=0
    g4: LineSegment [constr] StartX=20.6 StartY=16 StartZ=0 EndX=11.8 EndY=16 EndZ=0
    g5: LineSegment StartX=26.1 StartY=24.6 StartZ=0 EndX=20.6 EndY=24.6 EndZ=0
    g6: LineSegment StartX=26.1 StartY=24.6 StartZ=0 EndX=26.1 EndY=7.4 EndZ=0
    g7: LineSegment StartX=26.1 StartY=7.4 StartZ=0 EndX=20.6001 EndY=7.4 EndZ=0
    g8: ArcOfCircle CenterX=20.6 CenterY=16 CenterZ=0 NormalX=0 NormalY=0 NormalZ=1 AngleXU=0 Radius=8.6 StartAngle=1.5708 EndAngle=4.71239
  constraints (28):
    c: Coincident(g1,g0)
    c: Horizontal(g1)
    c: Coincident(g2,g1)
    c: Vertical(g2)
    c: Coincident(g3,g2)
    c: Coincident(g3,g0)
    c: Horizontal(g3)
    c: DistanceY(g0,g-4) = 1.2
    c: DistanceY(g-5,g0) = 1.2
    c: DistanceX(g0,g-5) = 0
    c: DistanceX(g0,g-4) = 0
    c: Radius(g0) = 8.8
    c: Coincident(g4,g0)
    c: PointOnObject(g4,g0)
    c: Horizontal(g4)
    c: DistanceX(g4,g1) = 14.5
    c: Horizontal(g5)
    c: Coincident(g6,g5)
    c: Vertical(g6)
    c: Coincident(g7,g6)
    c: Horizontal(g7)
    c: Coincident(g8,g7)
    c: Coincident(g8,g5)
    c: Coincident(g8,g0)
    c: DistanceY(g5,g1) = 0.2
    c: DistanceY(g2,g6) = 0.2
    c: DistanceX(g6,g2) = 0.2
    c: Radius(g8) = 8.6
FEATURE [PartDesign::Pocket] Pocket053
  BaseFeature = -> Fillet012
  Direction = (0,0,1)
  Length = 0.3
  Length2 = 5
  Profile = -> Sketch152
  ReferenceAxis = -> Sketch152 [N_Axis]
  Refine = true
  Suppressed = false
  Type = 0
FEATURE [Sketcher::SketchObject] Sketch153
  ArcFitTolerance = 1e-06
  AttachmentSupport = -> [Pocket053]
  ExternalGeometry = -> [Pocket053]
  FullyConstrained = true
  MakeInternals = false
  MapMode = 5
  Placement = pos=(0,0,-13.2) rot=(1,0,0;3.14159rad)
  sketch-geometry (27):
    g0: LineSegment [constr] StartX=20.6001 StartY=7.4 StartZ=0 EndX=12 EndY=7.4 EndZ=0
    g1: LineSegment [constr] StartX=12 StartY=7.4 StartZ=0 EndX=12 EndY=24.6 EndZ=0
    g2: LineSegment [constr] StartX=20.6 StartY=24.6 StartZ=0 EndX=12 EndY=24.6 EndZ=0
    g3: LineSegment StartX=23.9 StartY=7.4 StartZ=0 EndX=24.1 EndY=7.4 EndZ=0
    g4: LineSegment StartX=24.1 StartY=7.4 StartZ=0 EndX=24.1 EndY=24.6 EndZ=0
    g5: LineSegment StartX=24.1 StartY=24.6 StartZ=0 EndX=23.9 EndY=24.6 EndZ=0
    g6: LineSegment StartX=23.9 StartY=24.6 StartZ=0 EndX=23.9 EndY=7.4 EndZ=0
    g7: LineSegment StartX=21.9 StartY=24.6 StartZ=0 EndX=21.7 EndY=24.6 EndZ=0
    g8: LineSegment StartX=21.7 StartY=24.6 StartZ=0 EndX=21.7 EndY=7.4 EndZ=0
    g9: LineSegment StartX=21.7 StartY=7.4 StartZ=0 EndX=21.9 EndY=7.4 EndZ=0
    g10: LineSegment StartX=21.9 StartY=7.4 StartZ=0 EndX=21.9 EndY=24.6 EndZ=0
    g11: LineSegment StartX=19.7 StartY=7.4 StartZ=0 EndX=19.7 EndY=24.6 EndZ=0
    g12: LineSegment StartX=19.7 StartY=24.6 StartZ=0 EndX=19.5 EndY=24.6 EndZ=0
    g13: LineSegment StartX=19.5 StartY=24.6 StartZ=0 EndX=19.5 EndY=7.4 EndZ=0
    g14: LineSegment StartX=19.5 StartY=7.4 StartZ=0 EndX=19.7 EndY=7.4 EndZ=0
    g15: LineSegment StartX=17.5 StartY=24.0218 StartZ=0 EndX=17.5 EndY=7.97815 EndZ=0
    g16: LineSegment StartX=17.5 StartY=7.97815 StartZ=0 EndX=17.3 EndY=7.97815 EndZ=0
    g17: LineSegment StartX=17.3 StartY=7.97815 StartZ=0 EndX=17.3 EndY=24.0218 EndZ=0
    g18: LineSegment StartX=17.3 StartY=24.0218 StartZ=0 EndX=17.5 EndY=24.0218 EndZ=0
    g19: LineSegment StartX=15.3 StartY=22.7727 StartZ=0 EndX=15.1 EndY=22.7727 EndZ=0
    g20: LineSegment StartX=15.1 StartY=22.7727 StartZ=0 EndX=15.1 EndY=9.22726 EndZ=0
    g21: LineSegment StartX=15.1 StartY=9.22726 StartZ=0 EndX=15.3 EndY=9.22726 EndZ=0
    g22: LineSegment StartX=15.3 StartY=9.22726 StartZ=0 EndX=15.3 EndY=22.7727 EndZ=0
    g23: LineSegment StartX=13.1 StartY=20.2083 StartZ=0 EndX=12.9 EndY=20.2083 EndZ=0
    g24: LineSegment StartX=12.9 StartY=20.2083 StartZ=0 EndX=12.9 EndY=11.7917 EndZ=0
    g25: LineSegment StartX=12.9 StartY=11.7917 StartZ=0 EndX=13.1 EndY=11.7917 EndZ=0
    g26: LineSegment StartX=13.1 StartY=11.7917 StartZ=0 EndX=13.1 EndY=20.2083 EndZ=0
  constraints (80):
    c: Coincident(g1,g0)
    c: Vertical(g1)
    c: Tangent(g1,g-4)
    c: Horizontal(g0)
    c: Horizontal(g2)
    c: Coincident(g2,g1)
    c: Coincident(g2,g-4)
    c: Coincident(g0,g-5)
    c: Coincident(g3,g4)
    c: Coincident(g4,g5)
    c: Coincident(g5,g6)
    c: Coincident(g6,g3)
    c: Horizontal(g3)
    c: Horizontal(g5)
    c: Vertical(g4)
    c: Vertical(g6)
    c: PointOnObject(g3,g-5)
    c: PointOnObject(g4,g-3)
    c: DistanceX(g5,g5) = 0.2
    c: DistanceX(g4,g-3) = 2
    c: Coincident(g7,g8)
    c: Coincident(g8,g9)
    c: Coincident(g9,g10)
    c: Coincident(g10,g7)
    c: Horizontal(g7)
    c: Horizontal(g9)
    c: Vertical(g8)
    c: Vertical(g10)
    c: PointOnObject(g7,g-3)
    c: PointOnObject(g8,g-5)
    c: DistanceX(g9,g9) = 0.2
    c: DistanceX(g9,g3) = 2
    c: Coincident(g11,g12)
    c: Coincident(g12,g13)
    c: Coincident(g13,g14)
    c: Coincident(g14,g11)
    c: Vertical(g11)
    c: Vertical(g13)
    c: Horizontal(g12)
    c: Horizontal(g14)
    c: PointOnObject(g11,g-5)
    c: PointOnObject(g12,g-3)
    c: DistanceX(g12,g12) = 0.2
    c: DistanceX(g11,g7) = 2
    c: PointOnObject(g15,g-4)
    c: PointOnObject(g15,g-4)
    c: Vertical(g15)
    c: Coincident(g16,g15)
    c: Coincident(g17,g16)
    c: Vertical(g17)
    c: Coincident(g18,g17)
    c: Coincident(g18,g15)
    c: Horizontal(g18)
    c: DistanceX(g18,g18) = 0.2
    c: DistanceX(g15,g12) = 2
    c: Horizontal(g16)
    c: Coincident(g19,g20)
    c: Coincident(g20,g21)
    c: Coincident(g21,g22)
    c: Coincident(g22,g19)
    c: Horizontal(g19)
    c: Horizontal(g21)
    c: Vertical(g20)
    c: Vertical(g22)
    c: PointOnObject(g19,g-4)
    c: DistanceX(g21,g21) = 0.2
    c: PointOnObject(g21,g-4)
    c: DistanceX(g21,g16) = 2
    c: Coincident(g23,g24)
    c: Coincident(g24,g25)
    c: Coincident(g25,g26)
    c: Coincident(g26,g23)
    c: Horizontal(g23)
    c: Horizontal(g25)
    c: Vertical(g24)
    c: Vertical(g26)
    c: PointOnObject(g23,g-4)
    c: PointOnObject(g25,g-4)
    c: DistanceX(g25,g25) = 0.2
    c: DistanceX(g25,g20) = 2
FEATURE [PartDesign::Pocket] Pocket054
  BaseFeature = -> Pocket053
  Direction = (0,0,1)
  Length = 0.3
  Length2 = 5
  Profile = -> Sketch153
  ReferenceAxis = -> Sketch153 [N_Axis]
  Refine = true
  Suppressed = false
  Type = 0
FEATURE [Sketcher::SketchObject] Sketch154
  ArcFitTolerance = 1e-06
  AttachmentSupport = -> [Pocket054]
  ExternalGeometry = -> [Pocket054]
  FullyConstrained = true
  MakeInternals = false
  MapMode = 5
  Placement = pos=(0,0,-13.2) rot=(1,0,0;3.14159rad)
  sketch-geometry (2):
    g0: Circle CenterX=20.6 CenterY=16.25 CenterZ=0 NormalX=0 NormalY=0 NormalZ=1 AngleXU=0 Radius=3.55
    g1: Circle CenterX=20.6 CenterY=16.25 CenterZ=0 NormalX=0 NormalY=0 NormalZ=1 AngleXU=0 Radius=4
  constraints (4):
    c: Coincident(g0,g-3)
    c: Equal(g0,g-3)
    c: Coincident(g1,g0)
    c: Radius(g1) = 4
FEATURE [PartDesign::Pad] Pad112
  BaseFeature = -> Pocket054
  Direction = (0,0,-1)
  Length = 0.3
  Length2 = 10
  Profile = -> Sketch154
  ReferenceAxis = -> Sketch154 [N_Axis]
  Refine = true
  Suppressed = false
  Type = 0
FEATURE [PartDesign::Pad] Pad113
  BaseFeature = -> Pad112
  Direction = (0,0,-1)
  Length = 0.3
  Length2 = 10
  Profile = -> Sketch154
  ReferenceAxis = -> Sketch154 [N_Axis]
  Refine = true
  Reversed = true
  Suppressed = false
  Type = 0
FEATURE [PartDesign::Body] Body005  label="Chest_Plate"
  AllowCompound = false
  Group = -> [Binder002,Sketch133,Pad102,Sketch134,Pocket043,Sketch135,Pad103,Sketch136,Pocket044,Sketch137,Pad104,Sketch138,Pad105,Chamfer002,Sketch139,Pocket045,Sketch140,Pad106,Sketch141,Pad107,Sketch142,Pocket046,Sketch143,Pocket047,Fillet010,Sketch144,Pocket048,Sketch145,Pad108,Sketch146,Pocket049,Sketch147,Pocket050,Sketch148,Pad109,Sketch149,Pocket051,Pocket052,Fillet011,Sketch150,Pad110,Sketch151,+9 more]
  Origin = -> Origin005
  Tip = -> Pad113
FEATURE [PartDesign::SubShapeBinder] Binder003
  BindCopyOnChange = 0
  BindMode = 2
  ClaimChildren = false
  Context = -> Body006 [Binder003.]
  Fuse = false
  MakeFace = true
  OffsetFill = false
  OffsetIntersection = false
  OffsetJoinType = 0
  OffsetOpenResult = false
  PartialLoad = false
  Refine = true
  Relative = true
  _Version = 2
FEATURE [Sketcher::SketchObject] Sketch155
  ArcFitTolerance = 1e-06
  AttachmentSupport = -> [Binder003]
  ExternalGeometry = -> [Binder003]
  FullyConstrained = true
  MakeInternals = false
  MapMode = 5
  Placement = pos=(0,0,-13.2) rot=(1,0,0;3.14159rad)
  sketch-geometry (28):
    g0: LineSegment StartX=50.6 StartY=21.9 StartZ=0 EndX=58.1 EndY=21.9 EndZ=0
    g1: LineSegment StartX=59.1 StartY=20.9 StartZ=0 EndX=59.1 EndY=11.1 EndZ=0
    g2: LineSegment StartX=58.1 StartY=10.1 StartZ=0 EndX=50.6 EndY=10.1 EndZ=0
    g3: LineSegment StartX=50.6 StartY=10.1 StartZ=0 EndX=50.6 EndY=7 EndZ=0
    g4: LineSegment StartX=49.6 StartY=6 StartZ=0 EndX=36.4 EndY=6 EndZ=0
    g5: LineSegment StartX=35.9 StartY=6.5 StartZ=0 EndX=35.9 EndY=11.4 EndZ=0
    g6: LineSegment StartX=36.4 StartY=11.9 StartZ=0 EndX=42.3 EndY=11.9 EndZ=0
    g7: LineSegment StartX=42.3 StartY=11.9 StartZ=0 EndX=42.3 EndY=20.1 EndZ=0
    g8: LineSegment StartX=42.3 StartY=20.1 StartZ=0 EndX=36.4 EndY=20.1 EndZ=0
    g9: LineSegment StartX=35.9 StartY=20.6 StartZ=0 EndX=35.9 EndY=25.5 EndZ=0
    g10: LineSegment StartX=36.4 StartY=26 StartZ=0 EndX=49.6 EndY=26 EndZ=0
    g11: LineSegment StartX=50.6 StartY=25 StartZ=0 EndX=50.6 EndY=21.9 EndZ=0
    g12: ArcOfCircle CenterX=49.6 CenterY=25 CenterZ=0 NormalX=0 NormalY=0 NormalZ=1 AngleXU=0 Radius=1 StartAngle=-1.8e-15 EndAngle=1.5708
    g13: GeomPoint [constr] X=50.6 Y=26 Z=0
    g14: ArcOfCircle CenterX=49.6 CenterY=7 CenterZ=0 NormalX=0 NormalY=0 NormalZ=1 AngleXU=0 Radius=1 StartAngle=4.71239 EndAngle=6.28319
    g15: GeomPoint [constr] X=50.6 Y=6 Z=0
    g16: ArcOfCircle CenterX=58.1 CenterY=11.1 CenterZ=0 NormalX=0 NormalY=0 NormalZ=1 AngleXU=0 Radius=1 StartAngle=4.71239 EndAngle=6.28319
    g17: GeomPoint [constr] X=59.1 Y=10.1 Z=0
    g18: ArcOfCircle CenterX=58.1 CenterY=20.9 CenterZ=0 NormalX=0 NormalY=0 NormalZ=1 AngleXU=0 Radius=1 StartAngle=1.3e-15 EndAngle=1.5708
    g19: GeomPoint [constr] X=59.1 Y=21.9 Z=0
    g20: ArcOfCircle CenterX=36.4 CenterY=6.5 CenterZ=0 NormalX=0 NormalY=0 NormalZ=1 AngleXU=0 Radius=0.5 StartAngle=3.14159 EndAngle=4.71239
    g21: GeomPoint [constr] X=35.9 Y=6 Z=0
    g22: ArcOfCircle CenterX=36.4 CenterY=11.4 CenterZ=0 NormalX=0 NormalY=0 NormalZ=1 AngleXU=0 Radius=0.5 StartAngle=1.5708 EndAngle=3.14159
    g23: GeomPoint [constr] X=35.9 Y=11.9 Z=0
    g24: ArcOfCircle CenterX=36.4 CenterY=20.6 CenterZ=0 NormalX=0 NormalY=0 NormalZ=1 AngleXU=0 Radius=0.5 StartAngle=3.14159 EndAngle=4.71239
    g25: GeomPoint [constr] X=35.9 Y=20.1 Z=0
    g26: ArcOfCircle CenterX=36.4 CenterY=25.5 CenterZ=0 NormalX=0 NormalY=0 NormalZ=1 AngleXU=0 Radius=0.5 StartAngle=1.5708 EndAngle=3.14159
    g27: GeomPoint [constr] X=35.9 Y=26 Z=0
  constraints (66):
    c: Coincident(g0,g-5)
    c: Horizontal(g0)
    c: Coincident(g2,g-11)
    c: Horizontal(g2)
    c: Coincident(g3,g2)
    c: Vertical(g3)
    c: PointOnObject(g21,g-9)
    c: Horizontal(g4)
    c: Vertical(g5)
    c: Horizontal(g6)
    c: Coincident(g7,g6)
    c: Vertical(g7)
    c: Coincident(g8,g7)
    c: Horizontal(g8)
    c: PointOnObject(g27,g-6)
    c: Vertical(g9)
    c: Horizontal(g10)
    c: Vertical(g11)
    c: Coincident(g0,g11)
    c: Vertical(g1)
    c: DistanceY(g21,g23) = 5.9
    c: DistanceY(g25,g27) = 5.9
    c: DistanceX(g23,g25) = 0
    c: PointOnObject(g6,g-14)
    c: DistanceX(g-8,g21) = 0.3
    c: DistanceX(g0,g19) = 8.5
    c: PointOnObject(g13,g10)
    c: PointOnObject(g13,g11)
    c: Tangent(g10,g12) = 1.5708
    c: Tangent(g11,g12) = 1.5708
    c: PointOnObject(g15,g3)
    c: PointOnObject(g15,g4)
    c: Tangent(g3,g14) = 1.5708
    c: Tangent(g4,g14) = 1.5708
    c: PointOnObject(g17,g1)
    c: PointOnObject(g17,g2)
    c: Tangent(g1,g16) = 1.5708
    c: Tangent(g2,g16) = 1.5708
    c: PointOnObject(g19,g0)
    c: PointOnObject(g19,g1)
    c: Tangent(g0,g18) = 1.5708
    c: Tangent(g1,g18) = 1.5708
    c: PointOnObject(g21,g4)
    c: PointOnObject(g21,g5)
    c: Tangent(g4,g20) = 1.5708
    c: Tangent(g5,g20) = 1.5708
    c: PointOnObject(g23,g5)
    c: PointOnObject(g23,g6)
    c: Tangent(g5,g22) = 1.5708
    c: Tangent(g6,g22) = 1.5708
    c: PointOnObject(g25,g8)
    c: PointOnObject(g25,g9)
    c: Tangent(g8,g24) = 1.5708
    c: Tangent(g9,g24) = 1.5708
    c: PointOnObject(g27,g9)
    c: PointOnObject(g27,g10)
    c: Tangent(g9,g26) = 1.5708
    c: Tangent(g10,g26) = 1.5708
    c: Radius(g12) = 1
    c: Radius(g18) = 1
    c: Radius(g16) = 1
    c: Radius(g14) = 1
    c: Radius(g20) = 0.5
    c: Radius(g22) = 0.5
    c: Radius(g24) = 0.5
    c: Radius(g26) = 0.5
FEATURE [PartDesign::Pad] Pad114
  Direction = (0,0,-1)
  Length = 5
  Length2 = 10
  Profile = -> Sketch155
  ReferenceAxis = -> Sketch155 [N_Axis]
  Refine = true
  Suppressed = false
  Type = 0
FEATURE [Sketcher::SketchObject] Sketch156
  ArcFitTolerance = 1e-06
  AttachmentSupport = -> [Pad114]
  ExternalGeometry = -> [Pad114]
  FullyConstrained = true
  MakeInternals = false
  MapMode = 5
  Placement = pos=(0,0,-18.2) rot=(1,0,0;3.14159rad)
  sketch-geometry (12):
    g0: LineSegment StartX=42.3 StartY=20.1 StartZ=0 EndX=36.4 EndY=20.1 EndZ=0
    g1: LineSegment StartX=35.9 StartY=20.6 StartZ=0 EndX=35.9 EndY=25.5 EndZ=0
    g2: LineSegment StartX=42.3 StartY=20.1 StartZ=0 EndX=42.3 EndY=26 EndZ=0
    g3: LineSegment StartX=42.3 StartY=26 StartZ=0 EndX=36.4 EndY=26 EndZ=0
    g4: ArcOfCircle CenterX=36.4 CenterY=25.5 CenterZ=0 NormalX=0 NormalY=0 NormalZ=1 AngleXU=0 Radius=0.5 StartAngle=1.5708 EndAngle=3.14159
    g5: ArcOfCircle CenterX=36.4 CenterY=20.6 CenterZ=0 NormalX=0 NormalY=0 NormalZ=1 AngleXU=0 Radius=0.5 StartAngle=3.14161 EndAngle=4.71239
    g6: ArcOfCircle CenterX=36.4 CenterY=11.4 CenterZ=0 NormalX=0 NormalY=0 NormalZ=1 AngleXU=0 Radius=0.5 StartAngle=1.5708 EndAngle=3.14159
    g7: ArcOfCircle CenterX=36.4 CenterY=6.5 CenterZ=0 NormalX=0 NormalY=0 NormalZ=1 AngleXU=0 Radius=0.5 StartAngle=3.14159 EndAngle=4.71239
    g8: LineSegment StartX=35.9 StartY=6.5 StartZ=0 EndX=35.9 EndY=11.4 EndZ=0
    g9: LineSegment StartX=36.4 StartY=11.9 StartZ=0 EndX=42.3 EndY=11.9 EndZ=0
    g10: LineSegment StartX=42.3 StartY=11.9 StartZ=0 EndX=42.3 EndY=6 EndZ=0
    g11: LineSegment StartX=42.3 StartY=6 StartZ=0 EndX=36.4 EndY=6 EndZ=0
  constraints (28):
    c: Coincident(g0,g-13)
    c: Coincident(g0,g-6)
    c: Coincident(g2,g0)
    c: Vertical(g2)
    c: Coincident(g3,g-7)
    c: Coincident(g3,g2)
    c: PointOnObject(g2,g-3)
    c: Coincident(g4,g3)
    c: Coincident(g4,g1)
    c: Coincident(g5,g1)
    c: Coincident(g5,g0)
    c: PointOnObject(g1,g-5)
    c: Coincident(g4,g-7)
    c: Coincident(g5,g-6)
    c: PointOnObject(g1,g-5)
    c: Coincident(g6,g-10)
    c: Tangent(g6,g-9) = -1.5708
    c: Tangent(g7,g-11) = -1.5708
    c: Coincident(g7,g-12)
    c: Coincident(g8,g7)
    c: Coincident(g8,g6)
    c: Coincident(g9,g6)
    c: Coincident(g9,g-13)
    c: Coincident(g10,g9)
    c: PointOnObject(g10,g-12)
    c: Vertical(g10)
    c: Coincident(g11,g10)
    c: Coincident(g11,g7)
FEATURE [PartDesign::Pocket] Pocket055
  BaseFeature = -> Pad114
  Direction = (0,0,1)
  Length = 2
  Length2 = 5
  Profile = -> Sketch156
  ReferenceAxis = -> Sketch156 [N_Axis]
  Refine = true
  Suppressed = false
  Type = 0
FEATURE [Sketcher::SketchObject] Sketch157
  ArcFitTolerance = 1e-06
  AttachmentSupport = -> [Pocket055]
  ExternalGeometry = -> [Pocket055]
  FullyConstrained = true
  MakeInternals = false
  MapMode = 5
  Placement = pos=(0,0,-18.2) rot=(1,0,0;3.14159rad)
  sketch-geometry (10):
    g0: ArcOfCircle CenterX=49.6 CenterY=25 CenterZ=0 NormalX=0 NormalY=0 NormalZ=1 AngleXU=0 Radius=1 StartAngle=-3.6e-15 EndAngle=1.5708
    g1: ArcOfCircle CenterX=49.6 CenterY=7 CenterZ=0 NormalX=0 NormalY=0 NormalZ=1 AngleXU=0 Radius=1 StartAngle=4.71239 EndAngle=6.28319
    g2: LineSegment StartX=50.6 StartY=10.1 StartZ=0 EndX=50.6 EndY=7 EndZ=0
    g3: LineSegment StartX=49.6 StartY=6 StartZ=0 EndX=42.3 EndY=6 EndZ=0
    g4: LineSegment StartX=50.6 StartY=10.1 StartZ=0 EndX=42.3 EndY=10.1 EndZ=0
    g5: LineSegment StartX=42.3 StartY=10.1 StartZ=0 EndX=42.3 EndY=6 EndZ=0
    g6: LineSegment StartX=50.6 StartY=25 StartZ=0 EndX=50.6 EndY=21.9 EndZ=0
    g7: LineSegment StartX=49.6 StartY=26 StartZ=0 EndX=42.3 EndY=26 EndZ=0
    g8: LineSegment StartX=50.6 StartY=21.9 StartZ=0 EndX=42.3 EndY=21.9 EndZ=0
    g9: LineSegment StartX=42.3 StartY=26 StartZ=0 EndX=42.3 EndY=21.9 EndZ=0
  constraints (22):
    c: Tangent(g0,g-4) = -1.5708
    c: Coincident(g0,g-5)
    c: Tangent(g1,g-8) = -1.5708
    c: Coincident(g1,g-9)
    c: Coincident(g2,g-7)
    c: Coincident(g2,g1)
    c: Coincident(g3,g1)
    c: Coincident(g3,g-9)
    c: Coincident(g4,g2)
    c: PointOnObject(g4,g-6)
    c: Horizontal(g4)
    c: Coincident(g5,g4)
    c: Coincident(g5,g3)
    c: Coincident(g6,g0)
    c: Coincident(g6,g-3)
    c: Coincident(g7,g0)
    c: Coincident(g7,g-6)
    c: Coincident(g8,g6)
    c: PointOnObject(g8,g-6)
    c: Horizontal(g8)
    c: Coincident(g9,g7)
    c: Coincident(g9,g8)
FEATURE [PartDesign::Pocket] Pocket056
  BaseFeature = -> Pocket055
  Direction = (0,0,1)
  Length = 1
  Length2 = 5
  Profile = -> Sketch157
  ReferenceAxis = -> Sketch157 [N_Axis]
  Refine = true
  Suppressed = false
  Type = 0
FEATURE [Sketcher::SketchObject] Sketch158
  ArcFitTolerance = 1e-06
  AttachmentSupport = -> [Pocket056]
  ExternalGeometry = -> [Pocket056]
  FullyConstrained = true
  MakeInternals = false
  MapMode = 5
  Placement = pos=(42.3,0,0) rot=(0.57735,-0.57735,-0.57735;2.0944rad)
  sketch-geometry (6):
    g0: LineSegment StartX=10.1 StartY=-17.2 StartZ=0 EndX=6 EndY=-16.2 EndZ=0
    g1: LineSegment StartX=6 StartY=-16.2 StartZ=0 EndX=6 EndY=-17.2 EndZ=0
    g2: LineSegment StartX=6 StartY=-17.2 StartZ=0 EndX=10.1 EndY=-17.2 EndZ=0
    g3: LineSegment StartX=21.9 StartY=-17.2 StartZ=0 EndX=26 EndY=-16.2 EndZ=0
    g4: LineSegment StartX=26 StartY=-16.2 StartZ=0 EndX=26 EndY=-17.2 EndZ=0
    g5: LineSegment StartX=26 StartY=-17.2 StartZ=0 EndX=21.9 EndY=-17.2 EndZ=0
  constraints (12):
    c: Coincident(g0,g-4)
    c: Coincident(g0,g-3)
    c: Coincident(g1,g0)
    c: Coincident(g1,g-4)
    c: Coincident(g2,g1)
    c: Coincident(g2,g0)
    c: Coincident(g3,g-5)
    c: Coincident(g3,g-6)
    c: Coincident(g4,g3)
    c: Coincident(g4,g-6)
    c: Coincident(g5,g4)
    c: Coincident(g5,g3)
FEATURE [PartDesign::Pocket] Pocket057
  BaseFeature = -> Pocket056
  Direction = (1,0,0)
  Length = 9
  Length2 = 5
  Profile = -> Sketch158
  ReferenceAxis = -> Sketch158 [N_Axis]
  Refine = true
  Suppressed = false
  Type = 0
FEATURE [Sketcher::SketchObject] Sketch159
  ArcFitTolerance = 1e-06
  AttachmentSupport = -> [Pocket057]
  ExternalGeometry = -> [Pocket057]
  FullyConstrained = true
  MakeInternals = false
  MapMode = 5
  Placement = pos=(0,-10.1,0) rot=(0,0.707107,0.707107;3.14159rad)
  sketch-geometry (4):
    g0: LineSegment [constr] StartX=-50.6 StartY=-16.4439 StartZ=0 EndX=-50.6 EndY=-18.2 EndZ=0
    g1: LineSegment StartX=-50.6 StartY=-18.2 StartZ=0 EndX=-59.1 EndY=-16.2 EndZ=0
    g2: LineSegment StartX=-59.1 StartY=-16.2 StartZ=0 EndX=-59.1 EndY=-18.2 EndZ=0
    g3: LineSegment StartX=-59.1 StartY=-18.2 StartZ=0 EndX=-50.6 EndY=-18.2 EndZ=0
  constraints (10):
    c: Coincident(g0,g-3)
    c: PointOnObject(g0,g-4)
    c: Vertical(g0)
    c: Coincident(g1,g0)
    c: PointOnObject(g1,g-6)
    c: Coincident(g2,g1)
    c: Coincident(g2,g-6)
    c: Coincident(g3,g2)
    c: Coincident(g3,g0)
    c: DistanceY(g2,g2) = 2
FEATURE [PartDesign::Pocket] Pocket058
  BaseFeature = -> Pocket057
  Direction = (0,-1,2e-16)
  Length = 12
  Length2 = 5
  Profile = -> Sketch159
  ReferenceAxis = -> Sketch159 [N_Axis]
  Refine = true
  Suppressed = false
  Type = 0
FEATURE [Sketcher::SketchObject] Sketch160
  ArcFitTolerance = 1e-06
  AttachmentSupport = -> [Pocket058]
  ExternalGeometry = -> [Pocket058]
  FullyConstrained = true
  MakeInternals = false
  MapMode = 5
  Placement = pos=(0,0,-18.2) rot=(1,0,0;3.14159rad)
  sketch-geometry (4):
    g0: LineSegment StartX=59.1 StartY=20.4 StartZ=0 EndX=57.1 EndY=20.4 EndZ=0
    g1: LineSegment StartX=57.1 StartY=20.4 StartZ=0 EndX=57.1 EndY=11.6 EndZ=0
    g2: LineSegment StartX=57.1 StartY=11.6 StartZ=0 EndX=59.1 EndY=11.6 EndZ=0
    g3: LineSegment StartX=59.1 StartY=11.6 StartZ=0 EndX=59.1 EndY=20.4 EndZ=0
  constraints (12):
    c: Coincident(g0,g1)
    c: Coincident(g1,g2)
    c: Coincident(g2,g3)
    c: Coincident(g3,g0)
    c: Horizontal(g0)
    c: Horizontal(g2)
    c: Vertical(g1)
    c: Vertical(g3)
    c: PointOnObject(g0,g-4)
    c: DistanceY(g-5,g1) = 1.5
    c: DistanceY(g0,g-3) = 1.5
    c: DistanceX(g0,g0) = 2
FEATURE [PartDesign::Pocket] Pocket059
  BaseFeature = -> Pocket058
  Direction = (0,0,1)
  Length = 5
  Length2 = 5
  Profile = -> Sketch160
  ReferenceAxis = -> Sketch160 [N_Axis]
  Refine = true
  Suppressed = false
  Type = 0
FEATURE [Sketcher::SketchObject] Sketch161
  ArcFitTolerance = 1e-06
  AttachmentOffset = pos=(0,0,-1.5) rot=(0,0,1;0rad)
  AttachmentSupport = -> [Pocket059]
  ExternalGeometry = -> [Pocket059]
  FullyConstrained = true
  MakeInternals = false
  MapMode = 5
  Placement = pos=(0,-11.6,3e-16) rot=(0,0.707107,0.707107;3.14159rad)
  sketch-geometry (4):
    g0: LineSegment StartX=-50.6 StartY=-13.2 StartZ=0 EndX=-57.1 EndY=-13.2 EndZ=0
    g1: LineSegment StartX=-57.1 StartY=-13.2 StartZ=0 EndX=-57.1 EndY=-14.7706 EndZ=0
    g2: LineSegment StartX=-50.6 StartY=-13.2 StartZ=0 EndX=-50.6 EndY=-16.3 EndZ=0
    g3: LineSegment StartX=-50.6 StartY=-16.3 StartZ=0 EndX=-57.1 EndY=-14.7706 EndZ=0
  constraints (10):
    c: Coincident(g0,g-6)
    c: Coincident(g0,g-5)
    c: Coincident(g1,g0)
    c: Coincident(g2,g0)
    c: Vertical(g2)
    c: Coincident(g3,g2)
    c: Coincident(g3,g1)
    c: Parallel(g3,g-3)
    c: DistanceY(g-5,g1) = 1.9
    c: PointOnObject(g1,g-5)
FEATURE [PartDesign::Pocket] Pocket060
  BaseFeature = -> Pocket059
  Direction = (0,-1,2e-16)
  Length = 8.8
  Length2 = 5
  Profile = -> Sketch161
  ReferenceAxis = -> Sketch161 [N_Axis]
  Refine = true
  Suppressed = false
  Type = 0
FEATURE [Sketcher::SketchObject] Sketch162
  ArcFitTolerance = 1e-06
  AttachmentSupport = -> [Pocket060]
  ExternalGeometry = -> [Pocket060]
  FullyConstrained = true
  MakeInternals = false
  MapMode = 5
  Placement = pos=(0,0,-13.2) rot=(0,0,1;0rad)
  sketch-geometry (7):
    g0: ArcOfCircle CenterX=58.1 CenterY=-20.9 CenterZ=0 NormalX=0 NormalY=0 NormalZ=1 AngleXU=0 Radius=1 StartAngle=3.14159 EndAngle=6.28319
    g1: LineSegment [constr] StartX=58.1 StartY=-20.9 StartZ=0 EndX=57.1 EndY=-20.9 EndZ=0
    g2: ArcOfCircle CenterX=58.1 CenterY=-11.1 CenterZ=0 NormalX=0 NormalY=0 NormalZ=1 AngleXU=0 Radius=1 StartAngle=4.303e-13 EndAngle=3.14159
    g3: LineSegment [constr] StartX=58.1 StartY=-11.1 StartZ=0 EndX=57.1 EndY=-11.1 EndZ=0
    g4: LineSegment StartX=59.1 StartY=-11.1 StartZ=0 EndX=59.1 EndY=-20.9 EndZ=0
    g5: LineSegment StartX=57.1 StartY=-20.9 StartZ=0 EndX=57.1 EndY=-11.1 EndZ=0
    g6: LineSegment [constr] StartX=58.1 StartY=-11.1 StartZ=0 EndX=59.1 EndY=-11.1 EndZ=0
  constraints (15):
    c: Coincident(g0,g-8)
    c: Coincident(g0,g-7)
    c: Coincident(g1,g0)
    c: Coincident(g1,g0)
    c: Horizontal(g1)
    c: Coincident(g3,g2)
    c: Coincident(g3,g2)
    c: Coincident(g2,g-3)
    c: Coincident(g4,g2)
    c: Tangent(g4,g0) = 1.5708
    c: Coincident(g5,g0)
    c: Tangent(g5,g2) = 1.5708
    c: Coincident(g6,g2)
    c: Coincident(g6,g2)
    c: Horizontal(g6)
FEATURE [PartDesign::Pad] Pad115
  BaseFeature = -> Pocket060
  Direction = (0,0,1)
  Length = 1.5
  Length2 = 10
  Profile = -> Sketch162
  ReferenceAxis = -> Sketch162 [N_Axis]
  Refine = true
  Suppressed = false
  Type = 0
FEATURE [PartDesign::Pocket] Pocket061
  BaseFeature = -> Pad115
  Direction = (0,0,1)
  Length = 0.05
  Length2 = 5
  Profile = -> Pad115 [Face30]
  Refine = true
  Suppressed = false
  Type = 0
FEATURE [Sketcher::SketchObject] Sketch163
  ArcFitTolerance = 1e-06
  AttachmentSupport = -> [Pocket061]
  ExternalGeometry = -> [Pocket061]
  FullyConstrained = true
  MakeInternals = false
  MapMode = 5
  Placement = pos=(0,0,-18.2) rot=(1,0,0;3.14159rad)
  sketch-geometry (1):
    g0: Circle CenterX=46.45 CenterY=16 CenterZ=0 NormalX=0 NormalY=0 NormalZ=1 AngleXU=0 Radius=1
  constraints (3):
    c: Diameter(g0) = 2
    c: DistanceX(g-4,g0) = 4.15
    c: DistanceY(g0,g-4) = 5.9
FEATURE [PartDesign::Pocket] Pocket062
  BaseFeature = -> Pocket061
  Direction = (0,0,1)
  Length = 5
  Length2 = 5
  Profile = -> Sketch163
  ReferenceAxis = -> Sketch163 [N_Axis]
  Refine = true
  Suppressed = false
  Type = 0
FEATURE [Sketcher::SketchObject] Sketch164
  ArcFitTolerance = 1e-06
  AttachmentSupport = -> [Pocket062]
  ExternalGeometry = -> [Pocket062]
  FullyConstrained = true
  MakeInternals = false
  MapMode = 5
  Placement = pos=(0,0,-18.2) rot=(1,0,0;3.14159rad)
  sketch-geometry (1):
    g0: Circle CenterX=46.45 CenterY=16 CenterZ=0 NormalX=0 NormalY=0 NormalZ=1 AngleXU=0 Radius=1.95
  constraints (2):
    c: Coincident(g0,g-3)
    c: Diameter(g0) = 3.9
FEATURE [PartDesign::Pocket] Pocket063
  BaseFeature = -> Pocket062
  Direction = (0,0,1)
  Length = 1.5
  Length2 = 5
  Profile = -> Sketch164
  ReferenceAxis = -> Sketch164 [N_Axis]
  Refine = true
  Suppressed = false
  Type = 0
FEATURE [Sketcher::SketchObject] Sketch165
  ArcFitTolerance = 1e-06
  AttachmentSupport = -> [Pocket063]
  ExternalGeometry = -> [Pocket063]
  FullyConstrained = true
  MakeInternals = false
  MapMode = 5
  Placement = pos=(0,0,-13.2) rot=(0,0,1;0rad)
  sketch-geometry (4):
    g0: LineSegment StartX=50.6 StartY=-11.6 StartZ=0 EndX=43.8 EndY=-11.6 EndZ=0
    g1: LineSegment StartX=43.8 StartY=-11.6 StartZ=0 EndX=43.8 EndY=-20.4 EndZ=0
    g2: LineSegment StartX=43.8 StartY=-20.4 StartZ=0 EndX=50.6 EndY=-20.4 EndZ=0
    g3: LineSegment StartX=50.6 StartY=-20.4 StartZ=0 EndX=50.6 EndY=-11.6 EndZ=0
  constraints (10):
    c: Coincident(g0,g1)
    c: Coincident(g1,g2)
    c: Coincident(g2,g3)
    c: Coincident(g3,g0)
    c: Horizontal(g0)
    c: Horizontal(g2)
    c: Vertical(g1)
    c: Coincident(g0,g-3)
    c: Coincident(g2,g-3)
    c: DistanceX(g-4,g1) = 1.5
FEATURE [PartDesign::Pocket] Pocket064
  BaseFeature = -> Pocket063
  Direction = (0,0,-1)
  Length = 3.1
  Length2 = 5
  Profile = -> Sketch165
  ReferenceAxis = -> Sketch165 [N_Axis]
  Refine = true
  Suppressed = false
  Type = 0
FEATURE [Sketcher::SketchObject] Sketch166
  ArcFitTolerance = 1e-06
  AttachmentSupport = -> [Pocket064]
  ExternalGeometry = -> [Pocket064]
  FullyConstrained = true
  MakeInternals = false
  MapMode = 5
  Placement = pos=(0,0,-13.2) rot=(0,0,1;0rad)
  sketch-geometry (8):
    g0: LineSegment StartX=42.3 StartY=-10.4 StartZ=0 EndX=42.3 EndY=-7.5 EndZ=0
    g1: LineSegment StartX=42.3 StartY=-7.5 StartZ=0 EndX=37.4 EndY=-7.5 EndZ=0
    g2: LineSegment StartX=37.4 StartY=-7.5 StartZ=0 EndX=37.4 EndY=-10.4 EndZ=0
    g3: LineSegment StartX=37.4 StartY=-10.4 StartZ=0 EndX=42.3 EndY=-10.4 EndZ=0
    g4: LineSegment StartX=37.4 StartY=-21.6 StartZ=0 EndX=37.4 EndY=-24.5 EndZ=0
    g5: LineSegment StartX=37.4 StartY=-24.5 StartZ=0 EndX=42.3 EndY=-24.5 EndZ=0
    g6: LineSegment StartX=42.3 StartY=-24.5 StartZ=0 EndX=42.3 EndY=-21.6 EndZ=0
    g7: LineSegment StartX=42.3 StartY=-21.6 StartZ=0 EndX=37.4 EndY=-21.6 EndZ=0
  constraints (24):
    c: Coincident(g0,g1)
    c: Coincident(g1,g2)
    c: Coincident(g2,g3)
    c: Coincident(g3,g0)
    c: Vertical(g0)
    c: Vertical(g2)
    c: Horizontal(g1)
    c: Horizontal(g3)
    c: DistanceX(g-6,g0) = 0
    c: DistanceX(g-7,g2) = 1.5
    c: DistanceY(g1,g-8) = 1.5
    c: DistanceY(g-6,g2) = 1.5
    c: Coincident(g4,g5)
    c: Coincident(g5,g6)
    c: Coincident(g6,g7)
    c: Coincident(g7,g4)
    c: Vertical(g4)
    c: Vertical(g6)
    c: Horizontal(g5)
    c: Horizontal(g7)
    c: DistanceX(g6,g-3) = 0
    c: DistanceX(g-5,g4) = 1.5
    c: DistanceY(g4,g-3) = 1.5
    c: DistanceY(g-4,g4) = 1.5
FEATURE [PartDesign::Pocket] Pocket065
  BaseFeature = -> Pocket064
  Direction = (0,0,-1)
  Length = 1.5
  Length2 = 5
  Profile = -> Sketch166
  ReferenceAxis = -> Sketch166 [N_Axis]
  Refine = true
  Suppressed = false
  Type = 0
FEATURE [Sketcher::SketchObject] Sketch167
  ArcFitTolerance = 1e-06
  AttachmentOffset = pos=(0,0,-1.5) rot=(0,0,1;0rad)
  AttachmentSupport = -> [Pocket065]
  ExternalGeometry = -> [Pocket065]
  FullyConstrained = true
  MakeInternals = false
  MapMode = 5
  Placement = pos=(49.1,0,0) rot=(0.57735,0.57735,0.57735;2.0944rad)
  sketch-geometry (8):
    g0: LineSegment StartX=-24.5 StartY=-13.2 StartZ=0 EndX=-20.4 EndY=-13.2 EndZ=0
    g1: LineSegment StartX=-24.5 StartY=-13.2 StartZ=0 EndX=-24.5 EndY=-14.9439 EndZ=0
    g2: LineSegment StartX=-20.4 StartY=-16.3 StartZ=0 EndX=-20.4 EndY=-13.2 EndZ=0
    g3: LineSegment StartX=-24.5 StartY=-14.9439 StartZ=0 EndX=-20.4 EndY=-16.3 EndZ=0
    g4: LineSegment StartX=-7.5 StartY=-13.2 StartZ=0 EndX=-7.5 EndY=-14.9439 EndZ=0
    g5: LineSegment StartX=-7.5 StartY=-14.9439 StartZ=0 EndX=-11.6 EndY=-16.3 EndZ=0
    g6: LineSegment StartX=-11.6 StartY=-16.3 StartZ=0 EndX=-11.6 EndY=-13.2 EndZ=0
    g7: LineSegment StartX=-11.6 StartY=-13.2 StartZ=0 EndX=-7.5 EndY=-13.2 EndZ=0
  constraints (20):
    c: Coincident(g0,g-7)
    c: PointOnObject(g0,g-9)
    c: Horizontal(g0)
    c: Coincident(g1,g0)
    c: Vertical(g1)
    c: Coincident(g2,g0)
    c: DistanceY(g-4,g1) = 1.5
    c: Coincident(g3,g1)
    c: Coincident(g3,g-13)
    c: Coincident(g2,g3)
    c: Coincident(g4,g-8)
    c: Vertical(g4)
    c: Coincident(g5,g4)
    c: Coincident(g5,g-12)
    c: Coincident(g6,g5)
    c: PointOnObject(g6,g-10)
    c: Coincident(g7,g6)
    c: Coincident(g7,g4)
    c: Horizontal(g7)
    c: DistanceY(g-6,g4) = 1.5
FEATURE [PartDesign::Pocket] Pocket066
  BaseFeature = -> Pocket065
  Direction = (-1,0,0)
  Length = 5.3
  Length2 = 5
  Profile = -> Sketch167
  ReferenceAxis = -> Sketch167 [N_Axis]
  Refine = true
  Suppressed = false
  Type = 0
FEATURE [PartDesign::Pocket] Pocket067
  BaseFeature = -> Pocket066
  Direction = (1,0,0)
  Length = 2
  Length2 = 5
  Profile = -> Pocket066 [Face42,Face43]
  Refine = true
  Suppressed = false
  Type = 0
FEATURE [Sketcher::SketchObject] Sketch168
  ArcFitTolerance = 1e-06
  AttachmentSupport = -> [Pocket067]
  ExternalGeometry = -> [Pocket067]
  FullyConstrained = true
  MakeInternals = false
  MapMode = 5
  Placement = pos=(0,-10.1,0) rot=(0,0.707107,0.707107;3.14159rad)
  sketch-geometry (2):
    g0: ArcOfCircle CenterX=-53.7 CenterY=-13.2 CenterZ=0 NormalX=0 NormalY=0 NormalZ=1 AngleXU=0 Radius=1.5 StartAngle=3.14159 EndAngle=6.28319
    g1: LineSegment StartX=-55.2 StartY=-13.2 StartZ=0 EndX=-52.2 EndY=-13.2 EndZ=0
  constraints (7):
    c: PointOnObject(g0,g-3)
    c: PointOnObject(g0,g-3)
    c: PointOnObject(g0,g-3)
    c: Radius(g0) = 1.5
    c: DistanceX(g-3,g0) = 2.9
    c: Coincident(g1,g0)
    c: Coincident(g1,g0)
FEATURE [PartDesign::Pocket] Pocket068
  BaseFeature = -> Pocket067
  Direction = (0,-1,2e-16)
  Length = 13
  Length2 = 5
  Profile = -> Sketch168
  ReferenceAxis = -> Sketch168 [N_Axis]
  Refine = true
  Suppressed = false
  Type = 0
FEATURE [Sketcher::SketchObject] Sketch169
  ArcFitTolerance = 1e-06
  AttachmentSupport = -> [Pocket068]
  ExternalGeometry = -> [Pocket068]
  FullyConstrained = true
  MakeInternals = false
  MapMode = 5
  Placement = pos=(0,-11.9,0) rot=(1,0,0;1.5708rad)
  sketch-geometry (2):
    g0: ArcOfCircle CenterX=39.55 CenterY=-13.2 CenterZ=0 NormalX=0 NormalY=0 NormalZ=1 AngleXU=0 Radius=1.25 StartAngle=3.14159 EndAngle=6.28319
    g1: LineSegment StartX=40.8 StartY=-13.2 StartZ=0 EndX=38.3 EndY=-13.2 EndZ=0
  constraints (7):
    c: PointOnObject(g0,g-3)
    c: PointOnObject(g0,g-3)
    c: Radius(g0) = 1.25
    c: PointOnObject(g0,g-3)
    c: DistanceX(g-3,g0) = 1.9
    c: Coincident(g1,g0)
    c: Coincident(g1,g0)
FEATURE [PartDesign::Pocket] Pocket069
  BaseFeature = -> Pocket068
  Direction = (0,1,-2e-16)
  Length = 2
  Length2 = 5
  Profile = -> Sketch169
  ReferenceAxis = -> Sketch169 [N_Axis]
  Refine = true
  Suppressed = false
  Type = 0
FEATURE [PartDesign::Pocket] Pocket070
  BaseFeature = -> Pocket069
  Direction = (0,1,-2e-16)
  Length = 10
  Length2 = 5
  Profile = -> Sketch169
  ReferenceAxis = -> Sketch169 [N_Axis]
  Refine = true
  Reversed = true
  Suppressed = false
  Type = 0
FEATURE [Sketcher::SketchObject] Sketch170
  ArcFitTolerance = 1e-06
  AttachmentSupport = -> [Pocket070]
  ExternalGeometry = -> [Pocket070]
  FullyConstrained = true
  MakeInternals = false
  MapMode = 5
  Placement = pos=(0,0,-16.3) rot=(0,0,1;0rad)
  sketch-geometry (2):
    g0: Circle CenterX=46.45 CenterY=-16 CenterZ=0 NormalX=0 NormalY=0 NormalZ=1 AngleXU=0 Radius=3.95
    g1: Circle CenterX=46.45 CenterY=-16 CenterZ=0 NormalX=0 NormalY=0 NormalZ=1 AngleXU=0 Radius=1.00001
  constraints (4):
    c: Coincident(g0,g-3)
    c: Coincident(g1,g0)
    c: Tangent(g1,g-3)
    c: Diameter(g0) = 7.9
FEATURE [PartDesign::Pad] Pad116
  BaseFeature = -> Pocket070
  Direction = (0,0,1)
  Length = 3.1
  Length2 = 10
  Profile = -> Sketch170
  ReferenceAxis = -> Sketch170 [N_Axis]
  Refine = true
  Suppressed = false
  Type = 0
FEATURE [Sketcher::SketchObject] Sketch171
  ArcFitTolerance = 1e-06
  AttachmentSupport = -> [Pad116]
  ExternalGeometry = -> [Pad116]
  FullyConstrained = true
  MakeInternals = false
  MapMode = 5
  Placement = pos=(5.8e-15,0,-13.2) rot=(0,0,1;0rad)
  sketch-geometry (1):
    g0: Circle CenterX=46.45 CenterY=-16 CenterZ=0 NormalX=0 NormalY=0 NormalZ=1 AngleXU=0 Radius=2.4
  constraints (2):
    c: Coincident(g0,g-3)
    c: Diameter(g0) = 4.8
FEATURE [PartDesign::Pocket] Pocket071
  BaseFeature = -> Pad116
  Direction = (0,0,-1)
  Length = 2.05
  Length2 = 5
  Profile = -> Sketch171
  ReferenceAxis = -> Sketch171 [N_Axis]
  Refine = true
  Suppressed = false
  Type = 0
FEATURE [PartDesign::Body] Body006  label="Front_Cover"
  AllowCompound = false
  Group = -> [Binder003,Sketch155,Pad114,Sketch156,Pocket055,Sketch157,Pocket056,Sketch158,Pocket057,Sketch159,Pocket058,Sketch160,Pocket059,Sketch161,Pocket060,Sketch162,Pad115,Pocket061,Sketch163,Pocket062,Sketch164,Pocket063,Sketch165,Pocket064,Sketch166,Pocket065,Sketch167,Pocket066,Pocket067,Sketch168,Pocket068,Sketch169,Pocket069,Pocket070,Sketch170,Pad116,Sketch171,Pocket071]
  Origin = -> Origin006
  Tip = -> Pocket071
FEATURE [Sketcher::SketchObject] Sketch172
  ArcFitTolerance = 1e-06
  AttachmentSupport = -> [XY_Plane007]
  FullyConstrained = true
  MakeInternals = false
  MapMode = 5
  sketch-geometry (9):
    g0: LineSegment StartX=0 StartY=0 StartZ=0 EndX=18 EndY=0 EndZ=0
    g1: LineSegment StartX=18 StartY=0 StartZ=0 EndX=18 EndY=1.3 EndZ=0
    g2: LineSegment StartX=18 StartY=1.3 StartZ=0 EndX=23 EndY=1.3 EndZ=0
    g3: LineSegment StartX=23 StartY=1.3 StartZ=0 EndX=23 EndY=4.2 EndZ=0
    g4: LineSegment StartX=23 StartY=4.2 StartZ=0 EndX=16 EndY=4.2 EndZ=0
    g5: LineSegment StartX=16 StartY=4.2 StartZ=0 EndX=16 EndY=5 EndZ=0
    g6: LineSegment StartX=16 StartY=5 StartZ=0 EndX=6 EndY=2.5 EndZ=0
    g7: LineSegment StartX=6 StartY=2.5 StartZ=0 EndX=0 EndY=2.5 EndZ=0
    g8: LineSegment StartX=0 StartY=2.5 StartZ=0 EndX=0 EndY=0 EndZ=0
  constraints (27):
    c: Coincident(g0,g-1)
    c: PointOnObject(g0,g-1)
    c: Coincident(g1,g0)
    c: Vertical(g1)
    c: DistanceX(g0,g0) = 18
    c: Coincident(g2,g1)
    c: Horizontal(g2)
    c: Coincident(g3,g2)
    c: Vertical(g3)
    c: Coincident(g4,g3)
    c: Horizontal(g4)
    c: Coincident(g5,g4)
    c: Vertical(g5)
    c: Coincident(g6,g5)
    c: Coincident(g7,g6)
    c: PointOnObject(g7,g-2)
    c: Horizontal(g7)
    c: Coincident(g8,g7)
    c: Coincident(g8,g0)
    c: DistanceX(g7,g3) = 23
    c: DistanceX(g4,g4) = 7
    c: DistanceY(g3,g3) = 2.9
    c: DistanceX(g2,g2) = 5
    c: DistanceY(g1,g1) = 1.3
    c: DistanceY(g0,g5) = 5
    c: DistanceY(g8,g8) = 2.5
    c: DistanceX(g7,g7) = 6
FEATURE [PartDesign::Pad] Pad117
  Direction = (0,0,1)
  Length = 7.9
  Length2 = 10
  Profile = -> Sketch172
  ReferenceAxis = -> Sketch172 [N_Axis]
  Refine = true
  Suppressed = false
  Type = 0
FEATURE [Sketcher::SketchObject] Sketch173
  ArcFitTolerance = 1e-06
  AttachmentSupport = -> [Pad117]
  ExternalGeometry = -> [Pad117]
  FullyConstrained = true
  MakeInternals = false
  MapMode = 5
  Placement = pos=(23,0,0) rot=(0.57735,0.57735,0.57735;2.0944rad)
  sketch-geometry (8):
    g0: LineSegment StartX=1.3 StartY=0 StartZ=0 EndX=4.2 EndY=0 EndZ=0
    g1: LineSegment StartX=4.2 StartY=0 StartZ=0 EndX=4.2 EndY=1 EndZ=0
    g2: LineSegment StartX=4.2 StartY=1 StartZ=0 EndX=1.3 EndY=1 EndZ=0
    g3: LineSegment StartX=1.3 StartY=1 StartZ=0 EndX=1.3 EndY=0 EndZ=0
    g4: LineSegment StartX=1.3 StartY=7.9 StartZ=0 EndX=1.3 EndY=6.9 EndZ=0
    g5: LineSegment StartX=1.3 StartY=6.9 StartZ=0 EndX=4.2 EndY=6.9 EndZ=0
    g6: LineSegment StartX=4.2 StartY=6.9 StartZ=0 EndX=4.2 EndY=7.9 EndZ=0
    g7: LineSegment StartX=4.2 StartY=7.9 StartZ=0 EndX=1.3 EndY=7.9 EndZ=0
  constraints (22):
    c: Coincident(g0,g1)
    c: Coincident(g1,g2)
    c: Coincident(g2,g3)
    c: Coincident(g3,g0)
    c: Horizontal(g0)
    c: Horizontal(g2)
    c: Vertical(g1)
    c: Vertical(g3)
    c: Coincident(g0,g-6)
    c: PointOnObject(g1,g-3)
    c: Coincident(g4,g5)
    c: Coincident(g5,g6)
    c: Coincident(g6,g7)
    c: Coincident(g7,g4)
    c: Vertical(g4)
    c: Vertical(g6)
    c: Horizontal(g5)
    c: Horizontal(g7)
    c: Coincident(g4,g-5)
    c: PointOnObject(g5,g-3)
    c: DistanceY(g4,g4) = 1
    c: DistanceY(g3,g3) = 1
FEATURE [PartDesign::Pocket] Pocket072
  BaseFeature = -> Pad117
  Direction = (-1,0,0)
  Length = 7
  Length2 = 5
  Profile = -> Sketch173
  ReferenceAxis = -> Sketch173 [N_Axis]
  Refine = true
  Suppressed = false
  Type = 0
FEATURE [PartDesign::Pocket] Pocket073
  BaseFeature = -> Pocket072
  Direction = (0,-1,0)
  Length = 5
  Length2 = 5
  Profile = -> Pocket072 [Face9,Face7]
  Refine = true
  Suppressed = false
  Type = 0
FEATURE [Sketcher::SketchObject] Sketch174
  ArcFitTolerance = 1e-06
  AttachmentSupport = -> [Pocket073]
  ExternalGeometry = -> [Pocket073]
  FullyConstrained = true
  MakeInternals = false
  MapMode = 5
  Placement = pos=(0,0,7.9) rot=(0,0,1;0rad)
  sketch-geometry (1):
    g0: Circle CenterX=0 CenterY=0 CenterZ=0 NormalX=0 NormalY=0 NormalZ=1 AngleXU=0 Radius=1.25
  constraints (2):
    c: Coincident(g0,g-1)
    c: Radius(g0) = 1.25
FEATURE [PartDesign::Pad] Pad118
  BaseFeature = -> Pocket073
  Direction = (0,0,1)
  Length = 2
  Length2 = 10
  Profile = -> Sketch174
  ReferenceAxis = -> Sketch174 [N_Axis]
  Refine = true
  Suppressed = false
  Type = 0
FEATURE [PartDesign::Pad] Pad119
  BaseFeature = -> Pad118
  Direction = (0,0,1)
  Length = 9.9
  Length2 = 10
  Profile = -> Sketch174
  ReferenceAxis = -> Sketch174 [N_Axis]
  Refine = true
  Reversed = true
  Suppressed = false
  Type = 0
FEATURE [PartDesign::Pad] Pad120
  BaseFeature = -> Pad119
  Direction = (0,0,-1)
  Length = 0.15
  Length2 = 10
  Profile = -> Pad119 [Face9]
  Refine = true
  Suppressed = false
  Type = 0
FEATURE [PartDesign::Pad] Pad121
  BaseFeature = -> Pad120
  Direction = (0,0,1)
  Length = 0.15
  Length2 = 10
  Profile = -> Pad120 [Face1]
  Refine = true
  Suppressed = false
  Type = 0
FEATURE [Sketcher::SketchObject] Sketch175
  ArcFitTolerance = 1e-06
  AttachmentSupport = -> [Pad121]
  ExternalGeometry = -> [Pad121]
  FullyConstrained = true
  MakeInternals = false
  MapMode = 5
  Placement = pos=(0,0,0) rot=(1,0,0;1.5708rad)
  sketch-geometry (4):
    g0: LineSegment StartX=18 StartY=1 StartZ=0 EndX=18 EndY=6.9 EndZ=0
    g1: LineSegment StartX=18 StartY=6.9 StartZ=0 EndX=16 EndY=6.9 EndZ=0
    g2: LineSegment StartX=16 StartY=6.9 StartZ=0 EndX=16 EndY=1 EndZ=0
    g3: LineSegment StartX=16 StartY=1 StartZ=0 EndX=18 EndY=1 EndZ=0
  constraints (10):
    c: Coincident(g0,g1)
    c: Coincident(g1,g2)
    c: Coincident(g2,g3)
    c: Coincident(g3,g0)
    c: Vertical(g0)
    c: Vertical(g2)
    c: Horizontal(g1)
    c: Horizontal(g3)
    c: Coincident(g0,g-5)
    c: Coincident(g1,g-3)
FEATURE [PartDesign::Pocket] Pocket074
  BaseFeature = -> Pad121
  Direction = (0,1,-2e-16)
  Length = 0.3
  Length2 = 5
  Profile = -> Sketch175
  ReferenceAxis = -> Sketch175 [N_Axis]
  Refine = true
  Suppressed = false
  Type = 0
FEATURE [Sketcher::SketchObject] Sketch176
  ArcFitTolerance = 1e-06
  AttachmentSupport = -> [XY_Plane008]
  FullyConstrained = true
  MakeInternals = false
  MapMode = 5
  sketch-geometry (1):
    g0: Circle CenterX=0 CenterY=0 CenterZ=0 NormalX=0 NormalY=0 NormalZ=1 AngleXU=0 Radius=1.5
  constraints (2):
    c: Coincident(g0,g-1)
    c: Radius(g0) = 1.5
FEATURE [PartDesign::Pad] Pad122
  Direction = (0,0,1)
  Length = 11.8
  Length2 = 10
  Profile = -> Sketch176
  ReferenceAxis = -> Sketch176 [N_Axis]
  Refine = true
  Suppressed = false
  Type = 0
FEATURE [Sketcher::SketchObject] Sketch177
  ArcFitTolerance = 1e-06
  AttachmentSupport = -> [Pad122]
  ExternalGeometry = -> [Pad122]
  FullyConstrained = true
  MakeInternals = false
  MapMode = 5
  Placement = pos=(0,0,0) rot=(1,0,0;3.14159rad)
  sketch-geometry (1):
    g0: Circle CenterX=0 CenterY=0 CenterZ=0 NormalX=0 NormalY=0 NormalZ=1 AngleXU=0 Radius=2.95
  constraints (2):
    c: Coincident(g0,g-1)
    c: Diameter(g0) = 5.9
FEATURE [PartDesign::Pad] Pad123
  BaseFeature = -> Pad122
  Direction = (0,0,-1)
  Length = 4
  Length2 = 10
  Profile = -> Sketch177
  ReferenceAxis = -> Sketch177 [N_Axis]
  Refine = true
  Suppressed = false
  Type = 0
FEATURE [Sketcher::SketchObject] Sketch178
  ArcFitTolerance = 1e-06
  AttachmentSupport = -> [Pad123]
  ExternalGeometry = -> [Pad123]
  FullyConstrained = true
  MakeInternals = false
  MapMode = 5
  Placement = pos=(0,0,11.8) rot=(0,0,1;0rad)
  sketch-geometry (1):
    g0: Circle CenterX=0 CenterY=0 CenterZ=0 NormalX=0 NormalY=0 NormalZ=1 AngleXU=0 Radius=2.95
  constraints (2):
    c: Coincident(g0,g-1)
    c: Diameter(g0) = 5.9
FEATURE [PartDesign::Pad] Pad124
  BaseFeature = -> Pad123
  Direction = (0,0,1)
  Length = 4
  Length2 = 10
  Profile = -> Sketch178
  ReferenceAxis = -> Sketch178 [N_Axis]
  Refine = true
  Suppressed = false
  Type = 0
FEATURE [Sketcher::SketchObject] Sketch179
  ArcFitTolerance = 1e-06
  AttachmentSupport = -> [Pad124]
  ExternalGeometry = -> [Pad124]
  FullyConstrained = true
  MakeInternals = false
  MapMode = 5
  Placement = pos=(0,0,15.8) rot=(0,0,1;0rad)
  sketch-geometry (6):
    g0: ArcOfCircle CenterX=0 CenterY=0 CenterZ=0 NormalX=0 NormalY=0 NormalZ=1 AngleXU=0 Radius=2.94999 StartAngle=4.71239 EndAngle=7.85398
    g1: ArcOfCircle CenterX=-6.30001 CenterY=2e-16 CenterZ=0 NormalX=0 NormalY=0 NormalZ=1 AngleXU=0 Radius=2.94999 StartAngle=1.5708 EndAngle=4.71239
    g2: LineSegment StartX=-5e-16 StartY=-2.94999 StartZ=0 EndX=-6.30001 EndY=-2.94999 EndZ=0
    g3: LineSegment StartX=9e-16 StartY=2.94999 StartZ=0 EndX=-6.30001 EndY=2.94999 EndZ=0
    g4: LineSegment [constr] StartX=-6.30001 StartY=2e-16 StartZ=0 EndX=-9.25001 EndY=2e-16 EndZ=0
    g5: LineSegment [constr] StartX=0 StartY=0 StartZ=0 EndX=2.94999 EndY=0 EndZ=0
  constraints (15):
    c: Tangent(g0,g2) = 1.5708
    c: Tangent(g0,g3) = -1.5708
    c: Tangent(g1,g2) = 1.5708
    c: Tangent(g1,g3) = -1.5708
    c: Equal(g0,g1)
    c: Horizontal(g3)
    c: Coincident(g0,g-1)
    c: Tangent(g0,g-3)
    c: Coincident(g4,g1)
    c: PointOnObject(g4,g1)
    c: Horizontal(g4)
    c: Coincident(g5,g0)
    c: PointOnObject(g5,g0)
    c: Horizontal(g5)
    c: DistanceX(g4,g5) = 12.2
FEATURE [PartDesign::Pad] Pad125
  BaseFeature = -> Pad124
  Direction = (0,0,1)
  Length = 2
  Length2 = 10
  Profile = -> Sketch179
  ReferenceAxis = -> Sketch179 [N_Axis]
  Refine = true
  Reversed = true
  Suppressed = false
  Type = 0
FEATURE [Sketcher::SketchObject] Sketch180
  ArcFitTolerance = 1e-06
  AttachmentSupport = -> [Pad125]
  ExternalGeometry = -> [Pad125]
  FullyConstrained = true
  MakeInternals = false
  MapMode = 5
  Placement = pos=(0,0,-4) rot=(1,0,0;3.14159rad)
  sketch-geometry (4):
    g0: ArcOfCircle CenterX=0 CenterY=0 CenterZ=0 NormalX=0 NormalY=0 NormalZ=1 AngleXU=0 Radius=2.95 StartAngle=4.71239 EndAngle=7.85398
    g1: ArcOfCircle CenterX=-6.30002 CenterY=1e-16 CenterZ=0 NormalX=0 NormalY=0 NormalZ=1 AngleXU=0 Radius=2.95 StartAngle=1.5708 EndAngle=4.71239
    g2: LineSegment StartX=-5e-16 StartY=-2.95 StartZ=0 EndX=-6.30002 EndY=-2.95 EndZ=0
    g3: LineSegment StartX=9e-16 StartY=2.95 StartZ=0 EndX=-6.30002 EndY=2.95 EndZ=0
  constraints (9):
    c: Tangent(g0,g2) = 1.5708
    c: Tangent(g0,g3) = -1.5708
    c: Tangent(g1,g2) = 1.5708
    c: Tangent(g1,g3) = -1.5708
    c: Equal(g0,g1)
    c: Horizontal(g3)
    c: Coincident(g0,g-1)
    c: Tangent(g0,g-3)
    c: Tangent(g1,g-4)
FEATURE [PartDesign::Pad] Pad126
  BaseFeature = -> Pad125
  Direction = (0,0,-1)
  Length = 2
  Length2 = 10
  Profile = -> Sketch180
  ReferenceAxis = -> Sketch180 [N_Axis]
  Refine = true
  Reversed = true
  Suppressed = false
  Type = 0
FEATURE [Sketcher::SketchObject] Sketch181
  ArcFitTolerance = 1e-06
  AttachmentSupport = -> [Pad126]
  ExternalGeometry = -> [Pad126]
  FullyConstrained = true
  MakeInternals = false
  MapMode = 5
  Placement = pos=(0,0,-4) rot=(1,0,0;3.14159rad)
  sketch-geometry (1):
    g0: Circle CenterX=-6.30002 CenterY=0 CenterZ=0 NormalX=0 NormalY=0 NormalZ=1 AngleXU=0 Radius=1.45
  constraints (2):
    c: Coincident(g0,g-3)
    c: Diameter(g0) = 2.9
FEATURE [PartDesign::Pad] Pad127
  BaseFeature = -> Pad126
  Direction = (0,0,-1)
  Length = 2.1
  Length2 = 10
  Profile = -> Sketch181
  ReferenceAxis = -> Sketch181 [N_Axis]
  Refine = true
  Suppressed = false
  Type = 0
FEATURE [Sketcher::SketchObject] Sketch182
  ArcFitTolerance = 1e-06
  AttachmentSupport = -> [Pad127]
  ExternalGeometry = -> [Pad127]
  FullyConstrained = true
  MakeInternals = false
  MapMode = 5
  Placement = pos=(0,0,15.8) rot=(0,0,1;0rad)
  sketch-geometry (1):
    g0: Circle CenterX=-6.30001 CenterY=0 CenterZ=0 NormalX=0 NormalY=0 NormalZ=1 AngleXU=0 Radius=1.45
  constraints (2):
    c: Coincident(g0,g-3)
    c: Diameter(g0) = 2.9
FEATURE [PartDesign::Pad] Pad128
  BaseFeature = -> Pad127
  Direction = (0,0,1)
  Length = 2.1
  Length2 = 10
  Profile = -> Sketch182
  ReferenceAxis = -> Sketch182 [N_Axis]
  Refine = true
  Suppressed = false
  Type = 0
FEATURE [Sketcher::SketchObject] Sketch183
  ArcFitTolerance = 1e-06
  AttachmentSupport = -> [Pad128]
  ExternalGeometry = -> [Pad128]
  FullyConstrained = true
  MakeInternals = false
  MapMode = 5
  Placement = pos=(0,0,17.9) rot=(0,0,1;0rad)
  sketch-geometry (4):
    g0: LineSegment StartX=-9.40001 StartY=1.6 StartZ=0 EndX=-9.40001 EndY=-1.6 EndZ=0
    g1: LineSegment StartX=-9.40001 StartY=-1.6 StartZ=0 EndX=-3.20001 EndY=-1.6 EndZ=0
    g2: LineSegment StartX=-3.20001 StartY=-1.6 StartZ=0 EndX=-3.20001 EndY=1.6 EndZ=0
    g3: LineSegment StartX=-3.20001 StartY=1.6 StartZ=0 EndX=-9.40001 EndY=1.6 EndZ=0
  constraints (12):
    c: Coincident(g0,g1)
    c: Coincident(g1,g2)
    c: Coincident(g2,g3)
    c: Coincident(g3,g0)
    c: Vertical(g0)
    c: Vertical(g2)
    c: Horizontal(g1)
    c: Horizontal(g3)
    c: DistanceX(g3,g3) = 6.2
    c: DistanceY(g0,g0) = 3.2
    c: DistanceY(g-3,g2) = 1.6
    c: DistanceX(g-3,g2) = 3.1
FEATURE [PartDesign::Pad] Pad129
  BaseFeature = -> Pad128
  Direction = (0,0,1)
  Length = 2.7
  Length2 = 10
  Profile = -> Sketch183
  ReferenceAxis = -> Sketch183 [N_Axis]
  Refine = true
  Suppressed = false
  Type = 0
FEATURE [Sketcher::SketchObject] Sketch184
  ArcFitTolerance = 1e-06
  AttachmentSupport = -> [Pad129]
  ExternalGeometry = -> [Pad129]
  FullyConstrained = true
  MakeInternals = false
  MapMode = 5
  Placement = pos=(0,0,-6.1) rot=(1,0,0;3.14159rad)
  sketch-geometry (4):
    g0: LineSegment StartX=-9.40001 StartY=1.6 StartZ=0 EndX=-9.40001 EndY=-1.6 EndZ=0
    g1: LineSegment StartX=-9.40001 StartY=-1.6 StartZ=0 EndX=-3.20001 EndY=-1.6 EndZ=0
    g2: LineSegment StartX=-3.20001 StartY=-1.6 StartZ=0 EndX=-3.20001 EndY=1.6 EndZ=0
    g3: LineSegment StartX=-3.20001 StartY=1.6 StartZ=0 EndX=-9.40001 EndY=1.6 EndZ=0
  constraints (9):
    c: Coincident(g0,g1)
    c: Coincident(g1,g2)
    c: Coincident(g2,g3)
    c: Coincident(g3,g0)
    c: Vertical(g0)
    c: Horizontal(g1)
    c: Coincident(g0,g-5)
    c: Coincident(g2,g-5)
    c: Coincident(g1,g-6)
FEATURE [PartDesign::Pad] Pad130
  BaseFeature = -> Pad129
  Direction = (0,0,-1)
  Length = 2.7
  Length2 = 10
  Profile = -> Sketch184
  ReferenceAxis = -> Sketch184 [N_Axis]
  Refine = true
  Suppressed = false
  Type = 0
FEATURE [Sketcher::SketchObject] Sketch185
  ArcFitTolerance = 1e-06
  AttachmentOffset = pos=(0,0,4.7) rot=(0,0,1;0rad)
  AttachmentSupport = -> [Pad130]
  ExternalGeometry = -> [Pad130]
  FullyConstrained = true
  MakeInternals = false
  MapMode = 5
  Placement = pos=(1.49999,0,0) rot=(0.57735,0.57735,0.57735;2.0944rad)
  sketch-geometry (4):
    g0: LineSegment StartX=-3 StartY=8.4 StartZ=0 EndX=-3 EndY=3.4 EndZ=0
    g1: LineSegment StartX=-3 StartY=3.4 StartZ=0 EndX=3 EndY=3.4 EndZ=0
    g2: LineSegment StartX=3 StartY=3.4 StartZ=0 EndX=3 EndY=8.4 EndZ=0
    g3: LineSegment StartX=3 StartY=8.4 StartZ=0 EndX=-3 EndY=8.4 EndZ=0
  constraints (12):
    c: Coincident(g0,g1)
    c: Coincident(g1,g2)
    c: Coincident(g2,g3)
    c: Coincident(g3,g0)
    c: Vertical(g0)
    c: Vertical(g2)
    c: Horizontal(g1)
    c: Horizontal(g3)
    c: DistanceX(g3,g3) = 6
    c: DistanceX(g-1,g1) = 3
    c: DistanceY(g2,g-3) = 3.4
    c: DistanceY(g-4,g1) = 3.4
FEATURE [PartDesign::Pocket] Pocket075
  BaseFeature = -> Pad130
  Direction = (-1,0,0)
  Length = 0.1
  Length2 = 5
  Profile = -> Sketch185
  ReferenceAxis = -> Sketch185 [N_Axis]
  Refine = true
  Suppressed = false
  Type = 0
FEATURE [Sketcher::SketchObject] Sketch186
  ArcFitTolerance = 1e-06
  AttachmentOffset = pos=(0,0,-7.9) rot=(0,0,1;0rad)
  AttachmentSupport = -> [Pocket075]
  ExternalGeometry = -> [Pocket075]
  FullyConstrained = true
  MakeInternals = false
  MapMode = 5
  Placement = pos=(-1.50001,0,0) rot=(0.57735,-0.57735,-0.57735;2.0944rad)
  sketch-geometry (4):
    g0: LineSegment StartX=-3 StartY=9.4 StartZ=0 EndX=-3 EndY=3.4 EndZ=0
    g1: LineSegment StartX=-3 StartY=3.4 StartZ=0 EndX=3 EndY=3.4 EndZ=0
    g2: LineSegment StartX=3 StartY=3.4 StartZ=0 EndX=3 EndY=9.4 EndZ=0
    g3: LineSegment StartX=3 StartY=9.4 StartZ=0 EndX=-3 EndY=9.4 EndZ=0
  constraints (12):
    c: Coincident(g0,g1)
    c: Coincident(g1,g2)
    c: Coincident(g2,g3)
    c: Coincident(g3,g0)
    c: Vertical(g0)
    c: Vertical(g2)
    c: Horizontal(g1)
    c: Horizontal(g3)
    c: DistanceX(g3,g3) = 6
    c: DistanceX(g-1,g1) = 3
    c: DistanceY(g2,g-4) = 2.4
    c: DistanceY(g-3,g1) = 3.4
FEATURE [PartDesign::Pocket] Pocket076
  BaseFeature = -> Pocket075
  Direction = (1,0,0)
  Length = 0.1
  Length2 = 5
  Profile = -> Sketch186
  ReferenceAxis = -> Sketch186 [N_Axis]
  Refine = true
  Suppressed = false
  Type = 0
FEATURE [PartDesign::Body] Body008  label="Waist"
  AllowCompound = false
  Group = -> [Sketch176,Pad122,Sketch177,Pad123,Sketch178,Pad124,Sketch179,Pad125,Sketch180,Pad126,Sketch181,Pad127,Sketch182,Pad128,Sketch183,Pad129,Sketch184,Pad130,Sketch185,Pocket075,Sketch186,Pocket076]
  Origin = -> Origin008
  Placement = pos=(53.7,-21.9,-13.2) rot=(0.58,0.58,0.58;4.18879rad)
  Tip = -> Pocket076
FEATURE [PartDesign::SubShapeBinder] Binder004
  BindCopyOnChange = 0
  BindMode = 2
  ClaimChildren = false
  Context = -> Body009 [Binder004.]
  Fuse = false
  MakeFace = true
  OffsetFill = false
  OffsetIntersection = false
  OffsetJoinType = 0
  OffsetOpenResult = false
  PartialLoad = false
  Refine = true
  Relative = true
  _Version = 2
FEATURE [Sketcher::SketchObject] Sketch187
  ArcFitTolerance = 1e-06
  AttachmentSupport = -> [Binder004]
  ExternalGeometry = -> [Binder004]
  FullyConstrained = true
  MakeInternals = false
  MapMode = 5
  Placement = pos=(0,-26,0) rot=(1,0,0;1.5708rad)
  sketch-geometry (4):
    g0: LineSegment StartX=2 StartY=-0.05 StartZ=0 EndX=2 EndY=-8.15 EndZ=0
    g1: LineSegment StartX=2 StartY=-8.15 StartZ=0 EndX=38.5 EndY=-8.15 EndZ=0
    g2: LineSegment StartX=38.5 StartY=-8.15 StartZ=0 EndX=38.5 EndY=-0.05 EndZ=0
    g3: LineSegment StartX=38.5 StartY=-0.05 StartZ=0 EndX=2 EndY=-0.05 EndZ=0
  constraints (12):
    c: PointOnObject(g0,g-4)
    c: PointOnObject(g0,g-4)
    c: Coincident(g1,g0)
    c: PointOnObject(g1,g-6)
    c: Horizontal(g1)
    c: Coincident(g2,g1)
    c: PointOnObject(g2,g-6)
    c: Coincident(g3,g2)
    c: Coincident(g3,g0)
    c: Horizontal(g3)
    c: DistanceY(g0,g-3) = 0.05
    c: DistanceY(g-5,g0) = 0.05
FEATURE [PartDesign::Pad] Pad131
  Direction = (0,-1,2e-16)
  Length = 6
  Length2 = 10
  Profile = -> Sketch187
  ReferenceAxis = -> Sketch187 [N_Axis]
  Refine = true
  Suppressed = false
  Type = 0
FEATURE [Sketcher::SketchObject] Sketch188
  ArcFitTolerance = 1e-06
  AttachmentSupport = -> [Pad131]
  ExternalGeometry = -> [Pad131]
  FullyConstrained = true
  MakeInternals = false
  MapMode = 5
  Placement = pos=(0,-32,1.41e-14) rot=(1,0,0;1.5708rad)
  sketch-geometry (10):
    g0: LineSegment [constr] StartX=14.1667 StartY=-0.05 StartZ=0 EndX=14.1667 EndY=-8.15 EndZ=0
    g1: LineSegment [constr] StartX=26.3333 StartY=-0.05 StartZ=0 EndX=26.3333 EndY=-8.15 EndZ=0
    g2: LineSegment StartX=14.4167 StartY=-0.05 StartZ=0 EndX=13.9167 EndY=-0.05 EndZ=0
    g3: LineSegment StartX=13.9167 StartY=-0.05 StartZ=0 EndX=13.9167 EndY=-8.15 EndZ=0
    g4: LineSegment StartX=13.9167 StartY=-8.15 StartZ=0 EndX=14.4167 EndY=-8.15 EndZ=0
    g5: LineSegment StartX=14.4167 StartY=-8.15 StartZ=0 EndX=14.4167 EndY=-0.05 EndZ=0
    g6: LineSegment StartX=26.5833 StartY=-0.05 StartZ=0 EndX=26.0833 EndY=-0.05 EndZ=0
    g7: LineSegment StartX=26.0833 StartY=-0.05 StartZ=0 EndX=26.0833 EndY=-8.15 EndZ=0
    g8: LineSegment StartX=26.0833 StartY=-8.15 StartZ=0 EndX=26.5833 EndY=-8.15 EndZ=0
    g9: LineSegment StartX=26.5833 StartY=-8.15 StartZ=0 EndX=26.5833 EndY=-0.05 EndZ=0
  constraints (33):
    c: DistanceX(g-3,g-3) = 36.5
    c: PointOnObject(g0,g-3)
    c: PointOnObject(g0,g-4)
    c: Vertical(g0)
    c: PointOnObject(g1,g-3)
    c: PointOnObject(g1,g-4)
    c: Vertical(g1)
    c: DistanceX(g-5,g0) = 12.1667
    c: DistanceX(g1,g-6) = 12.1667
    c: Coincident(g2,g3)
    c: Coincident(g3,g4)
    c: Coincident(g4,g5)
    c: Coincident(g5,g2)
    c: Horizontal(g2)
    c: Horizontal(g4)
    c: Vertical(g3)
    c: Vertical(g5)
    c: PointOnObject(g2,g-3)
    c: PointOnObject(g3,g-4)
    c: Coincident(g6,g7)
    c: Coincident(g7,g8)
    c: Coincident(g8,g9)
    c: Coincident(g9,g6)
    c: Horizontal(g6)
    c: Horizontal(g8)
    c: Vertical(g7)
    c: Vertical(g9)
    c: PointOnObject(g6,g-3)
    c: PointOnObject(g7,g-4)
    c: DistanceX(g7,g1) = 0.25
    c: DistanceX(g1,g8) = 0.25
    c: DistanceX(g0,g4) = 0.25
    c: DistanceX(g3,g0) = 0.25
FEATURE [PartDesign::Pocket] Pocket077
  BaseFeature = -> Pad131
  Direction = (0,1,-2e-16)
  Length = 0.3
  Length2 = 5
  Profile = -> Sketch188
  ReferenceAxis = -> Sketch188 [N_Axis]
  Refine = true
  Suppressed = false
  Type = 0
FEATURE [Sketcher::SketchObject] Sketch189
  ArcFitTolerance = 1e-06
  AttachmentSupport = -> [Pocket077]
  ExternalGeometry = -> [Pocket077]
  FullyConstrained = true
  MakeInternals = false
  MapMode = 5
  Placement = pos=(0,-1.8e-15,-8.15) rot=(1,0,0;3.14159rad)
  sketch-geometry (4):
    g0: LineSegment StartX=2 StartY=30 StartZ=0 EndX=4 EndY=30 EndZ=0
    g1: LineSegment StartX=4 StartY=30 StartZ=0 EndX=4 EndY=26 EndZ=0
    g2: LineSegment StartX=4 StartY=26 StartZ=0 EndX=2 EndY=26 EndZ=0
    g3: LineSegment StartX=2 StartY=26 StartZ=0 EndX=2 EndY=30 EndZ=0
  constraints (11):
    c: PointOnObject(g0,g-3)
    c: Horizontal(g0)
    c: Coincident(g1,g0)
    c: PointOnObject(g1,g-4)
    c: Vertical(g1)
    c: Coincident(g2,g1)
    c: Coincident(g2,g-4)
    c: Coincident(g3,g2)
    c: Coincident(g3,g0)
    c: DistanceY(g0,g-3) = 2
    c: DistanceX(g0,g0) = 2
FEATURE [PartDesign::Pocket] Pocket078
  BaseFeature = -> Pocket077
  Direction = (0,0,1)
  Length = 9
  Length2 = 5
  Profile = -> Sketch189
  ReferenceAxis = -> Sketch189 [N_Axis]
  Refine = true
  Suppressed = false
  Type = 0
FEATURE [Sketcher::SketchObject] Sketch190
  ArcFitTolerance = 1e-06
  AttachmentSupport = -> [Pocket078]
  ExternalGeometry = -> [Pocket078]
  FullyConstrained = true
  MakeInternals = false
  MapMode = 5
  Placement = pos=(0,-1.8e-15,-8.15) rot=(1,0,0;3.14159rad)
  sketch-geometry (8):
    g0: LineSegment StartX=13.9167 StartY=31.7 StartZ=0 EndX=13.9167 EndY=26 EndZ=0
    g1: LineSegment StartX=13.9167 StartY=26 StartZ=0 EndX=14.4167 EndY=26 EndZ=0
    g2: LineSegment StartX=14.4167 StartY=26 StartZ=0 EndX=14.4167 EndY=31.7 EndZ=0
    g3: LineSegment StartX=14.4167 StartY=31.7 StartZ=0 EndX=13.9167 EndY=31.7 EndZ=0
    g4: LineSegment StartX=26.5833 StartY=31.7 StartZ=0 EndX=26.0833 EndY=31.7 EndZ=0
    g5: LineSegment StartX=26.0833 StartY=31.7 StartZ=0 EndX=26.0833 EndY=26 EndZ=0
    g6: LineSegment StartX=26.0833 StartY=26 StartZ=0 EndX=26.5833 EndY=26 EndZ=0
    g7: LineSegment StartX=26.5833 StartY=26 StartZ=0 EndX=26.5833 EndY=31.7 EndZ=0
  constraints (20):
    c: Coincident(g0,g1)
    c: Coincident(g1,g2)
    c: Coincident(g2,g3)
    c: Coincident(g3,g0)
    c: Vertical(g0)
    c: Vertical(g2)
    c: Horizontal(g1)
    c: Coincident(g0,g-4)
    c: PointOnObject(g1,g-3)
    c: Coincident(g2,g-4)
    c: Coincident(g4,g5)
    c: Coincident(g5,g6)
    c: Coincident(g6,g7)
    c: Coincident(g7,g4)
    c: Horizontal(g6)
    c: Vertical(g5)
    c: Vertical(g7)
    c: Coincident(g4,g-5)
    c: PointOnObject(g5,g-3)
    c: Coincident(g4,g-6)
FEATURE [PartDesign::Pocket] Pocket079
  BaseFeature = -> Pocket078
  Direction = (0,0,1)
  Length = 0.3
  Length2 = 5
  Profile = -> Sketch190
  ReferenceAxis = -> Sketch190 [N_Axis]
  Refine = true
  Suppressed = false
  Type = 0
FEATURE [Sketcher::SketchObject] Sketch191
  ArcFitTolerance = 1e-06
  AttachmentSupport = -> [Pocket079]
  ExternalGeometry = -> [Pocket079]
  FullyConstrained = true
  MakeInternals = false
  MapMode = 5
  Placement = pos=(0,-26,1.14e-14) rot=(0,0.707107,0.707107;3.14159rad)
  sketch-geometry (8):
    g0: LineSegment StartX=-26.5833 StartY=-7.85 StartZ=0 EndX=-26.0833 EndY=-7.85 EndZ=0
    g1: LineSegment StartX=-26.0833 StartY=-7.85 StartZ=0 EndX=-26.0833 EndY=-0.05 EndZ=0
    g2: LineSegment StartX=-26.0833 StartY=-0.05 StartZ=0 EndX=-26.5833 EndY=-0.05 EndZ=0
    g3: LineSegment StartX=-26.5833 StartY=-0.05 StartZ=0 EndX=-26.5833 EndY=-7.85 EndZ=0
    g4: LineSegment StartX=-13.9167 StartY=-7.85 StartZ=0 EndX=-13.9167 EndY=-0.05 EndZ=0
    g5: LineSegment StartX=-13.9167 StartY=-0.05 StartZ=0 EndX=-14.4167 EndY=-0.05 EndZ=0
    g6: LineSegment StartX=-14.4167 StartY=-0.05 StartZ=0 EndX=-14.4167 EndY=-7.85 EndZ=0
    g7: LineSegment StartX=-14.4167 StartY=-7.85 StartZ=0 EndX=-13.9167 EndY=-7.85 EndZ=0
  constraints (20):
    c: Coincident(g0,g1)
    c: Coincident(g1,g2)
    c: Coincident(g2,g3)
    c: Coincident(g3,g0)
    c: Horizontal(g2)
    c: Vertical(g1)
    c: Vertical(g3)
    c: Coincident(g0,g-5)
    c: PointOnObject(g1,g-3)
    c: Coincident(g4,g5)
    c: Coincident(g5,g6)
    c: Coincident(g6,g7)
    c: Coincident(g7,g4)
    c: Vertical(g4)
    c: Vertical(g6)
    c: Horizontal(g5)
    c: Coincident(g4,g-4)
    c: PointOnObject(g5,g-3)
    c: Coincident(g6,g-4)
    c: Coincident(g0,g-5)
FEATURE [PartDesign::Pocket] Pocket080
  BaseFeature = -> Pocket079
  Direction = (0,-1,2e-16)
  Length = 0.3
  Length2 = 5
  Profile = -> Sketch191
  ReferenceAxis = -> Sketch191 [N_Axis]
  Refine = true
  Suppressed = false
  Type = 0
FEATURE [Sketcher::SketchObject] Sketch192
  ArcFitTolerance = 1e-06
  AttachmentSupport = -> [Pocket080]
  ExternalGeometry = -> [Pocket080]
  FullyConstrained = true
  MakeInternals = false
  MapMode = 5
  Placement = pos=(0,0,-0.05) rot=(0,0,1;0rad)
  sketch-geometry (8):
    g0: LineSegment StartX=26.0833 StartY=-26.3 StartZ=0 EndX=26.0833 EndY=-31.7 EndZ=0
    g1: LineSegment StartX=26.0833 StartY=-31.7 StartZ=0 EndX=26.5833 EndY=-31.7 EndZ=0
    g2: LineSegment StartX=26.5833 StartY=-31.7 StartZ=0 EndX=26.5833 EndY=-26.3 EndZ=0
    g3: LineSegment StartX=26.5833 StartY=-26.3 StartZ=0 EndX=26.0833 EndY=-26.3 EndZ=0
    g4: LineSegment StartX=13.9167 StartY=-26.3 StartZ=0 EndX=13.9167 EndY=-31.7 EndZ=0
    g5: LineSegment StartX=13.9167 StartY=-31.7 StartZ=0 EndX=14.4167 EndY=-31.7 EndZ=0
    g6: LineSegment StartX=14.4167 StartY=-31.7 StartZ=0 EndX=14.4167 EndY=-26.3 EndZ=0
    g7: LineSegment StartX=14.4167 StartY=-26.3 StartZ=0 EndX=13.9167 EndY=-26.3 EndZ=0
  constraints (20):
    c: Coincident(g0,g1)
    c: Coincident(g1,g2)
    c: Coincident(g2,g3)
    c: Coincident(g3,g0)
    c: Vertical(g0)
    c: Vertical(g2)
    c: Horizontal(g1)
    c: Horizontal(g3)
    c: Coincident(g0,g-6)
    c: Coincident(g1,g-5)
    c: Coincident(g4,g5)
    c: Coincident(g5,g6)
    c: Coincident(g6,g7)
    c: Coincident(g7,g4)
    c: Vertical(g4)
    c: Vertical(g6)
    c: Horizontal(g5)
    c: Horizontal(g7)
    c: Coincident(g4,g-3)
    c: Coincident(g5,g-4)
FEATURE [PartDesign::Pocket] Pocket081
  BaseFeature = -> Pocket080
  Direction = (0,0,-1)
  Length = 0.3
  Length2 = 5
  Profile = -> Sketch192
  ReferenceAxis = -> Sketch192 [N_Axis]
  Refine = true
  Suppressed = false
  Type = 0
FEATURE [Sketcher::SketchObject] Sketch193
  ArcFitTolerance = 1e-06
  AttachmentSupport = -> [Pocket081]
  ExternalGeometry = -> [Pocket081]
  FullyConstrained = true
  MakeInternals = false
  MapMode = 5
  Placement = pos=(0,-26,1.14e-14) rot=(0,0.707107,0.707107;3.14159rad)
  sketch-geometry (1):
    g0: Circle CenterX=-11 CenterY=-4 CenterZ=0 NormalX=0 NormalY=0 NormalZ=1 AngleXU=0 Radius=2
  constraints (4):
    c: Radius(g0) = 2
    c: DistanceY(g-4,g-4) = 8.1
    c: DistanceY(g0,g-4) = 3.95
    c: DistanceX(g0,g-7) = 9
FEATURE [PartDesign::Pad] Pad132
  BaseFeature = -> Pocket081
  Direction = (0,1,-2e-16)
  Length = 7.5
  Length2 = 10
  Profile = -> Sketch193
  ReferenceAxis = -> Sketch193 [N_Axis]
  Refine = true
  Suppressed = false
  Type = 0
FEATURE [Sketcher::SketchObject] Sketch194
  ArcFitTolerance = 1e-06
  AttachmentSupport = -> [Pad132]
  ExternalGeometry = -> [Pad132]
  FullyConstrained = true
  MakeInternals = false
  MapMode = 5
  Placement = pos=(0,-18.5,0) rot=(0,0.707107,0.707107;3.14159rad)
  sketch-geometry (1):
    g0: Circle CenterX=-11 CenterY=-4 CenterZ=0 NormalX=0 NormalY=0 NormalZ=1 AngleXU=0 Radius=3
  constraints (2):
    c: Coincident(g0,g-3)
    c: Radius(g0) = 3
FEATURE [PartDesign::Pad] Pad133
  BaseFeature = -> Pad132
  Direction = (0,1,-2e-16)
  Length = 1.5
  Length2 = 10
  Profile = -> Sketch194
  ReferenceAxis = -> Sketch194 [N_Axis]
  Refine = true
  Suppressed = false
  Type = 0
FEATURE [Sketcher::SketchObject] Sketch195
  ArcFitTolerance = 1e-06
  AttachmentSupport = -> [Pad133]
  ExternalGeometry = -> [Pad133]
  FullyConstrained = true
  MakeInternals = false
  MapMode = 5
  Placement = pos=(0,-1.8e-15,-8.15) rot=(1,0,0;3.14159rad)
  sketch-geometry (8):
    g0: Circle CenterX=6.35 CenterY=29 CenterZ=0 NormalX=0 NormalY=0 NormalZ=1 AngleXU=0 Radius=1.45
    g1: Circle CenterX=34.55 CenterY=29 CenterZ=0 NormalX=0 NormalY=0 NormalZ=1 AngleXU=0 Radius=1.45
    g2: LineSegment StartX=15.75 StartY=30.45 StartZ=0 EndX=15.75 EndY=27.55 EndZ=0
    g3: LineSegment StartX=15.75 StartY=27.55 StartZ=0 EndX=24.75 EndY=27.55 EndZ=0
    g4: LineSegment StartX=24.75 StartY=27.55 StartZ=0 EndX=24.75 EndY=30.45 EndZ=0
    g5: LineSegment StartX=24.75 StartY=30.45 StartZ=0 EndX=15.75 EndY=30.45 EndZ=0
    g6: LineSegment [constr] StartX=34.55 StartY=29 StartZ=0 EndX=36 EndY=29 EndZ=0
    g7: LineSegment [constr] StartX=6.35 StartY=29 StartZ=0 EndX=4.9 EndY=29 EndZ=0
  constraints (26):
    c: Coincident(g2,g3)
    c: Coincident(g3,g4)
    c: Coincident(g4,g5)
    c: Coincident(g5,g2)
    c: Vertical(g2)
    c: Vertical(g4)
    c: Horizontal(g3)
    c: Horizontal(g5)
    c: Radius(g0) = 1.45
    c: Radius(g1) = 1.45
    c: DistanceY(g-3,g-3) = 6
    c: DistanceY(g1,g-4) = 3
    c: DistanceY(g-8,g0) = 3
    c: Coincident(g6,g1)
    c: PointOnObject(g6,g1)
    c: Horizontal(g6)
    c: DistanceX(g6,g-4) = 2.5
    c: Coincident(g7,g0)
    c: PointOnObject(g7,g0)
    c: Horizontal(g7)
    c: DistanceX(g-6,g7) = 0.9
    c: DistanceX(g5,g5) = 9
    c: DistanceY(g2,g2) = 2.9
    c: DistanceY(g2,g-9) = 1.55
    c: DistanceX(g-10,g-10) = 11.6667
    c: DistanceX(g-10,g2) = 1.33335
FEATURE [PartDesign::Pocket] Pocket082
  BaseFeature = -> Pad133
  Direction = (0,0,1)
  Length = 7
  Length2 = 5
  Profile = -> Sketch195
  ReferenceAxis = -> Sketch195 [N_Axis]
  Refine = true
  Suppressed = false
  Type = 0
FEATURE [Sketcher::SketchObject] Sketch196
  ArcFitTolerance = 1e-06
  AttachmentSupport = -> [Pocket082]
  ExternalGeometry = -> [Pocket082]
  FullyConstrained = true
  MakeInternals = false
  MapMode = 5
  Placement = pos=(0,0,-0.05) rot=(0,0,1;0rad)
  sketch-geometry (4):
    g0: Circle CenterX=11.1 CenterY=-29 CenterZ=0 NormalX=0 NormalY=0 NormalZ=1 AngleXU=0 Radius=1.5
    g1: Circle CenterX=28.5 CenterY=-29 CenterZ=0 NormalX=0 NormalY=0 NormalZ=1 AngleXU=0 Radius=1.5
    g2: LineSegment [constr] StartX=11.1 StartY=-29 StartZ=0 EndX=9.6 EndY=-29 EndZ=0
    g3: LineSegment [constr] StartX=28.5 StartY=-29 StartZ=0 EndX=30 EndY=-29 EndZ=0
  constraints (12):
    c: Radius(g1) = 1.5
    c: Radius(g0) = 1.5
    c: DistanceY(g0,g-6) = 3
    c: DistanceY(g1,g-8) = 3
    c: Coincident(g2,g0)
    c: PointOnObject(g2,g0)
    c: Coincident(g3,g1)
    c: PointOnObject(g3,g1)
    c: Horizontal(g3)
    c: Horizontal(g2)
    c: DistanceX(g-6,g2) = 5.6
    c: DistanceX(g3,g-9) = 8.5
FEATURE [PartDesign::Pocket] Pocket083
  BaseFeature = -> Pocket082
  Direction = (0,0,-1)
  Length = 6.1
  Length2 = 5
  Profile = -> Sketch196
  ReferenceAxis = -> Sketch196 [N_Axis]
  Refine = true
  Suppressed = false
  Type = 0
FEATURE [Sketcher::SketchObject] Sketch197
  ArcFitTolerance = 1e-06
  AttachmentSupport = -> [Pocket083]
  ExternalGeometry = -> [Pocket083]
  FullyConstrained = true
  MakeInternals = false
  MapMode = 5
  Placement = pos=(0,-26,1.14e-14) rot=(0,0.707107,0.707107;3.14159rad)
  sketch-geometry (4):
    g0: LineSegment StartX=-31 StartY=-0.05 StartZ=0 EndX=-31 EndY=-8.15 EndZ=0
    g1: LineSegment StartX=-31 StartY=-8.15 StartZ=0 EndX=-30.5 EndY=-8.15 EndZ=0
    g2: LineSegment StartX=-30.5 StartY=-8.15 StartZ=0 EndX=-30.5 EndY=-0.05 EndZ=0
    g3: LineSegment StartX=-30.5 StartY=-0.05 StartZ=0 EndX=-31 EndY=-0.05 EndZ=0
  constraints (12):
    c: Coincident(g0,g1)
    c: Coincident(g1,g2)
    c: Coincident(g2,g3)
    c: Coincident(g3,g0)
    c: Vertical(g0)
    c: Vertical(g2)
    c: Horizontal(g1)
    c: Horizontal(g3)
    c: PointOnObject(g1,g-4)
    c: DistanceX(g3,g3) = 0.5
    c: DistanceX(g-5,g2) = 8
    c: PointOnObject(g2,g-3)
FEATURE [PartDesign::Pocket] Pocket084
  BaseFeature = -> Pocket083
  Direction = (0,-1,2e-16)
  Length = 1
  Length2 = 5
  Profile = -> Sketch197
  ReferenceAxis = -> Sketch197 [N_Axis]
  Refine = true
  Suppressed = false
  Type = 0
FEATURE [Sketcher::SketchObject] Sketch198
  ArcFitTolerance = 1e-06
  AttachmentSupport = -> [Pocket084]
  ExternalGeometry = -> [Pocket084]
  FullyConstrained = true
  MakeInternals = false
  MapMode = 5
  Placement = pos=(0,0,-0.05) rot=(0,0,1;0rad)
  sketch-geometry (4):
    g0: LineSegment StartX=31 StartY=-27 StartZ=0 EndX=30.5 EndY=-27 EndZ=0
    g1: LineSegment StartX=30.5 StartY=-27 StartZ=0 EndX=30.5 EndY=-32 EndZ=0
    g2: LineSegment StartX=30.5 StartY=-32 StartZ=0 EndX=31 EndY=-32 EndZ=0
    g3: LineSegment StartX=31 StartY=-32 StartZ=0 EndX=31 EndY=-27 EndZ=0
  constraints (10):
    c: Coincident(g0,g1)
    c: Coincident(g1,g2)
    c: Coincident(g2,g3)
    c: Coincident(g3,g0)
    c: Horizontal(g2)
    c: Vertical(g1)
    c: Vertical(g3)
    c: Coincident(g0,g-4)
    c: PointOnObject(g1,g-3)
    c: Coincident(g0,g-4)
FEATURE [PartDesign::Pocket] Pocket085
  BaseFeature = -> Pocket084
  Direction = (0,0,-1)
  Length = 0.5
  Length2 = 5
  Profile = -> Sketch198
  ReferenceAxis = -> Sketch198 [N_Axis]
  Refine = true
  Suppressed = false
  Type = 0
FEATURE [Sketcher::SketchObject] Sketch199
  ArcFitTolerance = 1e-06
  AttachmentSupport = -> [Pocket085]
  ExternalGeometry = -> [Pocket085]
  FullyConstrained = true
  MakeInternals = false
  MapMode = 5
  Placement = pos=(0,-1.8e-15,-8.15) rot=(1,0,0;3.14159rad)
  sketch-geometry (4):
    g0: ArcOfCircle CenterX=34.55 CenterY=29 CenterZ=0 NormalX=0 NormalY=0 NormalZ=1 AngleXU=0 Radius=3 StartAngle=4.71239 EndAngle=6.62302
    g1: LineSegment StartX=37.3784 StartY=30 StartZ=0 EndX=38.5 EndY=30 EndZ=0
    g2: LineSegment StartX=38.5 StartY=30 StartZ=0 EndX=38.5 EndY=26 EndZ=0
    g3: LineSegment StartX=38.5 StartY=26 StartZ=0 EndX=34.55 EndY=26 EndZ=0
  constraints (11):
    c: PointOnObject(g0,g-6)
    c: Coincident(g1,g0)
    c: PointOnObject(g1,g-5)
    c: Horizontal(g1)
    c: Coincident(g2,g1)
    c: Coincident(g2,g-6)
    c: Coincident(g3,g2)
    c: Tangent(g3,g0) = 1.5708
    c: Coincident(g0,g-3)
    c: DistanceY(g-5,g-5) = 6
    c: DistanceY(g1,g-5) = 2
FEATURE [PartDesign::Pocket] Pocket086
  BaseFeature = -> Pocket085
  Direction = (0,0,1)
  Length = 2
  Length2 = 5
  Profile = -> Sketch199
  ReferenceAxis = -> Sketch199 [N_Axis]
  Refine = true
  Suppressed = false
  Type = 0
FEATURE [Sketcher::SketchObject] Sketch200
  ArcFitTolerance = 1e-06
  AttachmentSupport = -> [Pocket086]
  ExternalGeometry = -> [Pocket086]
  FullyConstrained = true
  MakeInternals = false
  MapMode = 5
  Placement = pos=(38.5,0,0) rot=(0.57735,0.57735,0.57735;2.0944rad)
  sketch-geometry (4):
    g0: LineSegment StartX=-26 StartY=-4.05 StartZ=0 EndX=-26 EndY=-0.05 EndZ=0
    g1: LineSegment StartX=-26 StartY=-0.05 StartZ=0 EndX=-30 EndY=-0.05 EndZ=0
    g2: LineSegment StartX=-30 StartY=-0.05 StartZ=0 EndX=-30 EndY=-4.05 EndZ=0
    g3: LineSegment StartX=-30 StartY=-4.05 StartZ=0 EndX=-26 EndY=-4.05 EndZ=0
  constraints (11):
    c: Coincident(g0,g1)
    c: Coincident(g1,g2)
    c: Coincident(g2,g3)
    c: Coincident(g3,g0)
    c: Vertical(g0)
    c: Vertical(g2)
    c: Horizontal(g1)
    c: Horizontal(g3)
    c: Coincident(g0,g-5)
    c: DistanceX(g-4,g1) = 2
    c: Distance(g2,g-6) = 2.1
FEATURE [PartDesign::Pocket] Pocket087
  BaseFeature = -> Pocket086
  Direction = (-1,0,0)
  Length = 0.5
  Length2 = 5
  Profile = -> Sketch200
  ReferenceAxis = -> Sketch200 [N_Axis]
  Refine = true
  Suppressed = false
  Type = 0
FEATURE [Sketcher::SketchObject] Sketch201
  ArcFitTolerance = 1e-06
  AttachmentSupport = -> [Pocket087]
  ExternalGeometry = -> [Pocket087]
  FullyConstrained = true
  MakeInternals = false
  MapMode = 5
  Placement = pos=(38,0,0) rot=(0.57735,0.57735,0.57735;2.0944rad)
  sketch-geometry (4):
    g0: LineSegment StartX=-30 StartY=-0.05 StartZ=0 EndX=-30 EndY=-2.05 EndZ=0
    g1: LineSegment StartX=-30 StartY=-2.05 StartZ=0 EndX=-26 EndY=-2.05 EndZ=0
    g2: LineSegment StartX=-26 StartY=-2.05 StartZ=0 EndX=-26 EndY=-0.05 EndZ=0
    g3: LineSegment StartX=-26 StartY=-0.05 StartZ=0 EndX=-30 EndY=-0.05 EndZ=0
  constraints (11):
    c: Coincident(g0,g1)
    c: Coincident(g1,g2)
    c: Coincident(g2,g3)
    c: Coincident(g3,g0)
    c: Vertical(g0)
    c: Vertical(g2)
    c: Horizontal(g1)
    c: Horizontal(g3)
    c: Coincident(g0,g-5)
    c: PointOnObject(g1,g-3)
    c: DistanceY(g2,g2) = 2
FEATURE [PartDesign::Pocket] Pocket088
  BaseFeature = -> Pocket087
  Direction = (-1,0,0)
  Length = 0.5
  Length2 = 5
  Profile = -> Sketch201
  ReferenceAxis = -> Sketch201 [N_Axis]
  Refine = true
  Suppressed = false
  Type = 0
FEATURE [Sketcher::SketchObject] Sketch202
  ArcFitTolerance = 1e-06
  AttachmentSupport = -> [Pocket088]
  ExternalGeometry = -> [Pocket088]
  FullyConstrained = true
  MakeInternals = false
  MapMode = 5
  Placement = pos=(0,-26,1.14e-14) rot=(0,0.707107,0.707107;3.14159rad)
  sketch-geometry (4):
    g0: LineSegment StartX=-38 StartY=-4.05 StartZ=0 EndX=-31 EndY=-4.05 EndZ=0
    g1: LineSegment StartX=-31 StartY=-4.05 StartZ=0 EndX=-31 EndY=-0.05 EndZ=0
    g2: LineSegment StartX=-31 StartY=-0.05 StartZ=0 EndX=-38 EndY=-0.05 EndZ=0
    g3: LineSegment StartX=-38 StartY=-0.05 StartZ=0 EndX=-38 EndY=-4.05 EndZ=0
  constraints (10):
    c: Coincident(g0,g1)
    c: Coincident(g1,g2)
    c: Coincident(g2,g3)
    c: Coincident(g3,g0)
    c: Horizontal(g0)
    c: Horizontal(g2)
    c: Vertical(g1)
    c: Vertical(g3)
    c: Coincident(g0,g-3)
    c: Coincident(g1,g-5)
FEATURE [PartDesign::Pocket] Pocket089
  BaseFeature = -> Pocket088
  Direction = (0,-1,2e-16)
  Length = 0.5
  Length2 = 5
  Profile = -> Sketch202
  ReferenceAxis = -> Sketch202 [N_Axis]
  Refine = true
  Suppressed = false
  Type = 0
FEATURE [Sketcher::SketchObject] Sketch203
  ArcFitTolerance = 1e-06
  AttachmentSupport = -> [Pocket089]
  ExternalGeometry = -> [Pocket089]
  FullyConstrained = true
  MakeInternals = false
  MapMode = 5
  Placement = pos=(0,-26.5,0) rot=(0,0.707107,0.707107;3.14159rad)
  sketch-geometry (4):
    g0: LineSegment StartX=-37.5 StartY=-2.05 StartZ=0 EndX=-31 EndY=-2.05 EndZ=0
    g1: LineSegment StartX=-31 StartY=-2.05 StartZ=0 EndX=-31 EndY=-0.05 EndZ=0
    g2: LineSegment StartX=-31 StartY=-0.05 StartZ=0 EndX=-37.5 EndY=-0.05 EndZ=0
    g3: LineSegment StartX=-37.5 StartY=-0.05 StartZ=0 EndX=-37.5 EndY=-2.05 EndZ=0
  constraints (10):
    c: Coincident(g0,g1)
    c: Coincident(g1,g2)
    c: Coincident(g2,g3)
    c: Coincident(g3,g0)
    c: Horizontal(g0)
    c: Horizontal(g2)
    c: Vertical(g1)
    c: Vertical(g3)
    c: Coincident(g0,g-5)
    c: Coincident(g1,g-4)
FEATURE [PartDesign::Pocket] Pocket090
  BaseFeature = -> Pocket089
  Direction = (0,-1,2e-16)
  Length = 0.5
  Length2 = 5
  Profile = -> Sketch203
  ReferenceAxis = -> Sketch203 [N_Axis]
  Refine = true
  Suppressed = false
  Type = 0
FEATURE [Sketcher::SketchObject] Sketch204
  ArcFitTolerance = 1e-06
  AttachmentSupport = -> [Pocket090]
  ExternalGeometry = -> [Pocket090]
  FullyConstrained = true
  MakeInternals = false
  MapMode = 5
  Placement = pos=(0,0,-0.05) rot=(0,0,1;0rad)
  sketch-geometry (3):
    g0: LineSegment StartX=37.5 StartY=-27 StartZ=0 EndX=36.5 EndY=-27 EndZ=0
    g1: LineSegment StartX=36.5 StartY=-27 StartZ=0 EndX=37.5 EndY=-28 EndZ=0
    g2: LineSegment StartX=37.5 StartY=-28 StartZ=0 EndX=37.5 EndY=-27 EndZ=0
  constraints (8):
    c: Coincident(g0,g-4)
    c: PointOnObject(g0,g-4)
    c: Coincident(g1,g0)
    c: PointOnObject(g1,g-3)
    c: Coincident(g2,g1)
    c: Coincident(g2,g0)
    c: DistanceY(g-5,g1) = 4
    c: Angle(g2,g1) = 0.785398
FEATURE [PartDesign::Pocket] Pocket091
  BaseFeature = -> Pocket090
  Direction = (0,0,-1)
  Length = 2
  Length2 = 5
  Profile = -> Sketch204
  ReferenceAxis = -> Sketch204 [N_Axis]
  Refine = true
  Suppressed = false
  Type = 0
FEATURE [Sketcher::SketchObject] Sketch205
  ArcFitTolerance = 1e-06
  AttachmentSupport = -> [Pocket091]
  ExternalGeometry = -> [Pocket091]
  FullyConstrained = true
  MakeInternals = false
  MapMode = 5
  Placement = pos=(0,0,-2.05) rot=(0,0,1;0rad)
  sketch-geometry (3):
    g0: LineSegment StartX=38 StartY=-26.5 StartZ=0 EndX=36.5 EndY=-26.5 EndZ=0
    g1: LineSegment StartX=36.5 StartY=-26.5 StartZ=0 EndX=38 EndY=-28 EndZ=0
    g2: LineSegment StartX=38 StartY=-28 StartZ=0 EndX=38 EndY=-26.5 EndZ=0
  constraints (8):
    c: Coincident(g0,g-4)
    c: PointOnObject(g0,g-4)
    c: Coincident(g1,g0)
    c: PointOnObject(g1,g-3)
    c: Coincident(g2,g1)
    c: Coincident(g2,g0)
    c: DistanceY(g-5,g1) = 4
    c: Angle(g2,g1) = 0.785398
FEATURE [PartDesign::Pocket] Pocket092
  BaseFeature = -> Pocket091
  Direction = (0,0,-1)
  Length = 2
  Length2 = 5
  Profile = -> Sketch205
  ReferenceAxis = -> Sketch205 [N_Axis]
  Refine = true
  Suppressed = false
  Type = 0
FEATURE [Sketcher::SketchObject] Sketch206
  ArcFitTolerance = 1e-06
  AttachmentSupport = -> [Pocket092]
  ExternalGeometry = -> [Pocket092]
  FullyConstrained = true
  MakeInternals = false
  MapMode = 5
  Placement = pos=(-3.3e-15,1.15e-14,-4.05) rot=(0,0,1;0rad)
  sketch-geometry (3):
    g0: LineSegment StartX=38.5 StartY=-26 StartZ=0 EndX=38.5 EndY=-28 EndZ=0
    g1: LineSegment StartX=38.5 StartY=-28 StartZ=0 EndX=36.5 EndY=-26 EndZ=0
    g2: LineSegment StartX=38.5 StartY=-26 StartZ=0 EndX=36.5 EndY=-26 EndZ=0
  constraints (8):
    c: Coincident(g0,g-4)
    c: PointOnObject(g0,g-3)
    c: Coincident(g1,g0)
    c: PointOnObject(g1,g-4)
    c: Coincident(g2,g0)
    c: Coincident(g2,g1)
    c: DistanceY(g-5,g0) = 4
    c: Angle(g0,g1) = 0.785398
FEATURE [PartDesign::Pocket] Pocket093
  BaseFeature = -> Pocket092
  Direction = (0,2.9e-15,-1)
  Length = 5
  Length2 = 5
  Profile = -> Sketch206
  ReferenceAxis = -> Sketch206 [N_Axis]
  Refine = true
  Suppressed = false
  Type = 0
FEATURE [Sketcher::SketchObject] Sketch207
  ArcFitTolerance = 1e-06
  AttachmentSupport = -> [Pocket093]
  ExternalGeometry = -> [Pocket093]
  FullyConstrained = true
  MakeInternals = false
  MapMode = 5
  Placement = pos=(0,-26,1.14e-14) rot=(0,0.707107,0.707107;3.14159rad)
  sketch-geometry (3):
    g0: LineSegment StartX=-34.55 StartY=-8.15 StartZ=0 EndX=-36.5 EndY=-6.15 EndZ=0
    g1: LineSegment StartX=-34.55 StartY=-6.15 StartZ=0 EndX=-36.5 EndY=-6.15 EndZ=0
    g2: LineSegment StartX=-34.55 StartY=-6.15 StartZ=0 EndX=-34.55 EndY=-8.15 EndZ=0
  constraints (6):
    c: Coincident(g0,g-3)
    c: Coincident(g0,g-4)
    c: Coincident(g1,g-4)
    c: Coincident(g1,g0)
    c: Coincident(g2,g1)
    c: Coincident(g2,g0)
FEATURE [PartDesign::Pad] Pad134
  BaseFeature = -> Pocket093
  Direction = (0,1,-2e-16)
  Length = 1
  Length2 = 10
  Profile = -> Sketch207
  ReferenceAxis = -> Sketch207 [N_Axis]
  Refine = true
  Reversed = true
  Suppressed = false
  Type = 0
FEATURE [Sketcher::SketchObject] Sketch208
  ArcFitTolerance = 1e-06
  AttachmentSupport = -> [Pad134]
  ExternalGeometry = -> [Pad134]
  FullyConstrained = true
  MakeInternals = false
  MapMode = 5
  Placement = pos=(0,-1.8e-15,-8.15) rot=(1,0,0;3.14159rad)
  sketch-geometry (3):
    g0: LineSegment StartX=30.5 StartY=27 StartZ=0 EndX=32.5 EndY=26 EndZ=0
    g1: LineSegment StartX=30.5 StartY=27 StartZ=0 EndX=30.5 EndY=26 EndZ=0
    g2: LineSegment StartX=30.5 StartY=26 StartZ=0 EndX=32.5 EndY=26 EndZ=0
  constraints (7):
    c: Coincident(g0,g-4)
    c: PointOnObject(g0,g-6)
    c: DistanceX(g0,g0) = 2
    c: Coincident(g1,g0)
    c: Coincident(g1,g-7)
    c: Coincident(g2,g1)
    c: Coincident(g2,g0)
FEATURE [PartDesign::Pocket] Pocket094
  BaseFeature = -> Pad134
  Direction = (0,0,1)
  Length = 4.1
  Length2 = 5
  Profile = -> Sketch208
  ReferenceAxis = -> Sketch208 [N_Axis]
  Refine = true
  Suppressed = false
  Type = 0
FEATURE [Sketcher::SketchObject] Sketch209
  ArcFitTolerance = 1e-06
  AttachmentSupport = -> [Pocket094]
  ExternalGeometry = -> [Pocket094]
  FullyConstrained = true
  MakeInternals = false
  MapMode = 5
  Placement = pos=(0,-1.8e-15,-8.15) rot=(1,0,0;3.14159rad)
  sketch-geometry (3):
    g0: LineSegment StartX=31 StartY=26.75 StartZ=0 EndX=30.5 EndY=27 EndZ=0
    g1: LineSegment StartX=31 StartY=27 StartZ=0 EndX=31 EndY=26.75 EndZ=0
    g2: LineSegment StartX=31 StartY=27 StartZ=0 EndX=30.5 EndY=27 EndZ=0
  constraints (6):
    c: Coincident(g0,g-5)
    c: Coincident(g0,g-3)
    c: Coincident(g1,g-4)
    c: Coincident(g1,g0)
    c: Coincident(g2,g1)
    c: Coincident(g2,g0)
FEATURE [PartDesign::Pad] Pad135
  BaseFeature = -> Pocket094
  Direction = (0,0,-1)
  Length = 4.1
  Length2 = 10
  Profile = -> Sketch209
  ReferenceAxis = -> Sketch209 [N_Axis]
  Refine = true
  Reversed = true
  Suppressed = false
  Type = 0
FEATURE [Sketcher::SketchObject] Sketch210
  ArcFitTolerance = 1e-06
  AttachmentSupport = -> [Pad135]
  ExternalGeometry = -> [Pad135]
  FullyConstrained = true
  MakeInternals = false
  MapMode = 5
  Placement = pos=(0,0,-0.05) rot=(0,0,1;0rad)
  sketch-geometry (3):
    g0: LineSegment StartX=31 StartY=-27 StartZ=0 EndX=32.5 EndY=-27 EndZ=0
    g1: LineSegment StartX=32.5 StartY=-27 StartZ=0 EndX=31 EndY=-28.5 EndZ=0
    g2: LineSegment StartX=31 StartY=-28.5 StartZ=0 EndX=31 EndY=-27 EndZ=0
  constraints (8):
    c: Coincident(g0,g-4)
    c: PointOnObject(g0,g-3)
    c: Coincident(g1,g0)
    c: PointOnObject(g1,g-4)
    c: Coincident(g2,g1)
    c: Coincident(g2,g0)
    c: DistanceX(g0,g0) = 1.5
    c: DistanceY(g2,g2) = 1.5
FEATURE [PartDesign::Pocket] Pocket095
  BaseFeature = -> Pad135
  Direction = (0,0,-1)
  Length = 2
  Length2 = 5
  Profile = -> Sketch210
  ReferenceAxis = -> Sketch210 [N_Axis]
  Refine = true
  Suppressed = false
  Type = 0
FEATURE [PartDesign::Pad] Pad136
  BaseFeature = -> Pocket095
  Direction = (0,0,1)
  Length = 0.5
  Length2 = 10
  Profile = -> Pocket095 [Face10]
  Refine = true
  Suppressed = false
  Type = 0
FEATURE [Sketcher::SketchObject] Sketch211
  ArcFitTolerance = 1e-06
  AttachmentSupport = -> [Pad136]
  ExternalGeometry = -> [Pad136]
  FullyConstrained = true
  MakeInternals = false
  MapMode = 5
  Placement = pos=(0,-5.3e-15,-8.15) rot=(1,0,0;3.14159rad)
  sketch-geometry (4):
    g0: LineSegment StartX=31 StartY=26.75 StartZ=0 EndX=31 EndY=32 EndZ=0
    g1: LineSegment StartX=31 StartY=32 StartZ=0 EndX=30.5 EndY=32 EndZ=0
    g2: LineSegment StartX=30.5 StartY=32 StartZ=0 EndX=30.5 EndY=27 EndZ=0
    g3: LineSegment StartX=31 StartY=26.75 StartZ=0 EndX=30.5 EndY=27 EndZ=0
  constraints (11):
    c: Coincident(g0,g1)
    c: Coincident(g1,g2)
    c: Horizontal(g1)
    c: Vertical(g0)
    c: Vertical(g2)
    c: PointOnObject(g0,g-4)
    c: DistanceX(g1,g1) = 0.5
    c: PointOnObject(g0,g-5)
    c: Coincident(g3,g0)
    c: Coincident(g3,g2)
    c: Coincident(g2,g-5)
FEATURE [PartDesign::Pocket] Pocket096
  BaseFeature = -> Pad136
  Direction = (0,0,1)
  Length = 0.5
  Length2 = 5
  Profile = -> Sketch211
  ReferenceAxis = -> Sketch211 [N_Axis]
  Refine = true
  Suppressed = false
  Type = 0
FEATURE [Sketcher::SketchObject] Sketch212
  ArcFitTolerance = 1e-06
  AttachmentSupport = -> [Pocket096]
  ExternalGeometry = -> [Pocket096]
  FullyConstrained = true
  MakeInternals = false
  MapMode = 5
  Placement = pos=(8e-16,1.8e-15,-2.05) rot=(0,0,1;0rad)
  sketch-geometry (3):
    g0: LineSegment StartX=31 StartY=-26.5 StartZ=0 EndX=32.5 EndY=-26.5 EndZ=0
    g1: LineSegment StartX=32.5 StartY=-26.5 StartZ=0 EndX=31 EndY=-28 EndZ=0
    g2: LineSegment StartX=31 StartY=-28 StartZ=0 EndX=31 EndY=-26.5 EndZ=0
  constraints (8):
    c: Coincident(g0,g-5)
    c: PointOnObject(g0,g-3)
    c: Coincident(g1,g0)
    c: PointOnObject(g1,g-4)
    c: Coincident(g2,g1)
    c: Coincident(g2,g0)
    c: DistanceX(g0,g0) = 1.5
    c: DistanceY(g2,g2) = 1.5
FEATURE [PartDesign::Pocket] Pocket097
  BaseFeature = -> Pocket096
  Direction = (0,0,-1)
  Length = 2
  Length2 = 5
  Profile = -> Sketch212
  ReferenceAxis = -> Sketch212 [N_Axis]
  Refine = true
  Suppressed = false
  Type = 0
FEATURE [Sketcher::SketchObject] Sketch213
  ArcFitTolerance = 1e-06
  AttachmentSupport = -> [XY_Plane011]
  FullyConstrained = true
  MakeInternals = false
  MapMode = 5
  sketch-geometry (4):
    g0: LineSegment StartX=0 StartY=0 StartZ=0 EndX=7.9 EndY=0 EndZ=0
    g1: LineSegment StartX=7.9 StartY=0 StartZ=0 EndX=7.9 EndY=9.8 EndZ=0
    g2: LineSegment StartX=7.9 StartY=9.8 StartZ=0 EndX=0 EndY=9.8 EndZ=0
    g3: LineSegment StartX=0 StartY=9.8 StartZ=0 EndX=0 EndY=0 EndZ=0
  constraints (11):
    c: Coincident(g0,g1)
    c: Coincident(g1,g2)
    c: Coincident(g2,g3)
    c: Coincident(g3,g0)
    c: Horizontal(g0)
    c: Horizontal(g2)
    c: Vertical(g1)
    c: Vertical(g3)
    c: Coincident(g0,g-1)
    c: DistanceX(g0,g0) = 7.9
    c: DistanceY(g1,g1) = 9.8
FEATURE [PartDesign::Pad] Pad137
  Direction = (0,0,1)
  Length = 2.75
  Length2 = 10
  Profile = -> Sketch213
  ReferenceAxis = -> Sketch213 [N_Axis]
  Refine = true
  Suppressed = false
  Type = 0
FEATURE [Sketcher::SketchObject] Sketch214
  ArcFitTolerance = 1e-06
  AttachmentSupport = -> [Pad137]
  ExternalGeometry = -> [Pad137]
  FullyConstrained = true
  MakeInternals = false
  MapMode = 5
  Placement = pos=(0,0,0) rot=(1,0,0;3.14159rad)
  sketch-geometry (4):
    g0: LineSegment StartX=0 StartY=0 StartZ=0 EndX=0 EndY=-1.4 EndZ=0
    g1: LineSegment StartX=0 StartY=-1.4 StartZ=0 EndX=7.9 EndY=-1.4 EndZ=0
    g2: LineSegment StartX=7.9 StartY=-1.4 StartZ=0 EndX=7.9 EndY=0 EndZ=0
    g3: LineSegment StartX=7.9 StartY=0 StartZ=0 EndX=0 EndY=0 EndZ=0
  constraints (11):
    c: Coincident(g0,g1)
    c: Coincident(g1,g2)
    c: Coincident(g2,g3)
    c: Coincident(g3,g0)
    c: Vertical(g0)
    c: Vertical(g2)
    c: Horizontal(g1)
    c: Horizontal(g3)
    c: Coincident(g0,g-1)
    c: PointOnObject(g1,g-3)
    c: DistanceY(g2,g2) = 1.4
FEATURE [PartDesign::Pad] Pad138
  BaseFeature = -> Pad137
  Direction = (0,0,-1)
  Length = 2
  Length2 = 10
  Profile = -> Sketch214
  ReferenceAxis = -> Sketch214 [N_Axis]
  Refine = true
  Suppressed = false
  Type = 0
FEATURE [Sketcher::SketchObject] Sketch215
  ArcFitTolerance = 1e-06
  AttachmentSupport = -> [Pad138]
  ExternalGeometry = -> [Pad138]
  FullyConstrained = true
  MakeInternals = false
  MapMode = 5
  Placement = pos=(0,0,0) rot=(0.57735,-0.57735,-0.57735;2.0944rad)
  sketch-geometry (1):
    g0: Circle CenterX=-8.5 CenterY=0 CenterZ=0 NormalX=0 NormalY=0 NormalZ=1 AngleXU=0 Radius=1.3
  constraints (3):
    c: Diameter(g0) = 2.6
    c: PointOnObject(g0,g-4)
    c: PointOnObject(g-4,g0)
FEATURE [PartDesign::Pad] Pad139
  BaseFeature = -> Pad138
  Direction = (-1,0,0)
  Length = 1.6
  Length2 = 10
  Profile = -> Sketch215
  ReferenceAxis = -> Sketch215 [N_Axis]
  Refine = true
  Suppressed = false
  Type = 0
FEATURE [PartDesign::Pad] Pad140
  BaseFeature = -> Pad139
  Direction = (-1,0,0)
  Length = 9.5
  Length2 = 10
  Profile = -> Sketch215
  ReferenceAxis = -> Sketch215 [N_Axis]
  Refine = true
  Reversed = true
  Suppressed = false
  Type = 0
FEATURE [Sketcher::SketchObject] Sketch216
  ArcFitTolerance = 1e-06
  AttachmentSupport = -> [Pad140]
  ExternalGeometry = -> [Pad140]
  FullyConstrained = true
  MakeInternals = false
  MapMode = 5
  Placement = pos=(0,0,0) rot=(0.57735,-0.57735,-0.57735;2.0944rad)
  sketch-geometry (4):
    g0: LineSegment StartX=-6.9 StartY=2.75 StartZ=0 EndX=-6.9 EndY=0 EndZ=0
    g1: LineSegment StartX=-6.9 StartY=0 StartZ=0 EndX=-5.4 EndY=0 EndZ=0
    g2: LineSegment StartX=-5.4 StartY=0 StartZ=0 EndX=-5.4 EndY=2.75 EndZ=0
    g3: LineSegment StartX=-5.4 StartY=2.75 StartZ=0 EndX=-6.9 EndY=2.75 EndZ=0
  constraints (12):
    c: Coincident(g0,g1)
    c: Coincident(g1,g2)
    c: Coincident(g2,g3)
    c: Coincident(g3,g0)
    c: Vertical(g0)
    c: Vertical(g2)
    c: Horizontal(g1)
    c: Horizontal(g3)
    c: PointOnObject(g0,g-3)
    c: PointOnObject(g1,g-4)
    c: DistanceX(g1,g1) = 1.5
    c: DistanceX(g-3,g0) = 2.9
FEATURE [PartDesign::Pad] Pad141
  BaseFeature = -> Pad140
  Direction = (-1,0,0)
  Length = 0.45
  Length2 = 10
  Profile = -> Sketch216
  ReferenceAxis = -> Sketch216 [N_Axis]
  Refine = true
  Suppressed = false
  Type = 0
FEATURE [Sketcher::SketchObject] Sketch217
  ArcFitTolerance = 1e-06
  AttachmentSupport = -> [Pad141]
  ExternalGeometry = -> [Pad141]
  FullyConstrained = true
  MakeInternals = false
  MapMode = 5
  Placement = pos=(7.9,0,0) rot=(0.57735,0.57735,0.57735;2.0944rad)
  sketch-geometry (4):
    g0: LineSegment StartX=5.4 StartY=2.75 StartZ=0 EndX=5.4 EndY=0 EndZ=0
    g1: LineSegment StartX=5.4 StartY=0 StartZ=0 EndX=6.9 EndY=0 EndZ=0
    g2: LineSegment StartX=6.9 StartY=0 StartZ=0 EndX=6.9 EndY=2.75 EndZ=0
    g3: LineSegment StartX=6.9 StartY=2.75 StartZ=0 EndX=5.4 EndY=2.75 EndZ=0
  constraints (10):
    c: Coincident(g0,g1)
    c: Coincident(g1,g2)
    c: Coincident(g2,g3)
    c: Coincident(g3,g0)
    c: Vertical(g0)
    c: Vertical(g2)
    c: Horizontal(g1)
    c: Horizontal(g3)
    c: Coincident(g0,g-3)
    c: Coincident(g1,g-4)
FEATURE [PartDesign::Pad] Pad142
  BaseFeature = -> Pad141
  Direction = (1,0,0)
  Length = 0.45
  Length2 = 10
  Profile = -> Sketch217
  ReferenceAxis = -> Sketch217 [N_Axis]
  Refine = true
  Suppressed = false
  Type = 0
FEATURE [PartDesign::Chamfer] Chamfer003
  Angle = 45
  Base = -> Pad142 [Edge47,Edge45,Edge16,Edge18]
  BaseFeature = -> Pad142
  ChamferType = 0
  FlipDirection = false
  Refine = true
  Size = 0.4
  Size2 = 1
  SupportTransform = false
  Suppressed = false
  UseAllEdges = false
FEATURE [Sketcher::SketchObject] Sketch218
  ArcFitTolerance = 1e-06
  AttachmentSupport = -> [Chamfer003]
  ExternalGeometry = -> [Chamfer003]
  FullyConstrained = true
  MakeInternals = false
  MapMode = 5
  Placement = pos=(0,0,2.75) rot=(0,0,1;0rad)
  sketch-geometry (1):
    g0: Circle CenterX=3.95 CenterY=4.9 CenterZ=0 NormalX=0 NormalY=0 NormalZ=1 AngleXU=0 Radius=2.45
  constraints (5):
    c: Diameter(g0) = 4.9
    c: DistanceX(g-3,g-3) = 7.9
    c: DistanceY(g-4,g-3) = 9.8
    c: DistanceX(g0,g-4) = 3.95
    c: DistanceY(g-4,g0) = 4.9
FEATURE [PartDesign::Pocket] Pocket098
  BaseFeature = -> Chamfer003
  Direction = (0,0,-1)
  Length = 1.7
  Length2 = 5
  Profile = -> Sketch218
  ReferenceAxis = -> Sketch218 [N_Axis]
  Refine = true
  Suppressed = false
  Type = 0
FEATURE [Sketcher::SketchObject] Sketch219
  ArcFitTolerance = 1e-06
  AttachmentOffset = pos=(0,0,-1) rot=(0,0,1;0rad)
  AttachmentSupport = -> [Pocket098]
  ExternalGeometry = -> [Pocket098]
  FullyConstrained = true
  MakeInternals = false
  MapMode = 5
  Placement = pos=(1,0,0) rot=(0.57735,-0.57735,-0.57735;2.0944rad)
  sketch-geometry (5):
    g0: ArcOfCircle CenterX=-7.19261 CenterY=0.257783 CenterZ=0 NormalX=0 NormalY=0 NormalZ=1 AngleXU=0 Radius=4.5 StartAngle=5.75759 EndAngle=6.22587
    g1: LineSegment [constr] StartX=-1.4 StartY=-2 StartZ=0 EndX=-3.3 EndY=-2 EndZ=0
    g2: LineSegment StartX=-3.3 StartY=-2 StartZ=0 EndX=-5.26914 EndY=-1.65 EndZ=0
    g3: ArcOfCircle CenterX=-12.6824 CenterY=-0.512926 CenterZ=0 NormalX=0 NormalY=0 NormalZ=1 AngleXU=0 Radius=7.5 StartAngle=6.13099 EndAngle=6.35163
    g4: LineSegment StartX=-5.2 StartY=-1.3e-15 StartZ=0 EndX=-2.7 EndY=1.6e-15 EndZ=0
  constraints (16):
    c: PointOnObject(g0,g-3)
    c: DistanceX(g0,g-3) = 1.3
    c: Coincident(g1,g-4)
    c: Coincident(g1,g0)
    c: Horizontal(g1)
    c: Coincident(g2,g0)
    c: Coincident(g3,g2)
    c: PointOnObject(g3,g-3)
    c: Coincident(g4,g3)
    c: Coincident(g4,g0)
    c: DistanceX(g3,g0) = 2.5
    c: Distance(g2) = 2
    c: DistanceX(g0,g0) = 0.6
    c: Radius(g0) = 4.5
    c: Radius(g3) = 7.5
    c: DistanceY(g0,g2) = 0.35
FEATURE [PartDesign::Pad] Pad143
  BaseFeature = -> Pocket098
  Direction = (-1,0,0)
  Length = 5.9
  Length2 = 10
  Profile = -> Sketch219
  ReferenceAxis = -> Sketch219 [N_Axis]
  Refine = true
  Reversed = true
  Suppressed = false
  Type = 0
FEATURE [Sketcher::SketchObject] Sketch220
  ArcFitTolerance = 1e-06
  AttachmentSupport = -> [Pad143]
  ExternalGeometry = -> [Pad143]
  FullyConstrained = true
  MakeInternals = false
  MapMode = 5
  Placement = pos=(1,0,0) rot=(0.57735,-0.57735,-0.57735;2.0944rad)
  sketch-geometry (4):
    g0: ArcOfCircle CenterX=-7.19261 CenterY=0.257783 CenterZ=0 NormalX=0 NormalY=0 NormalZ=1 AngleXU=0 Radius=4.5 StartAngle=5.85761 EndAngle=6.22587
    g1: LineSegment StartX=-3.094 StartY=-1.6 StartZ=0 EndX=-1.6 EndY=-0.737441 EndZ=0
    g2: LineSegment StartX=-1.6 StartY=-0.737441 StartZ=0 EndX=-1.6 EndY=0 EndZ=0
    g3: LineSegment StartX=-2.7 StartY=1.6e-15 StartZ=0 EndX=-1.6 EndY=0 EndZ=0
  constraints (11):
    c: PointOnObject(g0,g-3)
    c: Tangent(g0,g-3) = -1.5708
    c: DistanceY(g0,g0) = 1.6
    c: Coincident(g1,g0)
    c: Coincident(g2,g1)
    c: PointOnObject(g2,g-4)
    c: Vertical(g2)
    c: Coincident(g3,g0)
    c: Coincident(g3,g2)
    c: DistanceX(g3,g3) = 1.1
    c: Angle(g2,g1) = 2.0944
FEATURE [PartDesign::Pad] Pad144
  BaseFeature = -> Pad143
  Direction = (-1,0,0)
  Length = 5.9
  Length2 = 10
  Profile = -> Sketch220
  ReferenceAxis = -> Sketch220 [N_Axis]
  Refine = true
  Reversed = true
  Suppressed = false
  Type = 0
FEATURE [Sketcher::SketchObject] Sketch221
  ArcFitTolerance = 1e-06
  AttachmentSupport = -> [Pad144]
  ExternalGeometry = -> [Pad144]
  FullyConstrained = true
  MakeInternals = false
  MapMode = 5
  Placement = pos=(0,0,-2) rot=(1,0,0;3.14159rad)
  sketch-geometry (4):
    g0: LineSegment StartX=2.5 StartY=-1.6 StartZ=0 EndX=2.5 EndY=-3.094 EndZ=0
    g1: LineSegment StartX=2.5 StartY=-3.094 StartZ=0 EndX=5.4 EndY=-3.094 EndZ=0
    g2: LineSegment StartX=5.4 StartY=-3.094 StartZ=0 EndX=5.4 EndY=-1.6 EndZ=0
    g3: LineSegment StartX=5.4 StartY=-1.6 StartZ=0 EndX=2.5 EndY=-1.6 EndZ=0
  constraints (12):
    c: Coincident(g0,g1)
    c: Coincident(g1,g2)
    c: Coincident(g2,g3)
    c: Coincident(g3,g0)
    c: Vertical(g0)
    c: Vertical(g2)
    c: Horizontal(g1)
    c: Horizontal(g3)
    c: PointOnObject(g0,g-5)
    c: PointOnObject(g1,g-6)
    c: DistanceX(g-5,g0) = 1.5
    c: DistanceX(g2,g-5) = 1.5
FEATURE [PartDesign::Pocket] Pocket099
  BaseFeature = -> Pad144
  Direction = (0,0,1)
  Length = 2
  Length2 = 5
  Profile = -> Sketch221
  ReferenceAxis = -> Sketch221 [N_Axis]
  Refine = true
  Suppressed = false
  Type = 0
FEATURE [Sketcher::SketchObject] Sketch222
  ArcFitTolerance = 1e-06
  AttachmentSupport = -> [Pocket099]
  ExternalGeometry = -> [Pocket099]
  FullyConstrained = true
  MakeInternals = false
  MapMode = 5
  Placement = pos=(0,0,-2) rot=(1,0,0;3.14159rad)
  sketch-geometry (9):
    g0: LineSegment StartX=3.2 StartY=-1.6 StartZ=0 EndX=4.7 EndY=-1.6 EndZ=0
    g1: LineSegment StartX=4.7 StartY=-1.6 StartZ=0 EndX=5.075 EndY=-3.3 EndZ=0
    g2: LineSegment StartX=5.075 StartY=-3.3 StartZ=0 EndX=4.7 EndY=-5.26914 EndZ=0
    g3: LineSegment StartX=4.7 StartY=-5.26914 StartZ=0 EndX=3.2 EndY=-5.26914 EndZ=0
    g4: LineSegment StartX=3.2 StartY=-5.26914 StartZ=0 EndX=2.825 EndY=-3.3 EndZ=0
    g5: LineSegment StartX=2.825 StartY=-3.3 StartZ=0 EndX=3.2 EndY=-1.6 EndZ=0
    g6: LineSegment [constr] StartX=3.2 StartY=-1.6 StartZ=0 EndX=3.2 EndY=-5.26914 EndZ=0
    g7: LineSegment [constr] StartX=4.7 StartY=-1.6 StartZ=0 EndX=4.7 EndY=-5.26914 EndZ=0
    g8: LineSegment [constr] StartX=3.2 StartY=-1.6 StartZ=0 EndX=2.5 EndY=-1.6 EndZ=0
  constraints (26):
    c: Horizontal(g0)
    c: Coincident(g1,g0)
    c: PointOnObject(g1,g-8)
    c: Coincident(g2,g1)
    c: PointOnObject(g2,g-3)
    c: Coincident(g3,g2)
    c: PointOnObject(g3,g-3)
    c: Coincident(g4,g3)
    c: PointOnObject(g4,g-8)
    c: Coincident(g5,g4)
    c: Coincident(g5,g0)
    c: DistanceX(g0,g0) = 1.5
    c: DistanceX(g3,g3) = 1.5
    c: Coincident(g6,g0)
    c: Coincident(g6,g3)
    c: Vertical(g6)
    c: Coincident(g7,g0)
    c: Coincident(g7,g2)
    c: Coincident(g8,g0)
    c: Coincident(g8,g-6)
    c: Horizontal(g8)
    c: DistanceX(g4,g1) = 2.25
    c: DistanceX(g8,g-5) = 2.9
    c: DistanceX(g8,g0) = 0.7
    c: DistanceX(g-7,g4) = 0.325
    c: DistanceX(g1,g-7) = 0.325
FEATURE [PartDesign::Pad] Pad145
  BaseFeature = -> Pocket099
  Direction = (0,0,-1)
  Length = 2
  Length2 = 10
  Profile = -> Sketch222
  ReferenceAxis = -> Sketch222 [N_Axis]
  Refine = true
  Reversed = true
  Suppressed = false
  Type = 0
FEATURE [Sketcher::SketchObject] Sketch223
  ArcFitTolerance = 1e-06
  AttachmentSupport = -> [Pad145]
  ExternalGeometry = -> [Pad145]
  FullyConstrained = true
  MakeInternals = false
  MapMode = 5
  Placement = pos=(6.9,0,0) rot=(0.57735,0.57735,0.57735;2.0944rad)
  sketch-geometry (3):
    g0: LineSegment StartX=5.26914 StartY=-1.65 StartZ=0 EndX=5.26914 EndY=0 EndZ=0
    g1: LineSegment StartX=5.26914 StartY=0 StartZ=0 EndX=5.2 EndY=-1.3e-15 EndZ=0
    g2: ArcOfCircle CenterX=12.6825 CenterY=-0.512923 CenterZ=0 NormalX=0 NormalY=0 NormalZ=1 AngleXU=0 Radius=7.50006 StartAngle=3.07315 EndAngle=3.29379
  constraints (7):
    c: Coincident(g0,g-5)
    c: Coincident(g0,g-3)
    c: Coincident(g1,g0)
    c: Coincident(g1,g-5)
    c: Coincident(g2,g1)
    c: Coincident(g2,g0)
    c: Tangent(g2,g-5)
FEATURE [PartDesign::Pocket] Pocket100
  BaseFeature = -> Pad145
  Direction = (-1,0,0)
  Length = 5
  Length2 = 5
  Profile = -> Sketch223
  ReferenceAxis = -> Sketch223 [N_Axis]
  Refine = true
  Suppressed = false
  Type = 0
FEATURE [Sketcher::SketchObject] Sketch224
  ArcFitTolerance = 1e-06
  AttachmentSupport = -> [Pocket100]
  ExternalGeometry = -> [Pocket100]
  FullyConstrained = true
  MakeInternals = false
  MapMode = 5
  Placement = pos=(0,0,-2) rot=(1,0,0;3.14159rad)
  sketch-geometry (8):
    g0: LineSegment StartX=3.35588 StartY=-1.8 StartZ=0 EndX=4.54412 EndY=-1.8 EndZ=0
    g1: LineSegment StartX=4.54412 StartY=-1.8 StartZ=0 EndX=4.875 EndY=-3.3 EndZ=0
    g2: LineSegment StartX=4.875 StartY=-3.3 StartZ=0 EndX=4.53809 EndY=-5.06914 EndZ=0
    g3: LineSegment StartX=4.53809 StartY=-5.06914 StartZ=0 EndX=3.36191 EndY=-5.06914 EndZ=0
    g4: LineSegment StartX=3.36191 StartY=-5.06914 StartZ=0 EndX=3.025 EndY=-3.3 EndZ=0
    g5: LineSegment StartX=3.025 StartY=-3.3 StartZ=0 EndX=3.35588 EndY=-1.8 EndZ=0
    g6: LineSegment [constr] StartX=3.025 StartY=-3.3 StartZ=0 EndX=2.825 EndY=-3.3 EndZ=0
    g7: LineSegment [constr] StartX=4.875 StartY=-3.3 StartZ=0 EndX=5.075 EndY=-3.3 EndZ=0
  constraints (22):
    c: Horizontal(g0)
    c: Coincident(g1,g0)
    c: Coincident(g2,g1)
    c: Coincident(g3,g2)
    c: Horizontal(g3)
    c: Coincident(g4,g3)
    c: Coincident(g5,g4)
    c: Coincident(g5,g0)
    c: Parallel(g5,g-7)
    c: Parallel(g2,g-5)
    c: Parallel(g1,g-4)
    c: Parallel(g4,g-6)
    c: DistanceY(g0,g-7) = 0.2
    c: DistanceY(g-6,g3) = 0.2
    c: Coincident(g6,g4)
    c: Coincident(g6,g-7)
    c: Coincident(g7,g1)
    c: Coincident(g7,g-5)
    c: Horizontal(g6)
    c: Horizontal(g7)
    c: DistanceX(g6,g6) = 0.2
    c: DistanceX(g7,g7) = 0.2
FEATURE [PartDesign::Pocket] Pocket101
  BaseFeature = -> Pocket100
  Direction = (0,0,1)
  Length = 0.5
  Length2 = 5
  Profile = -> Sketch224
  ReferenceAxis = -> Sketch224 [N_Axis]
  Refine = true
  Suppressed = false
  Type = 0
FEATURE [Sketcher::SketchObject] Sketch225
  ArcFitTolerance = 1e-06
  AttachmentSupport = -> [Pocket101]
  ExternalGeometry = -> [Pocket101]
  FullyConstrained = true
  MakeInternals = false
  MapMode = 5
  Placement = pos=(0,0,-2) rot=(1,0,0;3.14159rad)
  sketch-geometry (4):
    g0: LineSegment StartX=3.2 StartY=-7.2 StartZ=0 EndX=3.2 EndY=-9.8 EndZ=0
    g1: LineSegment StartX=3.2 StartY=-9.8 StartZ=0 EndX=4.7 EndY=-9.8 EndZ=0
    g2: LineSegment StartX=4.7 StartY=-9.8 StartZ=0 EndX=4.7 EndY=-7.2 EndZ=0
    g3: LineSegment StartX=4.7 StartY=-7.2 StartZ=0 EndX=3.2 EndY=-7.2 EndZ=0
  constraints (13):
    c: Coincident(g0,g1)
    c: Coincident(g1,g2)
    c: Coincident(g2,g3)
    c: Coincident(g3,g0)
    c: Vertical(g0)
    c: Vertical(g2)
    c: Horizontal(g1)
    c: Horizontal(g3)
    c: PointOnObject(g0,g-3)
    c: PointOnObject(g1,g-4)
    c: DistanceX(g3,g3) = 1.5
    c: DistanceX(g-4,g-4) = 7.9
    c: DistanceX(g-3,g0) = 3.2
FEATURE [PartDesign::Pocket] Pocket102
  BaseFeature = -> Pocket101
  Direction = (0,0,1)
  Length = 1
  Length2 = 5
  Profile = -> Sketch225
  ReferenceAxis = -> Sketch225 [N_Axis]
  Refine = true
  Suppressed = false
  Type = 0
FEATURE [Sketcher::SketchObject] Sketch226
  ArcFitTolerance = 1e-06
  AttachmentSupport = -> [Pocket102]
  ExternalGeometry = -> [Pocket102]
  FullyConstrained = true
  MakeInternals = false
  MapMode = 5
  Placement = pos=(0,0,-2) rot=(1,0,0;3.14159rad)
  sketch-geometry (8):
    g0: LineSegment StartX=1.15 StartY=-7.2 StartZ=0 EndX=1.15 EndY=-9.8 EndZ=0
    g1: LineSegment StartX=1.15 StartY=-9.8 StartZ=0 EndX=1.95 EndY=-9.8 EndZ=0
    g2: LineSegment StartX=1.95 StartY=-9.8 StartZ=0 EndX=1.95 EndY=-7.2 EndZ=0
    g3: LineSegment StartX=1.95 StartY=-7.2 StartZ=0 EndX=1.15 EndY=-7.2 EndZ=0
    g4: LineSegment StartX=5.95 StartY=-7.2 StartZ=0 EndX=5.95 EndY=-9.8 EndZ=0
    g5: LineSegment StartX=5.95 StartY=-9.8 StartZ=0 EndX=6.75 EndY=-9.8 EndZ=0
    g6: LineSegment StartX=6.75 StartY=-9.8 StartZ=0 EndX=6.75 EndY=-7.2 EndZ=0
    g7: LineSegment StartX=6.75 StartY=-7.2 StartZ=0 EndX=5.95 EndY=-7.2 EndZ=0
  constraints (25):
    c: Coincident(g0,g1)
    c: Coincident(g1,g2)
    c: Coincident(g2,g3)
    c: Coincident(g3,g0)
    c: Vertical(g0)
    c: Vertical(g2)
    c: Horizontal(g1)
    c: Horizontal(g3)
    c: PointOnObject(g0,g-3)
    c: PointOnObject(g1,g-4)
    c: Coincident(g4,g5)
    c: Coincident(g5,g6)
    c: Coincident(g6,g7)
    c: Coincident(g7,g4)
    c: Vertical(g4)
    c: Vertical(g6)
    c: Horizontal(g5)
    c: Horizontal(g7)
    c: PointOnObject(g4,g-3)
    c: PointOnObject(g5,g-4)
    c: DistanceX(g3,g3) = 0.8
    c: DistanceX(g7,g7) = 0.8
    c: DistanceX(g-4,g-4) = 7.9
    c: DistanceX(g-4,g0) = 1.15
    c: DistanceX(g5,g-4) = 1.15
FEATURE [PartDesign::Pad] Pad146
  BaseFeature = -> Pocket102
  Direction = (0,0,-1)
  Length = 2
  Length2 = 10
  Profile = -> Sketch226
  ReferenceAxis = -> Sketch226 [N_Axis]
  Refine = true
  Reversed = true
  Suppressed = false
  Type = 0
FEATURE [Sketcher::SketchObject] Sketch227
  ArcFitTolerance = 1e-06
  AttachmentSupport = -> [Pad146]
  ExternalGeometry = -> [Pad146]
  FullyConstrained = true
  MakeInternals = false
  MapMode = 5
  Placement = pos=(0,0,-2) rot=(1,0,0;3.14159rad)
  sketch-geometry (4):
    g0: LineSegment StartX=3.2 StartY=-7.66934 StartZ=0 EndX=2.35 EndY=-7.2 EndZ=0
    g1: LineSegment StartX=2.35 StartY=-7.2 StartZ=0 EndX=5.55 EndY=-7.2 EndZ=0
    g2: LineSegment StartX=5.55 StartY=-7.2 StartZ=0 EndX=4.7 EndY=-7.66934 EndZ=0
    g3: LineSegment StartX=4.7 StartY=-7.66934 StartZ=0 EndX=3.2 EndY=-7.66934 EndZ=0
  constraints (10):
    c: Coincident(g0,g-4)
    c: PointOnObject(g0,g-3)
    c: Coincident(g1,g0)
    c: PointOnObject(g1,g-3)
    c: Coincident(g2,g1)
    c: Coincident(g2,g-4)
    c: Coincident(g3,g2)
    c: Coincident(g3,g0)
    c: DistanceX(g-3,g0) = 0.4
    c: DistanceX(g1,g-3) = 0.4
FEATURE [PartDesign::Pocket] Pocket103
  BaseFeature = -> Pad146
  Direction = (0,0,1)
  Length = 2
  Length2 = 5
  Profile = -> Sketch227
  ReferenceAxis = -> Sketch227 [N_Axis]
  Refine = true
  Suppressed = false
  Type = 0
FEATURE [Sketcher::SketchObject] Sketch228
  ArcFitTolerance = 1e-06
  AttachmentSupport = -> [Pocket103]
  ExternalGeometry = -> [Pocket103]
  FullyConstrained = true
  MakeInternals = false
  MapMode = 5
  Placement = pos=(0,0,0) rot=(1,0,0;3.14159rad)
  sketch-geometry (16):
    g0: LineSegment StartX=3.27732 StartY=-7.36934 StartZ=0 EndX=2.42732 EndY=-6.9 EndZ=0
    g1: LineSegment StartX=3.27732 StartY=-7.36934 StartZ=0 EndX=4.62268 EndY=-7.36934 EndZ=0
    g2: LineSegment StartX=4.62268 StartY=-7.36934 StartZ=0 EndX=5.47268 EndY=-6.9 EndZ=0
    g3: LineSegment StartX=5.47268 StartY=-6.9 StartZ=0 EndX=6.9 EndY=-6.9 EndZ=0
    g4: LineSegment StartX=6.9 StartY=-6.9 StartZ=0 EndX=6.9 EndY=-7.2 EndZ=0
    g5: LineSegment StartX=6.9 StartY=-7.2 StartZ=0 EndX=5.55 EndY=-7.2 EndZ=0
    g6: LineSegment StartX=5.55 StartY=-7.2 StartZ=0 EndX=4.7 EndY=-7.66934 EndZ=0
    g7: LineSegment StartX=4.7 StartY=-7.66934 StartZ=0 EndX=3.2 EndY=-7.66934 EndZ=0
    g8: LineSegment StartX=3.2 StartY=-7.66934 StartZ=0 EndX=2.35 EndY=-7.2 EndZ=0
    g9: LineSegment StartX=2.35 StartY=-7.2 StartZ=0 EndX=1 EndY=-7.2 EndZ=0
    g10: LineSegment StartX=1 StartY=-7.2 StartZ=0 EndX=1 EndY=-6.9 EndZ=0
    g11: LineSegment StartX=2.42732 StartY=-6.9 StartZ=0 EndX=1 EndY=-6.9 EndZ=0
    g12: LineSegment [constr] StartX=1 StartY=-5.26914 StartZ=0 EndX=1 EndY=-6.9 EndZ=0
    g13: LineSegment [constr] StartX=6.9 StartY=-5.26914 StartZ=0 EndX=6.9 EndY=-6.9 EndZ=0
    g14: LineSegment [constr] StartX=2.78771 StartY=-7.44169 StartZ=0 EndX=2.93272 EndY=-7.17906 EndZ=0
    g15: LineSegment [constr] StartX=5.11229 StartY=-7.44169 StartZ=0 EndX=4.96728 EndY=-7.17906 EndZ=0
  constraints (44):
    c: Coincident(g1,g0)
    c: Horizontal(g1)
    c: Coincident(g2,g1)
    c: Coincident(g3,g2)
    c: Horizontal(g3)
    c: Coincident(g4,g3)
    c: PointOnObject(g4,g-11)
    c: Coincident(g5,g4)
    c: Coincident(g5,g-6)
    c: Coincident(g6,g5)
    c: Coincident(g6,g-7)
    c: Coincident(g7,g6)
    c: Coincident(g7,g-7)
    c: Coincident(g8,g7)
    c: Coincident(g8,g-8)
    c: Coincident(g9,g8)
    c: PointOnObject(g9,g-10)
    c: Coincident(g10,g9)
    c: Vertical(g10)
    c: Coincident(g11,g0)
    c: Coincident(g11,g10)
    c: Horizontal(g11)
    c: Parallel(g0,g8)
    c: Parallel(g2,g6)
    c: Vertical(g4)
    c: Coincident(g12,g-3)
    c: Coincident(g12,g10)
    c: Vertical(g12)
    c: Coincident(g13,g-4)
    c: Coincident(g13,g3)
    c: Vertical(g13)
    c: DistanceY(g4,g4) = 0.3
    c: DistanceY(g10,g10) = 0.3
    c: DistanceY(g7,g0) = 0.3
    c: Perpendicular(g14,g8)
    c: Distance(g14) = 0.3
    c: PointOnObject(g14,g8)
    c: PointOnObject(g14,g0)
    c: Distance(g14,g8) = 0.5
    c: PointOnObject(g15,g6)
    c: PointOnObject(g15,g2)
    c: Perpendicular(g15,g6)
    c: Distance(g5,g15) = 0.5
    c: Distance(g15) = 0.3
FEATURE [PartDesign::Pad] Pad147
  BaseFeature = -> Pocket103
  Direction = (0,0,-1)
  Length = 1.5
  Length2 = 10
  Profile = -> Sketch228
  ReferenceAxis = -> Sketch228 [N_Axis]
  Refine = true
  Suppressed = false
  Type = 0
FEATURE [Sketcher::SketchObject] Sketch229
  ArcFitTolerance = 1e-06
  AttachmentSupport = -> [Pad147]
  ExternalGeometry = -> [Pad147]
  FullyConstrained = true
  MakeInternals = false
  MapMode = 5
  Placement = pos=(0,6.9,0) rot=(1,0,0;1.5708rad)
  sketch-geometry (6):
    g0: LineSegment StartX=6.9 StartY=-1e-16 StartZ=0 EndX=6.9 EndY=-1.5 EndZ=0
    g1: LineSegment StartX=6.9 StartY=-1.5 StartZ=0 EndX=5.47268 EndY=-1.5 EndZ=0
    g2: LineSegment StartX=5.47268 StartY=-1.5 StartZ=0 EndX=6.9 EndY=2e-16 EndZ=0
    g3: LineSegment StartX=2.42732 StartY=-1.5 StartZ=0 EndX=1 EndY=0 EndZ=0
    g4: LineSegment StartX=2.42732 StartY=-1.5 StartZ=0 EndX=1 EndY=-1.5 EndZ=0
    g5: LineSegment StartX=1 StartY=-1.5 StartZ=0 EndX=1 EndY=0 EndZ=0
  constraints (12):
    c: Coincident(g0,g-6)
    c: Coincident(g0,g-6)
    c: Coincident(g1,g0)
    c: Coincident(g1,g-5)
    c: Coincident(g2,g1)
    c: Coincident(g2,g0)
    c: Coincident(g3,g-3)
    c: Coincident(g3,g-4)
    c: Coincident(g4,g3)
    c: Coincident(g4,g-4)
    c: Coincident(g5,g4)
    c: Coincident(g5,g3)
FEATURE [PartDesign::Pocket] Pocket104
  BaseFeature = -> Pad147
  Direction = (0,1,-2e-16)
  Length = 0.3
  Length2 = 5
  Profile = -> Sketch229
  ReferenceAxis = -> Sketch229 [N_Axis]
  Refine = true
  Suppressed = false
  Type = 0
FEATURE [PartDesign::Pocket] Pocket105
  BaseFeature = -> Pocket104
  Direction = (0,1,0)
  Length = 0.1
  Length2 = 5
  Profile = -> Pocket104 [Face63]
  Refine = true
  Suppressed = false
  Type = 0
FEATURE [PartDesign::Pocket] Pocket106
  BaseFeature = -> Pocket105
  Direction = (0,1,0)
  Length = 0.1
  Length2 = 5
  Profile = -> Pocket105 [Face41]
  Refine = true
  Suppressed = false
  Type = 0
FEATURE [Sketcher::SketchObject] Sketch230
  ArcFitTolerance = 1e-06
  AttachmentSupport = -> [Pocket106]
  ExternalGeometry = -> [Pocket106]
  FullyConstrained = true
  MakeInternals = false
  MapMode = 5
  Placement = pos=(0,0,-1.5) rot=(1,0,0;3.14159rad)
  sketch-geometry (6):
    g0: LineSegment StartX=4.325 StartY=-7.36934 StartZ=0 EndX=4.325 EndY=-5.76934 EndZ=0
    g1: LineSegment StartX=4.325 StartY=-5.76934 StartZ=0 EndX=3.575 EndY=-5.76934 EndZ=0
    g2: LineSegment StartX=3.575 StartY=-5.76934 StartZ=0 EndX=3.575 EndY=-7.36934 EndZ=0
    g3: LineSegment StartX=3.575 StartY=-7.36934 StartZ=0 EndX=4.325 EndY=-7.36934 EndZ=0
    g4: LineSegment [constr] StartX=3.95 StartY=-5.76934 StartZ=0 EndX=3.95 EndY=-7.36934 EndZ=0
    g5: LineSegment [constr] StartX=3.95 StartY=-7.36934 StartZ=0 EndX=3.95 EndY=-7.66934 EndZ=0
  constraints (17):
    c: Coincident(g0,g1)
    c: Coincident(g1,g2)
    c: Coincident(g2,g3)
    c: Coincident(g3,g0)
    c: Vertical(g0)
    c: Vertical(g2)
    c: Horizontal(g1)
    c: Horizontal(g3)
    c: PointOnObject(g0,g-3)
    c: DistanceX(g1,g1) = 0.75
    c: DistanceX(g-3,g-3) = 1.34536
    c: Symmetric(g1,g1,g4)
    c: Symmetric(g3,g3,g4)
    c: Coincident(g5,g4)
    c: Symmetric(g-4,g-4,g5)
    c: Vertical(g5)
    c: DistanceY(g0,g0) = 1.6
FEATURE [PartDesign::Pad] Pad148
  BaseFeature = -> Pocket106
  Direction = (0,0,-1)
  Length = 1.5
  Length2 = 10
  Profile = -> Sketch230
  ReferenceAxis = -> Sketch230 [N_Axis]
  Refine = true
  Reversed = true
  Suppressed = false
  Type = 0
FEATURE [Sketcher::SketchObject] Sketch231
  ArcFitTolerance = 1e-06
  AttachmentSupport = -> [Pad148]
  ExternalGeometry = -> [Pad148]
  FullyConstrained = true
  MakeInternals = false
  MapMode = 5
  Placement = pos=(4.325,0,0) rot=(0.57735,0.57735,0.57735;2.0944rad)
  sketch-geometry (3):
    g0: LineSegment StartX=6.9 StartY=-1.5 StartZ=0 EndX=5.76934 EndY=-1 EndZ=0
    g1: LineSegment StartX=5.76934 StartY=-1 StartZ=0 EndX=5.76934 EndY=-1.5 EndZ=0
    g2: LineSegment StartX=6.9 StartY=-1.5 StartZ=0 EndX=5.76934 EndY=-1.5 EndZ=0
  constraints (7):
    c: Coincident(g0,g-5)
    c: PointOnObject(g0,g-4)
    c: Coincident(g1,g0)
    c: Coincident(g1,g-4)
    c: Coincident(g2,g0)
    c: Coincident(g2,g1)
    c: DistanceY(g1,g1) = 0.5
FEATURE [PartDesign::Pocket] Pocket107
  BaseFeature = -> Pad148
  Direction = (-1,0,0)
  Length = 5
  Length2 = 5
  Profile = -> Sketch231
  ReferenceAxis = -> Sketch231 [N_Axis]
  Refine = true
  Suppressed = false
  Type = 0
FEATURE [PartDesign::SubShapeBinder] Binder005
  BindCopyOnChange = 0
  BindMode = 2
  ClaimChildren = false
  Context = -> Part [Body011.Binder005.]
  Fuse = false
  MakeFace = true
  OffsetFill = false
  OffsetIntersection = false
  OffsetJoinType = 0
  OffsetOpenResult = false
  PartialLoad = false
  Refine = true
  Relative = true
  _Version = 2
FEATURE [Sketcher::SketchObject] Sketch232
  ArcFitTolerance = 1e-06
  AttachmentSupport = -> [Binder005]
  ExternalGeometry = -> [Binder005]
  FullyConstrained = true
  MakeInternals = false
  MapMode = 5
  Placement = pos=(0,0,-1.5) rot=(1,0,0;3.14159rad)
  sketch-geometry (8):
    g0: LineSegment StartX=3.39485 StartY=-1.85 StartZ=0 EndX=4.50515 EndY=-1.85 EndZ=0
    g1: LineSegment StartX=4.50515 StartY=-1.85 StartZ=0 EndX=4.825 EndY=-3.3 EndZ=0
    g2: LineSegment StartX=4.825 StartY=-3.3 StartZ=0 EndX=4.49761 EndY=-5.01914 EndZ=0
    g3: LineSegment StartX=4.49761 StartY=-5.01914 StartZ=0 EndX=3.40239 EndY=-5.01914 EndZ=0
    g4: LineSegment StartX=3.40239 StartY=-5.01914 StartZ=0 EndX=3.075 EndY=-3.3 EndZ=0
    g5: LineSegment StartX=3.075 StartY=-3.3 StartZ=0 EndX=3.39485 EndY=-1.85 EndZ=0
    g6: LineSegment [constr] StartX=4.825 StartY=-3.3 StartZ=0 EndX=4.875 EndY=-3.3 EndZ=0
    g7: LineSegment [constr] StartX=3.075 StartY=-3.3 StartZ=0 EndX=3.025 EndY=-3.3 EndZ=0
  constraints (22):
    c: Horizontal(g0)
    c: Coincident(g1,g0)
    c: Coincident(g2,g1)
    c: Coincident(g3,g2)
    c: Horizontal(g3)
    c: Coincident(g4,g3)
    c: Coincident(g5,g4)
    c: Coincident(g5,g0)
    c: Parallel(g1,g-8)
    c: Parallel(g2,g-7)
    c: Parallel(g4,g-5)
    c: Parallel(g5,g-4)
    c: DistanceY(g0,g-4) = 0.05
    c: DistanceY(g-6,g3) = 0.05
    c: DistanceX(g-5,g4) = 0.05
    c: DistanceX(g1,g-8) = 0.05
    c: Coincident(g6,g1)
    c: Coincident(g6,g-8)
    c: Coincident(g7,g4)
    c: Coincident(g7,g-5)
    c: Horizontal(g7)
    c: Horizontal(g6)
FEATURE [PartDesign::Pad] Pad149
  Direction = (0,0,-1)
  Length = 0.25
  Length2 = 10
  Profile = -> Sketch232
  ReferenceAxis = -> Sketch232 [N_Axis]
  Refine = true
  Suppressed = false
  Type = 0
FEATURE [Sketcher::SketchObject] Sketch233
  ArcFitTolerance = 1e-06
  AttachmentSupport = -> [Pad149]
  ExternalGeometry = -> [Pad149]
  FullyConstrained = true
  MakeInternals = false
  MapMode = 5
  Placement = pos=(0,0,-1.75) rot=(1,0,0;3.14159rad)
  sketch-geometry (8):
    g0: LineSegment StartX=3.375 StartY=-3.3 StartZ=0 EndX=3.64526 EndY=-4.71914 EndZ=0
    g1: LineSegment StartX=3.64526 StartY=-4.71914 StartZ=0 EndX=4.25474 EndY=-4.71914 EndZ=0
    g2: LineSegment StartX=4.25474 StartY=-4.71914 StartZ=0 EndX=4.525 EndY=-3.3 EndZ=0
    g3: LineSegment StartX=4.525 StartY=-3.3 StartZ=0 EndX=4.27132 EndY=-2.15 EndZ=0
    g4: LineSegment StartX=4.27132 StartY=-2.15 StartZ=0 EndX=3.62868 EndY=-2.15 EndZ=0
    g5: LineSegment StartX=3.62868 StartY=-2.15 StartZ=0 EndX=3.375 EndY=-3.3 EndZ=0
    g6: LineSegment [constr] StartX=3.375 StartY=-3.3 StartZ=0 EndX=3.075 EndY=-3.3 EndZ=0
    g7: LineSegment [constr] StartX=4.525 StartY=-3.3 StartZ=0 EndX=4.825 EndY=-3.3 EndZ=0
  constraints (22):
    c: Coincident(g1,g0)
    c: Horizontal(g1)
    c: Coincident(g2,g1)
    c: Coincident(g3,g2)
    c: Coincident(g4,g3)
    c: Horizontal(g4)
    c: Coincident(g5,g4)
    c: Coincident(g5,g0)
    c: DistanceY(g4,g-8) = 0.3
    c: DistanceY(g-6,g0) = 0.3
    c: Parallel(g5,g-7)
    c: Parallel(g3,g-3)
    c: Parallel(g2,g-4)
    c: Parallel(g0,g-6)
    c: Coincident(g6,g0)
    c: Coincident(g6,g-7)
    c: Coincident(g7,g2)
    c: Coincident(g7,g-4)
    c: Horizontal(g6)
    c: Horizontal(g7)
    c: DistanceX(g6,g6) = 0.3
    c: DistanceX(g7,g7) = 0.3
FEATURE [PartDesign::Pad] Pad150
  BaseFeature = -> Pad149
  Direction = (0,0,-1)
  Length = 0.25
  Length2 = 10
  Profile = -> Sketch233
  ReferenceAxis = -> Sketch233 [N_Axis]
  Refine = true
  Suppressed = false
  Type = 0
FEATURE [PartDesign::Body] Body011  label="Forehead"
  AllowCompound = false
  Group = -> [Binder005,Sketch232,Pad149,Sketch233,Pad150]
  Origin = -> Origin012
  Tip = -> Pad150
FEATURE [PartDesign::SubShapeBinder] Binder006
  BindCopyOnChange = 0
  BindMode = 2
  ClaimChildren = false
  Context = -> Part [Body012.Binder006.]
  Fuse = false
  MakeFace = true
  OffsetFill = false
  OffsetIntersection = false
  OffsetJoinType = 0
  OffsetOpenResult = false
  PartialLoad = false
  Refine = true
  Relative = true
  _Version = 2
FEATURE [Sketcher::SketchObject] Sketch234
  ArcFitTolerance = 1e-06
  AttachmentSupport = -> [Binder006]
  ExternalGeometry = -> [Binder006]
  FullyConstrained = true
  MakeInternals = false
  MapMode = 5
  Placement = pos=(0,0,0) rot=(1,0,0;3.14159rad)
  sketch-geometry (14):
    g0: LineSegment StartX=1.3 StartY=-5.3 StartZ=0 EndX=6.6 EndY=-5.3 EndZ=0
    g1: LineSegment StartX=6.6 StartY=-5.3 StartZ=0 EndX=6.6 EndY=-6.85 EndZ=0
    g2: LineSegment StartX=6.6 StartY=-6.85 StartZ=0 EndX=5.47268 EndY=-6.85 EndZ=0
    g3: LineSegment StartX=5.47268 StartY=-6.85 StartZ=0 EndX=4.62268 EndY=-7.31934 EndZ=0
    g4: LineSegment StartX=4.62268 StartY=-7.31934 StartZ=0 EndX=4.375 EndY=-7.31934 EndZ=0
    g5: LineSegment StartX=4.375 StartY=-7.31934 StartZ=0 EndX=4.375 EndY=-5.71934 EndZ=0
    g6: LineSegment StartX=4.375 StartY=-5.71934 StartZ=0 EndX=3.525 EndY=-5.71934 EndZ=0
    g7: LineSegment StartX=3.525 StartY=-5.71934 StartZ=0 EndX=3.525 EndY=-7.31934 EndZ=0
    g8: LineSegment StartX=3.525 StartY=-7.31934 StartZ=0 EndX=3.27732 EndY=-7.31934 EndZ=0
    g9: LineSegment StartX=3.27732 StartY=-7.31934 StartZ=0 EndX=2.42732 EndY=-6.85 EndZ=0
    g10: LineSegment StartX=2.42732 StartY=-6.85 StartZ=0 EndX=1.3 EndY=-6.85 EndZ=0
    g11: LineSegment StartX=1.3 StartY=-6.85 StartZ=0 EndX=1.3 EndY=-5.3 EndZ=0
    g12: LineSegment [constr] StartX=2.42732 StartY=-6.9 StartZ=0 EndX=2.42732 EndY=-6.85 EndZ=0
    g13: LineSegment [constr] StartX=5.47268 StartY=-6.9 StartZ=0 EndX=5.47268 EndY=-6.85 EndZ=0
  constraints (40):
    c: Horizontal(g0)
    c: Coincident(g1,g0)
    c: Vertical(g1)
    c: Coincident(g2,g1)
    c: Horizontal(g2)
    c: Coincident(g3,g2)
    c: Coincident(g4,g3)
    c: Horizontal(g4)
    c: Coincident(g5,g4)
    c: Vertical(g5)
    c: Coincident(g6,g5)
    c: Horizontal(g6)
    c: Coincident(g7,g6)
    c: Vertical(g7)
    c: Coincident(g8,g7)
    c: Horizontal(g8)
    c: Coincident(g9,g8)
    c: Coincident(g10,g9)
    c: Horizontal(g10)
    c: Coincident(g11,g10)
    c: Coincident(g11,g0)
    c: Vertical(g11)
    c: DistanceX(g-10,g0) = 0.3
    c: DistanceX(g0,g-3) = 0.3
    c: DistanceY(g0,g-3) = 0.1
    c: DistanceY(g-4,g1) = 0.05
    c: Parallel(g3,g-5)
    c: Parallel(g9,g-13)
    c: DistanceY(g-12,g7) = 0.05
    c: DistanceY(g-7,g4) = 0.05
    c: DistanceX(g-7,g4) = 0.05
    c: DistanceX(g7,g-12) = 0.05
    c: DistanceY(g-14,g10) = 0.05
    c: Coincident(g12,g-14)
    c: Coincident(g12,g9)
    c: Vertical(g12)
    c: Coincident(g13,g-5)
    c: Coincident(g13,g2)
    c: Vertical(g13)
    c: DistanceY(g-8,g5) = 0.05
FEATURE [PartDesign::Pad] Pad151
  Direction = (0,0,-1)
  Length = 1
  Length2 = 10
  Profile = -> Sketch234
  ReferenceAxis = -> Sketch234 [N_Axis]
  Refine = true
  Suppressed = false
  Type = 0
FEATURE [Sketcher::SketchObject] Sketch235
  ArcFitTolerance = 1e-06
  AttachmentSupport = -> [Pad151]
  ExternalGeometry = -> [Pad151]
  FullyConstrained = true
  MakeInternals = false
  MapMode = 5
  Placement = pos=(0,5.3,0) rot=(1,0,0;1.5708rad)
  sketch-geometry (4):
    g0: LineSegment StartX=1.3 StartY=-0.2 StartZ=0 EndX=1.3 EndY=-1 EndZ=0
    g1: LineSegment StartX=1.3 StartY=-1 StartZ=0 EndX=6.6 EndY=-1 EndZ=0
    g2: LineSegment StartX=6.6 StartY=-1 StartZ=0 EndX=6.6 EndY=-0.2 EndZ=0
    g3: ArcOfCircle CenterX=3.95 CenterY=3.78906 CenterZ=0 NormalX=0 NormalY=0 NormalZ=1 AngleXU=0 Radius=4.78906 StartAngle=4.12602 EndAngle=5.29876
  constraints (11):
    c: PointOnObject(g0,g-5)
    c: Coincident(g0,g-5)
    c: Coincident(g1,g0)
    c: Coincident(g1,g-4)
    c: Coincident(g2,g1)
    c: PointOnObject(g2,g-4)
    c: DistanceY(g0,g-5) = 0.2
    c: DistanceY(g2,g-4) = 0.2
    c: Coincident(g3,g2)
    c: Coincident(g3,g0)
    c: Tangent(g3,g1)
FEATURE [PartDesign::Pocket] Pocket108
  BaseFeature = -> Pad151
  Direction = (0,1,-2e-16)
  Length = 5
  Length2 = 5
  Profile = -> Sketch235
  ReferenceAxis = -> Sketch235 [N_Axis]
  Refine = true
  Suppressed = false
  Type = 0
FEATURE [PartDesign::Body] Body012  label="Eyes"
  AllowCompound = false
  Group = -> [Binder006,Sketch234,Pad151,Sketch235,Pocket108]
  Origin = -> Origin013
  Tip = -> Pocket108
FEATURE [PartDesign::SubShapeBinder] Binder007
  BindCopyOnChange = 0
  BindMode = 2
  ClaimChildren = false
  Context = -> Part [Body013.Binder007.]
  Fuse = false
  MakeFace = true
  OffsetFill = false
  OffsetIntersection = false
  OffsetJoinType = 0
  OffsetOpenResult = false
  PartialLoad = false
  Refine = true
  Relative = true
  _Version = 2
FEATURE [Sketcher::SketchObject] Sketch236
  ArcFitTolerance = 1e-06
  AttachmentSupport = -> [Binder007]
  ExternalGeometry = -> [Binder007]
  FullyConstrained = true
  MakeInternals = false
  MapMode = 5
  Placement = pos=(0,0,-1) rot=(1,0,0;3.14159rad)
  sketch-geometry (4):
    g0: LineSegment StartX=3.2 StartY=-7.66934 StartZ=0 EndX=3.2 EndY=-9.79934 EndZ=0
    g1: LineSegment StartX=3.2 StartY=-9.79934 StartZ=0 EndX=4.7 EndY=-9.79934 EndZ=0
    g2: LineSegment StartX=4.7 StartY=-9.79934 StartZ=0 EndX=4.7 EndY=-7.66934 EndZ=0
    g3: LineSegment StartX=4.7 StartY=-7.66934 StartZ=0 EndX=3.2 EndY=-7.66934 EndZ=0
  constraints (11):
    c: Coincident(g0,g1)
    c: Coincident(g1,g2)
    c: Coincident(g2,g3)
    c: Coincident(g3,g0)
    c: Vertical(g0)
    c: Vertical(g2)
    c: Horizontal(g1)
    c: Horizontal(g3)
    c: Coincident(g0,g-4)
    c: PointOnObject(g-6,g2)
    c: DistanceY(g0,g0) = 2.13
FEATURE [PartDesign::Pad] Pad152
  Direction = (0,0,-1)
  Length = 1
  Length2 = 10
  Profile = -> Sketch236
  ReferenceAxis = -> Sketch236 [N_Axis]
  Refine = true
  Suppressed = false
  Type = 0
FEATURE [Sketcher::SketchObject] Sketch237
  ArcFitTolerance = 1e-06
  AttachmentSupport = -> [Pad152]
  ExternalGeometry = -> [Pad152]
  FullyConstrained = true
  MakeInternals = false
  MapMode = 5
  Placement = pos=(3.2,0,0) rot=(0.57735,-0.57735,-0.57735;2.0944rad)
  sketch-geometry (3):
    g0: LineSegment StartX=-9.79934 StartY=-2 StartZ=0 EndX=-7.66934 EndY=-1.5 EndZ=0
    g1: LineSegment StartX=-7.66934 StartY=-1.5 StartZ=0 EndX=-7.66934 EndY=-2 EndZ=0
    g2: LineSegment StartX=-7.66934 StartY=-2 StartZ=0 EndX=-9.79934 EndY=-2 EndZ=0
  constraints (7):
    c: Coincident(g0,g-4)
    c: PointOnObject(g0,g-3)
    c: Coincident(g1,g0)
    c: Coincident(g1,g-4)
    c: Coincident(g2,g1)
    c: Coincident(g2,g0)
    c: DistanceY(g1,g1) = 0.5
FEATURE [PartDesign::Pocket] Pocket109
  BaseFeature = -> Pad152
  Direction = (1,0,0)
  Length = 5
  Length2 = 5
  Profile = -> Sketch237
  ReferenceAxis = -> Sketch237 [N_Axis]
  Refine = true
  Suppressed = false
  Type = 0
FEATURE [PartDesign::Body] Body013  label="Chin"
  AllowCompound = false
  Group = -> [Binder007,Sketch236,Pad152,Sketch237,Pocket109]
  Origin = -> Origin014
  Tip = -> Pocket109
FEATURE [Sketcher::SketchObject] Sketch238
  ArcFitTolerance = 1e-06
  AttachmentSupport = -> [XY_Plane016]
  FullyConstrained = true
  MakeInternals = false
  MapMode = 5
  sketch-geometry (12):
    g0: ArcOfCircle CenterX=0 CenterY=0 CenterZ=0 NormalX=0 NormalY=0 NormalZ=1 AngleXU=0 Radius=6.5 StartAngle=1.66324 EndAngle=4.71239
    g1: ArcOfCircle [constr] CenterX=37 CenterY=0 CenterZ=0 NormalX=0 NormalY=0 NormalZ=1 AngleXU=0 Radius=6.5 StartAngle=4.71239 EndAngle=7.76154
    g2: LineSegment [constr] StartX=37 StartY=0 StartZ=0 EndX=37 EndY=-6.5 EndZ=0
    g3: LineSegment [constr] StartX=0 StartY=0 StartZ=0 EndX=-6.5 EndY=0 EndZ=0
    g4: LineSegment [constr] StartX=37 StartY=0 StartZ=0 EndX=43.5 EndY=0 EndZ=0
    g5: LineSegment StartX=-1.2e-15 StartY=-6.5 StartZ=0 EndX=33.5 EndY=-6.5 EndZ=0
    g6: LineSegment [constr] StartX=16.75 StartY=0 StartZ=0 EndX=16.75 EndY=-6.5 EndZ=0
    g7: LineSegment StartX=33.5 StartY=-6.5 StartZ=0 EndX=33.5 EndY=6.87017 EndZ=0
    g8: LineSegment [constr] StartX=16.75 StartY=0 StartZ=0 EndX=16.75 EndY=7.5 EndZ=0
    g9: ArcOfCircle CenterX=18.5 CenterY=-169.004 CenterZ=0 NormalX=0 NormalY=0 NormalZ=1 AngleXU=0 Radius=176.512 StartAngle=1.48571 EndAngle=1.67922
    g10: LineSegment [constr] StartX=3.5 StartY=6.87017 StartZ=0 EndX=3.5 EndY=-6.5 EndZ=0
    g11: LineSegment [constr] StartX=3.5 StartY=6.87017 StartZ=0 EndX=33.5 EndY=6.87017 EndZ=0
  constraints (41):
    c: PointOnObject(g0,g-2)
    c: Diameter(g0) = 13
    c: Coincident(g0,g-1)
    c: PointOnObject(g1,g-1)
    c: Diameter(g1) = 13
    c: Coincident(g2,g1)
    c: Coincident(g2,g1)
    c: Vertical(g2)
    c: Coincident(g3,g0)
    c: PointOnObject(g3,g0)
    c: Horizontal(g3)
    c: Coincident(g4,g1)
    c: PointOnObject(g4,g1)
    c: PointOnObject(g4,g-1)
    c: DistanceX(g3,g4) = 50
    c: DistanceX(g0,g1) = 37
    c: Coincident(g5,g0)
    c: Horizontal(g5)
    c: DistanceX(g3,g5) = 40
    c: PointOnObject(g6,g-1)
    c: Symmetric(g5,g5,g6)
    c: Vertical(g6)
    c: DistanceY(g6,g6) = 6.5
    c: Coincident(g7,g5)
    c: Vertical(g7)
    c: Coincident(g8,g6)
    c: Vertical(g8)
    c: DistanceY(g8,g8) = 7.5
    c: PointOnObject(g8,g9)
    c: Coincident(g9,g0)
    c: DistanceX(g0,g0) = 0.6
    c: PointOnObject(g10,g9)
    c: PointOnObject(g10,g5)
    c: Vertical(g10)
    c: DistanceX(g3,g10) = 10
    c: Coincident(g9,g7)
    c: Coincident(g11,g10)
    c: Coincident(g11,g7)
    c: Horizontal(g11)
    c: DistanceX(g1,g1) = 0.6
    c: DistanceY(g5,g7) = 13.3702
FEATURE [PartDesign::Pad] Pad153
  Direction = (0,0,1)
  Length = 1.5
  Length2 = 10
  Profile = -> Sketch238
  ReferenceAxis = -> Sketch238 [N_Axis]
  Refine = true
  Suppressed = false
  Type = 0
FEATURE [Sketcher::SketchObject] Sketch239
  ArcFitTolerance = 1e-06
  AttachmentSupport = -> [Pad153]
  ExternalGeometry = -> [Pad153]
  FullyConstrained = true
  MakeInternals = false
  MapMode = 5
  Placement = pos=(0,0,1.5) rot=(0,0,1;0rad)
  sketch-geometry (10):
    g0: ArcOfCircle CenterX=18.5181 CenterY=-169.001 CenterZ=0 NormalX=0 NormalY=0 NormalZ=1 AngleXU=0 Radius=175.512 StartAngle=1.48533 EndAngle=1.67941
    g1: ArcOfCircle CenterX=0 CenterY=0 CenterZ=0 NormalX=0 NormalY=0 NormalZ=1 AngleXU=0 Radius=5.5 StartAngle=1.66324 EndAngle=4.71239
    g2: LineSegment StartX=-1e-15 StartY=-5.5 StartZ=0 EndX=33.5 EndY=-5.5 EndZ=0
    g3: LineSegment [constr] StartX=0 StartY=0 StartZ=0 EndX=-0.507692 EndY=5.47652 EndZ=0
    g4: LineSegment [constr] StartX=-0.507692 StartY=5.47652 StartZ=0 EndX=-0.6 EndY=6.47225 EndZ=0
    g5: LineSegment StartX=33.5 StartY=5.87017 StartZ=0 EndX=33.5 EndY=5.37017 EndZ=0
    g6: LineSegment StartX=33.5 StartY=-5.5 StartZ=0 EndX=33.5 EndY=-5 EndZ=0
    g7: LineSegment StartX=33.5 StartY=-5 StartZ=0 EndX=0 EndY=-5 EndZ=0
    g8: ArcOfCircle CenterX=0 CenterY=0 CenterZ=0 NormalX=0 NormalY=0 NormalZ=1 AngleXU=0 Radius=5 StartAngle=1.66324 EndAngle=4.71239
    g9: ArcOfCircle CenterX=18.5272 CenterY=-169 CenterZ=0 NormalX=0 NormalY=0 NormalZ=1 AngleXU=0 Radius=175.012 StartAngle=1.48514 EndAngle=1.67951
  constraints (32):
    c: Coincident(g1,g0)
    c: PointOnObject(g1,g-2)
    c: Coincident(g2,g1)
    c: PointOnObject(g2,g-4)
    c: Horizontal(g2)
    c: PointOnObject(g0,g-4)
    c: Radius(g-6) = 6.5
    c: Radius(g1) = 5.5
    c: Coincident(g1,g-1)
    c: Coincident(g3,g1)
    c: Coincident(g3,g0)
    c: Coincident(g4,g0)
    c: Coincident(g4,g-6)
    c: Parallel(g4,g3)
    c: Radius(g-3) = 176.512
    c: Radius(g0) = 175.512
    c: DistanceY(g0,g-4) = 1
    c: Coincident(g5,g0)
    c: PointOnObject(g5,g-4)
    c: Coincident(g6,g2)
    c: PointOnObject(g6,g-4)
    c: Coincident(g7,g6)
    c: PointOnObject(g7,g-2)
    c: Horizontal(g7)
    c: Coincident(g8,g7)
    c: PointOnObject(g8,g3)
    c: Coincident(g8,g1)
    c: DistanceY(g1,g7) = 0.5
    c: DistanceY(g5,g5) = 0.5
    c: Coincident(g9,g5)
    c: Coincident(g9,g8)
    c: Radius(g9) = 175.012
FEATURE [PartDesign::Pocket] Pocket110
  BaseFeature = -> Pad153
  Direction = (0,0,-1)
  Length = 0.3
  Length2 = 5
  Profile = -> Sketch239
  ReferenceAxis = -> Sketch239 [N_Axis]
  Refine = true
  Suppressed = false
  Type = 0
FEATURE [Sketcher::SketchObject] Sketch240
  ArcFitTolerance = 1e-06
  AttachmentSupport = -> [Pocket110]
  ExternalGeometry = -> [Pocket110]
  FullyConstrained = true
  MakeInternals = false
  MapMode = 5
  Placement = pos=(0,0,0) rot=(1,0,0;3.14159rad)
  sketch-geometry (9):
    g0: LineSegment StartX=33.5 StartY=6.5 StartZ=0 EndX=0 EndY=6.5 EndZ=0
    g1: ArcOfCircle CenterX=0 CenterY=-3e-16 CenterZ=0 NormalX=0 NormalY=0 NormalZ=1 AngleXU=0 Radius=6.5 StartAngle=1.5708 EndAngle=4.61995
    g2: ArcOfCircle CenterX=18.5 CenterY=169.004 CenterZ=0 NormalX=0 NormalY=0 NormalZ=1 AngleXU=0 Radius=176.512 StartAngle=4.60397 EndAngle=4.79747
    g3: LineSegment StartX=33.5 StartY=6.5 StartZ=0 EndX=33.5 EndY=5 EndZ=0
    g4: LineSegment StartX=33.5 StartY=5 StartZ=0 EndX=0 EndY=5 EndZ=0
    g5: LineSegment StartX=33.5 StartY=-6.87017 StartZ=0 EndX=33.5 EndY=-5.37017 EndZ=0
    g6: LineSegment [constr] StartX=0 StartY=-3e-16 StartZ=0 EndX=-0.6 EndY=-6.47225 EndZ=0
    g7: ArcOfCircle CenterX=0 CenterY=-3e-16 CenterZ=0 NormalX=0 NormalY=0 NormalZ=1 AngleXU=0 Radius=5 StartAngle=1.5708 EndAngle=4.61995
    g8: ArcOfCircle CenterX=18.5272 CenterY=169 CenterZ=0 NormalX=0 NormalY=0 NormalZ=1 AngleXU=0 Radius=175.012 StartAngle=4.60368 EndAngle=4.79805
  constraints (24):
    c: Coincident(g0,g-4)
    c: Coincident(g0,g-6)
    c: Coincident(g1,g0)
    c: Tangent(g1,g-6) = -1.5708
    c: Coincident(g2,g1)
    c: Tangent(g2,g-5) = -1.5708
    c: Coincident(g3,g0)
    c: PointOnObject(g3,g-4)
    c: Coincident(g4,g3)
    c: PointOnObject(g4,g-2)
    c: Horizontal(g4)
    c: DistanceY(g3,g3) = 1.5
    c: Coincident(g5,g2)
    c: PointOnObject(g5,g-4)
    c: DistanceY(g5,g5) = 1.5
    c: Coincident(g6,g1)
    c: Coincident(g6,g1)
    c: Coincident(g7,g4)
    c: PointOnObject(g7,g6)
    c: Coincident(g7,g1)
    c: Coincident(g8,g7)
    c: Coincident(g8,g5)
    c: Radius(g2) = 176.512
    c: Radius(g8) = 175.012
FEATURE [PartDesign::Pad] Pad154
  BaseFeature = -> Pocket110
  Direction = (0,0,-1)
  Length = 2.5
  Length2 = 10
  Profile = -> Sketch240
  ReferenceAxis = -> Sketch240 [N_Axis]
  Refine = true
  Suppressed = false
  Type = 0
FEATURE [Sketcher::SketchObject] Sketch241
  ArcFitTolerance = 1e-06
  AttachmentSupport = -> [Pad154]
  ExternalGeometry = -> [Pad154]
  FullyConstrained = true
  MakeInternals = false
  MapMode = 5
  Placement = pos=(0,0,-2.5) rot=(1,0,0;3.14159rad)
  sketch-geometry (61):
    g0: ArcOfCircle CenterX=33.0017 CenterY=-6.91196 CenterZ=0 NormalX=0 NormalY=0 NormalZ=1 AngleXU=0 Radius=0.5 StartAngle=3.22243 EndAngle=6.36685
    g1: ArcOfCircle CenterX=25.4163 CenterY=-7.37312 CenterZ=0 NormalX=0 NormalY=0 NormalZ=1 AngleXU=0 Radius=0.5 StartAngle=3.17937 EndAngle=6.32379
    g2: ArcOfCircle CenterX=29.2115 CenterY=-7.18337 CenterZ=0 NormalX=0 NormalY=0 NormalZ=1 AngleXU=0 Radius=0.5 StartAngle=3.2009 EndAngle=6.34532
    g3: ArcOfCircle CenterX=10.221 CenterY=-7.31441 CenterZ=0 NormalX=0 NormalY=0 NormalZ=1 AngleXU=0 Radius=0.5 StartAngle=3.09326 EndAngle=6.23768
    g4: ArcOfCircle CenterX=2.6393 CenterY=-6.79464 CenterZ=0 NormalX=0 NormalY=0 NormalZ=1 AngleXU=0 Radius=0.5 StartAngle=3.0502 EndAngle=6.19462
    g5: ArcOfCircle CenterX=21.6179 CenterY=-7.48114 CenterZ=0 NormalX=0 NormalY=0 NormalZ=1 AngleXU=0 Radius=0.5 StartAngle=3.15784 EndAngle=6.30227
    g6: ArcOfCircle CenterX=17.818 CenterY=-7.50736 CenterZ=0 NormalX=0 NormalY=0 NormalZ=1 AngleXU=0 Radius=0.5 StartAngle=3.13631 EndAngle=6.28074
    g7: ArcOfCircle CenterX=14.0184 CenterY=-7.45177 CenterZ=0 NormalX=0 NormalY=0 NormalZ=1 AngleXU=0 Radius=0.5 StartAngle=3.11478 EndAngle=6.25921
    g8: ArcOfCircle CenterX=6.42734 CenterY=-7.09533 CenterZ=0 NormalX=0 NormalY=0 NormalZ=1 AngleXU=0 Radius=0.5 StartAngle=3.07173 EndAngle=6.21615
    g9: ArcOfCircle CenterX=-1.15373 CenterY=-6.39679 CenterZ=0 NormalX=0 NormalY=0 NormalZ=1 AngleXU=0 Radius=0.5 StartAngle=2.92468 EndAngle=6.14321
    g10: ArcOfCircle CenterX=33 CenterY=6.5 CenterZ=0 NormalX=0 NormalY=0 NormalZ=1 AngleXU=0 Radius=0.5 StartAngle=4e-16 EndAngle=3.14159
    g11: ArcOfCircle CenterX=29.2105 CenterY=6.5 CenterZ=0 NormalX=0 NormalY=0 NormalZ=1 AngleXU=0 Radius=0.5 StartAngle=0 EndAngle=3.14159
    g12: ArcOfCircle CenterX=25.4159 CenterY=6.5 CenterZ=0 NormalX=0 NormalY=0 NormalZ=1 AngleXU=0 Radius=0.5 StartAngle=-9e-16 EndAngle=3.14159
    g13: ArcOfCircle CenterX=21.6178 CenterY=6.5 CenterZ=0 NormalX=0 NormalY=0 NormalZ=1 AngleXU=0 Radius=0.5 StartAngle=3e-16 EndAngle=3.14159
    g14: ArcOfCircle CenterX=17.818 CenterY=6.5 CenterZ=0 NormalX=0 NormalY=0 NormalZ=1 AngleXU=0 Radius=0.5 StartAngle=0 EndAngle=3.14159
    g15: ArcOfCircle CenterX=14.0183 CenterY=6.5 CenterZ=0 NormalX=0 NormalY=0 NormalZ=1 AngleXU=0 Radius=0.5 StartAngle=0 EndAngle=3.14159
    g16: ArcOfCircle CenterX=10.2205 CenterY=6.5 CenterZ=0 NormalX=0 NormalY=0 NormalZ=1 AngleXU=0 Radius=0.5 StartAngle=2e-16 EndAngle=3.14159
    g17: ArcOfCircle CenterX=6.42621 CenterY=6.5 CenterZ=0 NormalX=0 NormalY=0 NormalZ=1 AngleXU=0 Radius=0.5 StartAngle=3e-16 EndAngle=3.14159
    g18: ArcOfCircle CenterX=2.63734 CenterY=6.5 CenterZ=0 NormalX=0 NormalY=0 NormalZ=1 AngleXU=0 Radius=0.5 StartAngle=0 EndAngle=3.14159
    g19: ArcOfCircle CenterX=-1.15373 CenterY=6.39679 CenterZ=0 NormalX=0 NormalY=0 NormalZ=1 AngleXU=0 Radius=0.5 StartAngle=0.139971 EndAngle=3.35851
    g20: LineSegment [constr] StartX=29.7105 StartY=-7.15232 StartZ=0 EndX=29.7105 EndY=6.5 EndZ=0
    g21: LineSegment [constr] StartX=25.9159 StartY=-7.35282 StartZ=0 EndX=25.9159 EndY=6.5 EndZ=0
    g22: LineSegment [constr] StartX=22.1178 StartY=-7.4716 StartZ=0 EndX=22.1178 EndY=6.5 EndZ=0
    g23: LineSegment [constr] StartX=18.318 StartY=-7.50858 StartZ=0 EndX=18.318 EndY=6.5 EndZ=0
    g24: LineSegment [constr] StartX=14.5183 StartY=-7.46376 StartZ=0 EndX=14.5183 EndY=6.5 EndZ=0
    g25: LineSegment [constr] StartX=10.7205 StartY=-7.33716 StartZ=0 EndX=10.7205 EndY=6.5 EndZ=0
    g26: LineSegment [constr] StartX=6.92621 StartY=-7.12882 StartZ=0 EndX=6.92621 EndY=6.5 EndZ=0
    g27: LineSegment [constr] StartX=3.13734 StartY=-6.83886 StartZ=0 EndX=3.13734 EndY=6.5 EndZ=0
    g28: LineSegment [constr] StartX=-0.658617 StartY=-6.46655 StartZ=0 EndX=-0.658617 EndY=6.46655 EndZ=0
    g29: ArcOfCircle CenterX=-6.5 CenterY=0 CenterZ=0 NormalX=0 NormalY=0 NormalZ=1 AngleXU=0 Radius=0.5 StartAngle=1.53233 EndAngle=4.75086
    g30: ArcOfCircle CenterX=-3.88826 CenterY=5.20878 CenterZ=0 NormalX=0 NormalY=0 NormalZ=1 AngleXU=0 Radius=0.5 StartAngle=0.602774 EndAngle=3.82131
    g31: ArcOfCircle CenterX=-5.80474 CenterY=2.9249 CenterZ=0 NormalX=0 NormalY=0 NormalZ=1 AngleXU=0 Radius=0.5 StartAngle=1.06558 EndAngle=4.28411
    g32: ArcOfCircle CenterX=-3.88826 CenterY=-5.20878 CenterZ=0 NormalX=0 NormalY=0 NormalZ=1 AngleXU=0 Radius=0.5 StartAngle=2.46188 EndAngle=5.68041
    g33: ArcOfCircle CenterX=-5.80474 CenterY=-2.9249 CenterZ=0 NormalX=0 NormalY=0 NormalZ=1 AngleXU=0 Radius=0.5 StartAngle=1.99907 EndAngle=5.21761
    g34: LineSegment [constr] StartX=-3.47638 StartY=-5.49225 StartZ=0 EndX=-3.47638 EndY=5.49225 EndZ=0
    g35: LineSegment [constr] StartX=-5.56274 StartY=-3.36243 StartZ=0 EndX=-5.56274 EndY=3.36243 EndZ=0
    g36: LineSegment StartX=33.5 StartY=-6.87017 StartZ=0 EndX=32.5034 EndY=-6.95233 EndZ=0
    g37: LineSegment StartX=29.7105 StartY=-7.15232 StartZ=0 EndX=28.7124 EndY=-7.213 EndZ=0
    g38: LineSegment StartX=25.9159 StartY=-7.35282 StartZ=0 EndX=24.9166 EndY=-7.39201 EndZ=0
    g39: LineSegment StartX=22.1178 StartY=-7.4716 StartZ=0 EndX=21.1179 EndY=-7.48926 EndZ=0
    g40: LineSegment StartX=18.318 StartY=-7.50858 StartZ=0 EndX=17.318 EndY=-7.50472 EndZ=0
    g41: LineSegment StartX=14.5183 StartY=-7.46376 StartZ=0 EndX=13.5186 EndY=-7.43837 EndZ=0
    g42: LineSegment StartX=10.7205 StartY=-7.33716 StartZ=0 EndX=9.72156 EndY=-7.29025 EndZ=0
    g43: LineSegment StartX=6.92621 StartY=-7.12882 StartZ=0 EndX=5.92856 EndY=-7.06043 EndZ=0
    g44: LineSegment StartX=3.13734 StartY=-6.83886 StartZ=0 EndX=2.14138 EndY=-6.74901 EndZ=0
    g45: LineSegment StartX=-0.658617 StartY=-6.46655 StartZ=0 EndX=-1.64201 EndY=-6.28918 EndZ=0
    g46: LineSegment StartX=-3.47638 StartY=-5.49225 StartZ=0 EndX=-4.27713 EndY=-4.8945 EndZ=0
    g47: LineSegment StartX=-5.56274 StartY=-3.36243 StartZ=0 EndX=-6.01239 EndY=-2.47006 EndZ=0
    g48: LineSegment StartX=-6.48077 StartY=-0.49963 StartZ=0 EndX=-6.48077 EndY=0.49963 EndZ=0
    g49: LineSegment StartX=-6.01239 StartY=2.47006 StartZ=0 EndX=-5.56274 EndY=3.36243 EndZ=0
    g50: LineSegment StartX=-4.27713 StartY=4.8945 StartZ=0 EndX=-3.47638 EndY=5.49225 EndZ=0
    g51: LineSegment StartX=-1.64201 StartY=6.28918 StartZ=0 EndX=-0.658617 EndY=6.46655 EndZ=0
    g52: LineSegment StartX=2.13734 StartY=6.5 StartZ=0 EndX=3.13734 EndY=6.5 EndZ=0
    g53: LineSegment StartX=5.92621 StartY=6.5 StartZ=0 EndX=6.92621 EndY=6.5 EndZ=0
    g54: LineSegment StartX=9.72046 StartY=6.5 StartZ=0 EndX=10.7205 EndY=6.5 EndZ=0
    g55: LineSegment StartX=13.5183 StartY=6.5 StartZ=0 EndX=14.5183 EndY=6.5 EndZ=0
    g56: LineSegment StartX=17.318 StartY=6.5 StartZ=0 EndX=18.318 EndY=6.5 EndZ=0
    g57: LineSegment StartX=21.1178 StartY=6.5 StartZ=0 EndX=22.1178 EndY=6.5 EndZ=0
    g58: LineSegment StartX=24.9159 StartY=6.5 StartZ=0 EndX=25.9159 EndY=6.5 EndZ=0
    g59: LineSegment StartX=28.7105 StartY=6.5 StartZ=0 EndX=29.7105 EndY=6.5 EndZ=0
    g60: LineSegment StartX=32.5 StartY=6.5 StartZ=0 EndX=33.5 EndY=6.5 EndZ=0
  constraints (196):
    c: Coincident(g0,g-3)
    c: PointOnObject(g0,g-3)
    c: PointOnObject(g1,g-3)
    c: PointOnObject(g1,g-3)
    c: PointOnObject(g2,g-3)
    c: PointOnObject(g2,g-3)
    c: PointOnObject(g3,g-3)
    c: PointOnObject(g3,g-3)
    c: PointOnObject(g4,g-3)
    c: PointOnObject(g4,g-3)
    c: PointOnObject(g0,g-3)
    c: PointOnObject(g1,g-3)
    c: PointOnObject(g2,g-3)
    c: PointOnObject(g3,g-3)
    c: PointOnObject(g4,g-3)
    c: Diameter(g0) = 1
    c: Diameter(g1) = 1
    c: Diameter(g2) = 1
    c: Diameter(g3) = 1
    c: Diameter(g4) = 1
    c: Diameter(g5) = 1
    c: PointOnObject(g5,g-3)
    c: PointOnObject(g5,g-3)
    c: PointOnObject(g5,g-3)
    c: PointOnObject(g6,g-3)
    c: PointOnObject(g6,g-3)
    c: PointOnObject(g7,g-3)
    c: PointOnObject(g7,g-3)
    c: PointOnObject(g6,g-3)
    c: PointOnObject(g7,g-3)
    c: Diameter(g7) = 1
    c: Diameter(g6) = 1
    c: PointOnObject(g8,g-3)
    c: PointOnObject(g8,g-3)
    c: PointOnObject(g8,g-3)
    c: Diameter(g8) = 1
    c: Distance(g0,g2) = 2.8
    c: Distance(g2,g1) = 2.8
    c: Distance(g1,g5) = 2.8
    c: Distance(g5,g6) = 2.8
    c: Distance(g6,g7) = 2.8
    c: Distance(g7,g3) = 2.8
    c: Distance(g3,g8) = 2.8
    c: Distance(g8,g4) = 2.8
    c: Diameter(g9) = 1
    c: DistanceX(g9,g4) = 2.8
    c: PointOnObject(g9,g-5)
    c: PointOnObject(g9,g-5)
    c: PointOnObject(g9,g-5)
    c: Coincident(g10,g-4)
    c: PointOnObject(g10,g-4)
    c: PointOnObject(g11,g-4)
    c: PointOnObject(g11,g-4)
    c: PointOnObject(g12,g-4)
    c: PointOnObject(g12,g-4)
    c: PointOnObject(g13,g-4)
    c: PointOnObject(g13,g-4)
    c: PointOnObject(g14,g-4)
    c: PointOnObject(g14,g-4)
    c: PointOnObject(g15,g-4)
    c: PointOnObject(g15,g-4)
    c: PointOnObject(g16,g-4)
    c: PointOnObject(g16,g-4)
    c: PointOnObject(g17,g-4)
    c: PointOnObject(g17,g-4)
    c: PointOnObject(g18,g-4)
    c: PointOnObject(g18,g-4)
    c: PointOnObject(g10,g-4)
    c: PointOnObject(g11,g-4)
    c: PointOnObject(g12,g-4)
    c: PointOnObject(g13,g-4)
    c: PointOnObject(g14,g-4)
    c: PointOnObject(g15,g-4)
    c: PointOnObject(g16,g-4)
    c: PointOnObject(g17,g-4)
    c: PointOnObject(g18,g-4)
    c: Diameter(g10) = 1
    c: Diameter(g11) = 1
    c: Diameter(g12) = 1
    c: Diameter(g13) = 1
    c: Diameter(g14) = 1
    c: Diameter(g15) = 1
    c: Diameter(g16) = 1
    c: Diameter(g17) = 1
    c: Diameter(g18) = 1
    c: Diameter(g19) = 1
    c: Coincident(g20,g2)
    c: Coincident(g20,g11)
    c: Vertical(g20)
    c: Coincident(g21,g1)
    c: Coincident(g21,g12)
    c: Vertical(g21)
    c: Coincident(g22,g5)
    c: Coincident(g22,g13)
    c: Vertical(g22)
    c: Coincident(g23,g6)
    c: Coincident(g23,g14)
    c: Vertical(g23)
    c: Coincident(g24,g7)
    c: Coincident(g24,g15)
    c: Vertical(g24)
    c: Coincident(g25,g3)
    c: Coincident(g25,g16)
    c: Vertical(g25)
    c: Coincident(g26,g8)
    c: Coincident(g26,g17)
    c: Vertical(g26)
    c: Coincident(g27,g4)
    c: Coincident(g27,g18)
    c: Vertical(g27)
    c: PointOnObject(g19,g-5)
    c: PointOnObject(g19,g-5)
    c: PointOnObject(g19,g-5)
    c: Coincident(g28,g9)
    c: Coincident(g28,g19)
    c: Vertical(g28)
    c: PointOnObject(g29,g-5)
    c: PointOnObject(g29,g-5)
    c: PointOnObject(g29,g-1)
    c: PointOnObject(g29,g-5)
    c: Diameter(g29) = 1
    c: PointOnObject(g30,g-5)
    c: PointOnObject(g30,g-5)
    c: PointOnObject(g31,g-5)
    c: PointOnObject(g31,g-5)
    c: PointOnObject(g32,g-5)
    c: PointOnObject(g32,g-5)
    c: PointOnObject(g33,g-5)
    c: PointOnObject(g33,g-5)
    c: PointOnObject(g32,g-5)
    c: PointOnObject(g33,g-5)
    c: PointOnObject(g31,g-5)
    c: PointOnObject(g30,g-5)
    c: Diameter(g30) = 1
    c: Diameter(g31) = 1
    c: Diameter(g33) = 1
    c: Diameter(g32) = 1
    c: Distance(g9,g32) = 2
    c: Distance(g32,g33) = 2
    c: Distance(g33,g29) = 2.02533
    c: Coincident(g34,g32)
    c: Coincident(g34,g30)
    c: Coincident(g35,g33)
    c: Coincident(g35,g31)
    c: Vertical(g35)
    c: Vertical(g34)
    c: Coincident(g0,g36)
    c: Coincident(g36,g0)
    c: Coincident(g60,g10)
    c: Coincident(g60,g10)
    c: Coincident(g59,g11)
    c: Coincident(g59,g11)
    c: Coincident(g58,g12)
    c: Coincident(g58,g12)
    c: Coincident(g13,g57)
    c: Coincident(g57,g13)
    c: Coincident(g56,g14)
    c: Coincident(g56,g14)
    c: Coincident(g55,g15)
    c: Coincident(g55,g15)
    c: Coincident(g54,g16)
    c: Coincident(g54,g16)
    c: Coincident(g53,g17)
    c: Coincident(g53,g17)
    c: Coincident(g52,g18)
    c: Coincident(g52,g18)
    c: Coincident(g51,g19)
    c: Coincident(g51,g19)
    c: Coincident(g50,g30)
    c: Coincident(g50,g30)
    c: Coincident(g49,g31)
    c: Coincident(g49,g31)
    c: Coincident(g48,g29)
    c: Coincident(g48,g29)
    c: Coincident(g47,g33)
    c: Coincident(g47,g33)
    c: Coincident(g46,g32)
    c: Coincident(g46,g32)
    c: Coincident(g45,g9)
    c: Coincident(g45,g9)
    c: Coincident(g44,g4)
    c: Coincident(g44,g4)
    c: Coincident(g43,g8)
    c: Coincident(g43,g8)
    c: Coincident(g42,g3)
    c: Coincident(g42,g3)
    c: Coincident(g41,g7)
    c: Coincident(g41,g7)
    c: Coincident(g40,g6)
    c: Coincident(g40,g6)
    c: Coincident(g39,g5)
    c: Coincident(g39,g5)
    c: Coincident(g37,g2)
    c: Coincident(g37,g2)
    c: Coincident(g38,g1)
    c: Coincident(g38,g1)
FEATURE [PartDesign::Pad] Pad155
  BaseFeature = -> Pad154
  Direction = (0,0,-1)
  Length = 4
  Length2 = 10
  Profile = -> Sketch241
  ReferenceAxis = -> Sketch241 [N_Axis]
  Refine = true
  Reversed = true
  Suppressed = false
  Type = 0
FEATURE [Sketcher::SketchObject] Sketch242
  ArcFitTolerance = 1e-06
  AttachmentSupport = -> [Pad155]
  ExternalGeometry = -> [Pad155]
  FullyConstrained = true
  MakeInternals = false
  MapMode = 5
  Placement = pos=(0,0,0) rot=(1,0,0;3.14159rad)
  sketch-geometry (4):
    g0: ArcOfCircle CenterX=18.5272 CenterY=169 CenterZ=0 NormalX=0 NormalY=0 NormalZ=1 AngleXU=0 Radius=175.012 StartAngle=4.78945 EndAngle=4.79805
    g1: LineSegment StartX=33.5 StartY=-5.37017 StartZ=0 EndX=33.5 EndY=5 EndZ=0
    g2: LineSegment StartX=33.5 StartY=5 StartZ=0 EndX=32 EndY=5 EndZ=0
    g3: LineSegment StartX=32 StartY=5 StartZ=0 EndX=32 EndY=-5.49248 EndZ=0
  constraints (10):
    c: Tangent(g0,g-5) = -1.5708
    c: PointOnObject(g0,g-5)
    c: Coincident(g1,g0)
    c: Coincident(g1,g-4)
    c: Coincident(g2,g1)
    c: PointOnObject(g2,g-3)
    c: Coincident(g3,g2)
    c: Coincident(g3,g0)
    c: Vertical(g3)
    c: DistanceX(g2,g2) = 1.5
FEATURE [PartDesign::Pad] Pad156
  BaseFeature = -> Pad155
  Direction = (0,0,-1)
  Length = 2.5
  Length2 = 10
  Profile = -> Sketch242
  ReferenceAxis = -> Sketch242 [N_Axis]
  Refine = true
  Suppressed = false
  Type = 0
FEATURE [Sketcher::SketchObject] Sketch243
  ArcFitTolerance = 1e-06
  AttachmentSupport = -> [Pad156]
  ExternalGeometry = -> [Pad156]
  FullyConstrained = true
  MakeInternals = false
  MapMode = 5
  Placement = pos=(33.5,-3.69e-14,1.3e-13) rot=(0.57735,0.57735,0.57735;2.0944rad)
  sketch-geometry (2):
    g0: ArcOfCircle CenterX=0 CenterY=-2.5 CenterZ=0 NormalX=0 NormalY=0 NormalZ=1 AngleXU=0 Radius=1.5 StartAngle=0 EndAngle=3.14159
    g1: LineSegment StartX=-1.5 StartY=-2.5 StartZ=0 EndX=1.5 EndY=-2.5 EndZ=0
  constraints (7):
    c: PointOnObject(g0,g-3)
    c: PointOnObject(g0,g-3)
    c: PointOnObject(g0,g-3)
    c: PointOnObject(g0,g-2)
    c: Radius(g0) = 1.5
    c: Coincident(g1,g0)
    c: Coincident(g1,g0)
FEATURE [PartDesign::Pocket] Pocket111
  BaseFeature = -> Pad156
  Direction = (-1,1.1e-15,-3.8e-15)
  Length = 5
  Length2 = 5
  Profile = -> Sketch243
  ReferenceAxis = -> Sketch243 [N_Axis]
  Refine = true
  Suppressed = false
  Type = 0
FEATURE [Sketcher::SketchObject] Sketch244
  ArcFitTolerance = 1e-06
  AttachmentSupport = -> [Pocket111]
  ExternalGeometry = -> [Pocket111]
  FullyConstrained = true
  MakeInternals = false
  MapMode = 5
  Placement = pos=(0,0,0) rot=(1,0,0;3.14159rad)
  sketch-geometry (8):
    g0: LineSegment StartX=-3.15 StartY=1.65 StartZ=0 EndX=-3.15 EndY=-1.65 EndZ=0
    g1: LineSegment StartX=-3.15 StartY=-1.65 StartZ=0 EndX=3.15 EndY=-1.65 EndZ=0
    g2: LineSegment StartX=3.15 StartY=-1.65 StartZ=0 EndX=3.15 EndY=1.65 EndZ=0
    g3: LineSegment StartX=3.15 StartY=1.65 StartZ=0 EndX=-3.15 EndY=1.65 EndZ=0
    g4: Circle CenterX=7.15 CenterY=0 CenterZ=0 NormalX=0 NormalY=0 NormalZ=1 AngleXU=0 Radius=2.25
    g5: Circle CenterX=26.05 CenterY=0 CenterZ=0 NormalX=0 NormalY=0 NormalZ=1 AngleXU=0 Radius=2.25
    g6: LineSegment [constr] StartX=26.05 StartY=0 StartZ=0 EndX=28.3 EndY=0 EndZ=0
    g7: LineSegment [constr] StartX=7.15 StartY=0 StartZ=0 EndX=4.9 EndY=0 EndZ=0
  constraints (24):
    c: Coincident(g0,g1)
    c: Coincident(g1,g2)
    c: Coincident(g2,g3)
    c: Coincident(g3,g0)
    c: Vertical(g0)
    c: Vertical(g2)
    c: Horizontal(g1)
    c: Horizontal(g3)
    c: PointOnObject(g4,g-1)
    c: PointOnObject(g5,g-1)
    c: Diameter(g4) = 4.5
    c: Diameter(g5) = 4.5
    c: DistanceX(g3,g3) = 6.3
    c: DistanceY(g2,g2) = 3.3
    c: DistanceX(g0,g-1) = 3.15
    c: Coincident(g6,g5)
    c: PointOnObject(g6,g5)
    c: Horizontal(g6)
    c: DistanceX(g6,g-3) = 5.2
    c: Coincident(g7,g4)
    c: PointOnObject(g7,g4)
    c: Horizontal(g7)
    c: DistanceX(g7,g6) = 23.4
    c: DistanceY(g1,g-1) = 1.65
FEATURE [PartDesign::Pocket] Pocket112
  BaseFeature = -> Pocket111
  Direction = (0,0,1)
  Length = 5
  Length2 = 5
  Profile = -> Sketch244 [Edge4,Edge1,Edge2,Edge3]
  ReferenceAxis = -> Sketch244 [N_Axis]
  Refine = true
  Suppressed = false
  Type = 0
FEATURE [PartDesign::Pad] Pad157
  BaseFeature = -> Pocket112
  Direction = (0,0,-1)
  Length = 4
  Length2 = 10
  Profile = -> Sketch244 [Edge5,Edge6]
  ReferenceAxis = -> Sketch244 [N_Axis]
  Refine = true
  Suppressed = false
  Type = 0
FEATURE [Sketcher::SketchObject] Sketch245
  ArcFitTolerance = 1e-06
  AttachmentSupport = -> [Pad157]
  ExternalGeometry = -> [Pad157]
  FullyConstrained = true
  MakeInternals = false
  MapMode = 5
  Placement = pos=(0,0,-4) rot=(1,0,0;3.14159rad)
  sketch-geometry (2):
    g0: Circle CenterX=7.15 CenterY=0 CenterZ=0 NormalX=0 NormalY=0 NormalZ=1 AngleXU=0 Radius=0.75
    g1: Circle CenterX=26.05 CenterY=0 CenterZ=0 NormalX=0 NormalY=0 NormalZ=1 AngleXU=0 Radius=0.75
  constraints (4):
    c: Coincident(g0,g-3)
    c: Coincident(g1,g-4)
    c: Radius(g0) = 0.75
    c: Radius(g1) = 0.75
FEATURE [PartDesign::Pocket] Pocket113
  BaseFeature = -> Pad157
  Direction = (0,0,1)
  Length = 4
  Length2 = 5
  Profile = -> Sketch245
  ReferenceAxis = -> Sketch245 [N_Axis]
  Refine = true
  Suppressed = false
  Type = 0
FEATURE [Sketcher::SketchObject] Sketch246
  ArcFitTolerance = 1e-06
  AttachmentSupport = -> [Pocket113]
  ExternalGeometry = -> [Pocket113]
  FullyConstrained = true
  MakeInternals = false
  MapMode = 5
  Placement = pos=(0,0,0) rot=(1,0,0;3.14159rad)
  sketch-geometry (1):
    g0: Circle CenterX=15.9183 CenterY=-5.2423 CenterZ=0 NormalX=0 NormalY=0 NormalZ=1 AngleXU=0 Radius=0.75
  constraints (4):
    c: Diameter(g0) = 1.5
    c: Tangent(g0,g-3)
    c: DistanceX(g-4,g0) = 1.4
    c: DistanceX(g0,g-5) = 1.3997
FEATURE [PartDesign::Pad] Pad158
  BaseFeature = -> Pocket113
  Direction = (0,0,-1)
  Length = 3.8
  Length2 = 10
  Profile = -> Sketch246
  ReferenceAxis = -> Sketch246 [N_Axis]
  Refine = true
  Suppressed = false
  Type = 0
FEATURE [Sketcher::SketchObject] Sketch247
  ArcFitTolerance = 1e-06
  AttachmentSupport = -> [Pad158]
  ExternalGeometry = -> [Pad158]
  FullyConstrained = true
  MakeInternals = false
  MapMode = 5
  Placement = pos=(0,0,0) rot=(1,0,0;3.14159rad)
  sketch-geometry (8):
    g0: LineSegment StartX=-3.15 StartY=1.65 StartZ=0 EndX=-3.15 EndY=-1.65 EndZ=0
    g1: LineSegment StartX=-3.15 StartY=-1.65 StartZ=0 EndX=3.15 EndY=-1.65 EndZ=0
    g2: LineSegment StartX=3.15 StartY=-1.65 StartZ=0 EndX=3.15 EndY=1.65 EndZ=0
    g3: LineSegment StartX=3.15 StartY=1.65 StartZ=0 EndX=-3.15 EndY=1.65 EndZ=0
    g4: LineSegment StartX=-3.85 StartY=2.35 StartZ=0 EndX=-3.85 EndY=-2.35 EndZ=0
    g5: LineSegment StartX=-3.85 StartY=-2.35 StartZ=0 EndX=3.85 EndY=-2.35 EndZ=0
    g6: LineSegment StartX=3.85 StartY=-2.35 StartZ=0 EndX=3.85 EndY=2.35 EndZ=0
    g7: LineSegment StartX=3.85 StartY=2.35 StartZ=0 EndX=-3.85 EndY=2.35 EndZ=0
  constraints (22):
    c: Coincident(g0,g1)
    c: Coincident(g1,g2)
    c: Coincident(g2,g3)
    c: Coincident(g3,g0)
    c: Vertical(g0)
    c: Vertical(g2)
    c: Horizontal(g1)
    c: Horizontal(g3)
    c: Coincident(g0,g-6)
    c: Coincident(g1,g-5)
    c: Coincident(g4,g5)
    c: Coincident(g5,g6)
    c: Coincident(g6,g7)
    c: Coincident(g7,g4)
    c: Vertical(g4)
    c: Vertical(g6)
    c: Horizontal(g5)
    c: Horizontal(g7)
    c: DistanceX(g2,g6) = 0.7
    c: DistanceX(g4,g0) = 0.7
    c: DistanceY(g5,g1) = 0.7
    c: DistanceY(g2,g6) = 0.7
FEATURE [PartDesign::Pad] Pad159
  BaseFeature = -> Pad158
  Direction = (0,0,-1)
  Length = 0.5
  Length2 = 10
  Profile = -> Sketch247
  ReferenceAxis = -> Sketch247 [N_Axis]
  Refine = true
  Suppressed = false
  Type = 0
FEATURE [Sketcher::SketchObject] Sketch248
  ArcFitTolerance = 1e-06
  AttachmentSupport = -> [Pad159]
  ExternalGeometry = -> [Pad159]
  FullyConstrained = true
  MakeInternals = false
  MapMode = 5
  Placement = pos=(0,0,-0.5) rot=(1,0,0;3.14159rad)
  sketch-geometry (8):
    g0: LineSegment StartX=-1 StartY=2.35 StartZ=0 EndX=-1 EndY=1.65 EndZ=0
    g1: LineSegment StartX=-1 StartY=1.65 StartZ=0 EndX=1 EndY=1.65 EndZ=0
    g2: LineSegment StartX=1 StartY=1.65 StartZ=0 EndX=1 EndY=2.35 EndZ=0
    g3: LineSegment StartX=1 StartY=2.35 StartZ=0 EndX=-1 EndY=2.35 EndZ=0
    g4: LineSegment StartX=-1 StartY=-1.65 StartZ=0 EndX=-1 EndY=-2.35 EndZ=0
    g5: LineSegment StartX=-1 StartY=-2.35 StartZ=0 EndX=1 EndY=-2.35 EndZ=0
    g6: LineSegment StartX=1 StartY=-2.35 StartZ=0 EndX=1 EndY=-1.65 EndZ=0
    g7: LineSegment StartX=1 StartY=-1.65 StartZ=0 EndX=-1 EndY=-1.65 EndZ=0
  constraints (24):
    c: Coincident(g0,g1)
    c: Coincident(g1,g2)
    c: Coincident(g2,g3)
    c: Coincident(g3,g0)
    c: Vertical(g0)
    c: Vertical(g2)
    c: Horizontal(g1)
    c: Horizontal(g3)
    c: PointOnObject(g0,g-3)
    c: PointOnObject(g1,g-4)
    c: Coincident(g4,g5)
    c: Coincident(g5,g6)
    c: Coincident(g6,g7)
    c: Coincident(g7,g4)
    c: Vertical(g4)
    c: Vertical(g6)
    c: Horizontal(g5)
    c: Horizontal(g7)
    c: PointOnObject(g4,g-5)
    c: PointOnObject(g5,g-6)
    c: DistanceX(g0,g-1) = 1
    c: DistanceX(g-1,g1) = 1
    c: DistanceX(g4,g-1) = 1
    c: DistanceX(g-1,g6) = 1
FEATURE [PartDesign::Pad] Pad160
  BaseFeature = -> Pad159
  Direction = (0,0,-1)
  Length = 0.1
  Length2 = 10
  Profile = -> Sketch248
  ReferenceAxis = -> Sketch248 [N_Axis]
  Refine = true
  Suppressed = false
  Type = 0
FEATURE [PartDesign::Body] Body015  label="Left_Inner_Leg"
  AllowCompound = false
  Group = -> [Sketch238,Pad153,Sketch239,Pocket110,Sketch240,Pad154,Sketch241,Pad155,Sketch242,Pad156,Sketch243,Pocket111,Sketch244,Pocket112,Pad157,Sketch245,Pocket113,Sketch246,Pad158,Sketch247,Pad159,Sketch248,Pad160]
  Origin = -> Origin016
  Placement = pos=(53.7,-27.4,-19.5) rot=(0,-0.71,-0.71;3.14159rad)
  Tip = -> Pad160
FEATURE [PartDesign::SubShapeBinder] Binder008
  BindCopyOnChange = 0
  BindMode = 2
  ClaimChildren = false
  Context = -> Body016 [Binder008.]
  Fuse = false
  MakeFace = true
  OffsetFill = false
  OffsetIntersection = false
  OffsetJoinType = 0
  OffsetOpenResult = false
  PartialLoad = false
  Refine = true
  Relative = true
  _Version = 2
FEATURE [PartDesign::Pad] Pad161
  Direction = (0,0,-1)
  Length = 4
  Length2 = 10
  Profile = -> Binder008
  Refine = true
  Suppressed = false
  Type = 0
FEATURE [Sketcher::SketchObject] Sketch249
  ArcFitTolerance = 1e-06
  AttachmentSupport = -> [Pad161]
  ExternalGeometry = -> [Pad161]
  FullyConstrained = true
  MakeInternals = false
  MapMode = 5
  Placement = pos=(0,0,-6.5) rot=(1,0,0;3.14159rad)
  sketch-geometry (8):
    g0: ArcOfCircle CenterX=18.5272 CenterY=169 CenterZ=0 NormalX=0 NormalY=0 NormalZ=1 AngleXU=0 Radius=175.012 StartAngle=4.78945 EndAngle=4.79805
    g1: LineSegment StartX=32 StartY=5 StartZ=0 EndX=32 EndY=1.5 EndZ=0
    g2: LineSegment StartX=32 StartY=1.5 StartZ=0 EndX=33.5 EndY=1.5 EndZ=0
    g3: LineSegment StartX=33.5 StartY=1.5 StartZ=0 EndX=33.5 EndY=5 EndZ=0
    g4: LineSegment StartX=33.5 StartY=5 StartZ=0 EndX=32 EndY=5 EndZ=0
    g5: LineSegment StartX=32 StartY=-5.49248 StartZ=0 EndX=32 EndY=-1.5 EndZ=0
    g6: LineSegment StartX=32 StartY=-1.5 StartZ=0 EndX=33.5 EndY=-1.5 EndZ=0
    g7: LineSegment StartX=33.5 StartY=-1.5 StartZ=0 EndX=33.5 EndY=-5.37017 EndZ=0
  constraints (20):
    c: Radius(g-3) = 175.012
    c: Coincident(g0,g-8)
    c: PointOnObject(g0,g-9)
    c: Coincident(g0,g-3)
    c: Coincident(g1,g2)
    c: Coincident(g2,g3)
    c: Coincident(g3,g4)
    c: Coincident(g4,g1)
    c: Vertical(g1)
    c: Vertical(g3)
    c: Horizontal(g2)
    c: Horizontal(g4)
    c: Coincident(g1,g-4)
    c: Coincident(g2,g-6)
    c: Coincident(g5,g0)
    c: Coincident(g5,g-8)
    c: Coincident(g6,g5)
    c: Coincident(g6,g-9)
    c: Coincident(g7,g6)
    c: Coincident(g7,g0)
FEATURE [PartDesign::Pocket] Pocket114
  BaseFeature = -> Pad161
  Direction = (0,0,1)
  Length = 0.5
  Length2 = 5
  Profile = -> Sketch249
  ReferenceAxis = -> Sketch249 [N_Axis]
  Refine = true
  Suppressed = false
  Type = 0
FEATURE [Sketcher::SketchObject] Sketch250
  ArcFitTolerance = 1e-06
  AttachmentSupport = -> [Pocket114]
  ExternalGeometry = -> [Pocket114]
  FullyConstrained = true
  MakeInternals = false
  MapMode = 5
  Placement = pos=(0,0,-6) rot=(1,0,0;3.14159rad)
  sketch-geometry (4):
    g0: ArcOfCircle CenterX=0 CenterY=3e-16 CenterZ=0 NormalX=0 NormalY=0 NormalZ=1 AngleXU=0 Radius=5 StartAngle=1.5708 EndAngle=4.61995
    g1: ArcOfCircle CenterX=18.5272 CenterY=169 CenterZ=0 NormalX=0 NormalY=0 NormalZ=1 AngleXU=0 Radius=175.012 StartAngle=4.60368 EndAngle=4.78945
    g2: LineSegment StartX=32 StartY=-5.49248 StartZ=0 EndX=32 EndY=5 EndZ=0
    g3: LineSegment StartX=32 StartY=5 StartZ=0 EndX=0 EndY=5 EndZ=0
  constraints (9):
    c: Tangent(g0,g-7) = -1.5708
    c: Coincident(g0,g-7)
    c: Coincident(g1,g0)
    c: Coincident(g1,g-4)
    c: Tangent(g1,g-3)
    c: Coincident(g2,g1)
    c: Coincident(g2,g-5)
    c: Coincident(g3,g2)
    c: Coincident(g3,g0)
FEATURE [PartDesign::Pad] Pad162
  BaseFeature = -> Pocket114
  Direction = (0,0,-1)
  Length = 1
  Length2 = 10
  Profile = -> Sketch250
  ReferenceAxis = -> Sketch250 [N_Axis]
  Refine = true
  Reversed = true
  Suppressed = false
  Type = 0
FEATURE [Sketcher::SketchObject] Sketch251
  ArcFitTolerance = 1e-06
  AttachmentSupport = -> [Pad162]
  ExternalGeometry = -> [Pad162]
  FullyConstrained = true
  MakeInternals = false
  MapMode = 5
  Placement = pos=(33.5,7.933e-13,0) rot=(0.57735,0.57735,0.57735;2.0944rad)
  sketch-geometry (6):
    g0: ArcOfCircle CenterX=-8.307e-13 CenterY=-2.5 CenterZ=0 NormalX=0 NormalY=0 NormalZ=1 AngleXU=0 Radius=1.5 StartAngle=3.14159 EndAngle=6.28319
    g1: LineSegment [constr] StartX=-1.5 StartY=-2.5 StartZ=0 EndX=-8.307e-13 EndY=-2.5 EndZ=0
    g2: LineSegment [constr] StartX=-8.307e-13 StartY=-2.5 StartZ=0 EndX=1.5 EndY=-2.5 EndZ=0
    g3: LineSegment StartX=-1.5 StartY=-2.5 StartZ=0 EndX=-1.5 EndY=-6 EndZ=0
    g4: LineSegment StartX=-1.5 StartY=-6 StartZ=0 EndX=1.5 EndY=-6 EndZ=0
    g5: LineSegment StartX=1.5 StartY=-6 StartZ=0 EndX=1.5 EndY=-2.5 EndZ=0
  constraints (13):
    c: Coincident(g0,g-4)
    c: Coincident(g0,g-3)
    c: Coincident(g1,g0)
    c: Coincident(g1,g0)
    c: Coincident(g2,g0)
    c: Coincident(g2,g0)
    c: Angle(g2,g1) = 3.14159
    c: Coincident(g3,g0)
    c: Coincident(g3,g-4)
    c: Coincident(g4,g3)
    c: Coincident(g4,g-3)
    c: Coincident(g5,g4)
    c: Coincident(g5,g0)
FEATURE [PartDesign::Pad] Pad163
  BaseFeature = -> Pad162
  Direction = (1,2.36e-14,1e-16)
  Length = 1.5
  Length2 = 10
  Profile = -> Sketch251
  ReferenceAxis = -> Sketch251 [N_Axis]
  Refine = true
  Reversed = true
  Suppressed = false
  Type = 0
FEATURE [Sketcher::SketchObject] Sketch252
  ArcFitTolerance = 1e-06
  AttachmentSupport = -> [Pad163]
  ExternalGeometry = -> [Pad163]
  FullyConstrained = true
  MakeInternals = false
  MapMode = 5
  Placement = pos=(0,0,-6) rot=(1,0,0;3.14159rad)
  sketch-geometry (4):
    g0: ArcOfCircle CenterX=0 CenterY=0 CenterZ=0 NormalX=0 NormalY=0 NormalZ=1 AngleXU=0 Radius=4.85 StartAngle=0.748325 EndAngle=5.72466
    g1: LineSegment StartX=3.55422 StartY=3.3 StartZ=0 EndX=33.5 EndY=3.3 EndZ=0
    g2: LineSegment StartX=4.11299 StartY=-2.57017 StartZ=0 EndX=33.5 EndY=-2.57017 EndZ=0
    g3: LineSegment StartX=33.5 StartY=-2.57017 StartZ=0 EndX=33.5 EndY=3.3 EndZ=0
  constraints (13):
    c: Diameter(g0) = 9.7
    c: Coincident(g0,g-1)
    c: Coincident(g1,g0)
    c: PointOnObject(g1,g-5)
    c: Horizontal(g1)
    c: Coincident(g2,g0)
    c: PointOnObject(g2,g-5)
    c: Horizontal(g2)
    c: Coincident(g3,g2)
    c: Coincident(g3,g1)
    c: DistanceY(g1,g-5) = 1.7
    c: DistanceY(g-5,g2) = 2.8
    c: DistanceY(g2,g1) = 5.87017
FEATURE [PartDesign::Pad] Pad164
  BaseFeature = -> Pad163
  Direction = (0,0,-1)
  Length = 0.5
  Length2 = 10
  Profile = -> Sketch252
  ReferenceAxis = -> Sketch252 [N_Axis]
  Refine = true
  Suppressed = false
  Type = 0
FEATURE [Sketcher::SketchObject] Sketch253
  ArcFitTolerance = 1e-06
  AttachmentSupport = -> [Pad164]
  ExternalGeometry = -> [Pad164]
  FullyConstrained = true
  MakeInternals = false
  MapMode = 5
  Placement = pos=(0,0,-6.5) rot=(1,0,0;3.14159rad)
  sketch-geometry (2):
    g0: Circle CenterX=0 CenterY=0 CenterZ=0 NormalX=0 NormalY=0 NormalZ=1 AngleXU=0 Radius=3.8
    g1: Circle CenterX=0 CenterY=0 CenterZ=0 NormalX=0 NormalY=0 NormalZ=1 AngleXU=0 Radius=2
  constraints (4):
    c: Coincident(g0,g-1)
    c: Coincident(g1,g0)
    c: Diameter(g0) = 7.6
    c: Diameter(g1) = 4
FEATURE [PartDesign::Pad] Pad165
  BaseFeature = -> Pad164
  Direction = (0,0,-1)
  Length = 1
  Length2 = 10
  Profile = -> Sketch253
  ReferenceAxis = -> Sketch253 [N_Axis]
  Refine = true
  Suppressed = false
  Type = 0
FEATURE [Sketcher::SketchObject] Sketch254
  ArcFitTolerance = 1e-06
  AttachmentSupport = -> [Pad165]
  ExternalGeometry = -> [Pad165]
  FullyConstrained = true
  MakeInternals = false
  MapMode = 5
  Placement = pos=(0,0,-6.5) rot=(1,0,0;3.14159rad)
  sketch-geometry (4):
    g0: LineSegment StartX=33.5 StartY=3.3 StartZ=0 EndX=5 EndY=3.3 EndZ=0
    g1: LineSegment StartX=5 StartY=3.3 StartZ=0 EndX=5 EndY=-2.57017 EndZ=0
    g2: LineSegment StartX=5 StartY=-2.57017 StartZ=0 EndX=33.5 EndY=-2.57017 EndZ=0
    g3: LineSegment StartX=33.5 StartY=-2.57017 StartZ=0 EndX=33.5 EndY=3.3 EndZ=0
  constraints (11):
    c: Coincident(g0,g1)
    c: Coincident(g1,g2)
    c: Coincident(g2,g3)
    c: Coincident(g3,g0)
    c: Horizontal(g0)
    c: Horizontal(g2)
    c: Vertical(g1)
    c: Vertical(g3)
    c: Coincident(g0,g-4)
    c: PointOnObject(g1,g-5)
    c: DistanceX(g0,g0) = 28.5
FEATURE [PartDesign::Pad] Pad166
  BaseFeature = -> Pad165
  Direction = (0,0,-1)
  Length = 0.5
  Length2 = 10
  Profile = -> Sketch254
  ReferenceAxis = -> Sketch254 [N_Axis]
  Refine = true
  Suppressed = false
  Type = 0
FEATURE [Sketcher::SketchObject] Sketch255
  ArcFitTolerance = 1e-06
  AttachmentSupport = -> [Pad166]
  ExternalGeometry = -> [Pad166]
  FullyConstrained = true
  MakeInternals = false
  MapMode = 5
  Placement = pos=(0,0,-7) rot=(1,0,0;3.14159rad)
  sketch-geometry (5):
    g0: Circle CenterX=7.15 CenterY=0 CenterZ=0 NormalX=0 NormalY=0 NormalZ=1 AngleXU=0 Radius=2.25
    g1: Circle CenterX=26.05 CenterY=0 CenterZ=0 NormalX=0 NormalY=0 NormalZ=1 AngleXU=0 Radius=2.25
    g2: LineSegment [constr] StartX=26.05 StartY=0 StartZ=0 EndX=28.3 EndY=0 EndZ=0
    g3: LineSegment [constr] StartX=26.05 StartY=0 StartZ=0 EndX=23.8 EndY=0 EndZ=0
    g4: LineSegment [constr] StartX=7.15 StartY=0 StartZ=0 EndX=9.4 EndY=0 EndZ=0
  constraints (15):
    c: PointOnObject(g0,g-1)
    c: PointOnObject(g1,g-1)
    c: Diameter(g0) = 4.5
    c: Diameter(g1) = 4.5
    c: Coincident(g2,g1)
    c: PointOnObject(g2,g1)
    c: Horizontal(g2)
    c: DistanceX(g2,g-4) = 5.2
    c: Coincident(g3,g1)
    c: PointOnObject(g3,g1)
    c: Horizontal(g3)
    c: Coincident(g4,g0)
    c: PointOnObject(g4,g0)
    c: Horizontal(g4)
    c: DistanceX(g4,g3) = 14.4
FEATURE [Sketcher::SketchObject] Sketch256
  ArcFitTolerance = 1e-06
  AttachmentSupport = -> [Pad166]
  ExternalGeometry = -> [Pad166]
  FullyConstrained = true
  MakeInternals = false
  MapMode = 5
  Placement = pos=(0,0,-5) rot=(0,0,1;0rad)
  sketch-geometry (4):
    g0: LineSegment StartX=32 StartY=1.95 StartZ=0 EndX=-4.60407 EndY=1.95 EndZ=0
    g1: LineSegment StartX=-4.60407 StartY=1.95 StartZ=0 EndX=-4.60407 EndY=-1.95 EndZ=0
    g2: LineSegment StartX=-4.60407 StartY=-1.95 StartZ=0 EndX=32 EndY=-1.95 EndZ=0
    g3: LineSegment StartX=32 StartY=-1.95 StartZ=0 EndX=32 EndY=1.95 EndZ=0
  constraints (12):
    c: Coincident(g0,g1)
    c: Coincident(g1,g2)
    c: Coincident(g2,g3)
    c: Coincident(g3,g0)
    c: Horizontal(g0)
    c: Horizontal(g2)
    c: Vertical(g1)
    c: Vertical(g3)
    c: PointOnObject(g0,g-3)
    c: DistanceY(g3,g3) = 3.9
    c: DistanceY(g1,g-1) = 1.95
    c: PointOnObject(g0,g-4)
FEATURE [PartDesign::Pocket] Pocket115
  BaseFeature = -> Pad166
  Direction = (0,0,-1)
  Length = 1
  Length2 = 5
  Profile = -> Sketch256
  ReferenceAxis = -> Sketch256 [N_Axis]
  Refine = true
  Suppressed = false
  Type = 0
FEATURE [Sketcher::SketchObject] Sketch257
  ArcFitTolerance = 1e-06
  AttachmentSupport = -> [Pocket115]
  ExternalGeometry = -> [Sketch255]
  FullyConstrained = true
  MakeInternals = false
  MapMode = 5
  Placement = pos=(0,0,-6) rot=(0,0,1;0rad)
  sketch-geometry (2):
    g0: Circle CenterX=7.15 CenterY=0 CenterZ=0 NormalX=0 NormalY=0 NormalZ=1 AngleXU=0 Radius=3.5
    g1: Circle CenterX=26.05 CenterY=0 CenterZ=0 NormalX=0 NormalY=0 NormalZ=1 AngleXU=0 Radius=3.5
  constraints (4):
    c: Coincident(g0,g-3)
    c: Coincident(g1,g-4)
    c: Diameter(g0) = 7
    c: Diameter(g1) = 7
FEATURE [PartDesign::Pad] Pad167
  BaseFeature = -> Pocket115
  Direction = (0,0,1)
  Length = 2.8
  Length2 = 10
  Profile = -> Sketch257
  ReferenceAxis = -> Sketch257 [N_Axis]
  Refine = true
  Suppressed = false
  Type = 0
FEATURE [Sketcher::SketchObject] Sketch258
  ArcFitTolerance = 1e-06
  AttachmentSupport = -> [Pad167]
  ExternalGeometry = -> [Pad167]
  FullyConstrained = true
  MakeInternals = false
  MapMode = 5
  Placement = pos=(0,0,-3.2) rot=(0,0,1;0rad)
  sketch-geometry (2):
    g0: Circle CenterX=7.15 CenterY=0 CenterZ=0 NormalX=0 NormalY=0 NormalZ=1 AngleXU=0 Radius=2.45
    g1: Circle CenterX=26.05 CenterY=0 CenterZ=0 NormalX=0 NormalY=0 NormalZ=1 AngleXU=0 Radius=2.45
  constraints (4):
    c: Coincident(g0,g-3)
    c: Coincident(g1,g-4)
    c: Diameter(g0) = 4.9
    c: Diameter(g1) = 4.9
FEATURE [PartDesign::Pocket] Pocket116
  BaseFeature = -> Pad167
  Direction = (0,0,-1)
  Length = 1
  Length2 = 5
  Profile = -> Sketch258
  ReferenceAxis = -> Sketch258 [N_Axis]
  Refine = true
  Suppressed = false
  Type = 0
FEATURE [PartDesign::Pocket] Pocket117
  BaseFeature = -> Pocket116
  Direction = (0,0,1)
  Length = 2
  Length2 = 5
  Profile = -> Sketch255
  ReferenceAxis = -> Sketch255 [N_Axis]
  Refine = true
  Suppressed = false
  Type = 0
FEATURE [Sketcher::SketchObject] Sketch259
  ArcFitTolerance = 1e-06
  AttachmentSupport = -> [Pocket117]
  ExternalGeometry = -> [Pocket117]
  FullyConstrained = true
  MakeInternals = false
  MapMode = 5
  Placement = pos=(0,0,-5) rot=(1,0,0;3.14159rad)
  sketch-geometry (2):
    g0: Circle CenterX=7.15 CenterY=0 CenterZ=0 NormalX=0 NormalY=0 NormalZ=1 AngleXU=0 Radius=1
    g1: Circle CenterX=26.05 CenterY=0 CenterZ=0 NormalX=0 NormalY=0 NormalZ=1 AngleXU=0 Radius=1
  constraints (4):
    c: Coincident(g0,g-3)
    c: Coincident(g1,g-4)
    c: Radius(g0) = 1
    c: Radius(g1) = 1
FEATURE [PartDesign::Pocket] Pocket118
  BaseFeature = -> Pocket117
  Direction = (0,0,1)
  Length = 5
  Length2 = 5
  Profile = -> Sketch259
  ReferenceAxis = -> Sketch259 [N_Axis]
  Refine = true
  Suppressed = false
  Type = 0
FEATURE [Sketcher::SketchObject] Sketch260
  ArcFitTolerance = 1e-06
  AttachmentSupport = -> [Pocket118]
  FullyConstrained = true
  MakeInternals = false
  MapMode = 5
  Placement = pos=(0,0,-6) rot=(0,0,1;0rad)
  sketch-geometry (9):
    g0: LineSegment StartX=-3.1 StartY=2.45 StartZ=0 EndX=-3.1 EndY=-2.45 EndZ=0
    g1: LineSegment StartX=-3.1 StartY=-2.45 StartZ=0 EndX=-1.6 EndY=-2.45 EndZ=0
    g2: LineSegment StartX=-1.6 StartY=-2.45 StartZ=0 EndX=-1.6 EndY=2.45 EndZ=0
    g3: LineSegment StartX=-1.6 StartY=2.45 StartZ=0 EndX=-3.1 EndY=2.45 EndZ=0
    g4: LineSegment StartX=1.6 StartY=2.45 StartZ=0 EndX=1.6 EndY=-2.45 EndZ=0
    g5: LineSegment StartX=1.6 StartY=-2.45 StartZ=0 EndX=3.1 EndY=-2.45 EndZ=0
    g6: LineSegment StartX=3.1 StartY=-2.45 StartZ=0 EndX=3.1 EndY=2.45 EndZ=0
    g7: LineSegment StartX=3.1 StartY=2.45 StartZ=0 EndX=1.6 EndY=2.45 EndZ=0
    g8: LineSegment [constr] StartX=1.6 StartY=-2.45 StartZ=0 EndX=-1.6 EndY=-2.45 EndZ=0
  constraints (26):
    c: Coincident(g0,g1)
    c: Coincident(g1,g2)
    c: Coincident(g2,g3)
    c: Coincident(g3,g0)
    c: Vertical(g0)
    c: Vertical(g2)
    c: Horizontal(g1)
    c: Horizontal(g3)
    c: Coincident(g4,g5)
    c: Coincident(g5,g6)
    c: Coincident(g6,g7)
    c: Coincident(g7,g4)
    c: Vertical(g4)
    c: Vertical(g6)
    c: Horizontal(g5)
    c: Horizontal(g7)
    c: DistanceX(g4,g6) = 1.5
    c: DistanceX(g0,g2) = 1.5
    c: DistanceX(g2,g4) = 3.2
    c: DistanceY(g0,g0) = 4.9
    c: DistanceY(g4,g4) = 4.9
    c: DistanceY(g4,g-1) = 2.45
    c: Coincident(g8,g4)
    c: Coincident(g8,g1)
    c: Horizontal(g8)
    c: DistanceX(g2,g-1) = 1.6
FEATURE [PartDesign::Pad] Pad168
  BaseFeature = -> Pocket118
  Direction = (0,0,1)
  Length = 5.4
  Length2 = 10
  Profile = -> Sketch260
  ReferenceAxis = -> Sketch260 [N_Axis]
  Refine = true
  Suppressed = false
  Type = 0
FEATURE [Sketcher::SketchObject] Sketch261
  ArcFitTolerance = 1e-06
  AttachmentSupport = -> [Pad168]
  ExternalGeometry = -> [Pad168]
  FullyConstrained = true
  MakeInternals = false
  MapMode = 5
  Placement = pos=(0,0,-0.6) rot=(0,0,1;0rad)
  sketch-geometry (8):
    g0: LineSegment StartX=-3.1 StartY=1.6 StartZ=0 EndX=-3.1 EndY=-1.6 EndZ=0
    g1: LineSegment StartX=-3.1 StartY=-1.6 StartZ=0 EndX=-1.6 EndY=-1.6 EndZ=0
    g2: LineSegment StartX=-1.6 StartY=-1.6 StartZ=0 EndX=-1.6 EndY=1.6 EndZ=0
    g3: LineSegment StartX=-1.6 StartY=1.6 StartZ=0 EndX=-3.1 EndY=1.6 EndZ=0
    g4: LineSegment StartX=1.6 StartY=1.6 StartZ=0 EndX=1.6 EndY=-1.6 EndZ=0
    g5: LineSegment StartX=1.6 StartY=-1.6 StartZ=0 EndX=3.1 EndY=-1.6 EndZ=0
    g6: LineSegment StartX=3.1 StartY=-1.6 StartZ=0 EndX=3.1 EndY=1.6 EndZ=0
    g7: LineSegment StartX=3.1 StartY=1.6 StartZ=0 EndX=1.6 EndY=1.6 EndZ=0
  constraints (24):
    c: Coincident(g0,g1)
    c: Coincident(g1,g2)
    c: Coincident(g2,g3)
    c: Coincident(g3,g0)
    c: Vertical(g0)
    c: Vertical(g2)
    c: Horizontal(g1)
    c: Horizontal(g3)
    c: PointOnObject(g0,g-3)
    c: PointOnObject(g1,g-4)
    c: Coincident(g4,g5)
    c: Coincident(g5,g6)
    c: Coincident(g6,g7)
    c: Coincident(g7,g4)
    c: Vertical(g4)
    c: Vertical(g6)
    c: Horizontal(g5)
    c: Horizontal(g7)
    c: PointOnObject(g4,g-5)
    c: PointOnObject(g5,g-6)
    c: DistanceY(g0,g0) = 3.2
    c: DistanceY(g4,g4) = 3.2
    c: DistanceY(g-1,g4) = 1.6
    c: DistanceY(g-1,g2) = 1.6
FEATURE [PartDesign::Pad] Pad169
  BaseFeature = -> Pad168
  Direction = (0,0,1)
  Length = 2
  Length2 = 10
  Profile = -> Sketch261
  ReferenceAxis = -> Sketch261 [N_Axis]
  Refine = true
  Suppressed = false
  Type = 0
FEATURE [Sketcher::SketchObject] Sketch262
  ArcFitTolerance = 1e-06
  AttachmentSupport = -> [Pad169]
  ExternalGeometry = -> [Pad169]
  FullyConstrained = true
  MakeInternals = false
  MapMode = 5
  Placement = pos=(0,1.4e-15,-6) rot=(1,0,0;3.14159rad)
  sketch-geometry (15):
    g0: ArcOfCircle CenterX=10.6 CenterY=1.97712 CenterZ=0 NormalX=0 NormalY=0 NormalZ=1 AngleXU=0 Radius=2 StartAngle=0.722734 EndAngle=2.41886
    g1: ArcOfCircle CenterX=15.1 CenterY=1.97712 CenterZ=0 NormalX=0 NormalY=0 NormalZ=1 AngleXU=0 Radius=2 StartAngle=0.722734 EndAngle=2.41886
    g2: ArcOfCircle CenterX=19.6 CenterY=1.97712 CenterZ=0 NormalX=0 NormalY=0 NormalZ=1 AngleXU=0 Radius=2 StartAngle=0.722734 EndAngle=2.41886
    g3: ArcOfCircle CenterX=24.1 CenterY=1.97712 CenterZ=0 NormalX=0 NormalY=0 NormalZ=1 AngleXU=0 Radius=2 StartAngle=0.722734 EndAngle=2.41886
    g4: ArcOfCircle CenterX=28.6 CenterY=1.97712 CenterZ=0 NormalX=0 NormalY=0 NormalZ=1 AngleXU=0 Radius=2 StartAngle=0.722734 EndAngle=2.41886
    g5: ArcOfCircle CenterX=14 CenterY=-3.53842 CenterZ=0 NormalX=0 NormalY=0 NormalZ=1 AngleXU=0 Radius=2 StartAngle=2.63623 EndAngle=6.78855
    g6: ArcOfCircle CenterX=23.5 CenterY=-3.53842 CenterZ=0 NormalX=0 NormalY=0 NormalZ=1 AngleXU=0 Radius=2 StartAngle=2.63623 EndAngle=6.78855
    g7: LineSegment [constr] StartX=23.5 StartY=-3.53842 StartZ=0 EndX=25.5 EndY=-3.53842 EndZ=0
    g8: LineSegment StartX=9.1 StartY=3.3 StartZ=0 EndX=12.1 EndY=3.3 EndZ=0
    g9: LineSegment StartX=13.6 StartY=3.3 StartZ=0 EndX=16.6 EndY=3.3 EndZ=0
    g10: LineSegment StartX=18.1 StartY=3.3 StartZ=0 EndX=21.1 EndY=3.3 EndZ=0
    g11: LineSegment StartX=22.6 StartY=3.3 StartZ=0 EndX=25.6 EndY=3.3 EndZ=0
    g12: LineSegment StartX=27.1 StartY=3.3 StartZ=0 EndX=30.1 EndY=3.3 EndZ=0
    g13: LineSegment StartX=25.25 StartY=-2.57017 StartZ=0 EndX=21.75 EndY=-2.57017 EndZ=0
    g14: LineSegment StartX=15.75 StartY=-2.57017 StartZ=0 EndX=12.25 EndY=-2.57017 EndZ=0
  constraints (52):
    c: PointOnObject(g0,g-3)
    c: PointOnObject(g0,g-3)
    c: PointOnObject(g1,g-3)
    c: PointOnObject(g1,g-3)
    c: PointOnObject(g2,g-3)
    c: PointOnObject(g2,g-3)
    c: PointOnObject(g3,g-3)
    c: PointOnObject(g4,g-3)
    c: PointOnObject(g4,g-3)
    c: PointOnObject(g5,g-4)
    c: PointOnObject(g5,g-4)
    c: PointOnObject(g6,g-4)
    c: PointOnObject(g6,g-4)
    c: Diameter(g1) = 4
    c: DistanceX(g1,g1) = 3
    c: Diameter(g0) = 4
    c: Diameter(g2) = 4
    c: Diameter(g3) = 4
    c: Diameter(g4) = 4
    c: Diameter(g5) = 4
    c: Diameter(g6) = 4
    c: DistanceX(g0,g0) = 3
    c: DistanceX(g2,g2) = 3
    c: PointOnObject(g3,g-3)
    c: DistanceX(g3,g3) = 3
    c: DistanceX(g4,g4) = 3
    c: DistanceX(g5,g5) = 3.5
    c: DistanceX(g6,g6) = 3.5
    c: DistanceX(g5,g6) = 6
    c: DistanceX(g0,g1) = 1.5
    c: DistanceX(g1,g2) = 1.5
    c: DistanceX(g2,g3) = 1.5
    c: DistanceX(g3,g4) = 1.5
    c: Coincident(g7,g6)
    c: PointOnObject(g7,g6)
    c: Horizontal(g7)
    c: DistanceX(g7,g-5) = 8
    c: DistanceX(g4,g-6) = 3.4
    c: Coincident(g8,g0)
    c: Coincident(g8,g0)
    c: Coincident(g9,g1)
    c: Coincident(g9,g1)
    c: Coincident(g10,g2)
    c: Coincident(g10,g2)
    c: Coincident(g11,g3)
    c: Coincident(g11,g3)
    c: Coincident(g12,g4)
    c: Coincident(g12,g4)
    c: Coincident(g13,g6)
    c: Coincident(g13,g6)
    c: Coincident(g14,g5)
    c: Coincident(g14,g5)
FEATURE [PartDesign::Pad] Pad170
  BaseFeature = -> Pad169
  Direction = (0,0,-1)
  Length = 0.25
  Length2 = 10
  Profile = -> Pad169 [Face9]
  Refine = true
  Suppressed = false
  Type = 0
FEATURE [PartDesign::Pad] Pad171
  BaseFeature = -> Pad170
  Direction = (0,0,-1)
  Length = 0.75
  Length2 = 10
  Profile = -> Sketch262
  ReferenceAxis = -> Sketch262 [N_Axis]
  Refine = true
  Suppressed = false
  Type = 0
FEATURE [Sketcher::SketchObject] Sketch263
  ArcFitTolerance = 1e-06
  AttachmentSupport = -> [Pad171]
  ExternalGeometry = -> [Pad171]
  FullyConstrained = true
  MakeInternals = false
  MapMode = 5
  Placement = pos=(0,0,-6.75) rot=(1,0,0;3.14159rad)
  sketch-geometry (12):
    g0: LineSegment [constr] StartX=14 StartY=-3.53842 StartZ=0 EndX=12 EndY=-3.53842 EndZ=0
    g1: LineSegment [constr] StartX=14 StartY=-3.53842 StartZ=0 EndX=16 EndY=-3.53842 EndZ=0
    g2: LineSegment [constr] StartX=23.5 StartY=-3.53842 StartZ=0 EndX=21.5 EndY=-3.53842 EndZ=0
    g3: LineSegment [constr] StartX=23.5 StartY=-3.53842 StartZ=0 EndX=25.5 EndY=-3.53842 EndZ=0
    g4: LineSegment StartX=16 StartY=-3.53842 StartZ=0 EndX=12 EndY=-3.53842 EndZ=0
    g5: LineSegment StartX=16 StartY=-3.53842 StartZ=0 EndX=16 EndY=-2.57017 EndZ=0
    g6: LineSegment StartX=16 StartY=-2.57017 StartZ=0 EndX=12 EndY=-2.57017 EndZ=0
    g7: LineSegment StartX=12 StartY=-3.53842 StartZ=0 EndX=12 EndY=-2.57017 EndZ=0
    g8: LineSegment StartX=21.5 StartY=-3.53842 StartZ=0 EndX=25.5 EndY=-3.53842 EndZ=0
    g9: LineSegment StartX=21.5 StartY=-3.53842 StartZ=0 EndX=21.5 EndY=-2.57017 EndZ=0
    g10: LineSegment StartX=25.5 StartY=-3.53842 StartZ=0 EndX=25.5 EndY=-2.57017 EndZ=0
    g11: LineSegment StartX=25.5 StartY=-2.57017 StartZ=0 EndX=21.5 EndY=-2.57017 EndZ=0
  constraints (33):
    c: Coincident(g0,g-3)
    c: PointOnObject(g0,g-3)
    c: Horizontal(g0)
    c: Coincident(g1,g0)
    c: PointOnObject(g1,g-3)
    c: Horizontal(g1)
    c: Coincident(g2,g-4)
    c: PointOnObject(g2,g-4)
    c: Horizontal(g2)
    c: Coincident(g3,g2)
    c: PointOnObject(g3,g-4)
    c: Horizontal(g3)
    c: PointOnObject(g4,g-3)
    c: Horizontal(g4)
    c: Vertical(g5)
    c: Coincident(g6,g5)
    c: Horizontal(g6)
    c: Vertical(g7)
    c: Coincident(g7,g6)
    c: PointOnObject(g-5,g6)
    c: Coincident(g4,g0)
    c: Coincident(g7,g0)
    c: Coincident(g5,g4)
    c: Coincident(g8,g2)
    c: Coincident(g8,g3)
    c: Coincident(g9,g8)
    c: Coincident(g11,g10)
    c: Coincident(g11,g9)
    c: Horizontal(g11)
    c: PointOnObject(g-6,g11)
    c: Vertical(g9)
    c: Vertical(g10)
    c: Coincident(g10,g8)
FEATURE [PartDesign::Pad] Pad172
  BaseFeature = -> Pad171
  Direction = (0,0,-1)
  Length = 0.75
  Length2 = 10
  Profile = -> Sketch263
  ReferenceAxis = -> Sketch263 [N_Axis]
  Refine = true
  Reversed = true
  Suppressed = false
  Type = 0
FEATURE [PartDesign::Body] Body016  label="Left_Outer_Leg"
  AllowCompound = false
  Group = -> [Binder008,Pad161,Sketch249,Pocket114,Sketch250,Pad162,Sketch251,Pad163,Sketch252,Pad164,Sketch253,Pad165,Sketch254,Pad166,Sketch255,Sketch256,Pocket115,Sketch257,Pad167,Sketch258,Pocket116,Pocket117,Sketch259,Pocket118,Sketch260,Pad168,Sketch261,Pad169,Sketch262,Pad170,Pad171,Sketch263,Pad172]
  Origin = -> Origin017
  Placement = pos=(53.7,-27.4,-19.5) rot=(0,-0.71,-0.71;3.14159rad)
  Tip = -> Pad172
FEATURE [PartDesign::SubShapeBinder] Binder009
  BindCopyOnChange = 0
  BindMode = 2
  ClaimChildren = false
  Context = -> Body017 [Binder009.]
  Fuse = false
  MakeFace = true
  OffsetFill = false
  OffsetIntersection = false
  OffsetJoinType = 0
  OffsetOpenResult = false
  PartialLoad = false
  Refine = true
  Relative = true
  _Version = 2
FEATURE [Sketcher::SketchObject] Sketch264
  ArcFitTolerance = 1e-06
  AttachmentSupport = -> [Binder009]
  ExternalGeometry = -> [Binder009]
  FullyConstrained = true
  MakeInternals = false
  MapMode = 5
  Placement = pos=(0,0,1.5) rot=(0,0,1;0rad)
  sketch-geometry (6):
    g0: ArcOfCircle CenterX=37 CenterY=0 CenterZ=0 NormalX=0 NormalY=0 NormalZ=1 AngleXU=0 Radius=6.5 StartAngle=4.71239 EndAngle=7.76154
    g1: LineSegment [constr] StartX=37 StartY=0 StartZ=0 EndX=37 EndY=-6.5 EndZ=0
    g2: LineSegment [constr] StartX=37 StartY=0 StartZ=0 EndX=43.5 EndY=0 EndZ=0
    g3: LineSegment StartX=37 StartY=-6.5 StartZ=0 EndX=33.5 EndY=-6.5 EndZ=0
    g4: LineSegment StartX=33.5 StartY=-6.5 StartZ=0 EndX=33.5 EndY=6.87 EndZ=0
    g5: ArcOfCircle CenterX=18.5075 CenterY=-169.002 CenterZ=0 NormalX=0 NormalY=0 NormalZ=1 AngleXU=0 Radius=176.51 StartAngle=1.46242 EndAngle=1.48576
  constraints (19):
    c: Diameter(g0) = 13
    c: Coincident(g1,g0)
    c: Coincident(g1,g0)
    c: Vertical(g1)
    c: Coincident(g2,g0)
    c: PointOnObject(g2,g0)
    c: Horizontal(g2)
    c: DistanceX(g-3,g2) = 10
    c: PointOnObject(g2,g-1)
    c: DistanceX(g0,g0) = 0.6
    c: Coincident(g3,g0)
    c: Horizontal(g3)
    c: Coincident(g4,g3)
    c: Vertical(g4)
    c: PointOnObject(g-3,g4)
    c: Coincident(g5,g0)
    c: Coincident(g5,g4)
    c: DistanceY(g3,g4) = 13.37
    c: Radius(g5) = 176.51
FEATURE [PartDesign::Pad] Pad173
  Direction = (0,0,1)
  Length = 8
  Length2 = 10
  Profile = -> Sketch264
  ReferenceAxis = -> Sketch264 [N_Axis]
  Refine = true
  Reversed = true
  Suppressed = false
  Type = 0
FEATURE [Sketcher::SketchObject] Sketch265
  ArcFitTolerance = 1e-06
  AttachmentSupport = -> [Pad173]
  ExternalGeometry = -> [Pad173]
  FullyConstrained = true
  MakeInternals = false
  MapMode = 5
  Placement = pos=(0,0,-6.5) rot=(1,0,0;3.14159rad)
  sketch-geometry (6):
    g0: LineSegment StartX=33.5 StartY=5 StartZ=0 EndX=33.5 EndY=-5.37 EndZ=0
    g1: LineSegment StartX=33.5 StartY=-5.37 StartZ=0 EndX=37.6 EndY=-4.96387 EndZ=0
    g2: LineSegment StartX=33.5 StartY=5 StartZ=0 EndX=37 EndY=5 EndZ=0
    g3: ArcOfCircle CenterX=37 CenterY=0 CenterZ=0 NormalX=0 NormalY=0 NormalZ=1 AngleXU=0 Radius=5 StartAngle=4.83268 EndAngle=7.85398
    g4: LineSegment [constr] StartX=37 StartY=6.5 StartZ=0 EndX=37 EndY=5 EndZ=0
    g5: LineSegment [constr] StartX=37.6 StartY=-6.47225 StartZ=0 EndX=37.6 EndY=-4.96387 EndZ=0
  constraints (16):
    c: PointOnObject(g0,g-6)
    c: PointOnObject(g0,g-6)
    c: Coincident(g1,g0)
    c: Coincident(g2,g0)
    c: Horizontal(g2)
    c: Coincident(g3,g2)
    c: Coincident(g3,g1)
    c: Coincident(g3,g-4)
    c: DistanceY(g0,g-6) = 1.5
    c: Coincident(g4,g-4)
    c: Coincident(g4,g2)
    c: Vertical(g4)
    c: DistanceY(g-6,g0) = 1.5
    c: Coincident(g5,g-5)
    c: Coincident(g5,g1)
    c: Vertical(g5)
FEATURE [PartDesign::Pocket] Pocket119
  BaseFeature = -> Pad173
  Direction = (0,0,1)
  Length = 0.5
  Length2 = 5
  Profile = -> Sketch265
  ReferenceAxis = -> Sketch265 [N_Axis]
  Refine = true
  Suppressed = false
  Type = 0
FEATURE [Sketcher::SketchObject] Sketch266
  ArcFitTolerance = 1e-06
  AttachmentSupport = -> [Pocket119]
  ExternalGeometry = -> [Pocket119]
  FullyConstrained = true
  MakeInternals = false
  MapMode = 5
  Placement = pos=(0,0,-6) rot=(1,0,0;3.14159rad)
  sketch-geometry (3):
    g0: ArcOfCircle CenterX=37 CenterY=0 CenterZ=0 NormalX=0 NormalY=0 NormalZ=1 AngleXU=0 Radius=4.34222 StartAngle=3.77496 EndAngle=8.5615
    g1: LineSegment StartX=33.5 StartY=3.3 StartZ=0 EndX=33.5 EndY=-2.57 EndZ=0
    g2: LineSegment StartX=34.1778 StartY=3.3 StartZ=0 EndX=33.5 EndY=3.3 EndZ=0
  constraints (9):
    c: DistanceY(g-4,g0) = 2.8
    c: DistanceY(g0,g-5) = 1.7
    c: PointOnObject(g0,g-6)
    c: Coincident(g1,g0)
    c: Coincident(g0,g-3)
    c: Coincident(g2,g0)
    c: Coincident(g2,g1)
    c: Horizontal(g2)
    c: PointOnObject(g1,g-6)
FEATURE [PartDesign::Pad] Pad174
  BaseFeature = -> Pocket119
  Direction = (0,0,-1)
  Length = 1.25
  Length2 = 10
  Profile = -> Sketch266
  ReferenceAxis = -> Sketch266 [N_Axis]
  Refine = true
  Suppressed = false
  Type = 0
FEATURE [Sketcher::SketchObject] Sketch267
  ArcFitTolerance = 1e-06
  AttachmentSupport = -> [Pad174]
  ExternalGeometry = -> [Pad174]
  FullyConstrained = true
  MakeInternals = false
  MapMode = 5
  Placement = pos=(0,0,-6.5) rot=(1,0,0;3.14159rad)
  sketch-geometry (17):
    g0: ArcOfCircle CenterX=36.7879 CenterY=6.49654 CenterZ=0 NormalX=0 NormalY=0 NormalZ=1 AngleXU=0 Radius=0.5 StartAngle=6.27735 EndAngle=9.41785
    g1: ArcOfCircle CenterX=36.7853 CenterY=-6.55898 CenterZ=0 NormalX=0 NormalY=0 NormalZ=1 AngleXU=0 Radius=0.5 StartAngle=3.24391 EndAngle=6.38834
    g2: ArcOfCircle CenterX=40.1188 CenterY=-5.70292 CenterZ=0 NormalX=0 NormalY=0 NormalZ=1 AngleXU=0 Radius=0.5 StartAngle=3.60356 EndAngle=6.82209
    g3: ArcOfCircle CenterX=40.1188 CenterY=5.70292 CenterZ=0 NormalX=0 NormalY=0 NormalZ=1 AngleXU=0 Radius=0.5 StartAngle=5.74428 EndAngle=8.96281
    g4: ArcOfCircle CenterX=42.5842 CenterY=3.32673 CenterZ=0 NormalX=0 NormalY=0 NormalZ=1 AngleXU=0 Radius=0.5 StartAngle=5.2112 EndAngle=8.42974
    g5: ArcOfCircle CenterX=42.5842 CenterY=-3.32673 CenterZ=0 NormalX=0 NormalY=0 NormalZ=1 AngleXU=0 Radius=0.5 StartAngle=4.13663 EndAngle=7.35517
    g6: ArcOfCircle CenterX=43.5 CenterY=0 CenterZ=0 NormalX=0 NormalY=0 NormalZ=1 AngleXU=0 Radius=0.5 StartAngle=4.67392 EndAngle=7.89245
    g7: LineSegment [constr] StartX=36.2879 StartY=6.5 StartZ=0 EndX=36.2879 EndY=-6.61005 EndZ=0
    g8: LineSegment [constr] StartX=39.6712 StartY=5.92578 StartZ=0 EndX=39.6712 EndY=-5.92578 EndZ=0
    g9: LineSegment [constr] StartX=42.3119 StartY=3.74612 StartZ=0 EndX=42.3119 EndY=-3.74612 EndZ=0
    g10: LineSegment StartX=36.2879 StartY=6.5 StartZ=0 EndX=37.2879 EndY=6.49362 EndZ=0
    g11: LineSegment StartX=39.6712 StartY=5.92578 StartZ=0 EndX=40.5479 EndY=5.44632 EndZ=0
    g12: LineSegment StartX=42.3119 StartY=3.74612 StartZ=0 EndX=42.8234 EndY=2.88765 EndZ=0
    g13: LineSegment StartX=43.4808 StartY=0.49963 StartZ=0 EndX=43.4808 EndY=-0.49963 EndZ=0
    g14: LineSegment StartX=42.8234 StartY=-2.88765 StartZ=0 EndX=42.3119 EndY=-3.74612 EndZ=0
    g15: LineSegment StartX=40.5479 StartY=-5.44632 StartZ=0 EndX=39.6712 EndY=-5.92578 EndZ=0
    g16: LineSegment StartX=37.2825 StartY=-6.5065 StartZ=0 EndX=36.2879 EndY=-6.61005 EndZ=0
  constraints (56):
    c: PointOnObject(g0,g-5)
    c: PointOnObject(g0,g-4)
    c: PointOnObject(g1,g-3)
    c: PointOnObject(g2,g-4)
    c: PointOnObject(g2,g-4)
    c: PointOnObject(g3,g-4)
    c: PointOnObject(g3,g-4)
    c: PointOnObject(g4,g-4)
    c: PointOnObject(g4,g-4)
    c: PointOnObject(g5,g-4)
    c: PointOnObject(g5,g-4)
    c: PointOnObject(g6,g-4)
    c: PointOnObject(g6,g-4)
    c: PointOnObject(g6,g-1)
    c: Diameter(g0) = 1
    c: Diameter(g3) = 1
    c: Diameter(g4) = 1
    c: Diameter(g6) = 1
    c: Diameter(g5) = 1
    c: Diameter(g2) = 1
    c: Diameter(g1) = 1
    c: PointOnObject(g6,g-4)
    c: PointOnObject(g4,g-4)
    c: PointOnObject(g3,g-4)
    c: PointOnObject(g0,g-4)
    c: PointOnObject(g5,g-4)
    c: PointOnObject(g2,g-4)
    c: PointOnObject(g1,g-3)
    c: Distance(g-3,g1) = 2.8
    c: PointOnObject(g1,g-3)
    c: Coincident(g7,g0)
    c: Coincident(g7,g1)
    c: Vertical(g7)
    c: Distance(g0,g3) = 2.45
    c: Distance(g3,g4) = 2.45
    c: Distance(g4,g6) = 2.47686
    c: Coincident(g8,g3)
    c: Coincident(g8,g2)
    c: Vertical(g8)
    c: Vertical(g4,g5)
    c: Coincident(g9,g4)
    c: Coincident(g9,g5)
    c: Coincident(g11,g3)
    c: Coincident(g11,g3)
    c: Coincident(g12,g4)
    c: Coincident(g12,g4)
    c: Coincident(g13,g6)
    c: Coincident(g13,g6)
    c: Coincident(g14,g5)
    c: Coincident(g14,g5)
    c: Coincident(g15,g2)
    c: Coincident(g15,g2)
    c: Coincident(g10,g0)
    c: Coincident(g10,g0)
    c: Coincident(g16,g1)
    c: Coincident(g16,g1)
FEATURE [PartDesign::Pad] Pad175
  BaseFeature = -> Pad174
  Direction = (0,0,-1)
  Length = 8
  Length2 = 10
  Profile = -> Sketch267
  ReferenceAxis = -> Sketch267 [N_Axis]
  Refine = true
  Reversed = true
  Suppressed = false
  Type = 0
FEATURE [Sketcher::SketchObject] Sketch268
  ArcFitTolerance = 1e-06
  AttachmentSupport = -> [Pad175]
  ExternalGeometry = -> [Pad175]
  FullyConstrained = true
  MakeInternals = false
  MapMode = 5
  Placement = pos=(0,0,-6.5) rot=(1,0,0;3.14159rad)
  sketch-geometry (4):
    g0: LineSegment StartX=43.4374 StartY=0.9 StartZ=0 EndX=43.4374 EndY=-0.9 EndZ=0
    g1: LineSegment StartX=43.4374 StartY=0.9 StartZ=0 EndX=45.5374 EndY=0.9 EndZ=0
    g2: LineSegment StartX=45.5374 StartY=0.9 StartZ=0 EndX=45.5374 EndY=-0.9 EndZ=0
    g3: LineSegment StartX=45.5374 StartY=-0.9 StartZ=0 EndX=43.4374 EndY=-0.9 EndZ=0
  constraints (12):
    c: PointOnObject(g0,g-3)
    c: PointOnObject(g0,g-4)
    c: Vertical(g0)
    c: DistanceY(g0,g0) = 1.8
    c: Coincident(g1,g0)
    c: Horizontal(g1)
    c: Coincident(g2,g1)
    c: Vertical(g2)
    c: Coincident(g3,g2)
    c: Coincident(g3,g0)
    c: Horizontal(g3)
    c: DistanceX(g1,g1) = 2.1
FEATURE [PartDesign::Pad] Pad176
  BaseFeature = -> Pad175
  Direction = (0,0,-1)
  Length = 4
  Length2 = 10
  Profile = -> Sketch268
  ReferenceAxis = -> Sketch268 [N_Axis]
  Refine = true
  Reversed = true
  Suppressed = false
  Type = 0
FEATURE [Sketcher::SketchObject] Sketch269
  ArcFitTolerance = 1e-06
  AttachmentSupport = -> [Pad176]
  ExternalGeometry = -> [Pad176]
  FullyConstrained = true
  MakeInternals = false
  MapMode = 5
  Placement = pos=(0,0,-6.5) rot=(1,0,0;3.14159rad)
  sketch-geometry (4):
    g0: LineSegment StartX=45.5374 StartY=0.9 StartZ=0 EndX=43.4374 EndY=0.9 EndZ=0
    g1: LineSegment StartX=43.4374 StartY=0.9 StartZ=0 EndX=43.4374 EndY=-0.9 EndZ=0
    g2: LineSegment StartX=43.4374 StartY=-0.9 StartZ=0 EndX=45.5374 EndY=-0.9 EndZ=0
    g3: LineSegment StartX=45.5374 StartY=-0.9 StartZ=0 EndX=45.5374 EndY=0.9 EndZ=0
  constraints (10):
    c: Coincident(g0,g1)
    c: Coincident(g1,g2)
    c: Coincident(g2,g3)
    c: Coincident(g3,g0)
    c: Horizontal(g0)
    c: Horizontal(g2)
    c: Vertical(g1)
    c: Vertical(g3)
    c: Coincident(g0,g-5)
    c: Coincident(g1,g-4)
FEATURE [PartDesign::Pad] Pad177
  BaseFeature = -> Pad176
  Direction = (0,0,-1)
  Length = 1.7
  Length2 = 10
  Profile = -> Sketch269
  ReferenceAxis = -> Sketch269 [N_Axis]
  Refine = true
  Suppressed = false
  Type = 0
FEATURE [Sketcher::SketchObject] Sketch270
  ArcFitTolerance = 1e-06
  AttachmentSupport = -> [Pad177]
  ExternalGeometry = -> [Pad177]
  FullyConstrained = true
  MakeInternals = false
  MapMode = 5
  Placement = pos=(0,0.9,0) rot=(0,0.707107,0.707107;3.14159rad)
  sketch-geometry (3):
    g0: LineSegment StartX=-43.4374 StartY=-8.2 StartZ=0 EndX=-44.0374 EndY=-8.2 EndZ=0
    g1: LineSegment StartX=-44.0374 StartY=-8.2 StartZ=0 EndX=-43.4374 EndY=-7.6 EndZ=0
    g2: LineSegment StartX=-43.4374 StartY=-7.6 StartZ=0 EndX=-43.4374 EndY=-8.2 EndZ=0
  constraints (8):
    c: Coincident(g0,g-4)
    c: PointOnObject(g0,g-4)
    c: Coincident(g1,g0)
    c: PointOnObject(g1,g-3)
    c: Coincident(g2,g1)
    c: Coincident(g2,g0)
    c: DistanceX(g-5,g0) = 1.5
    c: Angle(g0,g1) = 0.785398
FEATURE [PartDesign::Pocket] Pocket120
  BaseFeature = -> Pad177
  Direction = (0,-1,2e-16)
  Length = 5
  Length2 = 5
  Profile = -> Sketch270
  ReferenceAxis = -> Sketch270 [N_Axis]
  Refine = true
  Suppressed = false
  Type = 0
FEATURE [Sketcher::SketchObject] Sketch271
  ArcFitTolerance = 1e-06
  AttachmentSupport = -> [Pocket120]
  ExternalGeometry = -> [Pocket120]
  FullyConstrained = true
  MakeInternals = false
  MapMode = 5
  Placement = pos=(0,0.9,0) rot=(0,0.707107,0.707107;3.14159rad)
  sketch-geometry (3):
    g0: LineSegment StartX=-43.4374 StartY=-7.6 StartZ=0 EndX=-42.3374 EndY=-6.5 EndZ=0
    g1: LineSegment StartX=-42.3374 StartY=-6.5 StartZ=0 EndX=-43.4374 EndY=-6.5 EndZ=0
    g2: LineSegment StartX=-43.4374 StartY=-6.5 StartZ=0 EndX=-43.4374 EndY=-7.6 EndZ=0
  constraints (7):
    c: Coincident(g0,g-4)
    c: PointOnObject(g0,g-5)
    c: Coincident(g1,g0)
    c: Coincident(g1,g-7)
    c: Coincident(g2,g1)
    c: Coincident(g2,g0)
    c: Parallel(g0,g-4)
FEATURE [PartDesign::Pad] Pad178
  BaseFeature = -> Pocket120
  Direction = (0,1,-2e-16)
  Length = 1.8
  Length2 = 10
  Profile = -> Sketch271
  ReferenceAxis = -> Sketch271 [N_Axis]
  Refine = true
  Reversed = true
  Suppressed = false
  Type = 0
FEATURE [Sketcher::SketchObject] Sketch272
  ArcFitTolerance = 1e-06
  AttachmentSupport = -> [Pad178]
  ExternalGeometry = -> [Pad178]
  FullyConstrained = true
  MakeInternals = false
  MapMode = 5
  Placement = pos=(0,0,1.5) rot=(0,0,1;0rad)
  sketch-geometry (4):
    g0: ArcOfCircle CenterX=37 CenterY=0 CenterZ=0 NormalX=0 NormalY=0 NormalZ=1 AngleXU=0 Radius=4.25 StartAngle=4.14055 EndAngle=8.42582
    g1: LineSegment StartX=34.7 StartY=3.57386 StartZ=0 EndX=34.7 EndY=4.996 EndZ=0
    g2: LineSegment StartX=34.7 StartY=-3.57386 StartZ=0 EndX=34.7 EndY=-4.996 EndZ=0
    g3: ArcOfCircle CenterX=37 CenterY=0 CenterZ=0 NormalX=0 NormalY=0 NormalZ=1 AngleXU=0 Radius=5.5 StartAngle=4.28095 EndAngle=8.28542
  constraints (13):
    c: Coincident(g0,g-3)
    c: Diameter(g0) = 8.5
    c: Coincident(g1,g0)
    c: Coincident(g2,g0)
    c: Coincident(g3,g2)
    c: Coincident(g3,g1)
    c: Coincident(g0,g3)
    c: DistanceX(g-4,g2) = 1.2
    c: DistanceX(g-4,g1) = 1.2
    c: Vertical(g1)
    c: Vertical(g2)
    c: Radius(g-3) = 6.5
    c: Radius(g3) = 5.5
FEATURE [PartDesign::Pocket] Pocket121
  BaseFeature = -> Pad178
  Direction = (0,0,-1)
  Length = 6.5
  Length2 = 5
  Profile = -> Sketch272
  ReferenceAxis = -> Sketch272 [N_Axis]
  Refine = true
  Suppressed = false
  Type = 0
FEATURE [Sketcher::SketchObject] Sketch273
  ArcFitTolerance = 1e-06
  AttachmentSupport = -> [Pocket121]
  ExternalGeometry = -> [Pocket121]
  FullyConstrained = true
  MakeInternals = false
  MapMode = 5
  Placement = pos=(0,0,-7.25) rot=(1,0,0;3.14159rad)
  sketch-geometry (1):
    g0: Circle CenterX=37 CenterY=0 CenterZ=0 NormalX=0 NormalY=0 NormalZ=1 AngleXU=0 Radius=2.1
  constraints (2):
    c: Coincident(g0,g-3)
    c: Radius(g0) = 2.1
FEATURE [PartDesign::Pocket] Pocket122
  BaseFeature = -> Pocket121
  Direction = (0,0,1)
  Length = 4.7
  Length2 = 5
  Profile = -> Sketch273
  ReferenceAxis = -> Sketch273 [N_Axis]
  Refine = true
  Suppressed = false
  Type = 0
FEATURE [Sketcher::SketchObject] Sketch274
  ArcFitTolerance = 1e-06
  AttachmentSupport = -> [Pocket122]
  ExternalGeometry = -> [Pocket122]
  FullyConstrained = true
  MakeInternals = false
  MapMode = 5
  Placement = pos=(0,0,-2.55) rot=(1,0,0;3.14159rad)
  sketch-geometry (1):
    g0: Circle CenterX=37 CenterY=0 CenterZ=0 NormalX=0 NormalY=0 NormalZ=1 AngleXU=0 Radius=1.4
  constraints (2):
    c: Coincident(g0,g-3)
    c: Radius(g0) = 1.4
FEATURE [PartDesign::Pocket] Pocket123
  BaseFeature = -> Pocket122
  Direction = (0,0,1)
  Length = 5
  Length2 = 5
  Profile = -> Sketch274
  ReferenceAxis = -> Sketch274 [N_Axis]
  Refine = true
  Suppressed = false
  Type = 0
FEATURE [Sketcher::SketchObject] Sketch275
  ArcFitTolerance = 1e-06
  AttachmentSupport = -> [Pocket123]
  ExternalGeometry = -> [Pocket123]
  FullyConstrained = true
  MakeInternals = false
  MapMode = 5
  Placement = pos=(33.5,8e-15,0) rot=(0.57735,-0.57735,-0.57735;2.0944rad)
  sketch-geometry (1):
    g0: Circle CenterX=0 CenterY=-2.5 CenterZ=0 NormalX=0 NormalY=0 NormalZ=1 AngleXU=0 Radius=1.5
  constraints (5):
    c: DistanceX(g-4,g-4) = 13.37
    c: DistanceY(g-5,g-5) = 8
    c: PointOnObject(g0,g-2)
    c: Radius(g0) = 1.5
    c: DistanceY(g0,g-5) = 4
FEATURE [PartDesign::Pad] Pad179
  BaseFeature = -> Pocket123
  Direction = (-1,0,0)
  Length = 1.6
  Length2 = 10
  Profile = -> Sketch275
  ReferenceAxis = -> Sketch275 [N_Axis]
  Refine = true
  Suppressed = false
  Type = 0
FEATURE [Sketcher::SketchObject] Sketch276
  ArcFitTolerance = 1e-06
  AttachmentSupport = -> [Pad179]
  ExternalGeometry = -> [Pad179]
  FullyConstrained = true
  MakeInternals = false
  MapMode = 5
  Placement = pos=(31.9,0,0) rot=(0.57735,-0.57735,-0.57735;2.0944rad)
  sketch-geometry (1):
    g0: Circle CenterX=0 CenterY=-2.5 CenterZ=0 NormalX=0 NormalY=0 NormalZ=1 AngleXU=0 Radius=2.5
  constraints (2):
    c: Coincident(g0,g-3)
    c: Diameter(g0) = 5
FEATURE [PartDesign::Pad] Pad180
  BaseFeature = -> Pad179
  Direction = (-1,0,0)
  Length = 1.5
  Length2 = 10
  Profile = -> Sketch276
  ReferenceAxis = -> Sketch276 [N_Axis]
  Refine = true
  Suppressed = false
  Type = 0
FEATURE [PartDesign::Body] Body017  label="Left_Ankle"
  AllowCompound = false
  Group = -> [Binder009,Sketch264,Pad173,Sketch265,Pocket119,Sketch266,Pad174,Sketch267,Pad175,Sketch268,Pad176,Sketch269,Pad177,Sketch270,Pocket120,Sketch271,Pad178,Sketch272,Pocket121,Sketch273,Pocket122,Sketch274,Pocket123,Sketch275,Pad179,Sketch276,Pad180]
  Origin = -> Origin018
  Placement = pos=(53.7,-27.4,-19.5) rot=(0,-0.71,-0.71;3.14159rad)
  Tip = -> Pad180
FEATURE [PartDesign::SubShapeBinder] Binder010
  BindCopyOnChange = 0
  BindMode = 2
  ClaimChildren = false
  Context = -> Body018 [Binder010.]
  Fuse = false
  MakeFace = true
  OffsetFill = false
  OffsetIntersection = false
  OffsetJoinType = 0
  OffsetOpenResult = false
  PartialLoad = false
  Refine = true
  Relative = true
  _Version = 2
FEATURE [Sketcher::SketchObject] Sketch277
  ArcFitTolerance = 1e-06
  AttachmentSupport = -> [Binder010]
  ExternalGeometry = -> [Binder010]
  FullyConstrained = false
  MakeInternals = false
  MapMode = 5
  Placement = pos=(0,0,1.5) rot=(0,0,1;0rad)
  sketch-geometry (4):
    g0: LineSegment StartX=33.5 StartY=2.57971 StartZ=0 EndX=33.5 EndY=-2.42029 EndZ=0
    g1: LineSegment StartX=33.5 StartY=-2.42029 StartZ=0 EndX=40.5 EndY=-2.42029 EndZ=0
    g2: LineSegment StartX=40.5 StartY=-2.42029 StartZ=0 EndX=40.5 EndY=2.57971 EndZ=0
    g3: LineSegment StartX=40.5 StartY=2.57971 StartZ=0 EndX=33.5 EndY=2.57971 EndZ=0
  constraints (12):
    c: Coincident(g0,g1)
    c: Coincident(g1,g2)
    c: Coincident(g2,g3)
    c: Coincident(g3,g0)
    c: Vertical(g0)
    c: Vertical(g2)
    c: Horizontal(g1)
    c: Horizontal(g3)
    c: PointOnObject(g0,g-5)
    c: DistanceY(g2,g2) = 5
    c: DistanceX(g3,g3) = 7
    c: DistanceX(g0,g-4) = 3.5
FEATURE [PartDesign::Pad] Pad181
  Direction = (0,0,1)
  Length = 1
  Length2 = 10
  Profile = -> Sketch277
  ReferenceAxis = -> Sketch277 [N_Axis]
  Refine = true
  Suppressed = false
  Type = 0
FEATURE [Sketcher::SketchObject] Sketch278
  ArcFitTolerance = 1e-06
  AttachmentSupport = -> [Pad181]
  ExternalGeometry = -> [Pad181]
  FullyConstrained = true
  MakeInternals = false
  MapMode = 5
  Placement = pos=(0,0,2.5) rot=(0,0,1;0rad)
  sketch-geometry (4):
    g0: LineSegment StartX=33.5 StartY=4.07971 StartZ=0 EndX=33.5 EndY=-3.92029 EndZ=0
    g1: LineSegment StartX=33.5 StartY=-3.92029 StartZ=0 EndX=44.5 EndY=-3.92029 EndZ=0
    g2: LineSegment StartX=44.5 StartY=-3.92029 StartZ=0 EndX=44.5 EndY=4.07971 EndZ=0
    g3: LineSegment StartX=44.5 StartY=4.07971 StartZ=0 EndX=33.5 EndY=4.07971 EndZ=0
  constraints (13):
    c: Coincident(g0,g1)
    c: Coincident(g1,g2)
    c: Coincident(g2,g3)
    c: Coincident(g3,g0)
    c: Vertical(g0)
    c: Vertical(g2)
    c: Horizontal(g1)
    c: Horizontal(g3)
    c: PointOnObject(g-6,g0)
    c: DistanceY(g0,g0) = 8
    c: DistanceY(g-6,g-6) = 5
    c: DistanceY(g-6,g0) = 1.5
    c: DistanceX(g3,g3) = 11
FEATURE [PartDesign::Pad] Pad182
  BaseFeature = -> Pad181
  Direction = (0,0,1)
  Length = 7.8
  Length2 = 10
  Profile = -> Sketch278
  ReferenceAxis = -> Sketch278 [N_Axis]
  Refine = true
  Suppressed = false
  Type = 0
FEATURE [Sketcher::SketchObject] Sketch279
  ArcFitTolerance = 1e-06
  AttachmentSupport = -> [Pad182]
  ExternalGeometry = -> [Pad182]
  FullyConstrained = true
  MakeInternals = false
  MapMode = 5
  Placement = pos=(0,4.07971,0) rot=(0,0.707107,0.707107;3.14159rad)
  sketch-geometry (3):
    g0: LineSegment StartX=-33.5 StartY=2.5 StartZ=0 EndX=-33.5 EndY=10.3 EndZ=0
    g1: LineSegment StartX=-33.5 StartY=10.3 StartZ=0 EndX=-37.5 EndY=10.3 EndZ=0
    g2: LineSegment StartX=-37.5 StartY=10.3 StartZ=0 EndX=-33.5 EndY=2.5 EndZ=0
  constraints (7):
    c: Coincident(g0,g-3)
    c: Coincident(g0,g-4)
    c: Coincident(g1,g0)
    c: PointOnObject(g1,g-4)
    c: Coincident(g2,g1)
    c: Coincident(g2,g0)
    c: DistanceX(g-4,g1) = 7
FEATURE [PartDesign::Pocket] Pocket124
  BaseFeature = -> Pad182
  Direction = (0,-1,2e-16)
  Length = 8
  Length2 = 5
  Profile = -> Sketch279
  ReferenceAxis = -> Sketch279 [N_Axis]
  Refine = true
  Suppressed = false
  Type = 0
FEATURE [Sketcher::SketchObject] Sketch280
  ArcFitTolerance = 1e-06
  AttachmentSupport = -> [Pocket124]
  ExternalGeometry = -> [Pocket124]
  FullyConstrained = true
  MakeInternals = false
  MapMode = 5
  Placement = pos=(0,4.07971,0) rot=(0,0.707107,0.707107;3.14159rad)
  sketch-geometry (1):
    g0: Circle CenterX=-41 CenterY=6.4 CenterZ=0 NormalX=0 NormalY=0 NormalZ=1 AngleXU=0 Radius=2
  constraints (5):
    c: Diameter(g0) = 4
    c: DistanceY(g-3,g-3) = 7.8
    c: DistanceY(g0,g-3) = 3.9
    c: DistanceX(g-4,g-4) = 7
    c: DistanceX(g-4,g0) = 3.5
FEATURE [PartDesign::Pocket] Pocket125
  BaseFeature = -> Pocket124
  Direction = (0,-1,2e-16)
  Length = 3.3
  Length2 = 5
  Profile = -> Sketch280
  ReferenceAxis = -> Sketch280 [N_Axis]
  Refine = true
  Suppressed = false
  Type = 0
FEATURE [Sketcher::SketchObject] Sketch281
  ArcFitTolerance = 1e-06
  AttachmentSupport = -> [Pocket125]
  ExternalGeometry = -> [Pocket125]
  FullyConstrained = true
  MakeInternals = false
  MapMode = 5
  Placement = pos=(0,-3.92029,0) rot=(1,0,0;1.5708rad)
  sketch-geometry (1):
    g0: Circle CenterX=41 CenterY=6.4 CenterZ=0 NormalX=0 NormalY=0 NormalZ=1 AngleXU=0 Radius=2
  constraints (2):
    c: Coincident(g0,g-3)
    c: Equal(g0,g-3)
FEATURE [PartDesign::Pocket] Pocket126
  BaseFeature = -> Pocket125
  Direction = (0,1,-2e-16)
  Length = 3.3
  Length2 = 5
  Profile = -> Sketch281
  ReferenceAxis = -> Sketch281 [N_Axis]
  Refine = true
  Suppressed = false
  Type = 0
FEATURE [Sketcher::SketchObject] Sketch282
  ArcFitTolerance = 1e-06
  AttachmentSupport = -> [Pocket126]
  ExternalGeometry = -> [Pocket126]
  FullyConstrained = true
  MakeInternals = false
  MapMode = 5
  Placement = pos=(0,0,1.5) rot=(1,0,0;3.14159rad)
  sketch-geometry (1):
    g0: Circle CenterX=37 CenterY=0 CenterZ=0 NormalX=0 NormalY=0 NormalZ=1 AngleXU=0 Radius=0.9
  constraints (4):
    c: PointOnObject(g0,g-1)
    c: Radius(g0) = 0.9
    c: DistanceX(g-3,g-4) = 7
    c: DistanceX(g-3,g0) = 3.5
FEATURE [PartDesign::Pocket] Pocket127
  BaseFeature = -> Pocket126
  Direction = (0,0,1)
  Length = 5
  Length2 = 5
  Profile = -> Sketch282
  ReferenceAxis = -> Sketch282 [N_Axis]
  Refine = true
  Suppressed = false
  Type = 0
FEATURE [PartDesign::Pad] Pad183
  BaseFeature = -> Pocket127
  Direction = (1,0,0)
  Length = 0.5
  Length2 = 10
  Profile = -> Pocket127 [Face10]
  Refine = true
  Suppressed = false
  Type = 0
FEATURE [PartDesign::Fillet] Fillet013
  Base = -> Pad183 [Edge22,Edge4,Edge27,Edge23,Edge24,Edge5,Edge2,Edge3,Face1,Edge31,Edge6]
  BaseFeature = -> Pad183
  Radius = 0.5
  Refine = true
  SupportTransform = false
  Suppressed = false
  UseAllEdges = false
FEATURE [PartDesign::Body] Body018  label="Left_Foot"
  AllowCompound = false
  Group = -> [Binder010,Sketch277,Pad181,Sketch278,Pad182,Sketch279,Pocket124,Sketch280,Pocket125,Sketch281,Pocket126,Sketch282,Pocket127,Pad183,Fillet013]
  Origin = -> Origin019
  Placement = pos=(53.7,-27.4,-19.5) rot=(0,-0.71,-0.71;3.14159rad)
  Tip = -> Fillet013
FEATURE [PartDesign::Pad] Pad184
  BaseFeature = -> Pocket107
  Direction = (1,0,0)
  Length = 0.05
  Length2 = 10
  Profile = -> Pocket107 [Face67]
  Refine = true
  Suppressed = false
  Type = 0
FEATURE [PartDesign::Pad] Pad185
  BaseFeature = -> Pad184
  Direction = (-1,0,0)
  Length = 0.05
  Length2 = 10
  Profile = -> Pad184 [Face66]
  Refine = true
  Suppressed = false
  Type = 0
FEATURE [PartDesign::Chamfer] Chamfer004
  Angle = 45
  Base = -> Pad185 [Edge206,Edge209,Edge203,Edge202]
  BaseFeature = -> Pad185
  ChamferType = 0
  FlipDirection = false
  Refine = true
  Size = 0.04999
  Size2 = 1
  SupportTransform = false
  Suppressed = false
  UseAllEdges = false
FEATURE [PartDesign::Pad] Pad186
  BaseFeature = -> Chamfer004
  Direction = (1,0,0)
  Length = 0.5
  Length2 = 10
  Profile = -> Chamfer004 [Face8]
  Refine = true
  Suppressed = false
  Type = 0
FEATURE [PartDesign::Pad] Pad187
  BaseFeature = -> Pad186
  Direction = (-1,0,0)
  Length = 0.5
  Length2 = 10
  Profile = -> Pad186 [Face22]
  Refine = true
  Suppressed = false
  Type = 0
FEATURE [PartDesign::Chamfer] Chamfer005
  Angle = 45
  Base = -> Pad187 [Edge171,Edge251,Edge76,Edge82]
  BaseFeature = -> Pad187
  ChamferType = 0
  FlipDirection = false
  Refine = true
  Size = 0.49
  Size2 = 1
  SupportTransform = false
  Suppressed = false
  UseAllEdges = false
FEATURE [PartDesign::Body] Body010  label="Main_Head"
  AllowCompound = false
  Group = -> [Sketch213,Pad137,Sketch214,Pad138,Sketch215,Pad139,Pad140,Sketch216,Pad141,Sketch217,Pad142,Chamfer003,Sketch218,Pocket098,Sketch219,Pad143,Sketch220,Pad144,Sketch221,Pocket099,Sketch222,Pad145,Sketch223,Pocket100,Sketch224,Pocket101,Sketch225,Pocket102,Sketch226,Pad146,Sketch227,Pocket103,Sketch228,Pad147,Sketch229,Pocket104,Pocket105,Pocket106,Sketch230,Pad148,Sketch231,Pocket107,Pad184,Pad185,+4 more]
  Origin = -> Origin011
  Tip = -> Chamfer005
FEATURE [App::Part] Part  label="Head"
  Group = -> [Body010,Body011,Body012,Body013]
  Origin = -> Origin010
  Placement = pos=(5.6,-12.2,-9.9) rot=(0.57735,-0.57735,-0.57735;2.0944rad)
FEATURE [PartDesign::Pad] Pad188
  BaseFeature = -> Pocket097
  Direction = (0,-2e-16,-1)
  Length = 0.075
  Length2 = 10
  Profile = -> Pocket097 [Face56,Face40,Face28,Face8]
  Refine = true
  Suppressed = false
  Type = 0
FEATURE [PartDesign::Pad] Pad189
  BaseFeature = -> Pad188
  Direction = (0,2e-16,1)
  Length = 0.075
  Length2 = 10
  Profile = -> Pad188 [Face7,Face19,Face29]
  Refine = true
  Suppressed = false
  Type = 0
FEATURE [PartDesign::Chamfer] Chamfer006
  Angle = 45
  Base = -> Pad189 [Edge108,Edge72,Edge129,Edge122,Edge91,Edge70]
  BaseFeature = -> Pad189
  ChamferType = 0
  FlipDirection = false
  Refine = true
  Size = 0.2
  Size2 = 1
  SupportTransform = false
  Suppressed = false
  UseAllEdges = false
FEATURE [PartDesign::Body] Body009  label="Left_Arm"
  AllowCompound = false
  Group = -> [Binder004,Sketch187,Pad131,Sketch188,Pocket077,Sketch189,Pocket078,Sketch190,Pocket079,Sketch191,Pocket080,Sketch192,Pocket081,Sketch193,Pad132,Sketch194,Pad133,Sketch195,Pocket082,Sketch196,Pocket083,Sketch197,Pocket084,Sketch198,Pocket085,Sketch199,Pocket086,Sketch200,Pocket087,Sketch201,Pocket088,Sketch202,Pocket089,Sketch203,Pocket090,Sketch204,Pocket091,Sketch205,Pocket092,Sketch206,+17 more]
  Origin = -> Origin009
  Tip = -> Chamfer006
FEATURE [PartDesign::Pad] Pad190
  BaseFeature = -> Pad067
  Direction = (0,0,1)
  Length = 0.025
  Length2 = 10
  Profile = -> Pad067 [Face78]
  Refine = true
  Suppressed = false
  Type = 0
FEATURE [PartDesign::Pad] Pad191
  BaseFeature = -> Pad190
  Direction = (0,0,-1)
  Length = 0.025
  Length2 = 10
  Profile = -> Pad190 [Face1]
  Refine = true
  Suppressed = false
  Type = 0
FEATURE [App::Link] Link  label="Pre_Right_Arm"
  LinkedObject = -> Body009
FEATURE [Part::Mirroring] Part__Mirroring  label="Right_Arm"
  Base = (0,0,0)
  Normal = (0,1,0)
  Placement = pos=(0,-32,0) rot=(0,0,1;0rad)
  Source = -> Link
FEATURE [PartDesign::Chamfer] Chamfer007
  Angle = 45
  Base = -> Pad191 [Edge9,Edge2,Edge1,Edge3]
  BaseFeature = -> Pad191
  ChamferType = 0
  FlipDirection = false
  Refine = true
  Size = 0.1
  Size2 = 1
  SupportTransform = false
  Suppressed = false
  UseAllEdges = false
FEATURE [PartDesign::Body] Body002  label="Lower_Scoop"
  AllowCompound = false
  Group = -> [Sketch065,Pad038,Fillet003,Sketch066,Pad039,Sketch067,Pad040,Sketch068,Pad041,Sketch069,Pad042,Sketch070,Pad043,Sketch071,Pocket028,Sketch072,Pad044,Sketch073,Pad045,Pad046,Pad047,Sketch074,Pad048,Sketch075,Pad049,Sketch076,Pocket029,Sketch077,Pocket030,Sketch078,Pocket031,Sketch079,Pocket032,Sketch080,Pocket033,Sketch081,Pocket034,Sketch082,Pad050,Sketch083,Pad051,Sketch084,Pad052,Sketch085,+32 more]
  Origin = -> Origin002
  Placement = pos=(71.32,-19.15,33) rot=(-0.28,0.68,0.68;2.59356rad)
  Tip = -> Chamfer007
FEATURE [Sketcher::SketchObject] Sketch283
  ArcFitTolerance = 1e-06
  AttachmentSupport = -> [Pocket074]
  ExternalGeometry = -> [Pocket074]
  FullyConstrained = true
  MakeInternals = false
  MapMode = 5
  Placement = pos=(0,2.5,0) rot=(0,0.707107,0.707107;3.14159rad)
  sketch-geometry (4):
    g0: LineSegment StartX=0 StartY=-0.15 StartZ=0 EndX=0 EndY=8.05 EndZ=0
    g1: LineSegment StartX=0 StartY=8.05 StartZ=0 EndX=-9.5 EndY=8.05 EndZ=0
    g2: LineSegment StartX=-9.5 StartY=8.05 StartZ=0 EndX=-9.5 EndY=-0.15 EndZ=0
    g3: LineSegment StartX=-9.5 StartY=-0.15 StartZ=0 EndX=0 EndY=-0.15 EndZ=0
  constraints (10):
    c: Coincident(g0,g1)
    c: Coincident(g1,g2)
    c: Coincident(g2,g3)
    c: Coincident(g3,g0)
    c: Vertical(g2)
    c: Horizontal(g1)
    c: Horizontal(g3)
    c: Coincident(g0,g-4)
    c: Coincident(g0,g-3)
    c: DistanceX(g1,g1) = 9.5
FEATURE [PartDesign::Pad] Pad192
  BaseFeature = -> Pocket074
  Direction = (0,1,-2e-16)
  Length = 0.3
  Length2 = 10
  Profile = -> Sketch283
  ReferenceAxis = -> Sketch283 [N_Axis]
  Refine = true
  Suppressed = false
  Type = 0
FEATURE [PartDesign::Fillet] Fillet014
  Base = -> Pad192 [Edge38]
  BaseFeature = -> Pad192
  Radius = 0.5
  Refine = true
  SupportTransform = false
  Suppressed = false
  UseAllEdges = false
FEATURE [PartDesign::Pad] Pad193
  BaseFeature = -> Fillet014
  Direction = (0,0,-1)
  Length = 0.05
  Length2 = 10
  Profile = -> Fillet014 [Face14]
  Refine = true
  Suppressed = false
  Type = 0
FEATURE [PartDesign::Pad] Pad194
  BaseFeature = -> Pad193
  Direction = (0,0,1)
  Length = 0.05
  Length2 = 10
  Profile = -> Pad193 [Face12]
  Refine = true
  Suppressed = false
  Type = 0
FEATURE [PartDesign::Pad] Pad195
  BaseFeature = -> Pad194
  Direction = (0,1,0)
  Length = 0.3
  Length2 = 10
  Profile = -> Pad194 [Face14]
  Refine = true
  Suppressed = false
  Type = 0
FEATURE [PartDesign::Body] Body007  label="Arm_Connector"
  AllowCompound = false
  Group = -> [Sketch172,Pad117,Sketch173,Pocket072,Pocket073,Sketch174,Pad118,Pad119,Pad120,Pad121,Sketch175,Pocket074,Sketch283,Pad192,Fillet014,Pad193,Pad194,Pad195]
  Origin = -> Origin007
  Placement = pos=(39.55,-12.05,-13.2) rot=(0,-0.71,0.71;3.14159rad)
  Tip = -> Pad195
FEATURE [Part::Feature] Part__Feature  label="Scavanger_Gun"
  Placement = pos=(48,-55,26) rot=(0,0,1;0rad)
  shape: bbox 30.1 x 5 x 12.9 mm, 145 faces (baked)
FEATURE [App::Link] Link001  label="Pre_Right_Inner_Leg"
  LinkedObject = -> Body015
FEATURE [Part::Mirroring] Part__Mirroring001  label="Right_Inner_Leg"
  Base = (0,0,0)
  Normal = (0,0,1)
  Placement = pos=(53.7,-4.5,-19.5) rot=(0,-0.71,-0.71;3.14159rad)
  Source = -> Link001
FEATURE [App::Link] Link002  label="Pre_Right_Outer_Leg"
  LinkedObject = -> Body016
FEATURE [Part::Mirroring] Part__Mirroring002  label="Right_Outer_Leg"
  Base = (0,0,0)
  Normal = (0,0,1)
  Placement = pos=(53.7,-4.5,-19.5) rot=(0,0.71,0.71;3.14159rad)
  Source = -> Link002
FEATURE [App::Link] Link003  label="Pre_Right_Ankle"
  LinkedObject = -> Body017
FEATURE [Part::Mirroring] Part__Mirroring003  label="Right_Ankle"
  Base = (0,0,0)
  Normal = (0,0,1)
  Placement = pos=(53.7,-4.5,-19.5) rot=(0,-0.707107,-0.707107;3.14159rad)
  Source = -> Link003
FEATURE [App::Link] Link004  label="Pre_Right_Foot"
  LinkedObject = -> Body018
FEATURE [Part::Mirroring] Part__Mirroring004  label="Right_Foot"
  Base = (0,0,0)
  Normal = (0,0,1)
  Placement = pos=(53.7,-4.5,-19.5) rot=(0,-0.707107,-0.707107;3.14159rad)
  Source = -> Link004
